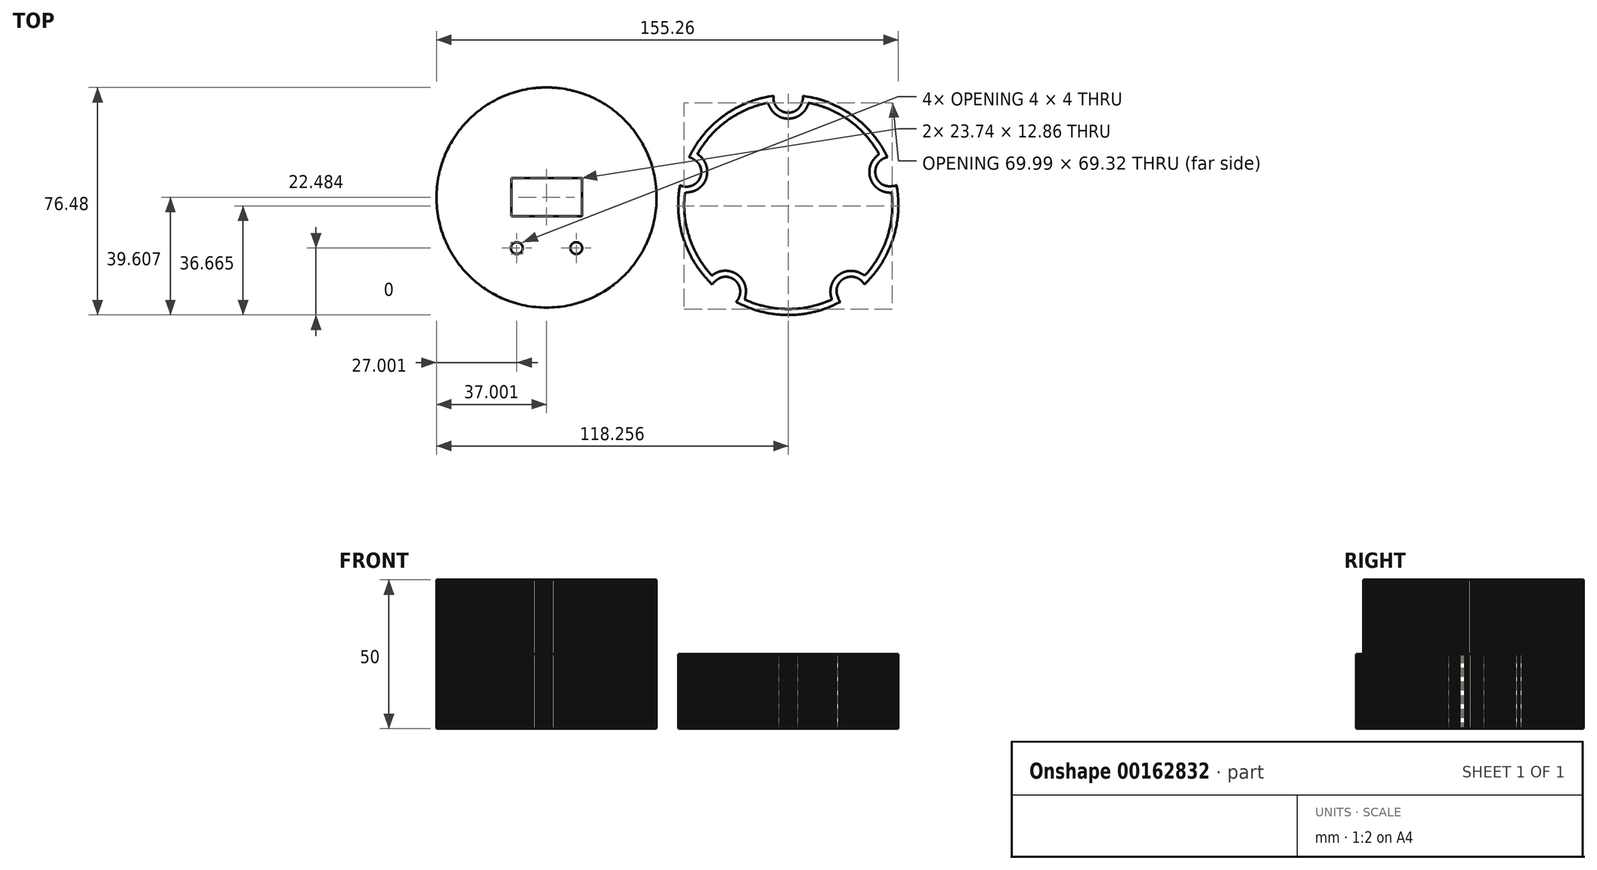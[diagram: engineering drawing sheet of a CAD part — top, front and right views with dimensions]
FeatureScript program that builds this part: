
annotation { "Feature Type Name" : "Feature", "Feature Type Description" : "" }
export const myFeature = defineFeature(function(context is Context, id is Id, definition is map)
    precondition{}
    {
        {
            var Q0;
            Q0=qCreatedBy(makeId("Top.planeOp"),FACE);
            var sketch = newSketch(context, id + "F0", { "sketchPlane" : qUnion([Q0])});
            skLineSegment(sketch, "E0", {"start": v(-51.65, -17.46) * mm, "end": v(-51.74, -17.42) * mm});
            skLineSegment(sketch, "E1", {"start": v(-51.74, -17.42) * mm, "end": v(-51.97, -17.23) * mm});
            skLineSegment(sketch, "E2", {"start": v(-51.97, -17.23) * mm, "end": v(-52.04, -17.17) * mm});
            skLineSegment(sketch, "E3", {"start": v(-52.04, -17.17) * mm, "end": v(-52.1, -17.1) * mm});
            skLineSegment(sketch, "E4", {"start": v(-52.1, -17.1) * mm, "end": v(-52.3, -16.87) * mm});
            skLineSegment(sketch, "E5", {"start": v(-52.3, -16.87) * mm, "end": v(-52.34, -16.78) * mm});
            skLineSegment(sketch, "E6", {"start": v(-52.34, -16.78) * mm, "end": v(-52.48, -16.52) * mm});
            skLineSegment(sketch, "E7", {"start": v(-52.48, -16.52) * mm, "end": v(-52.56, -16.24) * mm});
            skLineSegment(sketch, "E8", {"start": v(-52.56, -16.24) * mm, "end": v(-52.6, -16.15) * mm});
            skLineSegment(sketch, "E9", {"start": v(-52.6, -16.15) * mm, "end": v(-52.62, -15.85) * mm});
            skLineSegment(sketch, "E10", {"start": v(-52.62, -15.85) * mm, "end": v(-52.63, -15.76) * mm});
            skLineSegment(sketch, "E11", {"start": v(-52.63, -15.76) * mm, "end": v(-52.62, -15.66) * mm});
            skLineSegment(sketch, "E12", {"start": v(-52.62, -15.66) * mm, "end": v(-52.6, -15.37) * mm});
            skLineSegment(sketch, "E13", {"start": v(-52.6, -15.37) * mm, "end": v(-52.5, -15.08) * mm});
            skLineSegment(sketch, "E14", {"start": v(-52.5, -15.08) * mm, "end": v(-52.48, -15) * mm});
            skLineSegment(sketch, "E15", {"start": v(-52.48, -15) * mm, "end": v(-52.34, -14.73) * mm});
            skLineSegment(sketch, "E16", {"start": v(-52.34, -14.73) * mm, "end": v(-52.3, -14.64) * mm});
            skLineSegment(sketch, "E17", {"start": v(-52.3, -14.64) * mm, "end": v(-52.23, -14.57) * mm});
            skLineSegment(sketch, "E18", {"start": v(-52.23, -14.57) * mm, "end": v(-52.04, -14.34) * mm});
            skLineSegment(sketch, "E19", {"start": v(-52.04, -14.34) * mm, "end": v(-51.97, -14.28) * mm});
            skLineSegment(sketch, "E20", {"start": v(-51.97, -14.28) * mm, "end": v(-51.74, -14.1) * mm});
            skLineSegment(sketch, "E21", {"start": v(-51.74, -14.1) * mm, "end": v(-51.65, -14.05) * mm});
            skLineSegment(sketch, "E22", {"start": v(-51.65, -14.05) * mm, "end": v(-51.4, -13.9) * mm});
            skLineSegment(sketch, "E23", {"start": v(-51.4, -13.9) * mm, "end": v(-51.3, -13.88) * mm});
            skLineSegment(sketch, "E24", {"start": v(-51.3, -13.88) * mm, "end": v(-51.02, -13.8) * mm});
            skLineSegment(sketch, "E25", {"start": v(-51.02, -13.8) * mm, "end": v(-50.73, -13.77) * mm});
            skLineSegment(sketch, "E26", {"start": v(-50.73, -13.77) * mm, "end": v(-50.63, -13.76) * mm});
            skLineSegment(sketch, "E27", {"start": v(-50.63, -13.76) * mm, "end": v(-50.53, -13.77) * mm});
            skLineSegment(sketch, "E28", {"start": v(-50.53, -13.77) * mm, "end": v(-50.24, -13.8) * mm});
            skLineSegment(sketch, "E29", {"start": v(-50.24, -13.8) * mm, "end": v(-49.96, -13.88) * mm});
            skLineSegment(sketch, "E30", {"start": v(-49.96, -13.88) * mm, "end": v(-49.86, -13.9) * mm});
            skLineSegment(sketch, "E31", {"start": v(-49.86, -13.9) * mm, "end": v(-49.6, -14.05) * mm});
            skLineSegment(sketch, "E32", {"start": v(-49.6, -14.05) * mm, "end": v(-49.52, -14.1) * mm});
            skLineSegment(sketch, "E33", {"start": v(-49.52, -14.1) * mm, "end": v(-49.44, -14.15) * mm});
            skLineSegment(sketch, "E34", {"start": v(-49.44, -14.15) * mm, "end": v(-49.21, -14.34) * mm});
            skLineSegment(sketch, "E35", {"start": v(-49.21, -14.34) * mm, "end": v(-49.15, -14.42) * mm});
            skLineSegment(sketch, "E36", {"start": v(-49.15, -14.42) * mm, "end": v(-48.97, -14.64) * mm});
            skLineSegment(sketch, "E37", {"start": v(-48.97, -14.64) * mm, "end": v(-48.92, -14.73) * mm});
            skLineSegment(sketch, "E38", {"start": v(-48.92, -14.73) * mm, "end": v(-48.78, -15) * mm});
            skLineSegment(sketch, "E39", {"start": v(-48.78, -15) * mm, "end": v(-48.75, -15.08) * mm});
            skLineSegment(sketch, "E40", {"start": v(-48.75, -15.08) * mm, "end": v(-48.67, -15.37) * mm});
            skLineSegment(sketch, "E41", {"start": v(-48.67, -15.37) * mm, "end": v(-48.66, -15.46) * mm});
            skLineSegment(sketch, "E42", {"start": v(-48.66, -15.46) * mm, "end": v(-48.63, -15.76) * mm});
            skLineSegment(sketch, "E43", {"start": v(-48.63, -15.76) * mm, "end": v(-48.64, -15.85) * mm});
            skLineSegment(sketch, "E44", {"start": v(-48.64, -15.85) * mm, "end": v(-48.67, -16.15) * mm});
            skLineSegment(sketch, "E45", {"start": v(-48.67, -16.15) * mm, "end": v(-48.75, -16.43) * mm});
            skLineSegment(sketch, "E46", {"start": v(-48.75, -16.43) * mm, "end": v(-48.78, -16.52) * mm});
            skLineSegment(sketch, "E47", {"start": v(-48.78, -16.52) * mm, "end": v(-48.83, -16.6) * mm});
            skLineSegment(sketch, "E48", {"start": v(-48.83, -16.6) * mm, "end": v(-48.97, -16.87) * mm});
            skLineSegment(sketch, "E49", {"start": v(-48.97, -16.87) * mm, "end": v(-49.03, -16.95) * mm});
            skLineSegment(sketch, "E50", {"start": v(-49.03, -16.95) * mm, "end": v(-49.21, -17.17) * mm});
            skLineSegment(sketch, "E51", {"start": v(-49.21, -17.17) * mm, "end": v(-49.3, -17.23) * mm});
            skLineSegment(sketch, "E52", {"start": v(-49.3, -17.23) * mm, "end": v(-49.52, -17.42) * mm});
            skLineSegment(sketch, "E53", {"start": v(-49.52, -17.42) * mm, "end": v(-49.6, -17.47) * mm});
            skLineSegment(sketch, "E54", {"start": v(-49.6, -17.47) * mm, "end": v(-49.86, -17.6) * mm});
            skLineSegment(sketch, "E55", {"start": v(-49.86, -17.6) * mm, "end": v(-49.96, -17.63) * mm});
            skLineSegment(sketch, "E56", {"start": v(-49.96, -17.63) * mm, "end": v(-50.24, -17.72) * mm});
            skLineSegment(sketch, "E57", {"start": v(-50.24, -17.72) * mm, "end": v(-50.34, -17.73) * mm});
            skLineSegment(sketch, "E58", {"start": v(-50.34, -17.73) * mm, "end": v(-50.63, -17.76) * mm});
            skLineSegment(sketch, "E59", {"start": v(-50.63, -17.76) * mm, "end": v(-50.73, -17.75) * mm});
            skLineSegment(sketch, "E60", {"start": v(-50.73, -17.75) * mm, "end": v(-51.02, -17.72) * mm});
            skLineSegment(sketch, "E61", {"start": v(-51.02, -17.72) * mm, "end": v(-51.3, -17.63) * mm});
            skLineSegment(sketch, "E62", {"start": v(-51.3, -17.63) * mm, "end": v(-51.4, -17.6) * mm});
            skLineSegment(sketch, "E63", {"start": v(-51.4, -17.6) * mm, "end": v(-51.65, -17.46) * mm});
            skLineSegment(sketch, "E64", {"start": v(-31.65, -17.46) * mm, "end": v(-31.74, -17.42) * mm});
            skLineSegment(sketch, "E65", {"start": v(-31.74, -17.42) * mm, "end": v(-31.97, -17.23) * mm});
            skLineSegment(sketch, "E66", {"start": v(-31.97, -17.23) * mm, "end": v(-32.04, -17.17) * mm});
            skLineSegment(sketch, "E67", {"start": v(-32.04, -17.17) * mm, "end": v(-32.23, -16.95) * mm});
            skLineSegment(sketch, "E68", {"start": v(-32.23, -16.95) * mm, "end": v(-32.29, -16.87) * mm});
            skLineSegment(sketch, "E69", {"start": v(-32.29, -16.87) * mm, "end": v(-32.43, -16.6) * mm});
            skLineSegment(sketch, "E70", {"start": v(-32.43, -16.6) * mm, "end": v(-32.48, -16.52) * mm});
            skLineSegment(sketch, "E71", {"start": v(-32.48, -16.52) * mm, "end": v(-32.5, -16.43) * mm});
            skLineSegment(sketch, "E72", {"start": v(-32.5, -16.43) * mm, "end": v(-32.6, -16.15) * mm});
            skLineSegment(sketch, "E73", {"start": v(-32.6, -16.15) * mm, "end": v(-32.62, -15.85) * mm});
            skLineSegment(sketch, "E74", {"start": v(-32.62, -15.85) * mm, "end": v(-32.63, -15.76) * mm});
            skLineSegment(sketch, "E75", {"start": v(-32.63, -15.76) * mm, "end": v(-32.6, -15.46) * mm});
            skLineSegment(sketch, "E76", {"start": v(-32.6, -15.46) * mm, "end": v(-32.6, -15.37) * mm});
            skLineSegment(sketch, "E77", {"start": v(-32.6, -15.37) * mm, "end": v(-32.5, -15.08) * mm});
            skLineSegment(sketch, "E78", {"start": v(-32.5, -15.08) * mm, "end": v(-32.48, -15) * mm});
            skLineSegment(sketch, "E79", {"start": v(-32.48, -15) * mm, "end": v(-32.34, -14.73) * mm});
            skLineSegment(sketch, "E80", {"start": v(-32.34, -14.73) * mm, "end": v(-32.3, -14.64) * mm});
            skLineSegment(sketch, "E81", {"start": v(-32.3, -14.64) * mm, "end": v(-32.23, -14.57) * mm});
            skLineSegment(sketch, "E82", {"start": v(-32.23, -14.57) * mm, "end": v(-32.04, -14.34) * mm});
            skLineSegment(sketch, "E83", {"start": v(-32.04, -14.34) * mm, "end": v(-31.82, -14.15) * mm});
            skLineSegment(sketch, "E84", {"start": v(-31.82, -14.15) * mm, "end": v(-31.74, -14.1) * mm});
            skLineSegment(sketch, "E85", {"start": v(-31.74, -14.1) * mm, "end": v(-31.65, -14.05) * mm});
            skLineSegment(sketch, "E86", {"start": v(-31.65, -14.05) * mm, "end": v(-31.4, -13.9) * mm});
            skLineSegment(sketch, "E87", {"start": v(-31.4, -13.9) * mm, "end": v(-31.3, -13.88) * mm});
            skLineSegment(sketch, "E88", {"start": v(-31.3, -13.88) * mm, "end": v(-31.02, -13.8) * mm});
            skLineSegment(sketch, "E89", {"start": v(-31.02, -13.8) * mm, "end": v(-30.73, -13.77) * mm});
            skLineSegment(sketch, "E90", {"start": v(-30.73, -13.77) * mm, "end": v(-30.63, -13.76) * mm});
            skLineSegment(sketch, "E91", {"start": v(-30.63, -13.76) * mm, "end": v(-30.53, -13.77) * mm});
            skLineSegment(sketch, "E92", {"start": v(-30.53, -13.77) * mm, "end": v(-30.24, -13.8) * mm});
            skLineSegment(sketch, "E93", {"start": v(-30.24, -13.8) * mm, "end": v(-29.96, -13.88) * mm});
            skLineSegment(sketch, "E94", {"start": v(-29.96, -13.88) * mm, "end": v(-29.86, -13.9) * mm});
            skLineSegment(sketch, "E95", {"start": v(-29.86, -13.9) * mm, "end": v(-29.6, -14.05) * mm});
            skLineSegment(sketch, "E96", {"start": v(-29.6, -14.05) * mm, "end": v(-29.52, -14.1) * mm});
            skLineSegment(sketch, "E97", {"start": v(-29.52, -14.1) * mm, "end": v(-29.44, -14.15) * mm});
            skLineSegment(sketch, "E98", {"start": v(-29.44, -14.15) * mm, "end": v(-29.21, -14.34) * mm});
            skLineSegment(sketch, "E99", {"start": v(-29.21, -14.34) * mm, "end": v(-29.03, -14.57) * mm});
            skLineSegment(sketch, "E100", {"start": v(-29.03, -14.57) * mm, "end": v(-28.97, -14.64) * mm});
            skLineSegment(sketch, "E101", {"start": v(-28.97, -14.64) * mm, "end": v(-28.92, -14.73) * mm});
            skLineSegment(sketch, "E102", {"start": v(-28.92, -14.73) * mm, "end": v(-28.78, -15) * mm});
            skLineSegment(sketch, "E103", {"start": v(-28.78, -15) * mm, "end": v(-28.75, -15.08) * mm});
            skLineSegment(sketch, "E104", {"start": v(-28.75, -15.08) * mm, "end": v(-28.67, -15.37) * mm});
            skLineSegment(sketch, "E105", {"start": v(-28.67, -15.37) * mm, "end": v(-28.64, -15.66) * mm});
            skLineSegment(sketch, "E106", {"start": v(-28.64, -15.66) * mm, "end": v(-28.63, -15.76) * mm});
            skLineSegment(sketch, "E107", {"start": v(-28.63, -15.76) * mm, "end": v(-28.66, -16.05) * mm});
            skLineSegment(sketch, "E108", {"start": v(-28.66, -16.05) * mm, "end": v(-28.67, -16.15) * mm});
            skLineSegment(sketch, "E109", {"start": v(-28.67, -16.15) * mm, "end": v(-28.75, -16.43) * mm});
            skLineSegment(sketch, "E110", {"start": v(-28.75, -16.43) * mm, "end": v(-28.78, -16.52) * mm});
            skLineSegment(sketch, "E111", {"start": v(-28.78, -16.52) * mm, "end": v(-28.92, -16.78) * mm});
            skLineSegment(sketch, "E112", {"start": v(-28.92, -16.78) * mm, "end": v(-28.97, -16.87) * mm});
            skLineSegment(sketch, "E113", {"start": v(-28.97, -16.87) * mm, "end": v(-29.03, -16.94) * mm});
            skLineSegment(sketch, "E114", {"start": v(-29.03, -16.94) * mm, "end": v(-29.21, -17.17) * mm});
            skLineSegment(sketch, "E115", {"start": v(-29.21, -17.17) * mm, "end": v(-29.3, -17.23) * mm});
            skLineSegment(sketch, "E116", {"start": v(-29.3, -17.23) * mm, "end": v(-29.52, -17.42) * mm});
            skLineSegment(sketch, "E117", {"start": v(-29.52, -17.42) * mm, "end": v(-29.6, -17.46) * mm});
            skLineSegment(sketch, "E118", {"start": v(-29.6, -17.46) * mm, "end": v(-29.86, -17.6) * mm});
            skLineSegment(sketch, "E119", {"start": v(-29.86, -17.6) * mm, "end": v(-29.96, -17.63) * mm});
            skLineSegment(sketch, "E120", {"start": v(-29.96, -17.63) * mm, "end": v(-30.24, -17.72) * mm});
            skLineSegment(sketch, "E121", {"start": v(-30.24, -17.72) * mm, "end": v(-30.53, -17.75) * mm});
            skLineSegment(sketch, "E122", {"start": v(-30.53, -17.75) * mm, "end": v(-30.63, -17.76) * mm});
            skLineSegment(sketch, "E123", {"start": v(-30.63, -17.76) * mm, "end": v(-30.73, -17.75) * mm});
            skLineSegment(sketch, "E124", {"start": v(-30.73, -17.75) * mm, "end": v(-31.02, -17.72) * mm});
            skLineSegment(sketch, "E125", {"start": v(-31.02, -17.72) * mm, "end": v(-31.3, -17.63) * mm});
            skLineSegment(sketch, "E126", {"start": v(-31.3, -17.63) * mm, "end": v(-31.4, -17.6) * mm});
            skLineSegment(sketch, "E127", {"start": v(-31.4, -17.6) * mm, "end": v(-31.65, -17.46) * mm});
            skLineSegment(sketch, "E128", {"start": v(-28.76, 4.59) * mm, "end": v(-28.76, -5.07) * mm});
            skLineSegment(sketch, "E129", {"start": v(-28.76, -5.07) * mm, "end": v(-34.69, -5.07) * mm});
            skLineSegment(sketch, "E130", {"start": v(-34.69, -5.07) * mm, "end": v(-52.5, -5.07) * mm});
            skLineSegment(sketch, "E131", {"start": v(-52.5, -5.07) * mm, "end": v(-52.5, -1.85) * mm});
            skLineSegment(sketch, "E132", {"start": v(-52.5, -1.85) * mm, "end": v(-52.5, 7.8) * mm});
            skLineSegment(sketch, "E133", {"start": v(-52.5, 7.8) * mm, "end": v(-46.57, 7.8) * mm});
            skLineSegment(sketch, "E134", {"start": v(-46.57, 7.8) * mm, "end": v(-28.76, 7.8) * mm});
            skLineSegment(sketch, "E135", {"start": v(-28.76, 7.8) * mm, "end": v(-28.76, 4.59) * mm});
            skLineSegment(sketch, "E136", {"start": v(-68.54, -23.04) * mm, "end": v(-68, -23.65) * mm});
            skLineSegment(sketch, "E137", {"start": v(-68, -23.65) * mm, "end": v(-67.45, -24.25) * mm});
            skLineSegment(sketch, "E138", {"start": v(-67.45, -24.25) * mm, "end": v(-67.43, -24.27) * mm});
            skLineSegment(sketch, "E139", {"start": v(-67.43, -24.27) * mm, "end": v(-67.36, -24.34) * mm});
            skLineSegment(sketch, "E140", {"start": v(-67.36, -24.34) * mm, "end": v(-66.8, -24.92) * mm});
            skLineSegment(sketch, "E141", {"start": v(-66.8, -24.92) * mm, "end": v(-66.72, -25) * mm});
            skLineSegment(sketch, "E142", {"start": v(-66.72, -25) * mm, "end": v(-66.14, -25.55) * mm});
            skLineSegment(sketch, "E143", {"start": v(-66.14, -25.55) * mm, "end": v(-66.06, -25.63) * mm});
            skLineSegment(sketch, "E144", {"start": v(-66.06, -25.63) * mm, "end": v(-65.48, -26.17) * mm});
            skLineSegment(sketch, "E145", {"start": v(-65.48, -26.17) * mm, "end": v(-65.4, -26.24) * mm});
            skLineSegment(sketch, "E146", {"start": v(-65.4, -26.24) * mm, "end": v(-64.8, -26.77) * mm});
            skLineSegment(sketch, "E147", {"start": v(-64.8, -26.77) * mm, "end": v(-64.71, -26.84) * mm});
            skLineSegment(sketch, "E148", {"start": v(-64.71, -26.84) * mm, "end": v(-64.1, -27.36) * mm});
            skLineSegment(sketch, "E149", {"start": v(-64.1, -27.36) * mm, "end": v(-64.01, -27.43) * mm});
            skLineSegment(sketch, "E150", {"start": v(-64.01, -27.43) * mm, "end": v(-63.4, -27.92) * mm});
            skLineSegment(sketch, "E151", {"start": v(-63.4, -27.92) * mm, "end": v(-63.3, -28) * mm});
            skLineSegment(sketch, "E152", {"start": v(-63.3, -28) * mm, "end": v(-62.67, -28.47) * mm});
            skLineSegment(sketch, "E153", {"start": v(-62.67, -28.47) * mm, "end": v(-62.58, -28.54) * mm});
            skLineSegment(sketch, "E154", {"start": v(-62.58, -28.54) * mm, "end": v(-61.93, -29) * mm});
            skLineSegment(sketch, "E155", {"start": v(-61.93, -29) * mm, "end": v(-61.28, -29.46) * mm});
            skLineSegment(sketch, "E156", {"start": v(-61.28, -29.46) * mm, "end": v(-61.19, -29.52) * mm});
            skLineSegment(sketch, "E157", {"start": v(-61.19, -29.52) * mm, "end": v(-60.52, -29.95) * mm});
            skLineSegment(sketch, "E158", {"start": v(-60.52, -29.95) * mm, "end": v(-60.42, -30.02) * mm});
            skLineSegment(sketch, "E159", {"start": v(-60.42, -30.02) * mm, "end": v(-59.75, -30.43) * mm});
            skLineSegment(sketch, "E160", {"start": v(-59.75, -30.43) * mm, "end": v(-59.65, -30.5) * mm});
            skLineSegment(sketch, "E161", {"start": v(-59.65, -30.5) * mm, "end": v(-58.96, -30.9) * mm});
            skLineSegment(sketch, "E162", {"start": v(-58.96, -30.9) * mm, "end": v(-58.87, -30.95) * mm});
            skLineSegment(sketch, "E163", {"start": v(-58.87, -30.95) * mm, "end": v(-58.16, -31.34) * mm});
            skLineSegment(sketch, "E164", {"start": v(-58.16, -31.34) * mm, "end": v(-58.07, -31.39) * mm});
            skLineSegment(sketch, "E165", {"start": v(-58.07, -31.39) * mm, "end": v(-57.36, -31.76) * mm});
            skLineSegment(sketch, "E166", {"start": v(-57.36, -31.76) * mm, "end": v(-57.26, -31.8) * mm});
            skLineSegment(sketch, "E167", {"start": v(-57.26, -31.8) * mm, "end": v(-56.54, -32.16) * mm});
            skLineSegment(sketch, "E168", {"start": v(-56.54, -32.16) * mm, "end": v(-56.45, -32.2) * mm});
            skLineSegment(sketch, "E169", {"start": v(-56.45, -32.2) * mm, "end": v(-56.44, -32.2) * mm});
            skLineSegment(sketch, "E170", {"start": v(-56.44, -32.2) * mm, "end": v(-55.7, -32.55) * mm});
            skLineSegment(sketch, "E171", {"start": v(-55.7, -32.55) * mm, "end": v(-55.62, -32.58) * mm});
            skLineSegment(sketch, "E172", {"start": v(-55.62, -32.58) * mm, "end": v(-55.6, -32.59) * mm});
            skLineSegment(sketch, "E173", {"start": v(-55.6, -32.59) * mm, "end": v(-54.79, -32.94) * mm});
            skLineSegment(sketch, "E174", {"start": v(-54.79, -32.94) * mm, "end": v(-53.96, -33.27) * mm});
            skLineSegment(sketch, "E175", {"start": v(-53.96, -33.27) * mm, "end": v(-53.94, -33.28) * mm});
            skLineSegment(sketch, "E176", {"start": v(-53.94, -33.28) * mm, "end": v(-53.1, -33.59) * mm});
            skLineSegment(sketch, "E177", {"start": v(-53.1, -33.59) * mm, "end": v(-53.1, -33.6) * mm});
            skLineSegment(sketch, "E178", {"start": v(-53.1, -33.6) * mm, "end": v(-53.08, -33.6) * mm});
            skLineSegment(sketch, "E179", {"start": v(-53.08, -33.6) * mm, "end": v(-52.23, -33.89) * mm});
            skLineSegment(sketch, "E180", {"start": v(-52.23, -33.89) * mm, "end": v(-51.38, -34.16) * mm});
            skLineSegment(sketch, "E181", {"start": v(-51.38, -34.16) * mm, "end": v(-51.37, -34.16) * mm});
            skLineSegment(sketch, "E182", {"start": v(-51.37, -34.16) * mm, "end": v(-50.51, -34.41) * mm});
            skLineSegment(sketch, "E183", {"start": v(-50.51, -34.41) * mm, "end": v(-50.5, -34.42) * mm});
            skLineSegment(sketch, "E184", {"start": v(-50.5, -34.42) * mm, "end": v(-49.63, -34.64) * mm});
            skLineSegment(sketch, "E185", {"start": v(-49.63, -34.64) * mm, "end": v(-49.62, -34.65) * mm});
            skLineSegment(sketch, "E186", {"start": v(-49.62, -34.65) * mm, "end": v(-48.75, -34.85) * mm});
            skLineSegment(sketch, "E187", {"start": v(-48.75, -34.85) * mm, "end": v(-48.74, -34.86) * mm});
            skLineSegment(sketch, "E188", {"start": v(-48.74, -34.86) * mm, "end": v(-47.86, -35.04) * mm});
            skLineSegment(sketch, "E189", {"start": v(-47.86, -35.04) * mm, "end": v(-47.85, -35.04) * mm});
            skLineSegment(sketch, "E190", {"start": v(-47.85, -35.04) * mm, "end": v(-47.83, -35.05) * mm});
            skLineSegment(sketch, "E191", {"start": v(-47.83, -35.05) * mm, "end": v(-46.95, -35.21) * mm});
            skLineSegment(sketch, "E192", {"start": v(-46.95, -35.21) * mm, "end": v(-46.94, -35.21) * mm});
            skLineSegment(sketch, "E193", {"start": v(-46.94, -35.21) * mm, "end": v(-46.06, -35.36) * mm});
            skLineSegment(sketch, "E194", {"start": v(-46.06, -35.36) * mm, "end": v(-46.04, -35.36) * mm});
            skLineSegment(sketch, "E195", {"start": v(-46.04, -35.36) * mm, "end": v(-45.16, -35.48) * mm});
            skLineSegment(sketch, "E196", {"start": v(-45.16, -35.48) * mm, "end": v(-45.14, -35.48) * mm});
            skLineSegment(sketch, "E197", {"start": v(-45.14, -35.48) * mm, "end": v(-44.26, -35.58) * mm});
            skLineSegment(sketch, "E198", {"start": v(-44.26, -35.58) * mm, "end": v(-44.24, -35.58) * mm});
            skLineSegment(sketch, "E199", {"start": v(-44.24, -35.58) * mm, "end": v(-43.35, -35.66) * mm});
            skLineSegment(sketch, "E200", {"start": v(-43.35, -35.66) * mm, "end": v(-42.46, -35.71) * mm});
            skLineSegment(sketch, "E201", {"start": v(-42.46, -35.71) * mm, "end": v(-42.44, -35.71) * mm});
            skLineSegment(sketch, "E202", {"start": v(-42.44, -35.71) * mm, "end": v(-41.55, -35.74) * mm});
            skLineSegment(sketch, "E203", {"start": v(-41.55, -35.74) * mm, "end": v(-41.54, -35.74) * mm});
            skLineSegment(sketch, "E204", {"start": v(-41.54, -35.74) * mm, "end": v(-41.52, -35.74) * mm});
            skLineSegment(sketch, "E205", {"start": v(-41.52, -35.74) * mm, "end": v(-40.63, -35.76) * mm});
            skLineSegment(sketch, "E206", {"start": v(-40.63, -35.76) * mm, "end": v(-39.74, -35.74) * mm});
            skLineSegment(sketch, "E207", {"start": v(-39.74, -35.74) * mm, "end": v(-39.72, -35.74) * mm});
            skLineSegment(sketch, "E208", {"start": v(-39.72, -35.74) * mm, "end": v(-39.7, -35.74) * mm});
            skLineSegment(sketch, "E209", {"start": v(-39.7, -35.74) * mm, "end": v(-38.81, -35.71) * mm});
            skLineSegment(sketch, "E210", {"start": v(-38.81, -35.71) * mm, "end": v(-38.8, -35.71) * mm});
            skLineSegment(sketch, "E211", {"start": v(-38.8, -35.71) * mm, "end": v(-37.9, -35.66) * mm});
            skLineSegment(sketch, "E212", {"start": v(-37.9, -35.66) * mm, "end": v(-37.9, -35.65) * mm});
            skLineSegment(sketch, "E213", {"start": v(-37.9, -35.65) * mm, "end": v(-37, -35.58) * mm});
            skLineSegment(sketch, "E214", {"start": v(-37, -35.58) * mm, "end": v(-36.99, -35.58) * mm});
            skLineSegment(sketch, "E215", {"start": v(-36.99, -35.58) * mm, "end": v(-36.1, -35.48) * mm});
            skLineSegment(sketch, "E216", {"start": v(-36.1, -35.48) * mm, "end": v(-36.08, -35.48) * mm});
            skLineSegment(sketch, "E217", {"start": v(-36.08, -35.48) * mm, "end": v(-35.2, -35.36) * mm});
            skLineSegment(sketch, "E218", {"start": v(-35.2, -35.36) * mm, "end": v(-35.18, -35.35) * mm});
            skLineSegment(sketch, "E219", {"start": v(-35.18, -35.35) * mm, "end": v(-34.3, -35.21) * mm});
            skLineSegment(sketch, "E220", {"start": v(-34.3, -35.21) * mm, "end": v(-34.29, -35.2) * mm});
            skLineSegment(sketch, "E221", {"start": v(-34.29, -35.2) * mm, "end": v(-33.41, -35.04) * mm});
            skLineSegment(sketch, "E222", {"start": v(-33.41, -35.04) * mm, "end": v(-33.4, -35.04) * mm});
            skLineSegment(sketch, "E223", {"start": v(-33.4, -35.04) * mm, "end": v(-32.52, -34.86) * mm});
            skLineSegment(sketch, "E224", {"start": v(-32.52, -34.86) * mm, "end": v(-32.5, -34.85) * mm});
            skLineSegment(sketch, "E225", {"start": v(-32.5, -34.85) * mm, "end": v(-31.64, -34.65) * mm});
            skLineSegment(sketch, "E226", {"start": v(-31.64, -34.65) * mm, "end": v(-30.78, -34.42) * mm});
            skLineSegment(sketch, "E227", {"start": v(-30.78, -34.42) * mm, "end": v(-30.76, -34.42) * mm});
            skLineSegment(sketch, "E228", {"start": v(-30.76, -34.42) * mm, "end": v(-30.75, -34.41) * mm});
            skLineSegment(sketch, "E229", {"start": v(-30.75, -34.41) * mm, "end": v(-29.89, -34.16) * mm});
            skLineSegment(sketch, "E230", {"start": v(-29.89, -34.16) * mm, "end": v(-29.87, -34.16) * mm});
            skLineSegment(sketch, "E231", {"start": v(-29.87, -34.16) * mm, "end": v(-29.87, -34.16) * mm});
            skLineSegment(sketch, "E232", {"start": v(-29.87, -34.16) * mm, "end": v(-29.02, -33.89) * mm});
            skLineSegment(sketch, "E233", {"start": v(-29.02, -33.89) * mm, "end": v(-29.02, -33.89) * mm});
            skLineSegment(sketch, "E234", {"start": v(-29.02, -33.89) * mm, "end": v(-29, -33.88) * mm});
            skLineSegment(sketch, "E235", {"start": v(-29, -33.88) * mm, "end": v(-29, -33.88) * mm});
            skLineSegment(sketch, "E236", {"start": v(-29, -33.88) * mm, "end": v(-28.16, -33.6) * mm});
            skLineSegment(sketch, "E237", {"start": v(-28.16, -33.6) * mm, "end": v(-28.16, -33.6) * mm});
            skLineSegment(sketch, "E238", {"start": v(-28.16, -33.6) * mm, "end": v(-28.15, -33.59) * mm});
            skLineSegment(sketch, "E239", {"start": v(-28.15, -33.59) * mm, "end": v(-27.31, -33.28) * mm});
            skLineSegment(sketch, "E240", {"start": v(-27.31, -33.28) * mm, "end": v(-27.31, -33.28) * mm});
            skLineSegment(sketch, "E241", {"start": v(-27.31, -33.28) * mm, "end": v(-26.48, -32.95) * mm});
            skLineSegment(sketch, "E242", {"start": v(-26.48, -32.95) * mm, "end": v(-26.3, -32.87) * mm});
            skLineSegment(sketch, "E243", {"start": v(-26.3, -32.87) * mm, "end": v(-25.56, -32.55) * mm});
            skLineSegment(sketch, "E244", {"start": v(-25.56, -32.55) * mm, "end": v(-24.82, -32.2) * mm});
            skLineSegment(sketch, "E245", {"start": v(-24.82, -32.2) * mm, "end": v(-24.8, -32.2) * mm});
            skLineSegment(sketch, "E246", {"start": v(-24.8, -32.2) * mm, "end": v(-24.72, -32.16) * mm});
            skLineSegment(sketch, "E247", {"start": v(-24.72, -32.16) * mm, "end": v(-24, -31.8) * mm});
            skLineSegment(sketch, "E248", {"start": v(-24, -31.8) * mm, "end": v(-23.9, -31.76) * mm});
            skLineSegment(sketch, "E249", {"start": v(-23.9, -31.76) * mm, "end": v(-23.19, -31.39) * mm});
            skLineSegment(sketch, "E250", {"start": v(-23.19, -31.39) * mm, "end": v(-23.1, -31.34) * mm});
            skLineSegment(sketch, "E251", {"start": v(-23.1, -31.34) * mm, "end": v(-22.4, -30.95) * mm});
            skLineSegment(sketch, "E252", {"start": v(-22.4, -30.95) * mm, "end": v(-22.3, -30.9) * mm});
            skLineSegment(sketch, "E253", {"start": v(-22.3, -30.9) * mm, "end": v(-21.6, -30.5) * mm});
            skLineSegment(sketch, "E254", {"start": v(-21.6, -30.5) * mm, "end": v(-21.51, -30.43) * mm});
            skLineSegment(sketch, "E255", {"start": v(-21.51, -30.43) * mm, "end": v(-20.83, -30.02) * mm});
            skLineSegment(sketch, "E256", {"start": v(-20.83, -30.02) * mm, "end": v(-20.74, -29.95) * mm});
            skLineSegment(sketch, "E257", {"start": v(-20.74, -29.95) * mm, "end": v(-20.07, -29.52) * mm});
            skLineSegment(sketch, "E258", {"start": v(-20.07, -29.52) * mm, "end": v(-19.98, -29.46) * mm});
            skLineSegment(sketch, "E259", {"start": v(-19.98, -29.46) * mm, "end": v(-19.32, -29) * mm});
            skLineSegment(sketch, "E260", {"start": v(-19.32, -29) * mm, "end": v(-19.23, -28.94) * mm});
            skLineSegment(sketch, "E261", {"start": v(-19.23, -28.94) * mm, "end": v(-18.59, -28.47) * mm});
            skLineSegment(sketch, "E262", {"start": v(-18.59, -28.47) * mm, "end": v(-17.95, -28) * mm});
            skLineSegment(sketch, "E263", {"start": v(-17.95, -28) * mm, "end": v(-17.87, -27.92) * mm});
            skLineSegment(sketch, "E264", {"start": v(-17.87, -27.92) * mm, "end": v(-17.24, -27.43) * mm});
            skLineSegment(sketch, "E265", {"start": v(-17.24, -27.43) * mm, "end": v(-17.16, -27.36) * mm});
            skLineSegment(sketch, "E266", {"start": v(-17.16, -27.36) * mm, "end": v(-16.55, -26.84) * mm});
            skLineSegment(sketch, "E267", {"start": v(-16.55, -26.84) * mm, "end": v(-16.46, -26.77) * mm});
            skLineSegment(sketch, "E268", {"start": v(-16.46, -26.77) * mm, "end": v(-15.86, -26.24) * mm});
            skLineSegment(sketch, "E269", {"start": v(-15.86, -26.24) * mm, "end": v(-15.78, -26.17) * mm});
            skLineSegment(sketch, "E270", {"start": v(-15.78, -26.17) * mm, "end": v(-15.2, -25.63) * mm});
            skLineSegment(sketch, "E271", {"start": v(-15.2, -25.63) * mm, "end": v(-15.12, -25.55) * mm});
            skLineSegment(sketch, "E272", {"start": v(-15.12, -25.55) * mm, "end": v(-14.54, -25) * mm});
            skLineSegment(sketch, "E273", {"start": v(-14.54, -25) * mm, "end": v(-14.47, -24.92) * mm});
            skLineSegment(sketch, "E274", {"start": v(-14.47, -24.92) * mm, "end": v(-13.9, -24.34) * mm});
            skLineSegment(sketch, "E275", {"start": v(-13.9, -24.34) * mm, "end": v(-13.83, -24.27) * mm});
            skLineSegment(sketch, "E276", {"start": v(-13.83, -24.27) * mm, "end": v(-13.8, -24.24) * mm});
            skLineSegment(sketch, "E277", {"start": v(-13.8, -24.24) * mm, "end": v(-13.26, -23.65) * mm});
            skLineSegment(sketch, "E278", {"start": v(-13.26, -23.65) * mm, "end": v(-12.72, -23.04) * mm});
            skLineSegment(sketch, "E279", {"start": v(-12.72, -23.04) * mm, "end": v(-12.61, -22.92) * mm});
            skLineSegment(sketch, "E280", {"start": v(-12.61, -22.92) * mm, "end": v(-12.04, -22.24) * mm});
            skLineSegment(sketch, "E281", {"start": v(-12.04, -22.24) * mm, "end": v(-12.03, -22.23) * mm});
            skLineSegment(sketch, "E282", {"start": v(-12.03, -22.23) * mm, "end": v(-11.47, -21.53) * mm});
            skLineSegment(sketch, "E283", {"start": v(-11.47, -21.53) * mm, "end": v(-11.46, -21.52) * mm});
            skLineSegment(sketch, "E284", {"start": v(-11.46, -21.52) * mm, "end": v(-10.92, -20.8) * mm});
            skLineSegment(sketch, "E285", {"start": v(-10.92, -20.8) * mm, "end": v(-10.91, -20.8) * mm});
            skLineSegment(sketch, "E286", {"start": v(-10.91, -20.8) * mm, "end": v(-10.39, -20.07) * mm});
            skLineSegment(sketch, "E287", {"start": v(-10.39, -20.07) * mm, "end": v(-10.38, -20.06) * mm});
            skLineSegment(sketch, "E288", {"start": v(-10.38, -20.06) * mm, "end": v(-9.87, -19.32) * mm});
            skLineSegment(sketch, "E289", {"start": v(-9.87, -19.32) * mm, "end": v(-9.86, -19.31) * mm});
            skLineSegment(sketch, "E290", {"start": v(-9.86, -19.31) * mm, "end": v(-9.38, -18.56) * mm});
            skLineSegment(sketch, "E291", {"start": v(-9.38, -18.56) * mm, "end": v(-9.37, -18.55) * mm});
            skLineSegment(sketch, "E292", {"start": v(-9.37, -18.55) * mm, "end": v(-8.9, -17.8) * mm});
            skLineSegment(sketch, "E293", {"start": v(-8.9, -17.8) * mm, "end": v(-8.9, -17.78) * mm});
            skLineSegment(sketch, "E294", {"start": v(-8.9, -17.78) * mm, "end": v(-8.44, -17) * mm});
            skLineSegment(sketch, "E295", {"start": v(-8.44, -17) * mm, "end": v(-8.44, -17) * mm});
            skLineSegment(sketch, "E296", {"start": v(-8.44, -17) * mm, "end": v(-8, -16.21) * mm});
            skLineSegment(sketch, "E297", {"start": v(-8, -16.21) * mm, "end": v(-8, -16.2) * mm});
            skLineSegment(sketch, "E298", {"start": v(-8, -16.2) * mm, "end": v(-8, -16.18) * mm});
            skLineSegment(sketch, "E299", {"start": v(-8, -16.18) * mm, "end": v(-7.58, -15.4) * mm});
            skLineSegment(sketch, "E300", {"start": v(-7.58, -15.4) * mm, "end": v(-7.19, -14.59) * mm});
            skLineSegment(sketch, "E301", {"start": v(-7.19, -14.59) * mm, "end": v(-7.18, -14.58) * mm});
            skLineSegment(sketch, "E302", {"start": v(-7.18, -14.58) * mm, "end": v(-6.8, -13.76) * mm});
            skLineSegment(sketch, "E303", {"start": v(-6.8, -13.76) * mm, "end": v(-6.8, -13.75) * mm});
            skLineSegment(sketch, "E304", {"start": v(-6.8, -13.75) * mm, "end": v(-6.45, -12.93) * mm});
            skLineSegment(sketch, "E305", {"start": v(-6.45, -12.93) * mm, "end": v(-6.45, -12.92) * mm});
            skLineSegment(sketch, "E306", {"start": v(-6.45, -12.92) * mm, "end": v(-6.44, -12.9) * mm});
            skLineSegment(sketch, "E307", {"start": v(-6.44, -12.9) * mm, "end": v(-6.1, -12.07) * mm});
            skLineSegment(sketch, "E308", {"start": v(-6.1, -12.07) * mm, "end": v(-6.1, -12.06) * mm});
            skLineSegment(sketch, "E309", {"start": v(-6.1, -12.06) * mm, "end": v(-5.8, -11.22) * mm});
            skLineSegment(sketch, "E310", {"start": v(-5.8, -11.22) * mm, "end": v(-5.5, -10.38) * mm});
            skLineSegment(sketch, "E311", {"start": v(-5.5, -10.38) * mm, "end": v(-5.5, -10.36) * mm});
            skLineSegment(sketch, "E312", {"start": v(-5.5, -10.36) * mm, "end": v(-5.23, -9.51) * mm});
            skLineSegment(sketch, "E313", {"start": v(-5.23, -9.51) * mm, "end": v(-5.22, -9.5) * mm});
            skLineSegment(sketch, "E314", {"start": v(-5.22, -9.5) * mm, "end": v(-5.22, -9.48) * mm});
            skLineSegment(sketch, "E315", {"start": v(-5.22, -9.48) * mm, "end": v(-4.97, -8.62) * mm});
            skLineSegment(sketch, "E316", {"start": v(-4.97, -8.62) * mm, "end": v(-4.97, -8.6) * mm});
            skLineSegment(sketch, "E317", {"start": v(-4.97, -8.6) * mm, "end": v(-4.74, -7.75) * mm});
            skLineSegment(sketch, "E318", {"start": v(-4.74, -7.75) * mm, "end": v(-4.53, -6.88) * mm});
            skLineSegment(sketch, "E319", {"start": v(-4.53, -6.88) * mm, "end": v(-4.53, -6.86) * mm});
            skLineSegment(sketch, "E320", {"start": v(-4.53, -6.86) * mm, "end": v(-4.34, -5.99) * mm});
            skLineSegment(sketch, "E321", {"start": v(-4.34, -5.99) * mm, "end": v(-4.34, -5.97) * mm});
            skLineSegment(sketch, "E322", {"start": v(-4.34, -5.97) * mm, "end": v(-4.34, -5.96) * mm});
            skLineSegment(sketch, "E323", {"start": v(-4.34, -5.96) * mm, "end": v(-4.17, -5.08) * mm});
            skLineSegment(sketch, "E324", {"start": v(-4.17, -5.08) * mm, "end": v(-4.03, -4.2) * mm});
            skLineSegment(sketch, "E325", {"start": v(-4.03, -4.2) * mm, "end": v(-4.03, -4.18) * mm});
            skLineSegment(sketch, "E326", {"start": v(-4.03, -4.18) * mm, "end": v(-3.9, -3.3) * mm});
            skLineSegment(sketch, "E327", {"start": v(-3.9, -3.3) * mm, "end": v(-3.9, -3.28) * mm});
            skLineSegment(sketch, "E328", {"start": v(-3.9, -3.28) * mm, "end": v(-3.9, -3.27) * mm});
            skLineSegment(sketch, "E329", {"start": v(-3.9, -3.27) * mm, "end": v(-3.8, -2.38) * mm});
            skLineSegment(sketch, "E330", {"start": v(-3.8, -2.38) * mm, "end": v(-3.8, -2.37) * mm});
            skLineSegment(sketch, "E331", {"start": v(-3.8, -2.37) * mm, "end": v(-3.73, -1.48) * mm});
            skLineSegment(sketch, "E332", {"start": v(-3.73, -1.48) * mm, "end": v(-3.67, -0.59) * mm});
            skLineSegment(sketch, "E333", {"start": v(-3.67, -0.59) * mm, "end": v(-3.67, -0.54) * mm});
            skLineSegment(sketch, "E334", {"start": v(-3.67, -0.54) * mm, "end": v(-3.64, 0.35) * mm});
            skLineSegment(sketch, "E335", {"start": v(-3.64, 0.35) * mm, "end": v(-3.63, 1.24) * mm});
            skLineSegment(sketch, "E336", {"start": v(-3.63, 1.24) * mm, "end": v(-3.63, 1.25) * mm});
            skLineSegment(sketch, "E337", {"start": v(-3.63, 1.25) * mm, "end": v(-3.63, 1.25) * mm});
            skLineSegment(sketch, "E338", {"start": v(-3.63, 1.25) * mm, "end": v(-3.63, 1.26) * mm});
            skLineSegment(sketch, "E339", {"start": v(-3.63, 1.26) * mm, "end": v(-3.64, 2.15) * mm});
            skLineSegment(sketch, "E340", {"start": v(-3.64, 2.15) * mm, "end": v(-3.64, 2.15) * mm});
            skLineSegment(sketch, "E341", {"start": v(-3.64, 2.15) * mm, "end": v(-3.64, 2.16) * mm});
            skLineSegment(sketch, "E342", {"start": v(-3.64, 2.16) * mm, "end": v(-3.64, 2.17) * mm});
            skLineSegment(sketch, "E343", {"start": v(-3.64, 2.17) * mm, "end": v(-3.67, 3.06) * mm});
            skLineSegment(sketch, "E344", {"start": v(-3.67, 3.06) * mm, "end": v(-3.67, 3.06) * mm});
            skLineSegment(sketch, "E345", {"start": v(-3.67, 3.06) * mm, "end": v(-3.73, 3.95) * mm});
            skLineSegment(sketch, "E346", {"start": v(-3.73, 3.95) * mm, "end": v(-3.75, 4.16) * mm});
            skLineSegment(sketch, "E347", {"start": v(-3.75, 4.16) * mm, "end": v(-3.82, 4.97) * mm});
            skLineSegment(sketch, "E348", {"start": v(-3.82, 4.97) * mm, "end": v(-3.9, 5.78) * mm});
            skLineSegment(sketch, "E349", {"start": v(-3.9, 5.78) * mm, "end": v(-3.92, 5.87) * mm});
            skLineSegment(sketch, "E350", {"start": v(-3.92, 5.87) * mm, "end": v(-4.03, 6.67) * mm});
            skLineSegment(sketch, "E351", {"start": v(-4.03, 6.67) * mm, "end": v(-4.05, 6.77) * mm});
            skLineSegment(sketch, "E352", {"start": v(-4.05, 6.77) * mm, "end": v(-4.17, 7.57) * mm});
            skLineSegment(sketch, "E353", {"start": v(-4.17, 7.57) * mm, "end": v(-4.2, 7.67) * mm});
            skLineSegment(sketch, "E354", {"start": v(-4.2, 7.67) * mm, "end": v(-4.34, 8.46) * mm});
            skLineSegment(sketch, "E355", {"start": v(-4.34, 8.46) * mm, "end": v(-4.36, 8.57) * mm});
            skLineSegment(sketch, "E356", {"start": v(-4.36, 8.57) * mm, "end": v(-4.53, 9.35) * mm});
            skLineSegment(sketch, "E357", {"start": v(-4.53, 9.35) * mm, "end": v(-4.55, 9.46) * mm});
            skLineSegment(sketch, "E358", {"start": v(-4.55, 9.46) * mm, "end": v(-4.74, 10.23) * mm});
            skLineSegment(sketch, "E359", {"start": v(-4.74, 10.23) * mm, "end": v(-4.77, 10.34) * mm});
            skLineSegment(sketch, "E360", {"start": v(-4.77, 10.34) * mm, "end": v(-4.97, 11.11) * mm});
            skLineSegment(sketch, "E361", {"start": v(-4.97, 11.11) * mm, "end": v(-5, 11.22) * mm});
            skLineSegment(sketch, "E362", {"start": v(-5, 11.22) * mm, "end": v(-5.22, 11.99) * mm});
            skLineSegment(sketch, "E363", {"start": v(-5.22, 11.99) * mm, "end": v(-5.26, 12.1) * mm});
            skLineSegment(sketch, "E364", {"start": v(-5.26, 12.1) * mm, "end": v(-5.5, 12.85) * mm});
            skLineSegment(sketch, "E365", {"start": v(-5.5, 12.85) * mm, "end": v(-5.76, 13.6) * mm});
            skLineSegment(sketch, "E366", {"start": v(-5.76, 13.6) * mm, "end": v(-5.8, 13.7) * mm});
            skLineSegment(sketch, "E367", {"start": v(-5.8, 13.7) * mm, "end": v(-6.07, 14.46) * mm});
            skLineSegment(sketch, "E368", {"start": v(-6.07, 14.46) * mm, "end": v(-6.1, 14.56) * mm});
            skLineSegment(sketch, "E369", {"start": v(-6.1, 14.56) * mm, "end": v(-6.4, 15.3) * mm});
            skLineSegment(sketch, "E370", {"start": v(-6.4, 15.3) * mm, "end": v(-6.45, 15.4) * mm});
            skLineSegment(sketch, "E371", {"start": v(-6.45, 15.4) * mm, "end": v(-6.76, 16.14) * mm});
            skLineSegment(sketch, "E372", {"start": v(-6.76, 16.14) * mm, "end": v(-6.8, 16.24) * mm});
            skLineSegment(sketch, "E373", {"start": v(-6.8, 16.24) * mm, "end": v(-7.14, 16.97) * mm});
            skLineSegment(sketch, "E374", {"start": v(-7.14, 16.97) * mm, "end": v(-7.18, 17.06) * mm});
            skLineSegment(sketch, "E375", {"start": v(-7.18, 17.06) * mm, "end": v(-7.53, 17.79) * mm});
            skLineSegment(sketch, "E376", {"start": v(-7.53, 17.79) * mm, "end": v(-7.58, 17.88) * mm});
            skLineSegment(sketch, "E377", {"start": v(-7.58, 17.88) * mm, "end": v(-7.95, 18.6) * mm});
            skLineSegment(sketch, "E378", {"start": v(-7.95, 18.6) * mm, "end": v(-8, 18.69) * mm});
            skLineSegment(sketch, "E379", {"start": v(-8, 18.69) * mm, "end": v(-8.39, 19.4) * mm});
            skLineSegment(sketch, "E380", {"start": v(-8.39, 19.4) * mm, "end": v(-8.8, 20.1) * mm});
            skLineSegment(sketch, "E381", {"start": v(-8.8, 20.1) * mm, "end": v(-8.87, 20.23) * mm});
            skLineSegment(sketch, "E382", {"start": v(-8.87, 20.23) * mm, "end": v(-8.9, 20.27) * mm});
            skLineSegment(sketch, "E383", {"start": v(-8.9, 20.27) * mm, "end": v(-8.9, 20.28) * mm});
            skLineSegment(sketch, "E384", {"start": v(-8.9, 20.28) * mm, "end": v(-9.37, 21.04) * mm});
            skLineSegment(sketch, "E385", {"start": v(-9.37, 21.04) * mm, "end": v(-9.86, 21.79) * mm});
            skLineSegment(sketch, "E386", {"start": v(-9.86, 21.79) * mm, "end": v(-9.86, 21.8) * mm});
            skLineSegment(sketch, "E387", {"start": v(-9.86, 21.8) * mm, "end": v(-10.37, 22.54) * mm});
            skLineSegment(sketch, "E388", {"start": v(-10.37, 22.54) * mm, "end": v(-10.38, 22.55) * mm});
            skLineSegment(sketch, "E389", {"start": v(-10.38, 22.55) * mm, "end": v(-10.9, 23.27) * mm});
            skLineSegment(sketch, "E390", {"start": v(-10.9, 23.27) * mm, "end": v(-10.91, 23.29) * mm});
            skLineSegment(sketch, "E391", {"start": v(-10.91, 23.29) * mm, "end": v(-11.45, 24) * mm});
            skLineSegment(sketch, "E392", {"start": v(-11.45, 24) * mm, "end": v(-11.46, 24) * mm});
            skLineSegment(sketch, "E393", {"start": v(-11.46, 24) * mm, "end": v(-12.02, 24.7) * mm});
            skLineSegment(sketch, "E394", {"start": v(-12.02, 24.7) * mm, "end": v(-12.03, 24.72) * mm});
            skLineSegment(sketch, "E395", {"start": v(-12.03, 24.72) * mm, "end": v(-12.6, 25.4) * mm});
            skLineSegment(sketch, "E396", {"start": v(-12.6, 25.4) * mm, "end": v(-12.61, 25.41) * mm});
            skLineSegment(sketch, "E397", {"start": v(-12.61, 25.41) * mm, "end": v(-13.2, 26.08) * mm});
            skLineSegment(sketch, "E398", {"start": v(-13.2, 26.08) * mm, "end": v(-13.21, 26.1) * mm});
            skLineSegment(sketch, "E399", {"start": v(-13.21, 26.1) * mm, "end": v(-13.82, 26.75) * mm});
            skLineSegment(sketch, "E400", {"start": v(-13.82, 26.75) * mm, "end": v(-13.83, 26.76) * mm});
            skLineSegment(sketch, "E401", {"start": v(-13.83, 26.76) * mm, "end": v(-14.46, 27.4) * mm});
            skLineSegment(sketch, "E402", {"start": v(-14.46, 27.4) * mm, "end": v(-14.47, 27.4) * mm});
            skLineSegment(sketch, "E403", {"start": v(-14.47, 27.4) * mm, "end": v(-15.1, 28.03) * mm});
            skLineSegment(sketch, "E404", {"start": v(-15.1, 28.03) * mm, "end": v(-15.12, 28.04) * mm});
            skLineSegment(sketch, "E405", {"start": v(-15.12, 28.04) * mm, "end": v(-15.77, 28.65) * mm});
            skLineSegment(sketch, "E406", {"start": v(-15.77, 28.65) * mm, "end": v(-15.78, 28.66) * mm});
            skLineSegment(sketch, "E407", {"start": v(-15.78, 28.66) * mm, "end": v(-16.45, 29.25) * mm});
            skLineSegment(sketch, "E408", {"start": v(-16.45, 29.25) * mm, "end": v(-16.46, 29.26) * mm});
            skLineSegment(sketch, "E409", {"start": v(-16.46, 29.26) * mm, "end": v(-17.14, 29.84) * mm});
            skLineSegment(sketch, "E410", {"start": v(-17.14, 29.84) * mm, "end": v(-17.16, 29.85) * mm});
            skLineSegment(sketch, "E411", {"start": v(-17.16, 29.85) * mm, "end": v(-17.85, 30.4) * mm});
            skLineSegment(sketch, "E412", {"start": v(-17.85, 30.4) * mm, "end": v(-17.87, 30.41) * mm});
            skLineSegment(sketch, "E413", {"start": v(-17.87, 30.41) * mm, "end": v(-17.88, 30.42) * mm});
            skLineSegment(sketch, "E414", {"start": v(-17.88, 30.42) * mm, "end": v(-18.59, 30.96) * mm});
            skLineSegment(sketch, "E415", {"start": v(-18.59, 30.96) * mm, "end": v(-18.6, 30.97) * mm});
            skLineSegment(sketch, "E416", {"start": v(-18.6, 30.97) * mm, "end": v(-19.32, 31.5) * mm});
            skLineSegment(sketch, "E417", {"start": v(-19.32, 31.5) * mm, "end": v(-20.06, 32) * mm});
            skLineSegment(sketch, "E418", {"start": v(-20.06, 32) * mm, "end": v(-20.07, 32) * mm});
            skLineSegment(sketch, "E419", {"start": v(-20.07, 32) * mm, "end": v(-20.82, 32.5) * mm});
            skLineSegment(sketch, "E420", {"start": v(-20.82, 32.5) * mm, "end": v(-20.83, 32.5) * mm});
            skLineSegment(sketch, "E421", {"start": v(-20.83, 32.5) * mm, "end": v(-20.85, 32.51) * mm});
            skLineSegment(sketch, "E422", {"start": v(-20.85, 32.51) * mm, "end": v(-21.6, 32.98) * mm});
            skLineSegment(sketch, "E423", {"start": v(-21.6, 32.98) * mm, "end": v(-22.38, 33.43) * mm});
            skLineSegment(sketch, "E424", {"start": v(-22.38, 33.43) * mm, "end": v(-22.4, 33.44) * mm});
            skLineSegment(sketch, "E425", {"start": v(-22.4, 33.44) * mm, "end": v(-23.17, 33.87) * mm});
            skLineSegment(sketch, "E426", {"start": v(-23.17, 33.87) * mm, "end": v(-23.19, 33.88) * mm});
            skLineSegment(sketch, "E427", {"start": v(-23.19, 33.88) * mm, "end": v(-23.98, 34.29) * mm});
            skLineSegment(sketch, "E428", {"start": v(-23.98, 34.29) * mm, "end": v(-24, 34.3) * mm});
            skLineSegment(sketch, "E429", {"start": v(-24, 34.3) * mm, "end": v(-24.8, 34.69) * mm});
            skLineSegment(sketch, "E430", {"start": v(-24.8, 34.69) * mm, "end": v(-24.8, 34.7) * mm});
            skLineSegment(sketch, "E431", {"start": v(-24.8, 34.7) * mm, "end": v(-25.62, 35.06) * mm});
            skLineSegment(sketch, "E432", {"start": v(-25.62, 35.06) * mm, "end": v(-25.64, 35.07) * mm});
            skLineSegment(sketch, "E433", {"start": v(-25.64, 35.07) * mm, "end": v(-26.46, 35.42) * mm});
            skLineSegment(sketch, "E434", {"start": v(-26.46, 35.42) * mm, "end": v(-26.47, 35.43) * mm});
            skLineSegment(sketch, "E435", {"start": v(-26.47, 35.43) * mm, "end": v(-27.3, 35.76) * mm});
            skLineSegment(sketch, "E436", {"start": v(-27.3, 35.76) * mm, "end": v(-27.31, 35.77) * mm});
            skLineSegment(sketch, "E437", {"start": v(-27.31, 35.77) * mm, "end": v(-27.34, 35.78) * mm});
            skLineSegment(sketch, "E438", {"start": v(-27.34, 35.78) * mm, "end": v(-28.18, 36.09) * mm});
            skLineSegment(sketch, "E439", {"start": v(-28.18, 36.09) * mm, "end": v(-29.02, 36.38) * mm});
            skLineSegment(sketch, "E440", {"start": v(-29.02, 36.38) * mm, "end": v(-29.02, 36.38) * mm});
            skLineSegment(sketch, "E441", {"start": v(-29.02, 36.38) * mm, "end": v(-29.03, 36.38) * mm});
            skLineSegment(sketch, "E442", {"start": v(-29.03, 36.38) * mm, "end": v(-29.04, 36.38) * mm});
            skLineSegment(sketch, "E443", {"start": v(-29.04, 36.38) * mm, "end": v(-29.04, 36.38) * mm});
            skLineSegment(sketch, "E444", {"start": v(-29.04, 36.38) * mm, "end": v(-29.89, 36.65) * mm});
            skLineSegment(sketch, "E445", {"start": v(-29.89, 36.65) * mm, "end": v(-29.9, 36.65) * mm});
            skLineSegment(sketch, "E446", {"start": v(-29.9, 36.65) * mm, "end": v(-29.9, 36.66) * mm});
            skLineSegment(sketch, "E447", {"start": v(-29.9, 36.66) * mm, "end": v(-29.9, 36.66) * mm});
            skLineSegment(sketch, "E448", {"start": v(-29.9, 36.66) * mm, "end": v(-30.76, 36.9) * mm});
            skLineSegment(sketch, "E449", {"start": v(-30.76, 36.9) * mm, "end": v(-30.77, 36.9) * mm});
            skLineSegment(sketch, "E450", {"start": v(-30.77, 36.9) * mm, "end": v(-31.63, 37.13) * mm});
            skLineSegment(sketch, "E451", {"start": v(-31.63, 37.13) * mm, "end": v(-31.85, 37.18) * mm});
            skLineSegment(sketch, "E452", {"start": v(-31.85, 37.18) * mm, "end": v(-32.64, 37.37) * mm});
            skLineSegment(sketch, "E453", {"start": v(-32.64, 37.37) * mm, "end": v(-33.43, 37.54) * mm});
            skLineSegment(sketch, "E454", {"start": v(-33.43, 37.54) * mm, "end": v(-33.5, 37.55) * mm});
            skLineSegment(sketch, "E455", {"start": v(-33.5, 37.55) * mm, "end": v(-34.3, 37.7) * mm});
            skLineSegment(sketch, "E456", {"start": v(-34.3, 37.7) * mm, "end": v(-34.4, 37.72) * mm});
            skLineSegment(sketch, "E457", {"start": v(-34.4, 37.72) * mm, "end": v(-35.2, 37.84) * mm});
            skLineSegment(sketch, "E458", {"start": v(-35.2, 37.84) * mm, "end": v(-35.3, 37.86) * mm});
            skLineSegment(sketch, "E459", {"start": v(-35.3, 37.86) * mm, "end": v(-36.1, 37.97) * mm});
            skLineSegment(sketch, "E460", {"start": v(-36.1, 37.97) * mm, "end": v(-36.2, 37.98) * mm});
            skLineSegment(sketch, "E461", {"start": v(-36.2, 37.98) * mm, "end": v(-37, 38.07) * mm});
            skLineSegment(sketch, "E462", {"start": v(-37, 38.07) * mm, "end": v(-37.11, 38.08) * mm});
            skLineSegment(sketch, "E463", {"start": v(-37.11, 38.08) * mm, "end": v(-37.9, 38.14) * mm});
            skLineSegment(sketch, "E464", {"start": v(-37.9, 38.14) * mm, "end": v(-38.02, 38.15) * mm});
            skLineSegment(sketch, "E465", {"start": v(-38.02, 38.15) * mm, "end": v(-38.81, 38.2) * mm});
            skLineSegment(sketch, "E466", {"start": v(-38.81, 38.2) * mm, "end": v(-38.93, 38.2) * mm});
            skLineSegment(sketch, "E467", {"start": v(-38.93, 38.2) * mm, "end": v(-39.72, 38.23) * mm});
            skLineSegment(sketch, "E468", {"start": v(-39.72, 38.23) * mm, "end": v(-39.83, 38.23) * mm});
            skLineSegment(sketch, "E469", {"start": v(-39.83, 38.23) * mm, "end": v(-40.63, 38.24) * mm});
            skLineSegment(sketch, "E470", {"start": v(-40.63, 38.24) * mm, "end": v(-41.42, 38.23) * mm});
            skLineSegment(sketch, "E471", {"start": v(-41.42, 38.23) * mm, "end": v(-41.54, 38.23) * mm});
            skLineSegment(sketch, "E472", {"start": v(-41.54, 38.23) * mm, "end": v(-42.33, 38.2) * mm});
            skLineSegment(sketch, "E473", {"start": v(-42.33, 38.2) * mm, "end": v(-42.44, 38.2) * mm});
            skLineSegment(sketch, "E474", {"start": v(-42.44, 38.2) * mm, "end": v(-43.24, 38.15) * mm});
            skLineSegment(sketch, "E475", {"start": v(-43.24, 38.15) * mm, "end": v(-43.35, 38.14) * mm});
            skLineSegment(sketch, "E476", {"start": v(-43.35, 38.14) * mm, "end": v(-44.15, 38.08) * mm});
            skLineSegment(sketch, "E477", {"start": v(-44.15, 38.08) * mm, "end": v(-44.26, 38.07) * mm});
            skLineSegment(sketch, "E478", {"start": v(-44.26, 38.07) * mm, "end": v(-45.05, 37.98) * mm});
            skLineSegment(sketch, "E479", {"start": v(-45.05, 37.98) * mm, "end": v(-45.16, 37.97) * mm});
            skLineSegment(sketch, "E480", {"start": v(-45.16, 37.97) * mm, "end": v(-45.95, 37.86) * mm});
            skLineSegment(sketch, "E481", {"start": v(-45.95, 37.86) * mm, "end": v(-46.06, 37.84) * mm});
            skLineSegment(sketch, "E482", {"start": v(-46.06, 37.84) * mm, "end": v(-46.85, 37.72) * mm});
            skLineSegment(sketch, "E483", {"start": v(-46.85, 37.72) * mm, "end": v(-46.95, 37.7) * mm});
            skLineSegment(sketch, "E484", {"start": v(-46.95, 37.7) * mm, "end": v(-47.75, 37.55) * mm});
            skLineSegment(sketch, "E485", {"start": v(-47.75, 37.55) * mm, "end": v(-47.82, 37.54) * mm});
            skLineSegment(sketch, "E486", {"start": v(-47.82, 37.54) * mm, "end": v(-48.62, 37.37) * mm});
            skLineSegment(sketch, "E487", {"start": v(-48.62, 37.37) * mm, "end": v(-48.74, 37.35) * mm});
            skLineSegment(sketch, "E488", {"start": v(-48.74, 37.35) * mm, "end": v(-48.75, 37.34) * mm});
            skLineSegment(sketch, "E489", {"start": v(-48.75, 37.34) * mm, "end": v(-49.62, 37.14) * mm});
            skLineSegment(sketch, "E490", {"start": v(-49.62, 37.14) * mm, "end": v(-50.48, 36.9) * mm});
            skLineSegment(sketch, "E491", {"start": v(-50.48, 36.9) * mm, "end": v(-50.5, 36.9) * mm});
            skLineSegment(sketch, "E492", {"start": v(-50.5, 36.9) * mm, "end": v(-51.35, 36.66) * mm});
            skLineSegment(sketch, "E493", {"start": v(-51.35, 36.66) * mm, "end": v(-51.37, 36.65) * mm});
            skLineSegment(sketch, "E494", {"start": v(-51.37, 36.65) * mm, "end": v(-52.22, 36.38) * mm});
            skLineSegment(sketch, "E495", {"start": v(-52.22, 36.38) * mm, "end": v(-52.23, 36.38) * mm});
            skLineSegment(sketch, "E496", {"start": v(-52.23, 36.38) * mm, "end": v(-53.08, 36.09) * mm});
            skLineSegment(sketch, "E497", {"start": v(-53.08, 36.09) * mm, "end": v(-53.1, 36.08) * mm});
            skLineSegment(sketch, "E498", {"start": v(-53.1, 36.08) * mm, "end": v(-53.93, 35.77) * mm});
            skLineSegment(sketch, "E499", {"start": v(-53.93, 35.77) * mm, "end": v(-53.94, 35.76) * mm});
            skLineSegment(sketch, "E500", {"start": v(-53.94, 35.76) * mm, "end": v(-54.77, 35.43) * mm});
            skLineSegment(sketch, "E501", {"start": v(-54.77, 35.43) * mm, "end": v(-54.79, 35.43) * mm});
            skLineSegment(sketch, "E502", {"start": v(-54.79, 35.43) * mm, "end": v(-55.6, 35.08) * mm});
            skLineSegment(sketch, "E503", {"start": v(-55.6, 35.08) * mm, "end": v(-55.62, 35.07) * mm});
            skLineSegment(sketch, "E504", {"start": v(-55.62, 35.07) * mm, "end": v(-56.43, 34.7) * mm});
            skLineSegment(sketch, "E505", {"start": v(-56.43, 34.7) * mm, "end": v(-56.45, 34.7) * mm});
            skLineSegment(sketch, "E506", {"start": v(-56.45, 34.7) * mm, "end": v(-57.25, 34.3) * mm});
            skLineSegment(sketch, "E507", {"start": v(-57.25, 34.3) * mm, "end": v(-57.26, 34.3) * mm});
            skLineSegment(sketch, "E508", {"start": v(-57.26, 34.3) * mm, "end": v(-58.06, 33.88) * mm});
            skLineSegment(sketch, "E509", {"start": v(-58.06, 33.88) * mm, "end": v(-58.07, 33.88) * mm});
            skLineSegment(sketch, "E510", {"start": v(-58.07, 33.88) * mm, "end": v(-58.85, 33.44) * mm});
            skLineSegment(sketch, "E511", {"start": v(-58.85, 33.44) * mm, "end": v(-58.87, 33.44) * mm});
            skLineSegment(sketch, "E512", {"start": v(-58.87, 33.44) * mm, "end": v(-59.64, 32.99) * mm});
            skLineSegment(sketch, "E513", {"start": v(-59.64, 32.99) * mm, "end": v(-59.65, 32.98) * mm});
            skLineSegment(sketch, "E514", {"start": v(-59.65, 32.98) * mm, "end": v(-60.41, 32.51) * mm});
            skLineSegment(sketch, "E515", {"start": v(-60.41, 32.51) * mm, "end": v(-60.42, 32.5) * mm});
            skLineSegment(sketch, "E516", {"start": v(-60.42, 32.5) * mm, "end": v(-60.44, 32.5) * mm});
            skLineSegment(sketch, "E517", {"start": v(-60.44, 32.5) * mm, "end": v(-61.18, 32) * mm});
            skLineSegment(sketch, "E518", {"start": v(-61.18, 32) * mm, "end": v(-61.92, 31.5) * mm});
            skLineSegment(sketch, "E519", {"start": v(-61.92, 31.5) * mm, "end": v(-61.93, 31.5) * mm});
            skLineSegment(sketch, "E520", {"start": v(-61.93, 31.5) * mm, "end": v(-62.66, 30.97) * mm});
            skLineSegment(sketch, "E521", {"start": v(-62.66, 30.97) * mm, "end": v(-62.67, 30.96) * mm});
            skLineSegment(sketch, "E522", {"start": v(-62.67, 30.96) * mm, "end": v(-62.68, 30.95) * mm});
            skLineSegment(sketch, "E523", {"start": v(-62.68, 30.95) * mm, "end": v(-63.4, 30.41) * mm});
            skLineSegment(sketch, "E524", {"start": v(-63.4, 30.41) * mm, "end": v(-64.09, 29.86) * mm});
            skLineSegment(sketch, "E525", {"start": v(-64.09, 29.86) * mm, "end": v(-64.1, 29.85) * mm});
            skLineSegment(sketch, "E526", {"start": v(-64.1, 29.85) * mm, "end": v(-64.78, 29.27) * mm});
            skLineSegment(sketch, "E527", {"start": v(-64.78, 29.27) * mm, "end": v(-64.8, 29.26) * mm});
            skLineSegment(sketch, "E528", {"start": v(-64.8, 29.26) * mm, "end": v(-65.47, 28.67) * mm});
            skLineSegment(sketch, "E529", {"start": v(-65.47, 28.67) * mm, "end": v(-65.48, 28.66) * mm});
            skLineSegment(sketch, "E530", {"start": v(-65.48, 28.66) * mm, "end": v(-66.13, 28.05) * mm});
            skLineSegment(sketch, "E531", {"start": v(-66.13, 28.05) * mm, "end": v(-66.14, 28.04) * mm});
            skLineSegment(sketch, "E532", {"start": v(-66.14, 28.04) * mm, "end": v(-66.78, 27.42) * mm});
            skLineSegment(sketch, "E533", {"start": v(-66.78, 27.42) * mm, "end": v(-66.8, 27.4) * mm});
            skLineSegment(sketch, "E534", {"start": v(-66.8, 27.4) * mm, "end": v(-67.42, 26.77) * mm});
            skLineSegment(sketch, "E535", {"start": v(-67.42, 26.77) * mm, "end": v(-67.43, 26.76) * mm});
            skLineSegment(sketch, "E536", {"start": v(-67.43, 26.76) * mm, "end": v(-68.03, 26.1) * mm});
            skLineSegment(sketch, "E537", {"start": v(-68.03, 26.1) * mm, "end": v(-68.04, 26.1) * mm});
            skLineSegment(sketch, "E538", {"start": v(-68.04, 26.1) * mm, "end": v(-68.64, 25.42) * mm});
            skLineSegment(sketch, "E539", {"start": v(-68.64, 25.42) * mm, "end": v(-68.65, 25.41) * mm});
            skLineSegment(sketch, "E540", {"start": v(-68.65, 25.41) * mm, "end": v(-69.22, 24.73) * mm});
            skLineSegment(sketch, "E541", {"start": v(-69.22, 24.73) * mm, "end": v(-69.23, 24.72) * mm});
            skLineSegment(sketch, "E542", {"start": v(-69.23, 24.72) * mm, "end": v(-69.24, 24.7) * mm});
            skLineSegment(sketch, "E543", {"start": v(-69.24, 24.7) * mm, "end": v(-69.8, 24) * mm});
            skLineSegment(sketch, "E544", {"start": v(-69.8, 24) * mm, "end": v(-69.8, 24) * mm});
            skLineSegment(sketch, "E545", {"start": v(-69.8, 24) * mm, "end": v(-70.35, 23.29) * mm});
            skLineSegment(sketch, "E546", {"start": v(-70.35, 23.29) * mm, "end": v(-70.35, 23.28) * mm});
            skLineSegment(sketch, "E547", {"start": v(-70.35, 23.28) * mm, "end": v(-70.35, 23.28) * mm});
            skLineSegment(sketch, "E548", {"start": v(-70.35, 23.28) * mm, "end": v(-70.36, 23.27) * mm});
            skLineSegment(sketch, "E549", {"start": v(-70.36, 23.27) * mm, "end": v(-70.88, 22.55) * mm});
            skLineSegment(sketch, "E550", {"start": v(-70.88, 22.55) * mm, "end": v(-70.88, 22.55) * mm});
            skLineSegment(sketch, "E551", {"start": v(-70.88, 22.55) * mm, "end": v(-70.88, 22.54) * mm});
            skLineSegment(sketch, "E552", {"start": v(-70.88, 22.54) * mm, "end": v(-70.89, 22.54) * mm});
            skLineSegment(sketch, "E553", {"start": v(-70.89, 22.54) * mm, "end": v(-71.4, 21.8) * mm});
            skLineSegment(sketch, "E554", {"start": v(-71.4, 21.8) * mm, "end": v(-71.4, 21.8) * mm});
            skLineSegment(sketch, "E555", {"start": v(-71.4, 21.8) * mm, "end": v(-71.88, 21.04) * mm});
            skLineSegment(sketch, "E556", {"start": v(-71.88, 21.04) * mm, "end": v(-72, 20.84) * mm});
            skLineSegment(sketch, "E557", {"start": v(-72, 20.84) * mm, "end": v(-72.43, 20.15) * mm});
            skLineSegment(sketch, "E558", {"start": v(-72.43, 20.15) * mm, "end": v(-72.84, 19.44) * mm});
            skLineSegment(sketch, "E559", {"start": v(-72.84, 19.44) * mm, "end": v(-73.24, 18.73) * mm});
            skLineSegment(sketch, "E560", {"start": v(-73.24, 18.73) * mm, "end": v(-73.26, 18.69) * mm});
            skLineSegment(sketch, "E561", {"start": v(-73.26, 18.69) * mm, "end": v(-73.3, 18.6) * mm});
            skLineSegment(sketch, "E562", {"start": v(-73.3, 18.6) * mm, "end": v(-73.68, 17.88) * mm});
            skLineSegment(sketch, "E563", {"start": v(-73.68, 17.88) * mm, "end": v(-73.72, 17.79) * mm});
            skLineSegment(sketch, "E564", {"start": v(-73.72, 17.79) * mm, "end": v(-74.08, 17.06) * mm});
            skLineSegment(sketch, "E565", {"start": v(-74.08, 17.06) * mm, "end": v(-74.12, 16.97) * mm});
            skLineSegment(sketch, "E566", {"start": v(-74.12, 16.97) * mm, "end": v(-74.46, 16.24) * mm});
            skLineSegment(sketch, "E567", {"start": v(-74.46, 16.24) * mm, "end": v(-74.5, 16.14) * mm});
            skLineSegment(sketch, "E568", {"start": v(-74.5, 16.14) * mm, "end": v(-74.81, 15.4) * mm});
            skLineSegment(sketch, "E569", {"start": v(-74.81, 15.4) * mm, "end": v(-74.85, 15.3) * mm});
            skLineSegment(sketch, "E570", {"start": v(-74.85, 15.3) * mm, "end": v(-75.15, 14.56) * mm});
            skLineSegment(sketch, "E571", {"start": v(-75.15, 14.56) * mm, "end": v(-75.19, 14.45) * mm});
            skLineSegment(sketch, "E572", {"start": v(-75.19, 14.45) * mm, "end": v(-75.47, 13.7) * mm});
            skLineSegment(sketch, "E573", {"start": v(-75.47, 13.7) * mm, "end": v(-75.5, 13.6) * mm});
            skLineSegment(sketch, "E574", {"start": v(-75.5, 13.6) * mm, "end": v(-75.76, 12.85) * mm});
            skLineSegment(sketch, "E575", {"start": v(-75.76, 12.85) * mm, "end": v(-76, 12.1) * mm});
            skLineSegment(sketch, "E576", {"start": v(-76, 12.1) * mm, "end": v(-76.04, 11.98) * mm});
            skLineSegment(sketch, "E577", {"start": v(-76.04, 11.98) * mm, "end": v(-76.26, 11.22) * mm});
            skLineSegment(sketch, "E578", {"start": v(-76.26, 11.22) * mm, "end": v(-76.29, 11.11) * mm});
            skLineSegment(sketch, "E579", {"start": v(-76.29, 11.11) * mm, "end": v(-76.5, 10.34) * mm});
            skLineSegment(sketch, "E580", {"start": v(-76.5, 10.34) * mm, "end": v(-76.52, 10.23) * mm});
            skLineSegment(sketch, "E581", {"start": v(-76.52, 10.23) * mm, "end": v(-76.7, 9.46) * mm});
            skLineSegment(sketch, "E582", {"start": v(-76.7, 9.46) * mm, "end": v(-76.73, 9.35) * mm});
            skLineSegment(sketch, "E583", {"start": v(-76.73, 9.35) * mm, "end": v(-76.9, 8.57) * mm});
            skLineSegment(sketch, "E584", {"start": v(-76.9, 8.57) * mm, "end": v(-76.92, 8.46) * mm});
            skLineSegment(sketch, "E585", {"start": v(-76.92, 8.46) * mm, "end": v(-77.07, 7.67) * mm});
            skLineSegment(sketch, "E586", {"start": v(-77.07, 7.67) * mm, "end": v(-77.09, 7.57) * mm});
            skLineSegment(sketch, "E587", {"start": v(-77.09, 7.57) * mm, "end": v(-77.21, 6.77) * mm});
            skLineSegment(sketch, "E588", {"start": v(-77.21, 6.77) * mm, "end": v(-77.23, 6.67) * mm});
            skLineSegment(sketch, "E589", {"start": v(-77.23, 6.67) * mm, "end": v(-77.34, 5.87) * mm});
            skLineSegment(sketch, "E590", {"start": v(-77.34, 5.87) * mm, "end": v(-77.35, 5.78) * mm});
            skLineSegment(sketch, "E591", {"start": v(-77.35, 5.78) * mm, "end": v(-77.35, 5.77) * mm});
            skLineSegment(sketch, "E592", {"start": v(-77.35, 5.77) * mm, "end": v(-77.35, 5.76) * mm});
            skLineSegment(sketch, "E593", {"start": v(-77.35, 5.76) * mm, "end": v(-77.45, 4.87) * mm});
            skLineSegment(sketch, "E594", {"start": v(-77.45, 4.87) * mm, "end": v(-77.45, 4.86) * mm});
            skLineSegment(sketch, "E595", {"start": v(-77.45, 4.86) * mm, "end": v(-77.53, 3.97) * mm});
            skLineSegment(sketch, "E596", {"start": v(-77.53, 3.97) * mm, "end": v(-77.58, 3.07) * mm});
            skLineSegment(sketch, "E597", {"start": v(-77.58, 3.07) * mm, "end": v(-77.58, 3.06) * mm});
            skLineSegment(sketch, "E598", {"start": v(-77.58, 3.06) * mm, "end": v(-77.62, 2.17) * mm});
            skLineSegment(sketch, "E599", {"start": v(-77.62, 2.17) * mm, "end": v(-77.62, 2.15) * mm});
            skLineSegment(sketch, "E600", {"start": v(-77.62, 2.15) * mm, "end": v(-77.62, 2.14) * mm});
            skLineSegment(sketch, "E601", {"start": v(-77.62, 2.14) * mm, "end": v(-77.63, 1.24) * mm});
            skLineSegment(sketch, "E602", {"start": v(-77.63, 1.24) * mm, "end": v(-77.63, 1.23) * mm});
            skLineSegment(sketch, "E603", {"start": v(-77.63, 1.23) * mm, "end": v(-77.62, 0.34) * mm});
            skLineSegment(sketch, "E604", {"start": v(-77.62, 0.34) * mm, "end": v(-77.62, 0.32) * mm});
            skLineSegment(sketch, "E605", {"start": v(-77.62, 0.32) * mm, "end": v(-77.58, -0.57) * mm});
            skLineSegment(sketch, "E606", {"start": v(-77.58, -0.57) * mm, "end": v(-77.58, -0.59) * mm});
            skLineSegment(sketch, "E607", {"start": v(-77.58, -0.59) * mm, "end": v(-77.53, -1.48) * mm});
            skLineSegment(sketch, "E608", {"start": v(-77.53, -1.48) * mm, "end": v(-77.53, -1.5) * mm});
            skLineSegment(sketch, "E609", {"start": v(-77.53, -1.5) * mm, "end": v(-77.45, -2.38) * mm});
            skLineSegment(sketch, "E610", {"start": v(-77.45, -2.38) * mm, "end": v(-77.35, -3.27) * mm});
            skLineSegment(sketch, "E611", {"start": v(-77.35, -3.27) * mm, "end": v(-77.35, -3.28) * mm});
            skLineSegment(sketch, "E612", {"start": v(-77.35, -3.28) * mm, "end": v(-77.23, -4.17) * mm});
            skLineSegment(sketch, "E613", {"start": v(-77.23, -4.17) * mm, "end": v(-77.23, -4.18) * mm});
            skLineSegment(sketch, "E614", {"start": v(-77.23, -4.18) * mm, "end": v(-77.09, -5.07) * mm});
            skLineSegment(sketch, "E615", {"start": v(-77.09, -5.07) * mm, "end": v(-77.08, -5.08) * mm});
            skLineSegment(sketch, "E616", {"start": v(-77.08, -5.08) * mm, "end": v(-76.92, -5.96) * mm});
            skLineSegment(sketch, "E617", {"start": v(-76.92, -5.96) * mm, "end": v(-76.92, -5.97) * mm});
            skLineSegment(sketch, "E618", {"start": v(-76.92, -5.97) * mm, "end": v(-76.73, -6.85) * mm});
            skLineSegment(sketch, "E619", {"start": v(-76.73, -6.85) * mm, "end": v(-76.73, -6.86) * mm});
            skLineSegment(sketch, "E620", {"start": v(-76.73, -6.86) * mm, "end": v(-76.52, -7.73) * mm});
            skLineSegment(sketch, "E621", {"start": v(-76.52, -7.73) * mm, "end": v(-76.52, -7.75) * mm});
            skLineSegment(sketch, "E622", {"start": v(-76.52, -7.75) * mm, "end": v(-76.52, -7.76) * mm});
            skLineSegment(sketch, "E623", {"start": v(-76.52, -7.76) * mm, "end": v(-76.29, -8.62) * mm});
            skLineSegment(sketch, "E624", {"start": v(-76.29, -8.62) * mm, "end": v(-76.28, -8.64) * mm});
            skLineSegment(sketch, "E625", {"start": v(-76.28, -8.64) * mm, "end": v(-76.04, -9.5) * mm});
            skLineSegment(sketch, "E626", {"start": v(-76.04, -9.5) * mm, "end": v(-75.77, -10.35) * mm});
            skLineSegment(sketch, "E627", {"start": v(-75.77, -10.35) * mm, "end": v(-75.76, -10.36) * mm});
            skLineSegment(sketch, "E628", {"start": v(-75.76, -10.36) * mm, "end": v(-75.76, -10.38) * mm});
            skLineSegment(sketch, "E629", {"start": v(-75.76, -10.38) * mm, "end": v(-75.47, -11.22) * mm});
            skLineSegment(sketch, "E630", {"start": v(-75.47, -11.22) * mm, "end": v(-75.46, -11.23) * mm});
            skLineSegment(sketch, "E631", {"start": v(-75.46, -11.23) * mm, "end": v(-75.15, -12.07) * mm});
            skLineSegment(sketch, "E632", {"start": v(-75.15, -12.07) * mm, "end": v(-75.14, -12.09) * mm});
            skLineSegment(sketch, "E633", {"start": v(-75.14, -12.09) * mm, "end": v(-74.81, -12.91) * mm});
            skLineSegment(sketch, "E634", {"start": v(-74.81, -12.91) * mm, "end": v(-74.46, -13.74) * mm});
            skLineSegment(sketch, "E635", {"start": v(-74.46, -13.74) * mm, "end": v(-74.45, -13.75) * mm});
            skLineSegment(sketch, "E636", {"start": v(-74.45, -13.75) * mm, "end": v(-74.08, -14.56) * mm});
            skLineSegment(sketch, "E637", {"start": v(-74.08, -14.56) * mm, "end": v(-74.08, -14.58) * mm});
            skLineSegment(sketch, "E638", {"start": v(-74.08, -14.58) * mm, "end": v(-74.07, -14.59) * mm});
            skLineSegment(sketch, "E639", {"start": v(-74.07, -14.59) * mm, "end": v(-73.68, -15.4) * mm});
            skLineSegment(sketch, "E640", {"start": v(-73.68, -15.4) * mm, "end": v(-73.67, -15.4) * mm});
            skLineSegment(sketch, "E641", {"start": v(-73.67, -15.4) * mm, "end": v(-73.26, -16.2) * mm});
            skLineSegment(sketch, "E642", {"start": v(-73.26, -16.2) * mm, "end": v(-72.83, -16.98) * mm});
            skLineSegment(sketch, "E643", {"start": v(-72.83, -16.98) * mm, "end": v(-72.82, -17) * mm});
            skLineSegment(sketch, "E644", {"start": v(-72.82, -17) * mm, "end": v(-72.81, -17) * mm});
            skLineSegment(sketch, "E645", {"start": v(-72.81, -17) * mm, "end": v(-72.36, -17.78) * mm});
            skLineSegment(sketch, "E646", {"start": v(-72.36, -17.78) * mm, "end": v(-71.9, -18.54) * mm});
            skLineSegment(sketch, "E647", {"start": v(-71.9, -18.54) * mm, "end": v(-71.89, -18.55) * mm});
            skLineSegment(sketch, "E648", {"start": v(-71.89, -18.55) * mm, "end": v(-71.4, -19.3) * mm});
            skLineSegment(sketch, "E649", {"start": v(-71.4, -19.3) * mm, "end": v(-71.4, -19.31) * mm});
            skLineSegment(sketch, "E650", {"start": v(-71.4, -19.31) * mm, "end": v(-71.38, -19.32) * mm});
            skLineSegment(sketch, "E651", {"start": v(-71.38, -19.32) * mm, "end": v(-70.88, -20.06) * mm});
            skLineSegment(sketch, "E652", {"start": v(-70.88, -20.06) * mm, "end": v(-70.88, -20.07) * mm});
            skLineSegment(sketch, "E653", {"start": v(-70.88, -20.07) * mm, "end": v(-70.87, -20.07) * mm});
            skLineSegment(sketch, "E654", {"start": v(-70.87, -20.07) * mm, "end": v(-70.87, -20.07) * mm});
            skLineSegment(sketch, "E655", {"start": v(-70.87, -20.07) * mm, "end": v(-70.35, -20.8) * mm});
            skLineSegment(sketch, "E656", {"start": v(-70.35, -20.8) * mm, "end": v(-70.35, -20.8) * mm});
            skLineSegment(sketch, "E657", {"start": v(-70.35, -20.8) * mm, "end": v(-70.34, -20.8) * mm});
            skLineSegment(sketch, "E658", {"start": v(-70.34, -20.8) * mm, "end": v(-70.34, -20.8) * mm});
            skLineSegment(sketch, "E659", {"start": v(-70.34, -20.8) * mm, "end": v(-69.8, -21.52) * mm});
            skLineSegment(sketch, "E660", {"start": v(-69.8, -21.52) * mm, "end": v(-69.8, -21.52) * mm});
            skLineSegment(sketch, "E661", {"start": v(-69.8, -21.52) * mm, "end": v(-69.79, -21.53) * mm});
            skLineSegment(sketch, "E662", {"start": v(-69.79, -21.53) * mm, "end": v(-69.23, -22.23) * mm});
            skLineSegment(sketch, "E663", {"start": v(-69.23, -22.23) * mm, "end": v(-68.66, -22.9) * mm});
            skLineSegment(sketch, "E664", {"start": v(-68.66, -22.9) * mm, "end": v(-68.54, -23.04) * mm});
            skLineSegment(sketch, "E665", {"start": v(14.6, -24.63) * mm, "end": v(14.47, -24.49) * mm});
            skLineSegment(sketch, "E666", {"start": v(14.47, -24.49) * mm, "end": v(14.35, -24.36) * mm});
            skLineSegment(sketch, "E667", {"start": v(14.35, -24.36) * mm, "end": v(14.13, -24.1) * mm});
            skLineSegment(sketch, "E668", {"start": v(14.13, -24.1) * mm, "end": v(14.08, -24.05) * mm});
            skLineSegment(sketch, "E669", {"start": v(14.08, -24.05) * mm, "end": v(13.9, -23.84) * mm});
            skLineSegment(sketch, "E670", {"start": v(13.9, -23.84) * mm, "end": v(13.78, -23.7) * mm});
            skLineSegment(sketch, "E671", {"start": v(13.78, -23.7) * mm, "end": v(13.57, -23.45) * mm});
            skLineSegment(sketch, "E672", {"start": v(13.57, -23.45) * mm, "end": v(13.5, -23.36) * mm});
            skLineSegment(sketch, "E673", {"start": v(13.5, -23.36) * mm, "end": v(13.3, -23.1) * mm});
            skLineSegment(sketch, "E674", {"start": v(13.3, -23.1) * mm, "end": v(13.1, -22.86) * mm});
            skLineSegment(sketch, "E675", {"start": v(13.1, -22.86) * mm, "end": v(12.9, -22.6) * mm});
            skLineSegment(sketch, "E676", {"start": v(12.9, -22.6) * mm, "end": v(12.84, -22.52) * mm});
            skLineSegment(sketch, "E677", {"start": v(12.84, -22.52) * mm, "end": v(12.71, -22.35) * mm});
            skLineSegment(sketch, "E678", {"start": v(12.71, -22.35) * mm, "end": v(12.53, -22.1) * mm});
            skLineSegment(sketch, "E679", {"start": v(12.53, -22.1) * mm, "end": v(12.34, -21.83) * mm});
            skLineSegment(sketch, "E680", {"start": v(12.34, -21.83) * mm, "end": v(12.15, -21.57) * mm});
            skLineSegment(sketch, "E681", {"start": v(12.15, -21.57) * mm, "end": v(11.97, -21.3) * mm});
            skLineSegment(sketch, "E682", {"start": v(11.97, -21.3) * mm, "end": v(11.96, -21.28) * mm});
            skLineSegment(sketch, "E683", {"start": v(11.96, -21.28) * mm, "end": v(11.8, -21.05) * mm});
            skLineSegment(sketch, "E684", {"start": v(11.8, -21.05) * mm, "end": v(11.63, -20.83) * mm});
            skLineSegment(sketch, "E685", {"start": v(11.63, -20.83) * mm, "end": v(11.32, -20.38) * mm});
            skLineSegment(sketch, "E686", {"start": v(11.32, -20.38) * mm, "end": v(11.06, -19.97) * mm});
            skLineSegment(sketch, "E687", {"start": v(11.06, -19.97) * mm, "end": v(10.86, -19.65) * mm});
            skLineSegment(sketch, "E688", {"start": v(10.86, -19.65) * mm, "end": v(10.6, -19.24) * mm});
            skLineSegment(sketch, "E689", {"start": v(10.6, -19.24) * mm, "end": v(10.37, -18.82) * mm});
            skLineSegment(sketch, "E690", {"start": v(10.37, -18.82) * mm, "end": v(10.18, -18.5) * mm});
            skLineSegment(sketch, "E691", {"start": v(10.18, -18.5) * mm, "end": v(9.94, -18.08) * mm});
            skLineSegment(sketch, "E692", {"start": v(9.94, -18.08) * mm, "end": v(9.76, -17.74) * mm});
            skLineSegment(sketch, "E693", {"start": v(9.76, -17.74) * mm, "end": v(9.59, -17.4) * mm});
            skLineSegment(sketch, "E694", {"start": v(9.59, -17.4) * mm, "end": v(9.37, -16.98) * mm});
            skLineSegment(sketch, "E695", {"start": v(9.37, -16.98) * mm, "end": v(9.2, -16.64) * mm});
            skLineSegment(sketch, "E696", {"start": v(9.2, -16.64) * mm, "end": v(8.99, -16.2) * mm});
            skLineSegment(sketch, "E697", {"start": v(8.99, -16.2) * mm, "end": v(8.79, -15.77) * mm});
            skLineSegment(sketch, "E698", {"start": v(8.79, -15.77) * mm, "end": v(8.63, -15.43) * mm});
            skLineSegment(sketch, "E699", {"start": v(8.63, -15.43) * mm, "end": v(8.44, -14.99) * mm});
            skLineSegment(sketch, "E700", {"start": v(8.44, -14.99) * mm, "end": v(8.3, -14.64) * mm});
            skLineSegment(sketch, "E701", {"start": v(8.3, -14.64) * mm, "end": v(8.12, -14.2) * mm});
            skLineSegment(sketch, "E702", {"start": v(8.12, -14.2) * mm, "end": v(7.97, -13.84) * mm});
            skLineSegment(sketch, "E703", {"start": v(7.97, -13.84) * mm, "end": v(7.77, -13.3) * mm});
            skLineSegment(sketch, "E704", {"start": v(7.77, -13.3) * mm, "end": v(7.67, -13.02) * mm});
            skLineSegment(sketch, "E705", {"start": v(7.67, -13.02) * mm, "end": v(7.57, -12.74) * mm});
            skLineSegment(sketch, "E706", {"start": v(7.57, -12.74) * mm, "end": v(7.4, -12.22) * mm});
            skLineSegment(sketch, "E707", {"start": v(7.4, -12.22) * mm, "end": v(7.3, -11.94) * mm});
            skLineSegment(sketch, "E708", {"start": v(7.3, -11.94) * mm, "end": v(7.08, -11.2) * mm});
            skLineSegment(sketch, "E709", {"start": v(7.08, -11.2) * mm, "end": v(7, -10.92) * mm});
            skLineSegment(sketch, "E710", {"start": v(7, -10.92) * mm, "end": v(6.92, -10.64) * mm});
            skLineSegment(sketch, "E711", {"start": v(6.92, -10.64) * mm, "end": v(6.8, -10.21) * mm});
            skLineSegment(sketch, "E712", {"start": v(6.8, -10.21) * mm, "end": v(6.68, -9.75) * mm});
            skLineSegment(sketch, "E713", {"start": v(6.68, -9.75) * mm, "end": v(6.57, -9.28) * mm});
            skLineSegment(sketch, "E714", {"start": v(6.57, -9.28) * mm, "end": v(6.48, -8.91) * mm});
            skLineSegment(sketch, "E715", {"start": v(6.48, -8.91) * mm, "end": v(6.4, -8.54) * mm});
            skLineSegment(sketch, "E716", {"start": v(6.4, -8.54) * mm, "end": v(6.3, -8.07) * mm});
            skLineSegment(sketch, "E717", {"start": v(6.3, -8.07) * mm, "end": v(6.23, -7.7) * mm});
            skLineSegment(sketch, "E718", {"start": v(6.23, -7.7) * mm, "end": v(6.14, -7.23) * mm});
            skLineSegment(sketch, "E719", {"start": v(6.14, -7.23) * mm, "end": v(6.07, -6.75) * mm});
            skLineSegment(sketch, "E720", {"start": v(6.07, -6.75) * mm, "end": v(6, -6.38) * mm});
            skLineSegment(sketch, "E721", {"start": v(6, -6.38) * mm, "end": v(5.96, -6) * mm});
            skLineSegment(sketch, "E722", {"start": v(5.96, -6) * mm, "end": v(5.9, -5.53) * mm});
            skLineSegment(sketch, "E723", {"start": v(5.9, -5.53) * mm, "end": v(5.85, -5.15) * mm});
            skLineSegment(sketch, "E724", {"start": v(5.85, -5.15) * mm, "end": v(5.8, -4.67) * mm});
            skLineSegment(sketch, "E725", {"start": v(5.8, -4.67) * mm, "end": v(5.76, -4.3) * mm});
            skLineSegment(sketch, "E726", {"start": v(5.76, -4.3) * mm, "end": v(5.72, -3.82) * mm});
            skLineSegment(sketch, "E727", {"start": v(5.72, -3.82) * mm, "end": v(5.7, -3.44) * mm});
            skLineSegment(sketch, "E728", {"start": v(5.7, -3.44) * mm, "end": v(5.67, -2.96) * mm});
            skLineSegment(sketch, "E729", {"start": v(5.67, -2.96) * mm, "end": v(5.66, -2.58) * mm});
            skLineSegment(sketch, "E730", {"start": v(5.66, -2.58) * mm, "end": v(5.64, -2.1) * mm});
            skLineSegment(sketch, "E731", {"start": v(5.64, -2.1) * mm, "end": v(5.63, -1.72) * mm});
            skLineSegment(sketch, "E732", {"start": v(5.63, -1.72) * mm, "end": v(5.63, -1.24) * mm});
            skLineSegment(sketch, "E733", {"start": v(5.63, -1.24) * mm, "end": v(5.63, -0.86) * mm});
            skLineSegment(sketch, "E734", {"start": v(5.63, -0.86) * mm, "end": v(5.64, -0.38) * mm});
            skLineSegment(sketch, "E735", {"start": v(5.64, -0.38) * mm, "end": v(5.65, 0) * mm});
            skLineSegment(sketch, "E736", {"start": v(5.65, 0) * mm, "end": v(5.67, 0.47) * mm});
            skLineSegment(sketch, "E737", {"start": v(5.67, 0.47) * mm, "end": v(5.7, 0.85) * mm});
            skLineSegment(sketch, "E738", {"start": v(5.7, 0.85) * mm, "end": v(5.77, 1.7) * mm});
            skLineSegment(sketch, "E739", {"start": v(5.77, 1.7) * mm, "end": v(5.8, 2.12) * mm});
            skLineSegment(sketch, "E740", {"start": v(5.8, 2.12) * mm, "end": v(5.81, 2.13) * mm});
            skLineSegment(sketch, "E741", {"start": v(5.81, 2.13) * mm, "end": v(5.85, 2.55) * mm});
            skLineSegment(sketch, "E742", {"start": v(5.85, 2.55) * mm, "end": v(5.94, 2.55) * mm});
            skLineSegment(sketch, "E743", {"start": v(5.94, 2.55) * mm, "end": v(5.98, 2.9) * mm});
            skLineSegment(sketch, "E744", {"start": v(5.98, 2.9) * mm, "end": v(6.07, 2.9) * mm});
            skLineSegment(sketch, "E745", {"start": v(6.07, 2.9) * mm, "end": v(6.16, 2.89) * mm});
            skLineSegment(sketch, "E746", {"start": v(6.16, 2.89) * mm, "end": v(6.25, 2.9) * mm});
            skLineSegment(sketch, "E747", {"start": v(6.25, 2.9) * mm, "end": v(6.35, 2.9) * mm});
            skLineSegment(sketch, "E748", {"start": v(6.35, 2.9) * mm, "end": v(6.44, 2.9) * mm});
            skLineSegment(sketch, "E749", {"start": v(6.44, 2.9) * mm, "end": v(6.54, 2.9) * mm});
            skLineSegment(sketch, "E750", {"start": v(6.54, 2.9) * mm, "end": v(6.63, 2.92) * mm});
            skLineSegment(sketch, "E751", {"start": v(6.63, 2.92) * mm, "end": v(6.73, 2.93) * mm});
            skLineSegment(sketch, "E752", {"start": v(6.73, 2.93) * mm, "end": v(6.83, 2.95) * mm});
            skLineSegment(sketch, "E753", {"start": v(6.83, 2.95) * mm, "end": v(6.93, 2.97) * mm});
            skLineSegment(sketch, "E754", {"start": v(6.93, 2.97) * mm, "end": v(7.04, 2.99) * mm});
            skLineSegment(sketch, "E755", {"start": v(7.04, 2.99) * mm, "end": v(7.14, 3.01) * mm});
            skLineSegment(sketch, "E756", {"start": v(7.14, 3.01) * mm, "end": v(7.24, 3.04) * mm});
            skLineSegment(sketch, "E757", {"start": v(7.24, 3.04) * mm, "end": v(7.33, 3.03) * mm});
            skLineSegment(sketch, "E758", {"start": v(7.33, 3.03) * mm, "end": v(7.44, 3.06) * mm});
            skLineSegment(sketch, "E759", {"start": v(7.44, 3.06) * mm, "end": v(7.5, 3.06) * mm});
            skLineSegment(sketch, "E760", {"start": v(7.5, 3.06) * mm, "end": v(7.61, 3.1) * mm});
            skLineSegment(sketch, "E761", {"start": v(7.61, 3.1) * mm, "end": v(7.69, 3.09) * mm});
            skLineSegment(sketch, "E762", {"start": v(7.69, 3.09) * mm, "end": v(7.8, 3.12) * mm});
            skLineSegment(sketch, "E763", {"start": v(7.8, 3.12) * mm, "end": v(7.86, 3.13) * mm});
            skLineSegment(sketch, "E764", {"start": v(7.86, 3.13) * mm, "end": v(7.94, 3.13) * mm});
            skLineSegment(sketch, "E765", {"start": v(7.94, 3.13) * mm, "end": v(8.04, 3.17) * mm});
            skLineSegment(sketch, "E766", {"start": v(8.04, 3.17) * mm, "end": v(8.1, 3.17) * mm});
            skLineSegment(sketch, "E767", {"start": v(8.1, 3.17) * mm, "end": v(8.21, 3.21) * mm});
            skLineSegment(sketch, "E768", {"start": v(8.21, 3.21) * mm, "end": v(8.28, 3.22) * mm});
            skLineSegment(sketch, "E769", {"start": v(8.28, 3.22) * mm, "end": v(8.39, 3.26) * mm});
            skLineSegment(sketch, "E770", {"start": v(8.39, 3.26) * mm, "end": v(8.45, 3.27) * mm});
            skLineSegment(sketch, "E771", {"start": v(8.45, 3.27) * mm, "end": v(8.52, 3.28) * mm});
            skLineSegment(sketch, "E772", {"start": v(8.52, 3.28) * mm, "end": v(8.63, 3.32) * mm});
            skLineSegment(sketch, "E773", {"start": v(8.63, 3.32) * mm, "end": v(8.7, 3.33) * mm});
            skLineSegment(sketch, "E774", {"start": v(8.7, 3.33) * mm, "end": v(8.8, 3.38) * mm});
            skLineSegment(sketch, "E775", {"start": v(8.8, 3.38) * mm, "end": v(8.86, 3.4) * mm});
            skLineSegment(sketch, "E776", {"start": v(8.86, 3.4) * mm, "end": v(8.96, 3.45) * mm});
            skLineSegment(sketch, "E777", {"start": v(8.96, 3.45) * mm, "end": v(9.03, 3.46) * mm});
            skLineSegment(sketch, "E778", {"start": v(9.03, 3.46) * mm, "end": v(9.1, 3.48) * mm});
            skLineSegment(sketch, "E779", {"start": v(9.1, 3.48) * mm, "end": v(9.2, 3.53) * mm});
            skLineSegment(sketch, "E780", {"start": v(9.2, 3.53) * mm, "end": v(9.26, 3.55) * mm});
            skLineSegment(sketch, "E781", {"start": v(9.26, 3.55) * mm, "end": v(9.35, 3.6) * mm});
            skLineSegment(sketch, "E782", {"start": v(9.35, 3.6) * mm, "end": v(9.42, 3.62) * mm});
            skLineSegment(sketch, "E783", {"start": v(9.42, 3.62) * mm, "end": v(9.48, 3.64) * mm});
            skLineSegment(sketch, "E784", {"start": v(9.48, 3.64) * mm, "end": v(9.58, 3.7) * mm});
            skLineSegment(sketch, "E785", {"start": v(9.58, 3.7) * mm, "end": v(9.64, 3.72) * mm});
            skLineSegment(sketch, "E786", {"start": v(9.64, 3.72) * mm, "end": v(9.73, 3.79) * mm});
            skLineSegment(sketch, "E787", {"start": v(9.73, 3.79) * mm, "end": v(9.8, 3.8) * mm});
            skLineSegment(sketch, "E788", {"start": v(9.8, 3.8) * mm, "end": v(9.89, 3.87) * mm});
            skLineSegment(sketch, "E789", {"start": v(9.89, 3.87) * mm, "end": v(9.95, 3.9) * mm});
            skLineSegment(sketch, "E790", {"start": v(9.95, 3.9) * mm, "end": v(10, 3.92) * mm});
            skLineSegment(sketch, "E791", {"start": v(10, 3.92) * mm, "end": v(10.1, 4) * mm});
            skLineSegment(sketch, "E792", {"start": v(10.1, 4) * mm, "end": v(10.16, 4.02) * mm});
            skLineSegment(sketch, "E793", {"start": v(10.16, 4.02) * mm, "end": v(10.25, 4.09) * mm});
            skLineSegment(sketch, "E794", {"start": v(10.25, 4.09) * mm, "end": v(10.3, 4.11) * mm});
            skLineSegment(sketch, "E795", {"start": v(10.3, 4.11) * mm, "end": v(10.4, 4.19) * mm});
            skLineSegment(sketch, "E796", {"start": v(10.4, 4.19) * mm, "end": v(10.45, 4.21) * mm});
            skLineSegment(sketch, "E797", {"start": v(10.45, 4.21) * mm, "end": v(10.5, 4.24) * mm});
            skLineSegment(sketch, "E798", {"start": v(10.5, 4.24) * mm, "end": v(10.6, 4.32) * mm});
            skLineSegment(sketch, "E799", {"start": v(10.6, 4.32) * mm, "end": v(10.64, 4.35) * mm});
            skLineSegment(sketch, "E800", {"start": v(10.64, 4.35) * mm, "end": v(10.73, 4.43) * mm});
            skLineSegment(sketch, "E801", {"start": v(10.73, 4.43) * mm, "end": v(10.78, 4.46) * mm});
            skLineSegment(sketch, "E802", {"start": v(10.78, 4.46) * mm, "end": v(10.87, 4.54) * mm});
            skLineSegment(sketch, "E803", {"start": v(10.87, 4.54) * mm, "end": v(10.92, 4.57) * mm});
            skLineSegment(sketch, "E804", {"start": v(10.92, 4.57) * mm, "end": v(10.97, 4.6) * mm});
            skLineSegment(sketch, "E805", {"start": v(10.97, 4.6) * mm, "end": v(11.05, 4.69) * mm});
            skLineSegment(sketch, "E806", {"start": v(11.05, 4.69) * mm, "end": v(11.1, 4.72) * mm});
            skLineSegment(sketch, "E807", {"start": v(11.1, 4.72) * mm, "end": v(11.18, 4.8) * mm});
            skLineSegment(sketch, "E808", {"start": v(11.18, 4.8) * mm, "end": v(11.22, 4.84) * mm});
            skLineSegment(sketch, "E809", {"start": v(11.22, 4.84) * mm, "end": v(11.3, 4.93) * mm});
            skLineSegment(sketch, "E810", {"start": v(11.3, 4.93) * mm, "end": v(11.35, 4.96) * mm});
            skLineSegment(sketch, "E811", {"start": v(11.35, 4.96) * mm, "end": v(11.4, 5) * mm});
            skLineSegment(sketch, "E812", {"start": v(11.4, 5) * mm, "end": v(11.47, 5.09) * mm});
            skLineSegment(sketch, "E813", {"start": v(11.47, 5.09) * mm, "end": v(11.51, 5.13) * mm});
            skLineSegment(sketch, "E814", {"start": v(11.51, 5.13) * mm, "end": v(11.59, 5.22) * mm});
            skLineSegment(sketch, "E815", {"start": v(11.59, 5.22) * mm, "end": v(11.63, 5.26) * mm});
            skLineSegment(sketch, "E816", {"start": v(11.63, 5.26) * mm, "end": v(11.7, 5.35) * mm});
            skLineSegment(sketch, "E817", {"start": v(11.7, 5.35) * mm, "end": v(11.74, 5.39) * mm});
            skLineSegment(sketch, "E818", {"start": v(11.74, 5.39) * mm, "end": v(11.78, 5.43) * mm});
            skLineSegment(sketch, "E819", {"start": v(11.78, 5.43) * mm, "end": v(11.85, 5.52) * mm});
            skLineSegment(sketch, "E820", {"start": v(11.85, 5.52) * mm, "end": v(11.9, 5.56) * mm});
            skLineSegment(sketch, "E821", {"start": v(11.9, 5.56) * mm, "end": v(11.96, 5.66) * mm});
            skLineSegment(sketch, "E822", {"start": v(11.96, 5.66) * mm, "end": v(12, 5.7) * mm});
            skLineSegment(sketch, "E823", {"start": v(12, 5.7) * mm, "end": v(12.28, 6.11) * mm});
            skLineSegment(sketch, "E824", {"start": v(12.28, 6.11) * mm, "end": v(12.33, 6.18) * mm});
            skLineSegment(sketch, "E825", {"start": v(12.33, 6.18) * mm, "end": v(12.38, 6.25) * mm});
            skLineSegment(sketch, "E826", {"start": v(12.38, 6.25) * mm, "end": v(12.42, 6.33) * mm});
            skLineSegment(sketch, "E827", {"start": v(12.42, 6.33) * mm, "end": v(12.46, 6.4) * mm});
            skLineSegment(sketch, "E828", {"start": v(12.46, 6.4) * mm, "end": v(12.5, 6.48) * mm});
            skLineSegment(sketch, "E829", {"start": v(12.5, 6.48) * mm, "end": v(12.54, 6.54) * mm});
            skLineSegment(sketch, "E830", {"start": v(12.54, 6.54) * mm, "end": v(12.58, 6.61) * mm});
            skLineSegment(sketch, "E831", {"start": v(12.58, 6.61) * mm, "end": v(12.62, 6.69) * mm});
            skLineSegment(sketch, "E832", {"start": v(12.62, 6.69) * mm, "end": v(12.66, 6.77) * mm});
            skLineSegment(sketch, "E833", {"start": v(12.66, 6.77) * mm, "end": v(12.7, 6.84) * mm});
            skLineSegment(sketch, "E834", {"start": v(12.7, 6.84) * mm, "end": v(12.73, 6.92) * mm});
            skLineSegment(sketch, "E835", {"start": v(12.73, 6.92) * mm, "end": v(12.77, 7) * mm});
            skLineSegment(sketch, "E836", {"start": v(12.77, 7) * mm, "end": v(12.8, 7.08) * mm});
            skLineSegment(sketch, "E837", {"start": v(12.8, 7.08) * mm, "end": v(12.84, 7.16) * mm});
            skLineSegment(sketch, "E838", {"start": v(12.84, 7.16) * mm, "end": v(12.87, 7.23) * mm});
            skLineSegment(sketch, "E839", {"start": v(12.87, 7.23) * mm, "end": v(12.9, 7.32) * mm});
            skLineSegment(sketch, "E840", {"start": v(12.9, 7.32) * mm, "end": v(12.93, 7.4) * mm});
            skLineSegment(sketch, "E841", {"start": v(12.93, 7.4) * mm, "end": v(12.96, 7.48) * mm});
            skLineSegment(sketch, "E842", {"start": v(12.96, 7.48) * mm, "end": v(13, 7.56) * mm});
            skLineSegment(sketch, "E843", {"start": v(13, 7.56) * mm, "end": v(13.02, 7.64) * mm});
            skLineSegment(sketch, "E844", {"start": v(13.02, 7.64) * mm, "end": v(13.05, 7.72) * mm});
            skLineSegment(sketch, "E845", {"start": v(13.05, 7.72) * mm, "end": v(13.07, 7.8) * mm});
            skLineSegment(sketch, "E846", {"start": v(13.07, 7.8) * mm, "end": v(13.1, 7.88) * mm});
            skLineSegment(sketch, "E847", {"start": v(13.1, 7.88) * mm, "end": v(13.12, 7.96) * mm});
            skLineSegment(sketch, "E848", {"start": v(13.12, 7.96) * mm, "end": v(13.15, 8.05) * mm});
            skLineSegment(sketch, "E849", {"start": v(13.15, 8.05) * mm, "end": v(13.17, 8.13) * mm});
            skLineSegment(sketch, "E850", {"start": v(13.17, 8.13) * mm, "end": v(13.19, 8.21) * mm});
            skLineSegment(sketch, "E851", {"start": v(13.19, 8.21) * mm, "end": v(13.2, 8.3) * mm});
            skLineSegment(sketch, "E852", {"start": v(13.2, 8.3) * mm, "end": v(13.23, 8.38) * mm});
            skLineSegment(sketch, "E853", {"start": v(13.23, 8.38) * mm, "end": v(13.25, 8.46) * mm});
            skLineSegment(sketch, "E854", {"start": v(13.25, 8.46) * mm, "end": v(13.26, 8.55) * mm});
            skLineSegment(sketch, "E855", {"start": v(13.26, 8.55) * mm, "end": v(13.28, 8.63) * mm});
            skLineSegment(sketch, "E856", {"start": v(13.28, 8.63) * mm, "end": v(13.3, 8.72) * mm});
            skLineSegment(sketch, "E857", {"start": v(13.3, 8.72) * mm, "end": v(13.3, 8.8) * mm});
            skLineSegment(sketch, "E858", {"start": v(13.3, 8.8) * mm, "end": v(13.32, 8.89) * mm});
            skLineSegment(sketch, "E859", {"start": v(13.32, 8.89) * mm, "end": v(13.33, 8.97) * mm});
            skLineSegment(sketch, "E860", {"start": v(13.33, 8.97) * mm, "end": v(13.34, 9.04) * mm});
            skLineSegment(sketch, "E861", {"start": v(13.34, 9.04) * mm, "end": v(13.35, 9.13) * mm});
            skLineSegment(sketch, "E862", {"start": v(13.35, 9.13) * mm, "end": v(13.36, 9.21) * mm});
            skLineSegment(sketch, "E863", {"start": v(13.36, 9.21) * mm, "end": v(13.37, 9.3) * mm});
            skLineSegment(sketch, "E864", {"start": v(13.37, 9.3) * mm, "end": v(13.37, 9.4) * mm});
            skLineSegment(sketch, "E865", {"start": v(13.37, 9.4) * mm, "end": v(13.38, 9.46) * mm});
            skLineSegment(sketch, "E866", {"start": v(13.38, 9.46) * mm, "end": v(13.38, 9.57) * mm});
            skLineSegment(sketch, "E867", {"start": v(13.38, 9.57) * mm, "end": v(13.39, 9.63) * mm});
            skLineSegment(sketch, "E868", {"start": v(13.39, 9.63) * mm, "end": v(13.39, 9.74) * mm});
            skLineSegment(sketch, "E869", {"start": v(13.39, 9.74) * mm, "end": v(13.39, 9.8) * mm});
            skLineSegment(sketch, "E870", {"start": v(13.39, 9.8) * mm, "end": v(13.4, 9.92) * mm});
            skLineSegment(sketch, "E871", {"start": v(13.4, 9.92) * mm, "end": v(13.39, 9.97) * mm});
            skLineSegment(sketch, "E872", {"start": v(13.39, 9.97) * mm, "end": v(13.39, 10.09) * mm});
            skLineSegment(sketch, "E873", {"start": v(13.39, 10.09) * mm, "end": v(13.39, 10.14) * mm});
            skLineSegment(sketch, "E874", {"start": v(13.39, 10.14) * mm, "end": v(13.38, 10.26) * mm});
            skLineSegment(sketch, "E875", {"start": v(13.38, 10.26) * mm, "end": v(13.38, 10.32) * mm});
            skLineSegment(sketch, "E876", {"start": v(13.38, 10.32) * mm, "end": v(13.37, 10.43) * mm});
            skLineSegment(sketch, "E877", {"start": v(13.37, 10.43) * mm, "end": v(13.36, 10.49) * mm});
            skLineSegment(sketch, "E878", {"start": v(13.36, 10.49) * mm, "end": v(13.35, 10.6) * mm});
            skLineSegment(sketch, "E879", {"start": v(13.35, 10.6) * mm, "end": v(13.35, 10.66) * mm});
            skLineSegment(sketch, "E880", {"start": v(13.35, 10.66) * mm, "end": v(13.33, 10.77) * mm});
            skLineSegment(sketch, "E881", {"start": v(13.33, 10.77) * mm, "end": v(13.33, 10.83) * mm});
            skLineSegment(sketch, "E882", {"start": v(13.33, 10.83) * mm, "end": v(13.3, 10.94) * mm});
            skLineSegment(sketch, "E883", {"start": v(13.3, 10.94) * mm, "end": v(13.3, 11) * mm});
            skLineSegment(sketch, "E884", {"start": v(13.3, 11) * mm, "end": v(13.28, 11.11) * mm});
            skLineSegment(sketch, "E885", {"start": v(13.28, 11.11) * mm, "end": v(13.27, 11.17) * mm});
            skLineSegment(sketch, "E886", {"start": v(13.27, 11.17) * mm, "end": v(13.25, 11.28) * mm});
            skLineSegment(sketch, "E887", {"start": v(13.25, 11.28) * mm, "end": v(13.24, 11.34) * mm});
            skLineSegment(sketch, "E888", {"start": v(13.24, 11.34) * mm, "end": v(13.21, 11.45) * mm});
            skLineSegment(sketch, "E889", {"start": v(13.21, 11.45) * mm, "end": v(13.2, 11.5) * mm});
            skLineSegment(sketch, "E890", {"start": v(13.2, 11.5) * mm, "end": v(13.17, 11.62) * mm});
            skLineSegment(sketch, "E891", {"start": v(13.17, 11.62) * mm, "end": v(13.16, 11.68) * mm});
            skLineSegment(sketch, "E892", {"start": v(13.16, 11.68) * mm, "end": v(13.13, 11.78) * mm});
            skLineSegment(sketch, "E893", {"start": v(13.13, 11.78) * mm, "end": v(13.11, 11.84) * mm});
            skLineSegment(sketch, "E894", {"start": v(13.11, 11.84) * mm, "end": v(13.08, 11.95) * mm});
            skLineSegment(sketch, "E895", {"start": v(13.08, 11.95) * mm, "end": v(13.06, 12) * mm});
            skLineSegment(sketch, "E896", {"start": v(13.06, 12) * mm, "end": v(13.03, 12.1) * mm});
            skLineSegment(sketch, "E897", {"start": v(13.03, 12.1) * mm, "end": v(13, 12.17) * mm});
            skLineSegment(sketch, "E898", {"start": v(13, 12.17) * mm, "end": v(12.97, 12.27) * mm});
            skLineSegment(sketch, "E899", {"start": v(12.97, 12.27) * mm, "end": v(12.95, 12.33) * mm});
            skLineSegment(sketch, "E900", {"start": v(12.95, 12.33) * mm, "end": v(12.9, 12.43) * mm});
            skLineSegment(sketch, "E901", {"start": v(12.9, 12.43) * mm, "end": v(12.88, 12.5) * mm});
            skLineSegment(sketch, "E902", {"start": v(12.88, 12.5) * mm, "end": v(12.84, 12.6) * mm});
            skLineSegment(sketch, "E903", {"start": v(12.84, 12.6) * mm, "end": v(12.82, 12.65) * mm});
            skLineSegment(sketch, "E904", {"start": v(12.82, 12.65) * mm, "end": v(12.78, 12.75) * mm});
            skLineSegment(sketch, "E905", {"start": v(12.78, 12.75) * mm, "end": v(12.75, 12.8) * mm});
            skLineSegment(sketch, "E906", {"start": v(12.75, 12.8) * mm, "end": v(12.7, 12.9) * mm});
            skLineSegment(sketch, "E907", {"start": v(12.7, 12.9) * mm, "end": v(12.67, 12.97) * mm});
            skLineSegment(sketch, "E908", {"start": v(12.67, 12.97) * mm, "end": v(12.63, 13.06) * mm});
            skLineSegment(sketch, "E909", {"start": v(12.63, 13.06) * mm, "end": v(12.6, 13.12) * mm});
            skLineSegment(sketch, "E910", {"start": v(12.6, 13.12) * mm, "end": v(12.55, 13.21) * mm});
            skLineSegment(sketch, "E911", {"start": v(12.55, 13.21) * mm, "end": v(12.51, 13.27) * mm});
            skLineSegment(sketch, "E912", {"start": v(12.51, 13.27) * mm, "end": v(12.46, 13.36) * mm});
            skLineSegment(sketch, "E913", {"start": v(12.46, 13.36) * mm, "end": v(12.43, 13.42) * mm});
            skLineSegment(sketch, "E914", {"start": v(12.43, 13.42) * mm, "end": v(12.38, 13.5) * mm});
            skLineSegment(sketch, "E915", {"start": v(12.38, 13.5) * mm, "end": v(12.34, 13.57) * mm});
            skLineSegment(sketch, "E916", {"start": v(12.34, 13.57) * mm, "end": v(12.29, 13.65) * mm});
            skLineSegment(sketch, "E917", {"start": v(12.29, 13.65) * mm, "end": v(12.25, 13.71) * mm});
            skLineSegment(sketch, "E918", {"start": v(12.25, 13.71) * mm, "end": v(12.2, 13.8) * mm});
            skLineSegment(sketch, "E919", {"start": v(12.2, 13.8) * mm, "end": v(12.15, 13.86) * mm});
            skLineSegment(sketch, "E920", {"start": v(12.15, 13.86) * mm, "end": v(12.1, 13.94) * mm});
            skLineSegment(sketch, "E921", {"start": v(12.1, 13.94) * mm, "end": v(12.05, 14) * mm});
            skLineSegment(sketch, "E922", {"start": v(12.05, 14) * mm, "end": v(12, 14.08) * mm});
            skLineSegment(sketch, "E923", {"start": v(12, 14.08) * mm, "end": v(11.95, 14.14) * mm});
            skLineSegment(sketch, "E924", {"start": v(11.95, 14.14) * mm, "end": v(11.89, 14.21) * mm});
            skLineSegment(sketch, "E925", {"start": v(11.89, 14.21) * mm, "end": v(11.84, 14.27) * mm});
            skLineSegment(sketch, "E926", {"start": v(11.84, 14.27) * mm, "end": v(11.78, 14.35) * mm});
            skLineSegment(sketch, "E927", {"start": v(11.78, 14.35) * mm, "end": v(11.73, 14.4) * mm});
            skLineSegment(sketch, "E928", {"start": v(11.73, 14.4) * mm, "end": v(11.67, 14.48) * mm});
            skLineSegment(sketch, "E929", {"start": v(11.67, 14.48) * mm, "end": v(11.62, 14.54) * mm});
            skLineSegment(sketch, "E930", {"start": v(11.62, 14.54) * mm, "end": v(11.55, 14.6) * mm});
            skLineSegment(sketch, "E931", {"start": v(11.55, 14.6) * mm, "end": v(11.5, 14.66) * mm});
            skLineSegment(sketch, "E932", {"start": v(11.5, 14.66) * mm, "end": v(11.44, 14.73) * mm});
            skLineSegment(sketch, "E933", {"start": v(11.44, 14.73) * mm, "end": v(11.38, 14.79) * mm});
            skLineSegment(sketch, "E934", {"start": v(11.38, 14.79) * mm, "end": v(11.32, 14.85) * mm});
            skLineSegment(sketch, "E935", {"start": v(11.32, 14.85) * mm, "end": v(11.26, 14.9) * mm});
            skLineSegment(sketch, "E936", {"start": v(11.26, 14.9) * mm, "end": v(11.2, 14.97) * mm});
            skLineSegment(sketch, "E937", {"start": v(11.2, 14.97) * mm, "end": v(11.13, 15.03) * mm});
            skLineSegment(sketch, "E938", {"start": v(11.13, 15.03) * mm, "end": v(11.07, 15.1) * mm});
            skLineSegment(sketch, "E939", {"start": v(11.07, 15.1) * mm, "end": v(11, 15.14) * mm});
            skLineSegment(sketch, "E940", {"start": v(11, 15.14) * mm, "end": v(10.94, 15.2) * mm});
            skLineSegment(sketch, "E941", {"start": v(10.94, 15.2) * mm, "end": v(10.87, 15.26) * mm});
            skLineSegment(sketch, "E942", {"start": v(10.87, 15.26) * mm, "end": v(10.8, 15.31) * mm});
            skLineSegment(sketch, "E943", {"start": v(10.8, 15.31) * mm, "end": v(10.74, 15.36) * mm});
            skLineSegment(sketch, "E944", {"start": v(10.74, 15.36) * mm, "end": v(10.67, 15.42) * mm});
            skLineSegment(sketch, "E945", {"start": v(10.67, 15.42) * mm, "end": v(10.6, 15.47) * mm});
            skLineSegment(sketch, "E946", {"start": v(10.6, 15.47) * mm, "end": v(10.53, 15.52) * mm});
            skLineSegment(sketch, "E947", {"start": v(10.53, 15.52) * mm, "end": v(10.46, 15.57) * mm});
            skLineSegment(sketch, "E948", {"start": v(10.46, 15.57) * mm, "end": v(10.4, 15.62) * mm});
            skLineSegment(sketch, "E949", {"start": v(10.4, 15.62) * mm, "end": v(10.32, 15.67) * mm});
            skLineSegment(sketch, "E950", {"start": v(10.32, 15.67) * mm, "end": v(10.25, 15.72) * mm});
            skLineSegment(sketch, "E951", {"start": v(10.25, 15.72) * mm, "end": v(10.18, 15.77) * mm});
            skLineSegment(sketch, "E952", {"start": v(10.18, 15.77) * mm, "end": v(10.1, 15.81) * mm});
            skLineSegment(sketch, "E953", {"start": v(10.1, 15.81) * mm, "end": v(10.1, 15.82) * mm});
            skLineSegment(sketch, "E954", {"start": v(10.1, 15.82) * mm, "end": v(10.08, 15.83) * mm});
            skLineSegment(sketch, "E955", {"start": v(10.08, 15.83) * mm, "end": v(10.33, 16.27) * mm});
            skLineSegment(sketch, "E956", {"start": v(10.33, 16.27) * mm, "end": v(10.36, 16.33) * mm});
            skLineSegment(sketch, "E957", {"start": v(10.36, 16.33) * mm, "end": v(10.6, 16.75) * mm});
            skLineSegment(sketch, "E958", {"start": v(10.6, 16.75) * mm, "end": v(10.7, 16.9) * mm});
            skLineSegment(sketch, "E959", {"start": v(10.7, 16.9) * mm, "end": v(10.85, 17.14) * mm});
            skLineSegment(sketch, "E960", {"start": v(10.85, 17.14) * mm, "end": v(10.89, 17.2) * mm});
            skLineSegment(sketch, "E961", {"start": v(10.89, 17.2) * mm, "end": v(11.06, 17.48) * mm});
            skLineSegment(sketch, "E962", {"start": v(11.06, 17.48) * mm, "end": v(11.18, 17.67) * mm});
            skLineSegment(sketch, "E963", {"start": v(11.18, 17.67) * mm, "end": v(11.35, 17.93) * mm});
            skLineSegment(sketch, "E964", {"start": v(11.35, 17.93) * mm, "end": v(11.53, 18.2) * mm});
            skLineSegment(sketch, "E965", {"start": v(11.53, 18.2) * mm, "end": v(11.7, 18.46) * mm});
            skLineSegment(sketch, "E966", {"start": v(11.7, 18.46) * mm, "end": v(11.9, 18.73) * mm});
            skLineSegment(sketch, "E967", {"start": v(11.9, 18.73) * mm, "end": v(12.08, 18.99) * mm});
            skLineSegment(sketch, "E968", {"start": v(12.08, 18.99) * mm, "end": v(12.27, 19.24) * mm});
            skLineSegment(sketch, "E969", {"start": v(12.27, 19.24) * mm, "end": v(12.4, 19.43) * mm});
            skLineSegment(sketch, "E970", {"start": v(12.4, 19.43) * mm, "end": v(12.46, 19.5) * mm});
            skLineSegment(sketch, "E971", {"start": v(12.46, 19.5) * mm, "end": v(12.63, 19.75) * mm});
            skLineSegment(sketch, "E972", {"start": v(12.63, 19.75) * mm, "end": v(12.73, 19.88) * mm});
            skLineSegment(sketch, "E973", {"start": v(12.73, 19.88) * mm, "end": v(12.78, 19.95) * mm});
            skLineSegment(sketch, "E974", {"start": v(12.78, 19.95) * mm, "end": v(12.9, 20.11) * mm});
            skLineSegment(sketch, "E975", {"start": v(12.9, 20.11) * mm, "end": v(13.04, 20.29) * mm});
            skLineSegment(sketch, "E976", {"start": v(13.04, 20.29) * mm, "end": v(13.34, 20.66) * mm});
            skLineSegment(sketch, "E977", {"start": v(13.34, 20.66) * mm, "end": v(13.57, 20.96) * mm});
            skLineSegment(sketch, "E978", {"start": v(13.57, 20.96) * mm, "end": v(13.88, 21.33) * mm});
            skLineSegment(sketch, "E979", {"start": v(13.88, 21.33) * mm, "end": v(14.13, 21.62) * mm});
            skLineSegment(sketch, "E980", {"start": v(14.13, 21.62) * mm, "end": v(14.44, 21.98) * mm});
            skLineSegment(sketch, "E981", {"start": v(14.44, 21.98) * mm, "end": v(14.7, 22.26) * mm});
            skLineSegment(sketch, "E982", {"start": v(14.7, 22.26) * mm, "end": v(15.02, 22.61) * mm});
            skLineSegment(sketch, "E983", {"start": v(15.02, 22.61) * mm, "end": v(15.28, 22.89) * mm});
            skLineSegment(sketch, "E984", {"start": v(15.28, 22.89) * mm, "end": v(15.62, 23.23) * mm});
            skLineSegment(sketch, "E985", {"start": v(15.62, 23.23) * mm, "end": v(15.88, 23.5) * mm});
            skLineSegment(sketch, "E986", {"start": v(15.88, 23.5) * mm, "end": v(16.15, 23.77) * mm});
            skLineSegment(sketch, "E987", {"start": v(16.15, 23.77) * mm, "end": v(16.5, 24.1) * mm});
            skLineSegment(sketch, "E988", {"start": v(16.5, 24.1) * mm, "end": v(16.77, 24.36) * mm});
            skLineSegment(sketch, "E989", {"start": v(16.77, 24.36) * mm, "end": v(17.12, 24.69) * mm});
            skLineSegment(sketch, "E990", {"start": v(17.12, 24.69) * mm, "end": v(17.4, 24.94) * mm});
            skLineSegment(sketch, "E991", {"start": v(17.4, 24.94) * mm, "end": v(17.77, 25.26) * mm});
            skLineSegment(sketch, "E992", {"start": v(17.77, 25.26) * mm, "end": v(18.74, 26.05) * mm});
            skLineSegment(sketch, "E993", {"start": v(18.74, 26.05) * mm, "end": v(18.97, 26.24) * mm});
            skLineSegment(sketch, "E994", {"start": v(18.97, 26.24) * mm, "end": v(19.2, 26.42) * mm});
            skLineSegment(sketch, "E995", {"start": v(19.2, 26.42) * mm, "end": v(19.43, 26.6) * mm});
            skLineSegment(sketch, "E996", {"start": v(19.43, 26.6) * mm, "end": v(19.78, 26.87) * mm});
            skLineSegment(sketch, "E997", {"start": v(19.78, 26.87) * mm, "end": v(20.02, 27.04) * mm});
            skLineSegment(sketch, "E998", {"start": v(20.02, 27.04) * mm, "end": v(20.75, 27.56) * mm});
            skLineSegment(sketch, "E999", {"start": v(20.75, 27.56) * mm, "end": v(20.99, 27.72) * mm});
            skLineSegment(sketch, "E1000", {"start": v(20.99, 27.72) * mm, "end": v(21.23, 27.88) * mm});
            skLineSegment(sketch, "E1001", {"start": v(21.23, 27.88) * mm, "end": v(21.5, 28.06) * mm});
            skLineSegment(sketch, "E1002", {"start": v(21.5, 28.06) * mm, "end": v(21.9, 28.33) * mm});
            skLineSegment(sketch, "E1003", {"start": v(21.9, 28.33) * mm, "end": v(22.31, 28.58) * mm});
            skLineSegment(sketch, "E1004", {"start": v(22.31, 28.58) * mm, "end": v(22.64, 28.78) * mm});
            skLineSegment(sketch, "E1005", {"start": v(22.64, 28.78) * mm, "end": v(23.05, 29.02) * mm});
            skLineSegment(sketch, "E1006", {"start": v(23.05, 29.02) * mm, "end": v(23.38, 29.2) * mm});
            skLineSegment(sketch, "E1007", {"start": v(23.38, 29.2) * mm, "end": v(23.71, 29.4) * mm});
            skLineSegment(sketch, "E1008", {"start": v(23.71, 29.4) * mm, "end": v(24.13, 29.62) * mm});
            skLineSegment(sketch, "E1009", {"start": v(24.13, 29.62) * mm, "end": v(24.47, 29.8) * mm});
            skLineSegment(sketch, "E1010", {"start": v(24.47, 29.8) * mm, "end": v(24.9, 30.02) * mm});
            skLineSegment(sketch, "E1011", {"start": v(24.9, 30.02) * mm, "end": v(25.23, 30.19) * mm});
            skLineSegment(sketch, "E1012", {"start": v(25.23, 30.19) * mm, "end": v(25.66, 30.4) * mm});
            skLineSegment(sketch, "E1013", {"start": v(25.66, 30.4) * mm, "end": v(26.01, 30.55) * mm});
            skLineSegment(sketch, "E1014", {"start": v(26.01, 30.55) * mm, "end": v(26.45, 30.75) * mm});
            skLineSegment(sketch, "E1015", {"start": v(26.45, 30.75) * mm, "end": v(26.8, 30.9) * mm});
            skLineSegment(sketch, "E1016", {"start": v(26.8, 30.9) * mm, "end": v(27.24, 31.1) * mm});
            skLineSegment(sketch, "E1017", {"start": v(27.24, 31.1) * mm, "end": v(27.59, 31.23) * mm});
            skLineSegment(sketch, "E1018", {"start": v(27.59, 31.23) * mm, "end": v(28.03, 31.41) * mm});
            skLineSegment(sketch, "E1019", {"start": v(28.03, 31.41) * mm, "end": v(28.39, 31.54) * mm});
            skLineSegment(sketch, "E1020", {"start": v(28.39, 31.54) * mm, "end": v(28.84, 31.7) * mm});
            skLineSegment(sketch, "E1021", {"start": v(28.84, 31.7) * mm, "end": v(29.3, 31.87) * mm});
            skLineSegment(sketch, "E1022", {"start": v(29.3, 31.87) * mm, "end": v(29.65, 31.99) * mm});
            skLineSegment(sketch, "E1023", {"start": v(29.65, 31.99) * mm, "end": v(30.01, 32.1) * mm});
            skLineSegment(sketch, "E1024", {"start": v(30.01, 32.1) * mm, "end": v(30.47, 32.25) * mm});
            skLineSegment(sketch, "E1025", {"start": v(30.47, 32.25) * mm, "end": v(30.83, 32.35) * mm});
            skLineSegment(sketch, "E1026", {"start": v(30.83, 32.35) * mm, "end": v(31.3, 32.49) * mm});
            skLineSegment(sketch, "E1027", {"start": v(31.3, 32.49) * mm, "end": v(31.66, 32.58) * mm});
            skLineSegment(sketch, "E1028", {"start": v(31.66, 32.58) * mm, "end": v(32.57, 32.79) * mm});
            skLineSegment(sketch, "E1029", {"start": v(32.57, 32.79) * mm, "end": v(32.98, 32.9) * mm});
            skLineSegment(sketch, "E1030", {"start": v(32.98, 32.9) * mm, "end": v(33.4, 33) * mm});
            skLineSegment(sketch, "E1031", {"start": v(33.4, 33) * mm, "end": v(33.4, 32.99) * mm});
            skLineSegment(sketch, "E1032", {"start": v(33.4, 32.99) * mm, "end": v(33.82, 33.07) * mm});
            skLineSegment(sketch, "E1033", {"start": v(33.82, 33.07) * mm, "end": v(33.84, 32.98) * mm});
            skLineSegment(sketch, "E1034", {"start": v(33.84, 32.98) * mm, "end": v(33.87, 32.9) * mm});
            skLineSegment(sketch, "E1035", {"start": v(33.87, 32.9) * mm, "end": v(33.9, 32.81) * mm});
            skLineSegment(sketch, "E1036", {"start": v(33.9, 32.81) * mm, "end": v(33.92, 32.73) * mm});
            skLineSegment(sketch, "E1037", {"start": v(33.92, 32.73) * mm, "end": v(33.96, 32.64) * mm});
            skLineSegment(sketch, "E1038", {"start": v(33.96, 32.64) * mm, "end": v(34, 32.55) * mm});
            skLineSegment(sketch, "E1039", {"start": v(34, 32.55) * mm, "end": v(34.03, 32.46) * mm});
            skLineSegment(sketch, "E1040", {"start": v(34.03, 32.46) * mm, "end": v(34.07, 32.37) * mm});
            skLineSegment(sketch, "E1041", {"start": v(34.07, 32.37) * mm, "end": v(34.11, 32.28) * mm});
            skLineSegment(sketch, "E1042", {"start": v(34.11, 32.28) * mm, "end": v(34.16, 32.2) * mm});
            skLineSegment(sketch, "E1043", {"start": v(34.16, 32.2) * mm, "end": v(34.2, 32.1) * mm});
            skLineSegment(sketch, "E1044", {"start": v(34.2, 32.1) * mm, "end": v(34.26, 32.01) * mm});
            skLineSegment(sketch, "E1045", {"start": v(34.26, 32.01) * mm, "end": v(34.31, 31.92) * mm});
            skLineSegment(sketch, "E1046", {"start": v(34.31, 31.92) * mm, "end": v(34.37, 31.83) * mm});
            skLineSegment(sketch, "E1047", {"start": v(34.37, 31.83) * mm, "end": v(34.38, 31.83) * mm});
            skLineSegment(sketch, "E1048", {"start": v(34.38, 31.83) * mm, "end": v(34.4, 31.74) * mm});
            skLineSegment(sketch, "E1049", {"start": v(34.4, 31.74) * mm, "end": v(34.47, 31.65) * mm});
            skLineSegment(sketch, "E1050", {"start": v(34.47, 31.65) * mm, "end": v(34.49, 31.58) * mm});
            skLineSegment(sketch, "E1051", {"start": v(34.49, 31.58) * mm, "end": v(34.55, 31.5) * mm});
            skLineSegment(sketch, "E1052", {"start": v(34.55, 31.5) * mm, "end": v(34.57, 31.42) * mm});
            skLineSegment(sketch, "E1053", {"start": v(34.57, 31.42) * mm, "end": v(34.64, 31.34) * mm});
            skLineSegment(sketch, "E1054", {"start": v(34.64, 31.34) * mm, "end": v(34.66, 31.27) * mm});
            skLineSegment(sketch, "E1055", {"start": v(34.66, 31.27) * mm, "end": v(34.68, 31.2) * mm});
            skLineSegment(sketch, "E1056", {"start": v(34.68, 31.2) * mm, "end": v(34.75, 31.11) * mm});
            skLineSegment(sketch, "E1057", {"start": v(34.75, 31.11) * mm, "end": v(34.78, 31.05) * mm});
            skLineSegment(sketch, "E1058", {"start": v(34.78, 31.05) * mm, "end": v(34.85, 30.96) * mm});
            skLineSegment(sketch, "E1059", {"start": v(34.85, 30.96) * mm, "end": v(34.88, 30.9) * mm});
            skLineSegment(sketch, "E1060", {"start": v(34.88, 30.9) * mm, "end": v(34.95, 30.81) * mm});
            skLineSegment(sketch, "E1061", {"start": v(34.95, 30.81) * mm, "end": v(34.98, 30.75) * mm});
            skLineSegment(sketch, "E1062", {"start": v(34.98, 30.75) * mm, "end": v(35, 30.69) * mm});
            skLineSegment(sketch, "E1063", {"start": v(35, 30.69) * mm, "end": v(35.08, 30.6) * mm});
            skLineSegment(sketch, "E1064", {"start": v(35.08, 30.6) * mm, "end": v(35.12, 30.54) * mm});
            skLineSegment(sketch, "E1065", {"start": v(35.12, 30.54) * mm, "end": v(35.2, 30.46) * mm});
            skLineSegment(sketch, "E1066", {"start": v(35.2, 30.46) * mm, "end": v(35.23, 30.4) * mm});
            skLineSegment(sketch, "E1067", {"start": v(35.23, 30.4) * mm, "end": v(35.3, 30.32) * mm});
            skLineSegment(sketch, "E1068", {"start": v(35.3, 30.32) * mm, "end": v(35.34, 30.26) * mm});
            skLineSegment(sketch, "E1069", {"start": v(35.34, 30.26) * mm, "end": v(35.37, 30.2) * mm});
            skLineSegment(sketch, "E1070", {"start": v(35.37, 30.2) * mm, "end": v(35.46, 30.13) * mm});
            skLineSegment(sketch, "E1071", {"start": v(35.46, 30.13) * mm, "end": v(35.5, 30.07) * mm});
            skLineSegment(sketch, "E1072", {"start": v(35.5, 30.07) * mm, "end": v(35.58, 30) * mm});
            skLineSegment(sketch, "E1073", {"start": v(35.58, 30) * mm, "end": v(35.61, 29.94) * mm});
            skLineSegment(sketch, "E1074", {"start": v(35.61, 29.94) * mm, "end": v(35.65, 29.9) * mm});
            skLineSegment(sketch, "E1075", {"start": v(35.65, 29.9) * mm, "end": v(35.74, 29.82) * mm});
            skLineSegment(sketch, "E1076", {"start": v(35.74, 29.82) * mm, "end": v(35.78, 29.76) * mm});
            skLineSegment(sketch, "E1077", {"start": v(35.78, 29.76) * mm, "end": v(35.87, 29.7) * mm});
            skLineSegment(sketch, "E1078", {"start": v(35.87, 29.7) * mm, "end": v(35.9, 29.64) * mm});
            skLineSegment(sketch, "E1079", {"start": v(35.9, 29.64) * mm, "end": v(36, 29.57) * mm});
            skLineSegment(sketch, "E1080", {"start": v(36, 29.57) * mm, "end": v(36.04, 29.52) * mm});
            skLineSegment(sketch, "E1081", {"start": v(36.04, 29.52) * mm, "end": v(36.08, 29.48) * mm});
            skLineSegment(sketch, "E1082", {"start": v(36.08, 29.48) * mm, "end": v(36.17, 29.4) * mm});
            skLineSegment(sketch, "E1083", {"start": v(36.17, 29.4) * mm, "end": v(36.22, 29.36) * mm});
            skLineSegment(sketch, "E1084", {"start": v(36.22, 29.36) * mm, "end": v(36.3, 29.3) * mm});
            skLineSegment(sketch, "E1085", {"start": v(36.3, 29.3) * mm, "end": v(36.35, 29.25) * mm});
            skLineSegment(sketch, "E1086", {"start": v(36.35, 29.25) * mm, "end": v(36.45, 29.19) * mm});
            skLineSegment(sketch, "E1087", {"start": v(36.45, 29.19) * mm, "end": v(36.5, 29.15) * mm});
            skLineSegment(sketch, "E1088", {"start": v(36.5, 29.15) * mm, "end": v(36.54, 29.1) * mm});
            skLineSegment(sketch, "E1089", {"start": v(36.54, 29.1) * mm, "end": v(36.64, 29.04) * mm});
            skLineSegment(sketch, "E1090", {"start": v(36.64, 29.04) * mm, "end": v(36.68, 29) * mm});
            skLineSegment(sketch, "E1091", {"start": v(36.68, 29) * mm, "end": v(36.78, 28.94) * mm});
            skLineSegment(sketch, "E1092", {"start": v(36.78, 28.94) * mm, "end": v(36.83, 28.9) * mm});
            skLineSegment(sketch, "E1093", {"start": v(36.83, 28.9) * mm, "end": v(36.93, 28.85) * mm});
            skLineSegment(sketch, "E1094", {"start": v(36.93, 28.85) * mm, "end": v(36.98, 28.81) * mm});
            skLineSegment(sketch, "E1095", {"start": v(36.98, 28.81) * mm, "end": v(37.03, 28.77) * mm});
            skLineSegment(sketch, "E1096", {"start": v(37.03, 28.77) * mm, "end": v(37.13, 28.72) * mm});
            skLineSegment(sketch, "E1097", {"start": v(37.13, 28.72) * mm, "end": v(37.18, 28.69) * mm});
            skLineSegment(sketch, "E1098", {"start": v(37.18, 28.69) * mm, "end": v(37.28, 28.64) * mm});
            skLineSegment(sketch, "E1099", {"start": v(37.28, 28.64) * mm, "end": v(37.33, 28.6) * mm});
            skLineSegment(sketch, "E1100", {"start": v(37.33, 28.6) * mm, "end": v(37.43, 28.55) * mm});
            skLineSegment(sketch, "E1101", {"start": v(37.43, 28.55) * mm, "end": v(37.48, 28.52) * mm});
            skLineSegment(sketch, "E1102", {"start": v(37.48, 28.52) * mm, "end": v(37.53, 28.5) * mm});
            skLineSegment(sketch, "E1103", {"start": v(37.53, 28.5) * mm, "end": v(37.64, 28.44) * mm});
            skLineSegment(sketch, "E1104", {"start": v(37.64, 28.44) * mm, "end": v(37.7, 28.42) * mm});
            skLineSegment(sketch, "E1105", {"start": v(37.7, 28.42) * mm, "end": v(37.8, 28.37) * mm});
            skLineSegment(sketch, "E1106", {"start": v(37.8, 28.37) * mm, "end": v(37.85, 28.34) * mm});
            skLineSegment(sketch, "E1107", {"start": v(37.85, 28.34) * mm, "end": v(37.96, 28.3) * mm});
            skLineSegment(sketch, "E1108", {"start": v(37.96, 28.3) * mm, "end": v(38, 28.28) * mm});
            skLineSegment(sketch, "E1109", {"start": v(38, 28.28) * mm, "end": v(38.06, 28.25) * mm});
            skLineSegment(sketch, "E1110", {"start": v(38.06, 28.25) * mm, "end": v(38.17, 28.21) * mm});
            skLineSegment(sketch, "E1111", {"start": v(38.17, 28.21) * mm, "end": v(38.22, 28.2) * mm});
            skLineSegment(sketch, "E1112", {"start": v(38.22, 28.2) * mm, "end": v(38.33, 28.15) * mm});
            skLineSegment(sketch, "E1113", {"start": v(38.33, 28.15) * mm, "end": v(38.39, 28.13) * mm});
            skLineSegment(sketch, "E1114", {"start": v(38.39, 28.13) * mm, "end": v(38.87, 27.99) * mm});
            skLineSegment(sketch, "E1115", {"start": v(38.87, 27.99) * mm, "end": v(38.95, 27.96) * mm});
            skLineSegment(sketch, "E1116", {"start": v(38.95, 27.96) * mm, "end": v(39.03, 27.94) * mm});
            skLineSegment(sketch, "E1117", {"start": v(39.03, 27.94) * mm, "end": v(39.11, 27.92) * mm});
            skLineSegment(sketch, "E1118", {"start": v(39.11, 27.92) * mm, "end": v(39.2, 27.9) * mm});
            skLineSegment(sketch, "E1119", {"start": v(39.2, 27.9) * mm, "end": v(39.28, 27.89) * mm});
            skLineSegment(sketch, "E1120", {"start": v(39.28, 27.89) * mm, "end": v(39.35, 27.87) * mm});
            skLineSegment(sketch, "E1121", {"start": v(39.35, 27.87) * mm, "end": v(39.44, 27.86) * mm});
            skLineSegment(sketch, "E1122", {"start": v(39.44, 27.86) * mm, "end": v(39.52, 27.84) * mm});
            skLineSegment(sketch, "E1123", {"start": v(39.52, 27.84) * mm, "end": v(39.6, 27.83) * mm});
            skLineSegment(sketch, "E1124", {"start": v(39.6, 27.83) * mm, "end": v(39.69, 27.82) * mm});
            skLineSegment(sketch, "E1125", {"start": v(39.69, 27.82) * mm, "end": v(39.77, 27.8) * mm});
            skLineSegment(sketch, "E1126", {"start": v(39.77, 27.8) * mm, "end": v(39.86, 27.8) * mm});
            skLineSegment(sketch, "E1127", {"start": v(39.86, 27.8) * mm, "end": v(39.94, 27.79) * mm});
            skLineSegment(sketch, "E1128", {"start": v(39.94, 27.79) * mm, "end": v(40.03, 27.78) * mm});
            skLineSegment(sketch, "E1129", {"start": v(40.03, 27.78) * mm, "end": v(40.11, 27.77) * mm});
            skLineSegment(sketch, "E1130", {"start": v(40.11, 27.77) * mm, "end": v(40.2, 27.77) * mm});
            skLineSegment(sketch, "E1131", {"start": v(40.2, 27.77) * mm, "end": v(40.29, 27.76) * mm});
            skLineSegment(sketch, "E1132", {"start": v(40.29, 27.76) * mm, "end": v(40.37, 27.76) * mm});
            skLineSegment(sketch, "E1133", {"start": v(40.37, 27.76) * mm, "end": v(40.46, 27.76) * mm});
            skLineSegment(sketch, "E1134", {"start": v(40.46, 27.76) * mm, "end": v(40.55, 27.76) * mm});
            skLineSegment(sketch, "E1135", {"start": v(40.55, 27.76) * mm, "end": v(40.63, 27.76) * mm});
            skLineSegment(sketch, "E1136", {"start": v(40.63, 27.76) * mm, "end": v(40.71, 27.76) * mm});
            skLineSegment(sketch, "E1137", {"start": v(40.71, 27.76) * mm, "end": v(40.8, 27.76) * mm});
            skLineSegment(sketch, "E1138", {"start": v(40.8, 27.76) * mm, "end": v(40.89, 27.76) * mm});
            skLineSegment(sketch, "E1139", {"start": v(40.89, 27.76) * mm, "end": v(40.97, 27.76) * mm});
            skLineSegment(sketch, "E1140", {"start": v(40.97, 27.76) * mm, "end": v(41.06, 27.77) * mm});
            skLineSegment(sketch, "E1141", {"start": v(41.06, 27.77) * mm, "end": v(41.14, 27.77) * mm});
            skLineSegment(sketch, "E1142", {"start": v(41.14, 27.77) * mm, "end": v(41.23, 27.78) * mm});
            skLineSegment(sketch, "E1143", {"start": v(41.23, 27.78) * mm, "end": v(41.32, 27.79) * mm});
            skLineSegment(sketch, "E1144", {"start": v(41.32, 27.79) * mm, "end": v(41.4, 27.8) * mm});
            skLineSegment(sketch, "E1145", {"start": v(41.4, 27.8) * mm, "end": v(41.49, 27.8) * mm});
            skLineSegment(sketch, "E1146", {"start": v(41.49, 27.8) * mm, "end": v(41.57, 27.82) * mm});
            skLineSegment(sketch, "E1147", {"start": v(41.57, 27.82) * mm, "end": v(41.66, 27.83) * mm});
            skLineSegment(sketch, "E1148", {"start": v(41.66, 27.83) * mm, "end": v(41.74, 27.85) * mm});
            skLineSegment(sketch, "E1149", {"start": v(41.74, 27.85) * mm, "end": v(41.83, 27.86) * mm});
            skLineSegment(sketch, "E1150", {"start": v(41.83, 27.86) * mm, "end": v(41.9, 27.87) * mm});
            skLineSegment(sketch, "E1151", {"start": v(41.9, 27.87) * mm, "end": v(41.98, 27.89) * mm});
            skLineSegment(sketch, "E1152", {"start": v(41.98, 27.89) * mm, "end": v(42.06, 27.9) * mm});
            skLineSegment(sketch, "E1153", {"start": v(42.06, 27.9) * mm, "end": v(42.15, 27.92) * mm});
            skLineSegment(sketch, "E1154", {"start": v(42.15, 27.92) * mm, "end": v(42.23, 27.94) * mm});
            skLineSegment(sketch, "E1155", {"start": v(42.23, 27.94) * mm, "end": v(42.31, 27.96) * mm});
            skLineSegment(sketch, "E1156", {"start": v(42.31, 27.96) * mm, "end": v(42.5, 28) * mm});
            skLineSegment(sketch, "E1157", {"start": v(42.5, 28) * mm, "end": v(42.55, 28.03) * mm});
            skLineSegment(sketch, "E1158", {"start": v(42.55, 28.03) * mm, "end": v(42.66, 28.06) * mm});
            skLineSegment(sketch, "E1159", {"start": v(42.66, 28.06) * mm, "end": v(42.71, 28.07) * mm});
            skLineSegment(sketch, "E1160", {"start": v(42.71, 28.07) * mm, "end": v(42.83, 28.1) * mm});
            skLineSegment(sketch, "E1161", {"start": v(42.83, 28.1) * mm, "end": v(42.88, 28.13) * mm});
            skLineSegment(sketch, "E1162", {"start": v(42.88, 28.13) * mm, "end": v(42.99, 28.17) * mm});
            skLineSegment(sketch, "E1163", {"start": v(42.99, 28.17) * mm, "end": v(43.04, 28.19) * mm});
            skLineSegment(sketch, "E1164", {"start": v(43.04, 28.19) * mm, "end": v(43.15, 28.23) * mm});
            skLineSegment(sketch, "E1165", {"start": v(43.15, 28.23) * mm, "end": v(43.2, 28.25) * mm});
            skLineSegment(sketch, "E1166", {"start": v(43.2, 28.25) * mm, "end": v(43.3, 28.29) * mm});
            skLineSegment(sketch, "E1167", {"start": v(43.3, 28.29) * mm, "end": v(43.36, 28.31) * mm});
            skLineSegment(sketch, "E1168", {"start": v(43.36, 28.31) * mm, "end": v(43.47, 28.36) * mm});
            skLineSegment(sketch, "E1169", {"start": v(43.47, 28.36) * mm, "end": v(43.52, 28.38) * mm});
            skLineSegment(sketch, "E1170", {"start": v(43.52, 28.38) * mm, "end": v(43.62, 28.43) * mm});
            skLineSegment(sketch, "E1171", {"start": v(43.62, 28.43) * mm, "end": v(43.68, 28.45) * mm});
            skLineSegment(sketch, "E1172", {"start": v(43.68, 28.45) * mm, "end": v(43.78, 28.5) * mm});
            skLineSegment(sketch, "E1173", {"start": v(43.78, 28.5) * mm, "end": v(43.83, 28.53) * mm});
            skLineSegment(sketch, "E1174", {"start": v(43.83, 28.53) * mm, "end": v(43.93, 28.58) * mm});
            skLineSegment(sketch, "E1175", {"start": v(43.93, 28.58) * mm, "end": v(43.98, 28.61) * mm});
            skLineSegment(sketch, "E1176", {"start": v(43.98, 28.61) * mm, "end": v(44.08, 28.67) * mm});
            skLineSegment(sketch, "E1177", {"start": v(44.08, 28.67) * mm, "end": v(44.13, 28.7) * mm});
            skLineSegment(sketch, "E1178", {"start": v(44.13, 28.7) * mm, "end": v(44.23, 28.75) * mm});
            skLineSegment(sketch, "E1179", {"start": v(44.23, 28.75) * mm, "end": v(44.28, 28.78) * mm});
            skLineSegment(sketch, "E1180", {"start": v(44.28, 28.78) * mm, "end": v(44.37, 28.84) * mm});
            skLineSegment(sketch, "E1181", {"start": v(44.37, 28.84) * mm, "end": v(44.43, 28.88) * mm});
            skLineSegment(sketch, "E1182", {"start": v(44.43, 28.88) * mm, "end": v(44.52, 28.94) * mm});
            skLineSegment(sketch, "E1183", {"start": v(44.52, 28.94) * mm, "end": v(44.57, 28.97) * mm});
            skLineSegment(sketch, "E1184", {"start": v(44.57, 28.97) * mm, "end": v(44.66, 29.03) * mm});
            skLineSegment(sketch, "E1185", {"start": v(44.66, 29.03) * mm, "end": v(44.71, 29.07) * mm});
            skLineSegment(sketch, "E1186", {"start": v(44.71, 29.07) * mm, "end": v(44.8, 29.13) * mm});
            skLineSegment(sketch, "E1187", {"start": v(44.8, 29.13) * mm, "end": v(44.85, 29.17) * mm});
            skLineSegment(sketch, "E1188", {"start": v(44.85, 29.17) * mm, "end": v(44.94, 29.24) * mm});
            skLineSegment(sketch, "E1189", {"start": v(44.94, 29.24) * mm, "end": v(44.99, 29.28) * mm});
            skLineSegment(sketch, "E1190", {"start": v(44.99, 29.28) * mm, "end": v(45.07, 29.35) * mm});
            skLineSegment(sketch, "E1191", {"start": v(45.07, 29.35) * mm, "end": v(45.12, 29.39) * mm});
            skLineSegment(sketch, "E1192", {"start": v(45.12, 29.39) * mm, "end": v(45.2, 29.46) * mm});
            skLineSegment(sketch, "E1193", {"start": v(45.2, 29.46) * mm, "end": v(45.25, 29.5) * mm});
            skLineSegment(sketch, "E1194", {"start": v(45.25, 29.5) * mm, "end": v(45.33, 29.57) * mm});
            skLineSegment(sketch, "E1195", {"start": v(45.33, 29.57) * mm, "end": v(45.38, 29.62) * mm});
            skLineSegment(sketch, "E1196", {"start": v(45.38, 29.62) * mm, "end": v(45.46, 29.69) * mm});
            skLineSegment(sketch, "E1197", {"start": v(45.46, 29.69) * mm, "end": v(45.5, 29.73) * mm});
            skLineSegment(sketch, "E1198", {"start": v(45.5, 29.73) * mm, "end": v(45.58, 29.8) * mm});
            skLineSegment(sketch, "E1199", {"start": v(45.58, 29.8) * mm, "end": v(45.63, 29.86) * mm});
            skLineSegment(sketch, "E1200", {"start": v(45.63, 29.86) * mm, "end": v(45.7, 29.93) * mm});
            skLineSegment(sketch, "E1201", {"start": v(45.7, 29.93) * mm, "end": v(45.75, 29.98) * mm});
            skLineSegment(sketch, "E1202", {"start": v(45.75, 29.98) * mm, "end": v(45.82, 30.06) * mm});
            skLineSegment(sketch, "E1203", {"start": v(45.82, 30.06) * mm, "end": v(45.86, 30.1) * mm});
            skLineSegment(sketch, "E1204", {"start": v(45.86, 30.1) * mm, "end": v(45.93, 30.18) * mm});
            skLineSegment(sketch, "E1205", {"start": v(45.93, 30.18) * mm, "end": v(45.98, 30.24) * mm});
            skLineSegment(sketch, "E1206", {"start": v(45.98, 30.24) * mm, "end": v(46.04, 30.32) * mm});
            skLineSegment(sketch, "E1207", {"start": v(46.04, 30.32) * mm, "end": v(46.09, 30.37) * mm});
            skLineSegment(sketch, "E1208", {"start": v(46.09, 30.37) * mm, "end": v(46.15, 30.45) * mm});
            skLineSegment(sketch, "E1209", {"start": v(46.15, 30.45) * mm, "end": v(46.2, 30.5) * mm});
            skLineSegment(sketch, "E1210", {"start": v(46.2, 30.5) * mm, "end": v(46.25, 30.59) * mm});
            skLineSegment(sketch, "E1211", {"start": v(46.25, 30.59) * mm, "end": v(46.3, 30.65) * mm});
            skLineSegment(sketch, "E1212", {"start": v(46.3, 30.65) * mm, "end": v(46.35, 30.73) * mm});
            skLineSegment(sketch, "E1213", {"start": v(46.35, 30.73) * mm, "end": v(46.4, 30.79) * mm});
            skLineSegment(sketch, "E1214", {"start": v(46.4, 30.79) * mm, "end": v(46.45, 30.87) * mm});
            skLineSegment(sketch, "E1215", {"start": v(46.45, 30.87) * mm, "end": v(46.5, 30.93) * mm});
            skLineSegment(sketch, "E1216", {"start": v(46.5, 30.93) * mm, "end": v(46.54, 31.01) * mm});
            skLineSegment(sketch, "E1217", {"start": v(46.54, 31.01) * mm, "end": v(46.58, 31.08) * mm});
            skLineSegment(sketch, "E1218", {"start": v(46.58, 31.08) * mm, "end": v(46.63, 31.16) * mm});
            skLineSegment(sketch, "E1219", {"start": v(46.63, 31.16) * mm, "end": v(46.67, 31.22) * mm});
            skLineSegment(sketch, "E1220", {"start": v(46.67, 31.22) * mm, "end": v(46.72, 31.3) * mm});
            skLineSegment(sketch, "E1221", {"start": v(46.72, 31.3) * mm, "end": v(46.76, 31.37) * mm});
            skLineSegment(sketch, "E1222", {"start": v(46.76, 31.37) * mm, "end": v(46.8, 31.46) * mm});
            skLineSegment(sketch, "E1223", {"start": v(46.8, 31.46) * mm, "end": v(46.84, 31.53) * mm});
            skLineSegment(sketch, "E1224", {"start": v(46.84, 31.53) * mm, "end": v(46.88, 31.6) * mm});
            skLineSegment(sketch, "E1225", {"start": v(46.88, 31.6) * mm, "end": v(46.92, 31.68) * mm});
            skLineSegment(sketch, "E1226", {"start": v(46.92, 31.68) * mm, "end": v(46.96, 31.76) * mm});
            skLineSegment(sketch, "E1227", {"start": v(46.96, 31.76) * mm, "end": v(47, 31.84) * mm});
            skLineSegment(sketch, "E1228", {"start": v(47, 31.84) * mm, "end": v(47.03, 31.92) * mm});
            skLineSegment(sketch, "E1229", {"start": v(47.03, 31.92) * mm, "end": v(47.06, 32) * mm});
            skLineSegment(sketch, "E1230", {"start": v(47.06, 32) * mm, "end": v(47.1, 32.08) * mm});
            skLineSegment(sketch, "E1231", {"start": v(47.1, 32.08) * mm, "end": v(47.13, 32.15) * mm});
            skLineSegment(sketch, "E1232", {"start": v(47.13, 32.15) * mm, "end": v(47.16, 32.24) * mm});
            skLineSegment(sketch, "E1233", {"start": v(47.16, 32.24) * mm, "end": v(47.19, 32.31) * mm});
            skLineSegment(sketch, "E1234", {"start": v(47.19, 32.31) * mm, "end": v(47.22, 32.4) * mm});
            skLineSegment(sketch, "E1235", {"start": v(47.22, 32.4) * mm, "end": v(47.25, 32.48) * mm});
            skLineSegment(sketch, "E1236", {"start": v(47.25, 32.48) * mm, "end": v(47.28, 32.56) * mm});
            skLineSegment(sketch, "E1237", {"start": v(47.28, 32.56) * mm, "end": v(47.3, 32.64) * mm});
            skLineSegment(sketch, "E1238", {"start": v(47.3, 32.64) * mm, "end": v(47.33, 32.72) * mm});
            skLineSegment(sketch, "E1239", {"start": v(47.33, 32.72) * mm, "end": v(47.35, 32.8) * mm});
            skLineSegment(sketch, "E1240", {"start": v(47.35, 32.8) * mm, "end": v(47.38, 32.89) * mm});
            skLineSegment(sketch, "E1241", {"start": v(47.38, 32.89) * mm, "end": v(47.4, 32.97) * mm});
            skLineSegment(sketch, "E1242", {"start": v(47.4, 32.97) * mm, "end": v(47.42, 33.06) * mm});
            skLineSegment(sketch, "E1243", {"start": v(47.42, 33.06) * mm, "end": v(47.42, 33.07) * mm});
            skLineSegment(sketch, "E1244", {"start": v(47.42, 33.07) * mm, "end": v(47.43, 33.09) * mm});
            skLineSegment(sketch, "E1245", {"start": v(47.43, 33.09) * mm, "end": v(47.89, 33) * mm});
            skLineSegment(sketch, "E1246", {"start": v(47.89, 33) * mm, "end": v(48.3, 32.9) * mm});
            skLineSegment(sketch, "E1247", {"start": v(48.3, 32.9) * mm, "end": v(48.34, 32.9) * mm});
            skLineSegment(sketch, "E1248", {"start": v(48.34, 32.9) * mm, "end": v(48.57, 32.84) * mm});
            skLineSegment(sketch, "E1249", {"start": v(48.57, 32.84) * mm, "end": v(48.81, 32.78) * mm});
            skLineSegment(sketch, "E1250", {"start": v(48.81, 32.78) * mm, "end": v(49.13, 32.7) * mm});
            skLineSegment(sketch, "E1251", {"start": v(49.13, 32.7) * mm, "end": v(49.16, 32.7) * mm});
            skLineSegment(sketch, "E1252", {"start": v(49.16, 32.7) * mm, "end": v(49.46, 32.62) * mm});
            skLineSegment(sketch, "E1253", {"start": v(49.46, 32.62) * mm, "end": v(49.66, 32.57) * mm});
            skLineSegment(sketch, "E1254", {"start": v(49.66, 32.57) * mm, "end": v(49.96, 32.49) * mm});
            skLineSegment(sketch, "E1255", {"start": v(49.96, 32.49) * mm, "end": v(50.07, 32.46) * mm});
            skLineSegment(sketch, "E1256", {"start": v(50.07, 32.46) * mm, "end": v(50.38, 32.37) * mm});
            skLineSegment(sketch, "E1257", {"start": v(50.38, 32.37) * mm, "end": v(50.68, 32.28) * mm});
            skLineSegment(sketch, "E1258", {"start": v(50.68, 32.28) * mm, "end": v(50.99, 32.18) * mm});
            skLineSegment(sketch, "E1259", {"start": v(50.99, 32.18) * mm, "end": v(51.3, 32.08) * mm});
            skLineSegment(sketch, "E1260", {"start": v(51.3, 32.08) * mm, "end": v(51.4, 32.05) * mm});
            skLineSegment(sketch, "E1261", {"start": v(51.4, 32.05) * mm, "end": v(51.6, 31.98) * mm});
            skLineSegment(sketch, "E1262", {"start": v(51.6, 31.98) * mm, "end": v(51.9, 31.87) * mm});
            skLineSegment(sketch, "E1263", {"start": v(51.9, 31.87) * mm, "end": v(52.19, 31.78) * mm});
            skLineSegment(sketch, "E1264", {"start": v(52.19, 31.78) * mm, "end": v(52.25, 31.76) * mm});
            skLineSegment(sketch, "E1265", {"start": v(52.25, 31.76) * mm, "end": v(52.44, 31.7) * mm});
            skLineSegment(sketch, "E1266", {"start": v(52.44, 31.7) * mm, "end": v(52.64, 31.62) * mm});
            skLineSegment(sketch, "E1267", {"start": v(52.64, 31.62) * mm, "end": v(53.23, 31.41) * mm});
            skLineSegment(sketch, "E1268", {"start": v(53.23, 31.41) * mm, "end": v(53.67, 31.23) * mm});
            skLineSegment(sketch, "E1269", {"start": v(53.67, 31.23) * mm, "end": v(54.02, 31.1) * mm});
            skLineSegment(sketch, "E1270", {"start": v(54.02, 31.1) * mm, "end": v(54.46, 30.9) * mm});
            skLineSegment(sketch, "E1271", {"start": v(54.46, 30.9) * mm, "end": v(54.81, 30.75) * mm});
            skLineSegment(sketch, "E1272", {"start": v(54.81, 30.75) * mm, "end": v(55.25, 30.55) * mm});
            skLineSegment(sketch, "E1273", {"start": v(55.25, 30.55) * mm, "end": v(55.6, 30.4) * mm});
            skLineSegment(sketch, "E1274", {"start": v(55.6, 30.4) * mm, "end": v(56.02, 30.19) * mm});
            skLineSegment(sketch, "E1275", {"start": v(56.02, 30.19) * mm, "end": v(56.37, 30.02) * mm});
            skLineSegment(sketch, "E1276", {"start": v(56.37, 30.02) * mm, "end": v(56.8, 29.8) * mm});
            skLineSegment(sketch, "E1277", {"start": v(56.8, 29.8) * mm, "end": v(57.13, 29.62) * mm});
            skLineSegment(sketch, "E1278", {"start": v(57.13, 29.62) * mm, "end": v(57.55, 29.4) * mm});
            skLineSegment(sketch, "E1279", {"start": v(57.55, 29.4) * mm, "end": v(57.88, 29.2) * mm});
            skLineSegment(sketch, "E1280", {"start": v(57.88, 29.2) * mm, "end": v(58.3, 28.97) * mm});
            skLineSegment(sketch, "E1281", {"start": v(58.3, 28.97) * mm, "end": v(58.62, 28.78) * mm});
            skLineSegment(sketch, "E1282", {"start": v(58.62, 28.78) * mm, "end": v(59.03, 28.52) * mm});
            skLineSegment(sketch, "E1283", {"start": v(59.03, 28.52) * mm, "end": v(59.35, 28.33) * mm});
            skLineSegment(sketch, "E1284", {"start": v(59.35, 28.33) * mm, "end": v(59.76, 28.06) * mm});
            skLineSegment(sketch, "E1285", {"start": v(59.76, 28.06) * mm, "end": v(60.07, 27.86) * mm});
            skLineSegment(sketch, "E1286", {"start": v(60.07, 27.86) * mm, "end": v(60.27, 27.72) * mm});
            skLineSegment(sketch, "E1287", {"start": v(60.27, 27.72) * mm, "end": v(60.51, 27.56) * mm});
            skLineSegment(sketch, "E1288", {"start": v(60.51, 27.56) * mm, "end": v(60.78, 27.37) * mm});
            skLineSegment(sketch, "E1289", {"start": v(60.78, 27.37) * mm, "end": v(61.02, 27.2) * mm});
            skLineSegment(sketch, "E1290", {"start": v(61.02, 27.2) * mm, "end": v(61.83, 26.6) * mm});
            skLineSegment(sketch, "E1291", {"start": v(61.83, 26.6) * mm, "end": v(62.06, 26.42) * mm});
            skLineSegment(sketch, "E1292", {"start": v(62.06, 26.42) * mm, "end": v(62.29, 26.24) * mm});
            skLineSegment(sketch, "E1293", {"start": v(62.29, 26.24) * mm, "end": v(62.83, 25.81) * mm});
            skLineSegment(sketch, "E1294", {"start": v(62.83, 25.81) * mm, "end": v(63.2, 25.5) * mm});
            skLineSegment(sketch, "E1295", {"start": v(63.2, 25.5) * mm, "end": v(63.5, 25.26) * mm});
            skLineSegment(sketch, "E1296", {"start": v(63.5, 25.26) * mm, "end": v(63.85, 24.94) * mm});
            skLineSegment(sketch, "E1297", {"start": v(63.85, 24.94) * mm, "end": v(64.13, 24.69) * mm});
            skLineSegment(sketch, "E1298", {"start": v(64.13, 24.69) * mm, "end": v(64.48, 24.36) * mm});
            skLineSegment(sketch, "E1299", {"start": v(64.48, 24.36) * mm, "end": v(64.76, 24.1) * mm});
            skLineSegment(sketch, "E1300", {"start": v(64.76, 24.1) * mm, "end": v(65.1, 23.77) * mm});
            skLineSegment(sketch, "E1301", {"start": v(65.1, 23.77) * mm, "end": v(65.38, 23.5) * mm});
            skLineSegment(sketch, "E1302", {"start": v(65.38, 23.5) * mm, "end": v(65.71, 23.16) * mm});
            skLineSegment(sketch, "E1303", {"start": v(65.71, 23.16) * mm, "end": v(65.98, 22.89) * mm});
            skLineSegment(sketch, "E1304", {"start": v(65.98, 22.89) * mm, "end": v(66.3, 22.54) * mm});
            skLineSegment(sketch, "E1305", {"start": v(66.3, 22.54) * mm, "end": v(66.56, 22.26) * mm});
            skLineSegment(sketch, "E1306", {"start": v(66.56, 22.26) * mm, "end": v(66.88, 21.9) * mm});
            skLineSegment(sketch, "E1307", {"start": v(66.88, 21.9) * mm, "end": v(67.13, 21.62) * mm});
            skLineSegment(sketch, "E1308", {"start": v(67.13, 21.62) * mm, "end": v(67.44, 21.25) * mm});
            skLineSegment(sketch, "E1309", {"start": v(67.44, 21.25) * mm, "end": v(67.68, 20.96) * mm});
            skLineSegment(sketch, "E1310", {"start": v(67.68, 20.96) * mm, "end": v(67.98, 20.59) * mm});
            skLineSegment(sketch, "E1311", {"start": v(67.98, 20.59) * mm, "end": v(68.22, 20.29) * mm});
            skLineSegment(sketch, "E1312", {"start": v(68.22, 20.29) * mm, "end": v(68.51, 19.9) * mm});
            skLineSegment(sketch, "E1313", {"start": v(68.51, 19.9) * mm, "end": v(68.74, 19.6) * mm});
            skLineSegment(sketch, "E1314", {"start": v(68.74, 19.6) * mm, "end": v(69.02, 19.22) * mm});
            skLineSegment(sketch, "E1315", {"start": v(69.02, 19.22) * mm, "end": v(69.24, 18.9) * mm});
            skLineSegment(sketch, "E1316", {"start": v(69.24, 18.9) * mm, "end": v(69.52, 18.51) * mm});
            skLineSegment(sketch, "E1317", {"start": v(69.52, 18.51) * mm, "end": v(69.73, 18.2) * mm});
            skLineSegment(sketch, "E1318", {"start": v(69.73, 18.2) * mm, "end": v(70, 17.8) * mm});
            skLineSegment(sketch, "E1319", {"start": v(70, 17.8) * mm, "end": v(70.2, 17.48) * mm});
            skLineSegment(sketch, "E1320", {"start": v(70.2, 17.48) * mm, "end": v(70.7, 16.65) * mm});
            skLineSegment(sketch, "E1321", {"start": v(70.7, 16.65) * mm, "end": v(70.92, 16.29) * mm});
            skLineSegment(sketch, "E1322", {"start": v(70.92, 16.29) * mm, "end": v(70.9, 16.27) * mm});
            skLineSegment(sketch, "E1323", {"start": v(70.9, 16.27) * mm, "end": v(71.12, 15.9) * mm});
            skLineSegment(sketch, "E1324", {"start": v(71.12, 15.9) * mm, "end": v(71.04, 15.86) * mm});
            skLineSegment(sketch, "E1325", {"start": v(71.04, 15.86) * mm, "end": v(71.1, 15.77) * mm});
            skLineSegment(sketch, "E1326", {"start": v(71.1, 15.77) * mm, "end": v(71.02, 15.72) * mm});
            skLineSegment(sketch, "E1327", {"start": v(71.02, 15.72) * mm, "end": v(70.94, 15.67) * mm});
            skLineSegment(sketch, "E1328", {"start": v(70.94, 15.67) * mm, "end": v(70.87, 15.62) * mm});
            skLineSegment(sketch, "E1329", {"start": v(70.87, 15.62) * mm, "end": v(70.8, 15.56) * mm});
            skLineSegment(sketch, "E1330", {"start": v(70.8, 15.56) * mm, "end": v(70.72, 15.5) * mm});
            skLineSegment(sketch, "E1331", {"start": v(70.72, 15.5) * mm, "end": v(70.65, 15.43) * mm});
            skLineSegment(sketch, "E1332", {"start": v(70.65, 15.43) * mm, "end": v(70.58, 15.37) * mm});
            skLineSegment(sketch, "E1333", {"start": v(70.58, 15.37) * mm, "end": v(70.5, 15.3) * mm});
            skLineSegment(sketch, "E1334", {"start": v(70.5, 15.3) * mm, "end": v(70.44, 15.23) * mm});
            skLineSegment(sketch, "E1335", {"start": v(70.44, 15.23) * mm, "end": v(70.36, 15.15) * mm});
            skLineSegment(sketch, "E1336", {"start": v(70.36, 15.15) * mm, "end": v(70.3, 15.08) * mm});
            skLineSegment(sketch, "E1337", {"start": v(70.3, 15.08) * mm, "end": v(70.22, 15) * mm});
            skLineSegment(sketch, "E1338", {"start": v(70.22, 15) * mm, "end": v(70.16, 14.92) * mm});
            skLineSegment(sketch, "E1339", {"start": v(70.16, 14.92) * mm, "end": v(70.08, 14.87) * mm});
            skLineSegment(sketch, "E1340", {"start": v(70.08, 14.87) * mm, "end": v(70.01, 14.78) * mm});
            skLineSegment(sketch, "E1341", {"start": v(70.01, 14.78) * mm, "end": v(69.95, 14.74) * mm});
            skLineSegment(sketch, "E1342", {"start": v(69.95, 14.74) * mm, "end": v(69.89, 14.65) * mm});
            skLineSegment(sketch, "E1343", {"start": v(69.89, 14.65) * mm, "end": v(69.83, 14.61) * mm});
            skLineSegment(sketch, "E1344", {"start": v(69.83, 14.61) * mm, "end": v(69.76, 14.52) * mm});
            skLineSegment(sketch, "E1345", {"start": v(69.76, 14.52) * mm, "end": v(69.7, 14.48) * mm});
            skLineSegment(sketch, "E1346", {"start": v(69.7, 14.48) * mm, "end": v(69.65, 14.43) * mm});
            skLineSegment(sketch, "E1347", {"start": v(69.65, 14.43) * mm, "end": v(69.59, 14.34) * mm});
            skLineSegment(sketch, "E1348", {"start": v(69.59, 14.34) * mm, "end": v(69.53, 14.3) * mm});
            skLineSegment(sketch, "E1349", {"start": v(69.53, 14.3) * mm, "end": v(69.47, 14.2) * mm});
            skLineSegment(sketch, "E1350", {"start": v(69.47, 14.2) * mm, "end": v(69.42, 14.16) * mm});
            skLineSegment(sketch, "E1351", {"start": v(69.42, 14.16) * mm, "end": v(69.36, 14.06) * mm});
            skLineSegment(sketch, "E1352", {"start": v(69.36, 14.06) * mm, "end": v(69.31, 14.02) * mm});
            skLineSegment(sketch, "E1353", {"start": v(69.31, 14.02) * mm, "end": v(69.26, 13.97) * mm});
            skLineSegment(sketch, "E1354", {"start": v(69.26, 13.97) * mm, "end": v(69.2, 13.87) * mm});
            skLineSegment(sketch, "E1355", {"start": v(69.2, 13.87) * mm, "end": v(69.16, 13.82) * mm});
            skLineSegment(sketch, "E1356", {"start": v(69.16, 13.82) * mm, "end": v(69.1, 13.72) * mm});
            skLineSegment(sketch, "E1357", {"start": v(69.1, 13.72) * mm, "end": v(69.06, 13.67) * mm});
            skLineSegment(sketch, "E1358", {"start": v(69.06, 13.67) * mm, "end": v(69, 13.57) * mm});
            skLineSegment(sketch, "E1359", {"start": v(69, 13.57) * mm, "end": v(68.96, 13.52) * mm});
            skLineSegment(sketch, "E1360", {"start": v(68.96, 13.52) * mm, "end": v(68.92, 13.47) * mm});
            skLineSegment(sketch, "E1361", {"start": v(68.92, 13.47) * mm, "end": v(68.87, 13.37) * mm});
            skLineSegment(sketch, "E1362", {"start": v(68.87, 13.37) * mm, "end": v(68.83, 13.32) * mm});
            skLineSegment(sketch, "E1363", {"start": v(68.83, 13.32) * mm, "end": v(68.78, 13.22) * mm});
            skLineSegment(sketch, "E1364", {"start": v(68.78, 13.22) * mm, "end": v(68.74, 13.16) * mm});
            skLineSegment(sketch, "E1365", {"start": v(68.74, 13.16) * mm, "end": v(68.7, 13.1) * mm});
            skLineSegment(sketch, "E1366", {"start": v(68.7, 13.1) * mm, "end": v(68.66, 13) * mm});
            skLineSegment(sketch, "E1367", {"start": v(68.66, 13) * mm, "end": v(68.62, 12.95) * mm});
            skLineSegment(sketch, "E1368", {"start": v(68.62, 12.95) * mm, "end": v(68.58, 12.85) * mm});
            skLineSegment(sketch, "E1369", {"start": v(68.58, 12.85) * mm, "end": v(68.55, 12.8) * mm});
            skLineSegment(sketch, "E1370", {"start": v(68.55, 12.8) * mm, "end": v(68.5, 12.68) * mm});
            skLineSegment(sketch, "E1371", {"start": v(68.5, 12.68) * mm, "end": v(68.47, 12.63) * mm});
            skLineSegment(sketch, "E1372", {"start": v(68.47, 12.63) * mm, "end": v(68.44, 12.57) * mm});
            skLineSegment(sketch, "E1373", {"start": v(68.44, 12.57) * mm, "end": v(68.4, 12.47) * mm});
            skLineSegment(sketch, "E1374", {"start": v(68.4, 12.47) * mm, "end": v(68.37, 12.41) * mm});
            skLineSegment(sketch, "E1375", {"start": v(68.37, 12.41) * mm, "end": v(68.34, 12.3) * mm});
            skLineSegment(sketch, "E1376", {"start": v(68.34, 12.3) * mm, "end": v(68.31, 12.25) * mm});
            skLineSegment(sketch, "E1377", {"start": v(68.31, 12.25) * mm, "end": v(68.28, 12.13) * mm});
            skLineSegment(sketch, "E1378", {"start": v(68.28, 12.13) * mm, "end": v(68.25, 12.08) * mm});
            skLineSegment(sketch, "E1379", {"start": v(68.25, 12.08) * mm, "end": v(68.23, 12.02) * mm});
            skLineSegment(sketch, "E1380", {"start": v(68.23, 12.02) * mm, "end": v(68.2, 11.91) * mm});
            skLineSegment(sketch, "E1381", {"start": v(68.2, 11.91) * mm, "end": v(68.18, 11.86) * mm});
            skLineSegment(sketch, "E1382", {"start": v(68.18, 11.86) * mm, "end": v(68.15, 11.74) * mm});
            skLineSegment(sketch, "E1383", {"start": v(68.15, 11.74) * mm, "end": v(68.13, 11.69) * mm});
            skLineSegment(sketch, "E1384", {"start": v(68.13, 11.69) * mm, "end": v(68.1, 11.57) * mm});
            skLineSegment(sketch, "E1385", {"start": v(68.1, 11.57) * mm, "end": v(68.08, 11.52) * mm});
            skLineSegment(sketch, "E1386", {"start": v(68.08, 11.52) * mm, "end": v(68.07, 11.46) * mm});
            skLineSegment(sketch, "E1387", {"start": v(68.07, 11.46) * mm, "end": v(68.05, 11.35) * mm});
            skLineSegment(sketch, "E1388", {"start": v(68.05, 11.35) * mm, "end": v(68.03, 11.29) * mm});
            skLineSegment(sketch, "E1389", {"start": v(68.03, 11.29) * mm, "end": v(68.01, 11.17) * mm});
            skLineSegment(sketch, "E1390", {"start": v(68.01, 11.17) * mm, "end": v(68, 11.12) * mm});
            skLineSegment(sketch, "E1391", {"start": v(68, 11.12) * mm, "end": v(67.98, 11) * mm});
            skLineSegment(sketch, "E1392", {"start": v(67.98, 11) * mm, "end": v(67.97, 10.95) * mm});
            skLineSegment(sketch, "E1393", {"start": v(67.97, 10.95) * mm, "end": v(67.95, 10.89) * mm});
            skLineSegment(sketch, "E1394", {"start": v(67.95, 10.89) * mm, "end": v(67.94, 10.77) * mm});
            skLineSegment(sketch, "E1395", {"start": v(67.94, 10.77) * mm, "end": v(67.93, 10.72) * mm});
            skLineSegment(sketch, "E1396", {"start": v(67.93, 10.72) * mm, "end": v(67.92, 10.6) * mm});
            skLineSegment(sketch, "E1397", {"start": v(67.92, 10.6) * mm, "end": v(67.91, 10.54) * mm});
            skLineSegment(sketch, "E1398", {"start": v(67.91, 10.54) * mm, "end": v(67.9, 10.43) * mm});
            skLineSegment(sketch, "E1399", {"start": v(67.9, 10.43) * mm, "end": v(67.9, 10.37) * mm});
            skLineSegment(sketch, "E1400", {"start": v(67.9, 10.37) * mm, "end": v(67.89, 10.31) * mm});
            skLineSegment(sketch, "E1401", {"start": v(67.89, 10.31) * mm, "end": v(67.89, 10.2) * mm});
            skLineSegment(sketch, "E1402", {"start": v(67.89, 10.2) * mm, "end": v(67.88, 10.14) * mm});
            skLineSegment(sketch, "E1403", {"start": v(67.88, 10.14) * mm, "end": v(67.88, 10.02) * mm});
            skLineSegment(sketch, "E1404", {"start": v(67.88, 10.02) * mm, "end": v(67.87, 9.97) * mm});
            skLineSegment(sketch, "E1405", {"start": v(67.87, 9.97) * mm, "end": v(67.89, 9.47) * mm});
            skLineSegment(sketch, "E1406", {"start": v(67.89, 9.47) * mm, "end": v(67.89, 9.38) * mm});
            skLineSegment(sketch, "E1407", {"start": v(67.89, 9.38) * mm, "end": v(67.9, 9.3) * mm});
            skLineSegment(sketch, "E1408", {"start": v(67.9, 9.3) * mm, "end": v(67.9, 9.21) * mm});
            skLineSegment(sketch, "E1409", {"start": v(67.9, 9.21) * mm, "end": v(67.9, 9.13) * mm});
            skLineSegment(sketch, "E1410", {"start": v(67.9, 9.13) * mm, "end": v(67.92, 9.04) * mm});
            skLineSegment(sketch, "E1411", {"start": v(67.92, 9.04) * mm, "end": v(67.93, 8.97) * mm});
            skLineSegment(sketch, "E1412", {"start": v(67.93, 8.97) * mm, "end": v(67.94, 8.88) * mm});
            skLineSegment(sketch, "E1413", {"start": v(67.94, 8.88) * mm, "end": v(67.95, 8.8) * mm});
            skLineSegment(sketch, "E1414", {"start": v(67.95, 8.8) * mm, "end": v(67.97, 8.71) * mm});
            skLineSegment(sketch, "E1415", {"start": v(67.97, 8.71) * mm, "end": v(67.98, 8.63) * mm});
            skLineSegment(sketch, "E1416", {"start": v(67.98, 8.63) * mm, "end": v(68, 8.55) * mm});
            skLineSegment(sketch, "E1417", {"start": v(68, 8.55) * mm, "end": v(68.01, 8.46) * mm});
            skLineSegment(sketch, "E1418", {"start": v(68.01, 8.46) * mm, "end": v(68.03, 8.38) * mm});
            skLineSegment(sketch, "E1419", {"start": v(68.03, 8.38) * mm, "end": v(68.05, 8.3) * mm});
            skLineSegment(sketch, "E1420", {"start": v(68.05, 8.3) * mm, "end": v(68.07, 8.21) * mm});
            skLineSegment(sketch, "E1421", {"start": v(68.07, 8.21) * mm, "end": v(68.1, 8.13) * mm});
            skLineSegment(sketch, "E1422", {"start": v(68.1, 8.13) * mm, "end": v(68.11, 8.05) * mm});
            skLineSegment(sketch, "E1423", {"start": v(68.11, 8.05) * mm, "end": v(68.14, 7.96) * mm});
            skLineSegment(sketch, "E1424", {"start": v(68.14, 7.96) * mm, "end": v(68.16, 7.88) * mm});
            skLineSegment(sketch, "E1425", {"start": v(68.16, 7.88) * mm, "end": v(68.18, 7.8) * mm});
            skLineSegment(sketch, "E1426", {"start": v(68.18, 7.8) * mm, "end": v(68.2, 7.72) * mm});
            skLineSegment(sketch, "E1427", {"start": v(68.2, 7.72) * mm, "end": v(68.24, 7.64) * mm});
            skLineSegment(sketch, "E1428", {"start": v(68.24, 7.64) * mm, "end": v(68.26, 7.55) * mm});
            skLineSegment(sketch, "E1429", {"start": v(68.26, 7.55) * mm, "end": v(68.3, 7.48) * mm});
            skLineSegment(sketch, "E1430", {"start": v(68.3, 7.48) * mm, "end": v(68.32, 7.4) * mm});
            skLineSegment(sketch, "E1431", {"start": v(68.32, 7.4) * mm, "end": v(68.35, 7.31) * mm});
            skLineSegment(sketch, "E1432", {"start": v(68.35, 7.31) * mm, "end": v(68.39, 7.23) * mm});
            skLineSegment(sketch, "E1433", {"start": v(68.39, 7.23) * mm, "end": v(68.42, 7.16) * mm});
            skLineSegment(sketch, "E1434", {"start": v(68.42, 7.16) * mm, "end": v(68.45, 7.07) * mm});
            skLineSegment(sketch, "E1435", {"start": v(68.45, 7.07) * mm, "end": v(68.49, 7) * mm});
            skLineSegment(sketch, "E1436", {"start": v(68.49, 7) * mm, "end": v(68.52, 6.92) * mm});
            skLineSegment(sketch, "E1437", {"start": v(68.52, 6.92) * mm, "end": v(68.56, 6.84) * mm});
            skLineSegment(sketch, "E1438", {"start": v(68.56, 6.84) * mm, "end": v(68.6, 6.76) * mm});
            skLineSegment(sketch, "E1439", {"start": v(68.6, 6.76) * mm, "end": v(68.64, 6.69) * mm});
            skLineSegment(sketch, "E1440", {"start": v(68.64, 6.69) * mm, "end": v(68.68, 6.61) * mm});
            skLineSegment(sketch, "E1441", {"start": v(68.68, 6.61) * mm, "end": v(68.72, 6.54) * mm});
            skLineSegment(sketch, "E1442", {"start": v(68.72, 6.54) * mm, "end": v(68.75, 6.48) * mm});
            skLineSegment(sketch, "E1443", {"start": v(68.75, 6.48) * mm, "end": v(68.8, 6.4) * mm});
            skLineSegment(sketch, "E1444", {"start": v(68.8, 6.4) * mm, "end": v(68.84, 6.33) * mm});
            skLineSegment(sketch, "E1445", {"start": v(68.84, 6.33) * mm, "end": v(68.88, 6.25) * mm});
            skLineSegment(sketch, "E1446", {"start": v(68.88, 6.25) * mm, "end": v(68.93, 6.16) * mm});
            skLineSegment(sketch, "E1447", {"start": v(68.93, 6.16) * mm, "end": v(68.96, 6.12) * mm});
            skLineSegment(sketch, "E1448", {"start": v(68.96, 6.12) * mm, "end": v(69.03, 6.02) * mm});
            skLineSegment(sketch, "E1449", {"start": v(69.03, 6.02) * mm, "end": v(69.06, 5.97) * mm});
            skLineSegment(sketch, "E1450", {"start": v(69.06, 5.97) * mm, "end": v(69.12, 5.88) * mm});
            skLineSegment(sketch, "E1451", {"start": v(69.12, 5.88) * mm, "end": v(69.16, 5.83) * mm});
            skLineSegment(sketch, "E1452", {"start": v(69.16, 5.83) * mm, "end": v(69.22, 5.74) * mm});
            skLineSegment(sketch, "E1453", {"start": v(69.22, 5.74) * mm, "end": v(69.26, 5.7) * mm});
            skLineSegment(sketch, "E1454", {"start": v(69.26, 5.7) * mm, "end": v(69.33, 5.6) * mm});
            skLineSegment(sketch, "E1455", {"start": v(69.33, 5.6) * mm, "end": v(69.36, 5.56) * mm});
            skLineSegment(sketch, "E1456", {"start": v(69.36, 5.56) * mm, "end": v(69.43, 5.47) * mm});
            skLineSegment(sketch, "E1457", {"start": v(69.43, 5.47) * mm, "end": v(69.47, 5.42) * mm});
            skLineSegment(sketch, "E1458", {"start": v(69.47, 5.42) * mm, "end": v(69.54, 5.33) * mm});
            skLineSegment(sketch, "E1459", {"start": v(69.54, 5.33) * mm, "end": v(69.58, 5.3) * mm});
            skLineSegment(sketch, "E1460", {"start": v(69.58, 5.3) * mm, "end": v(69.66, 5.2) * mm});
            skLineSegment(sketch, "E1461", {"start": v(69.66, 5.2) * mm, "end": v(69.7, 5.16) * mm});
            skLineSegment(sketch, "E1462", {"start": v(69.7, 5.16) * mm, "end": v(69.77, 5.08) * mm});
            skLineSegment(sketch, "E1463", {"start": v(69.77, 5.08) * mm, "end": v(69.81, 5.04) * mm});
            skLineSegment(sketch, "E1464", {"start": v(69.81, 5.04) * mm, "end": v(69.9, 4.95) * mm});
            skLineSegment(sketch, "E1465", {"start": v(69.9, 4.95) * mm, "end": v(69.94, 4.91) * mm});
            skLineSegment(sketch, "E1466", {"start": v(69.94, 4.91) * mm, "end": v(70.02, 4.83) * mm});
            skLineSegment(sketch, "E1467", {"start": v(70.02, 4.83) * mm, "end": v(70.06, 4.8) * mm});
            skLineSegment(sketch, "E1468", {"start": v(70.06, 4.8) * mm, "end": v(70.14, 4.72) * mm});
            skLineSegment(sketch, "E1469", {"start": v(70.14, 4.72) * mm, "end": v(70.19, 4.68) * mm});
            skLineSegment(sketch, "E1470", {"start": v(70.19, 4.68) * mm, "end": v(70.27, 4.6) * mm});
            skLineSegment(sketch, "E1471", {"start": v(70.27, 4.6) * mm, "end": v(70.32, 4.56) * mm});
            skLineSegment(sketch, "E1472", {"start": v(70.32, 4.56) * mm, "end": v(70.4, 4.5) * mm});
            skLineSegment(sketch, "E1473", {"start": v(70.4, 4.5) * mm, "end": v(70.45, 4.45) * mm});
            skLineSegment(sketch, "E1474", {"start": v(70.45, 4.45) * mm, "end": v(70.53, 4.38) * mm});
            skLineSegment(sketch, "E1475", {"start": v(70.53, 4.38) * mm, "end": v(70.58, 4.34) * mm});
            skLineSegment(sketch, "E1476", {"start": v(70.58, 4.34) * mm, "end": v(70.67, 4.28) * mm});
            skLineSegment(sketch, "E1477", {"start": v(70.67, 4.28) * mm, "end": v(70.72, 4.24) * mm});
            skLineSegment(sketch, "E1478", {"start": v(70.72, 4.24) * mm, "end": v(70.8, 4.18) * mm});
            skLineSegment(sketch, "E1479", {"start": v(70.8, 4.18) * mm, "end": v(70.86, 4.14) * mm});
            skLineSegment(sketch, "E1480", {"start": v(70.86, 4.14) * mm, "end": v(70.95, 4.08) * mm});
            skLineSegment(sketch, "E1481", {"start": v(70.95, 4.08) * mm, "end": v(71, 4.04) * mm});
            skLineSegment(sketch, "E1482", {"start": v(71, 4.04) * mm, "end": v(71.1, 3.98) * mm});
            skLineSegment(sketch, "E1483", {"start": v(71.1, 3.98) * mm, "end": v(71.15, 3.95) * mm});
            skLineSegment(sketch, "E1484", {"start": v(71.15, 3.95) * mm, "end": v(71.24, 3.9) * mm});
            skLineSegment(sketch, "E1485", {"start": v(71.24, 3.9) * mm, "end": v(71.3, 3.86) * mm});
            skLineSegment(sketch, "E1486", {"start": v(71.3, 3.86) * mm, "end": v(71.39, 3.8) * mm});
            skLineSegment(sketch, "E1487", {"start": v(71.39, 3.8) * mm, "end": v(71.45, 3.77) * mm});
            skLineSegment(sketch, "E1488", {"start": v(71.45, 3.77) * mm, "end": v(71.54, 3.72) * mm});
            skLineSegment(sketch, "E1489", {"start": v(71.54, 3.72) * mm, "end": v(71.6, 3.7) * mm});
            skLineSegment(sketch, "E1490", {"start": v(71.6, 3.7) * mm, "end": v(71.69, 3.64) * mm});
            skLineSegment(sketch, "E1491", {"start": v(71.69, 3.64) * mm, "end": v(71.75, 3.61) * mm});
            skLineSegment(sketch, "E1492", {"start": v(71.75, 3.61) * mm, "end": v(71.84, 3.57) * mm});
            skLineSegment(sketch, "E1493", {"start": v(71.84, 3.57) * mm, "end": v(71.9, 3.54) * mm});
            skLineSegment(sketch, "E1494", {"start": v(71.9, 3.54) * mm, "end": v(72, 3.5) * mm});
            skLineSegment(sketch, "E1495", {"start": v(72, 3.5) * mm, "end": v(72.06, 3.47) * mm});
            skLineSegment(sketch, "E1496", {"start": v(72.06, 3.47) * mm, "end": v(72.16, 3.43) * mm});
            skLineSegment(sketch, "E1497", {"start": v(72.16, 3.43) * mm, "end": v(72.22, 3.4) * mm});
            skLineSegment(sketch, "E1498", {"start": v(72.22, 3.4) * mm, "end": v(72.32, 3.36) * mm});
            skLineSegment(sketch, "E1499", {"start": v(72.32, 3.36) * mm, "end": v(72.38, 3.34) * mm});
            skLineSegment(sketch, "E1500", {"start": v(72.38, 3.34) * mm, "end": v(72.48, 3.3) * mm});
            skLineSegment(sketch, "E1501", {"start": v(72.48, 3.3) * mm, "end": v(72.55, 3.28) * mm});
            skLineSegment(sketch, "E1502", {"start": v(72.55, 3.28) * mm, "end": v(72.64, 3.24) * mm});
            skLineSegment(sketch, "E1503", {"start": v(72.64, 3.24) * mm, "end": v(72.7, 3.22) * mm});
            skLineSegment(sketch, "E1504", {"start": v(72.7, 3.22) * mm, "end": v(72.8, 3.2) * mm});
            skLineSegment(sketch, "E1505", {"start": v(72.8, 3.2) * mm, "end": v(72.87, 3.17) * mm});
            skLineSegment(sketch, "E1506", {"start": v(72.87, 3.17) * mm, "end": v(72.97, 3.14) * mm});
            skLineSegment(sketch, "E1507", {"start": v(72.97, 3.14) * mm, "end": v(73.04, 3.12) * mm});
            skLineSegment(sketch, "E1508", {"start": v(73.04, 3.12) * mm, "end": v(73.13, 3.1) * mm});
            skLineSegment(sketch, "E1509", {"start": v(73.13, 3.1) * mm, "end": v(73.2, 3.08) * mm});
            skLineSegment(sketch, "E1510", {"start": v(73.2, 3.08) * mm, "end": v(73.3, 3.06) * mm});
            skLineSegment(sketch, "E1511", {"start": v(73.3, 3.06) * mm, "end": v(73.37, 3.04) * mm});
            skLineSegment(sketch, "E1512", {"start": v(73.37, 3.04) * mm, "end": v(73.47, 3.02) * mm});
            skLineSegment(sketch, "E1513", {"start": v(73.47, 3.02) * mm, "end": v(73.54, 3) * mm});
            skLineSegment(sketch, "E1514", {"start": v(73.54, 3) * mm, "end": v(73.64, 2.99) * mm});
            skLineSegment(sketch, "E1515", {"start": v(73.64, 2.99) * mm, "end": v(73.71, 2.98) * mm});
            skLineSegment(sketch, "E1516", {"start": v(73.71, 2.98) * mm, "end": v(73.8, 2.96) * mm});
            skLineSegment(sketch, "E1517", {"start": v(73.8, 2.96) * mm, "end": v(73.88, 2.95) * mm});
            skLineSegment(sketch, "E1518", {"start": v(73.88, 2.95) * mm, "end": v(73.98, 2.94) * mm});
            skLineSegment(sketch, "E1519", {"start": v(73.98, 2.94) * mm, "end": v(74.06, 2.93) * mm});
            skLineSegment(sketch, "E1520", {"start": v(74.06, 2.93) * mm, "end": v(74.15, 2.92) * mm});
            skLineSegment(sketch, "E1521", {"start": v(74.15, 2.92) * mm, "end": v(74.23, 2.91) * mm});
            skLineSegment(sketch, "E1522", {"start": v(74.23, 2.91) * mm, "end": v(74.32, 2.9) * mm});
            skLineSegment(sketch, "E1523", {"start": v(74.32, 2.9) * mm, "end": v(74.4, 2.9) * mm});
            skLineSegment(sketch, "E1524", {"start": v(74.4, 2.9) * mm, "end": v(74.49, 2.9) * mm});
            skLineSegment(sketch, "E1525", {"start": v(74.49, 2.9) * mm, "end": v(74.57, 2.89) * mm});
            skLineSegment(sketch, "E1526", {"start": v(74.57, 2.89) * mm, "end": v(74.66, 2.88) * mm});
            skLineSegment(sketch, "E1527", {"start": v(74.66, 2.88) * mm, "end": v(74.74, 2.88) * mm});
            skLineSegment(sketch, "E1528", {"start": v(74.74, 2.88) * mm, "end": v(74.83, 2.88) * mm});
            skLineSegment(sketch, "E1529", {"start": v(74.83, 2.88) * mm, "end": v(74.92, 2.88) * mm});
            skLineSegment(sketch, "E1530", {"start": v(74.92, 2.88) * mm, "end": v(75, 2.88) * mm});
            skLineSegment(sketch, "E1531", {"start": v(75, 2.88) * mm, "end": v(75.09, 2.88) * mm});
            skLineSegment(sketch, "E1532", {"start": v(75.09, 2.88) * mm, "end": v(75.18, 2.89) * mm});
            skLineSegment(sketch, "E1533", {"start": v(75.18, 2.89) * mm, "end": v(75.26, 2.9) * mm});
            skLineSegment(sketch, "E1534", {"start": v(75.26, 2.9) * mm, "end": v(75.35, 2.9) * mm});
            skLineSegment(sketch, "E1535", {"start": v(75.35, 2.9) * mm, "end": v(75.36, 2.9) * mm});
            skLineSegment(sketch, "E1536", {"start": v(75.36, 2.9) * mm, "end": v(75.38, 2.9) * mm});
            skLineSegment(sketch, "E1537", {"start": v(75.38, 2.9) * mm, "end": v(75.42, 2.53) * mm});
            skLineSegment(sketch, "E1538", {"start": v(75.42, 2.53) * mm, "end": v(75.46, 2.19) * mm});
            skLineSegment(sketch, "E1539", {"start": v(75.46, 2.19) * mm, "end": v(75.47, 2.04) * mm});
            skLineSegment(sketch, "E1540", {"start": v(75.47, 2.04) * mm, "end": v(75.5, 1.8) * mm});
            skLineSegment(sketch, "E1541", {"start": v(75.5, 1.8) * mm, "end": v(75.5, 1.66) * mm});
            skLineSegment(sketch, "E1542", {"start": v(75.5, 1.66) * mm, "end": v(75.53, 1.33) * mm});
            skLineSegment(sketch, "E1543", {"start": v(75.53, 1.33) * mm, "end": v(75.54, 1.2) * mm});
            skLineSegment(sketch, "E1544", {"start": v(75.54, 1.2) * mm, "end": v(75.56, 0.9) * mm});
            skLineSegment(sketch, "E1545", {"start": v(75.56, 0.9) * mm, "end": v(75.57, 0.8) * mm});
            skLineSegment(sketch, "E1546", {"start": v(75.57, 0.8) * mm, "end": v(75.59, 0.47) * mm});
            skLineSegment(sketch, "E1547", {"start": v(75.59, 0.47) * mm, "end": v(75.6, 0.25) * mm});
            skLineSegment(sketch, "E1548", {"start": v(75.6, 0.25) * mm, "end": v(75.6, -0.06) * mm});
            skLineSegment(sketch, "E1549", {"start": v(75.6, -0.06) * mm, "end": v(75.62, -0.39) * mm});
            skLineSegment(sketch, "E1550", {"start": v(75.62, -0.39) * mm, "end": v(75.62, -0.7) * mm});
            skLineSegment(sketch, "E1551", {"start": v(75.62, -0.7) * mm, "end": v(75.62, -1.02) * mm});
            skLineSegment(sketch, "E1552", {"start": v(75.62, -1.02) * mm, "end": v(75.62, -1.34) * mm});
            skLineSegment(sketch, "E1553", {"start": v(75.62, -1.34) * mm, "end": v(75.61, -1.67) * mm});
            skLineSegment(sketch, "E1554", {"start": v(75.61, -1.67) * mm, "end": v(75.61, -1.91) * mm});
            skLineSegment(sketch, "E1555", {"start": v(75.61, -1.91) * mm, "end": v(75.61, -1.97) * mm});
            skLineSegment(sketch, "E1556", {"start": v(75.61, -1.97) * mm, "end": v(75.6, -2.23) * mm});
            skLineSegment(sketch, "E1557", {"start": v(75.6, -2.23) * mm, "end": v(75.6, -2.44) * mm});
            skLineSegment(sketch, "E1558", {"start": v(75.6, -2.44) * mm, "end": v(75.6, -2.47) * mm});
            skLineSegment(sketch, "E1559", {"start": v(75.6, -2.47) * mm, "end": v(75.59, -2.96) * mm});
            skLineSegment(sketch, "E1560", {"start": v(75.59, -2.96) * mm, "end": v(75.56, -3.44) * mm});
            skLineSegment(sketch, "E1561", {"start": v(75.56, -3.44) * mm, "end": v(75.53, -3.82) * mm});
            skLineSegment(sketch, "E1562", {"start": v(75.53, -3.82) * mm, "end": v(75.5, -4.2) * mm});
            skLineSegment(sketch, "E1563", {"start": v(75.5, -4.2) * mm, "end": v(75.46, -4.67) * mm});
            skLineSegment(sketch, "E1564", {"start": v(75.46, -4.67) * mm, "end": v(75.42, -5.05) * mm});
            skLineSegment(sketch, "E1565", {"start": v(75.42, -5.05) * mm, "end": v(75.37, -5.53) * mm});
            skLineSegment(sketch, "E1566", {"start": v(75.37, -5.53) * mm, "end": v(75.31, -5.9) * mm});
            skLineSegment(sketch, "E1567", {"start": v(75.31, -5.9) * mm, "end": v(75.25, -6.38) * mm});
            skLineSegment(sketch, "E1568", {"start": v(75.25, -6.38) * mm, "end": v(75.19, -6.76) * mm});
            skLineSegment(sketch, "E1569", {"start": v(75.19, -6.76) * mm, "end": v(75.11, -7.23) * mm});
            skLineSegment(sketch, "E1570", {"start": v(75.11, -7.23) * mm, "end": v(75.04, -7.6) * mm});
            skLineSegment(sketch, "E1571", {"start": v(75.04, -7.6) * mm, "end": v(74.96, -8.07) * mm});
            skLineSegment(sketch, "E1572", {"start": v(74.96, -8.07) * mm, "end": v(74.88, -8.44) * mm});
            skLineSegment(sketch, "E1573", {"start": v(74.88, -8.44) * mm, "end": v(74.78, -8.91) * mm});
            skLineSegment(sketch, "E1574", {"start": v(74.78, -8.91) * mm, "end": v(74.7, -9.28) * mm});
            skLineSegment(sketch, "E1575", {"start": v(74.7, -9.28) * mm, "end": v(74.58, -9.75) * mm});
            skLineSegment(sketch, "E1576", {"start": v(74.58, -9.75) * mm, "end": v(74.46, -10.21) * mm});
            skLineSegment(sketch, "E1577", {"start": v(74.46, -10.21) * mm, "end": v(74.36, -10.58) * mm});
            skLineSegment(sketch, "E1578", {"start": v(74.36, -10.58) * mm, "end": v(74.26, -10.92) * mm});
            skLineSegment(sketch, "E1579", {"start": v(74.26, -10.92) * mm, "end": v(74.17, -11.2) * mm});
            skLineSegment(sketch, "E1580", {"start": v(74.17, -11.2) * mm, "end": v(74.12, -11.4) * mm});
            skLineSegment(sketch, "E1581", {"start": v(74.12, -11.4) * mm, "end": v(74.03, -11.68) * mm});
            skLineSegment(sketch, "E1582", {"start": v(74.03, -11.68) * mm, "end": v(73.86, -12.22) * mm});
            skLineSegment(sketch, "E1583", {"start": v(73.86, -12.22) * mm, "end": v(73.68, -12.75) * mm});
            skLineSegment(sketch, "E1584", {"start": v(73.68, -12.75) * mm, "end": v(73.59, -13.02) * mm});
            skLineSegment(sketch, "E1585", {"start": v(73.59, -13.02) * mm, "end": v(73.49, -13.3) * mm});
            skLineSegment(sketch, "E1586", {"start": v(73.49, -13.3) * mm, "end": v(73.28, -13.84) * mm});
            skLineSegment(sketch, "E1587", {"start": v(73.28, -13.84) * mm, "end": v(73.1, -14.29) * mm});
            skLineSegment(sketch, "E1588", {"start": v(73.1, -14.29) * mm, "end": v(72.96, -14.64) * mm});
            skLineSegment(sketch, "E1589", {"start": v(72.96, -14.64) * mm, "end": v(72.78, -15.08) * mm});
            skLineSegment(sketch, "E1590", {"start": v(72.78, -15.08) * mm, "end": v(72.63, -15.43) * mm});
            skLineSegment(sketch, "E1591", {"start": v(72.63, -15.43) * mm, "end": v(72.43, -15.86) * mm});
            skLineSegment(sketch, "E1592", {"start": v(72.43, -15.86) * mm, "end": v(72.27, -16.2) * mm});
            skLineSegment(sketch, "E1593", {"start": v(72.27, -16.2) * mm, "end": v(72.06, -16.64) * mm});
            skLineSegment(sketch, "E1594", {"start": v(72.06, -16.64) * mm, "end": v(71.9, -16.98) * mm});
            skLineSegment(sketch, "E1595", {"start": v(71.9, -16.98) * mm, "end": v(71.67, -17.4) * mm});
            skLineSegment(sketch, "E1596", {"start": v(71.67, -17.4) * mm, "end": v(71.5, -17.74) * mm});
            skLineSegment(sketch, "E1597", {"start": v(71.5, -17.74) * mm, "end": v(71.27, -18.16) * mm});
            skLineSegment(sketch, "E1598", {"start": v(71.27, -18.16) * mm, "end": v(71.08, -18.5) * mm});
            skLineSegment(sketch, "E1599", {"start": v(71.08, -18.5) * mm, "end": v(70.84, -18.9) * mm});
            skLineSegment(sketch, "E1600", {"start": v(70.84, -18.9) * mm, "end": v(70.65, -19.24) * mm});
            skLineSegment(sketch, "E1601", {"start": v(70.65, -19.24) * mm, "end": v(70.4, -19.65) * mm});
            skLineSegment(sketch, "E1602", {"start": v(70.4, -19.65) * mm, "end": v(70.2, -19.97) * mm});
            skLineSegment(sketch, "E1603", {"start": v(70.2, -19.97) * mm, "end": v(69.94, -20.37) * mm});
            skLineSegment(sketch, "E1604", {"start": v(69.94, -20.37) * mm, "end": v(69.73, -20.69) * mm});
            skLineSegment(sketch, "E1605", {"start": v(69.73, -20.69) * mm, "end": v(69.46, -21.08) * mm});
            skLineSegment(sketch, "E1606", {"start": v(69.46, -21.08) * mm, "end": v(69.24, -21.4) * mm});
            skLineSegment(sketch, "E1607", {"start": v(69.24, -21.4) * mm, "end": v(68.96, -21.79) * mm});
            skLineSegment(sketch, "E1608", {"start": v(68.96, -21.79) * mm, "end": v(68.74, -22.1) * mm});
            skLineSegment(sketch, "E1609", {"start": v(68.74, -22.1) * mm, "end": v(68.51, -22.4) * mm});
            skLineSegment(sketch, "E1610", {"start": v(68.51, -22.4) * mm, "end": v(68.22, -22.78) * mm});
            skLineSegment(sketch, "E1611", {"start": v(68.22, -22.78) * mm, "end": v(67.92, -23.15) * mm});
            skLineSegment(sketch, "E1612", {"start": v(67.92, -23.15) * mm, "end": v(67.68, -23.45) * mm});
            skLineSegment(sketch, "E1613", {"start": v(67.68, -23.45) * mm, "end": v(67.38, -23.81) * mm});
            skLineSegment(sketch, "E1614", {"start": v(67.38, -23.81) * mm, "end": v(67.13, -24.1) * mm});
            skLineSegment(sketch, "E1615", {"start": v(67.13, -24.1) * mm, "end": v(66.72, -24.57) * mm});
            skLineSegment(sketch, "E1616", {"start": v(66.72, -24.57) * mm, "end": v(66.43, -24.89) * mm});
            skLineSegment(sketch, "E1617", {"start": v(66.43, -24.89) * mm, "end": v(66.3, -25.02) * mm});
            skLineSegment(sketch, "E1618", {"start": v(66.3, -25.02) * mm, "end": v(66.3, -25.01) * mm});
            skLineSegment(sketch, "E1619", {"start": v(66.3, -25.01) * mm, "end": v(66.23, -24.96) * mm});
            skLineSegment(sketch, "E1620", {"start": v(66.23, -24.96) * mm, "end": v(66.16, -24.9) * mm});
            skLineSegment(sketch, "E1621", {"start": v(66.16, -24.9) * mm, "end": v(66.08, -24.85) * mm});
            skLineSegment(sketch, "E1622", {"start": v(66.08, -24.85) * mm, "end": v(66, -24.8) * mm});
            skLineSegment(sketch, "E1623", {"start": v(66, -24.8) * mm, "end": v(65.93, -24.74) * mm});
            skLineSegment(sketch, "E1624", {"start": v(65.93, -24.74) * mm, "end": v(65.85, -24.7) * mm});
            skLineSegment(sketch, "E1625", {"start": v(65.85, -24.7) * mm, "end": v(65.77, -24.64) * mm});
            skLineSegment(sketch, "E1626", {"start": v(65.77, -24.64) * mm, "end": v(65.68, -24.6) * mm});
            skLineSegment(sketch, "E1627", {"start": v(65.68, -24.6) * mm, "end": v(65.6, -24.55) * mm});
            skLineSegment(sketch, "E1628", {"start": v(65.6, -24.55) * mm, "end": v(65.5, -24.5) * mm});
            skLineSegment(sketch, "E1629", {"start": v(65.5, -24.5) * mm, "end": v(65.41, -24.46) * mm});
            skLineSegment(sketch, "E1630", {"start": v(65.41, -24.46) * mm, "end": v(65.32, -24.41) * mm});
            skLineSegment(sketch, "E1631", {"start": v(65.32, -24.41) * mm, "end": v(65.22, -24.37) * mm});
            skLineSegment(sketch, "E1632", {"start": v(65.22, -24.37) * mm, "end": v(65.12, -24.33) * mm});
            skLineSegment(sketch, "E1633", {"start": v(65.12, -24.33) * mm, "end": v(65.05, -24.28) * mm});
            skLineSegment(sketch, "E1634", {"start": v(65.05, -24.28) * mm, "end": v(64.95, -24.24) * mm});
            skLineSegment(sketch, "E1635", {"start": v(64.95, -24.24) * mm, "end": v(64.9, -24.2) * mm});
            skLineSegment(sketch, "E1636", {"start": v(64.9, -24.2) * mm, "end": v(64.8, -24.16) * mm});
            skLineSegment(sketch, "E1637", {"start": v(64.8, -24.16) * mm, "end": v(64.73, -24.11) * mm});
            skLineSegment(sketch, "E1638", {"start": v(64.73, -24.11) * mm, "end": v(64.63, -24.08) * mm});
            skLineSegment(sketch, "E1639", {"start": v(64.63, -24.08) * mm, "end": v(64.57, -24.04) * mm});
            skLineSegment(sketch, "E1640", {"start": v(64.57, -24.04) * mm, "end": v(64.5, -24) * mm});
            skLineSegment(sketch, "E1641", {"start": v(64.5, -24) * mm, "end": v(64.4, -23.97) * mm});
            skLineSegment(sketch, "E1642", {"start": v(64.4, -23.97) * mm, "end": v(64.34, -23.93) * mm});
            skLineSegment(sketch, "E1643", {"start": v(64.34, -23.93) * mm, "end": v(64.24, -23.9) * mm});
            skLineSegment(sketch, "E1644", {"start": v(64.24, -23.9) * mm, "end": v(64.17, -23.87) * mm});
            skLineSegment(sketch, "E1645", {"start": v(64.17, -23.87) * mm, "end": v(64.07, -23.84) * mm});
            skLineSegment(sketch, "E1646", {"start": v(64.07, -23.84) * mm, "end": v(64, -23.8) * mm});
            skLineSegment(sketch, "E1647", {"start": v(64, -23.8) * mm, "end": v(63.94, -23.77) * mm});
            skLineSegment(sketch, "E1648", {"start": v(63.94, -23.77) * mm, "end": v(63.84, -23.75) * mm});
            skLineSegment(sketch, "E1649", {"start": v(63.84, -23.75) * mm, "end": v(63.77, -23.72) * mm});
            skLineSegment(sketch, "E1650", {"start": v(63.77, -23.72) * mm, "end": v(63.66, -23.7) * mm});
            skLineSegment(sketch, "E1651", {"start": v(63.66, -23.7) * mm, "end": v(63.6, -23.67) * mm});
            skLineSegment(sketch, "E1652", {"start": v(63.6, -23.67) * mm, "end": v(63.5, -23.65) * mm});
            skLineSegment(sketch, "E1653", {"start": v(63.5, -23.65) * mm, "end": v(63.43, -23.63) * mm});
            skLineSegment(sketch, "E1654", {"start": v(63.43, -23.63) * mm, "end": v(63.37, -23.6) * mm});
            skLineSegment(sketch, "E1655", {"start": v(63.37, -23.6) * mm, "end": v(63.26, -23.59) * mm});
            skLineSegment(sketch, "E1656", {"start": v(63.26, -23.59) * mm, "end": v(63.2, -23.56) * mm});
            skLineSegment(sketch, "E1657", {"start": v(63.2, -23.56) * mm, "end": v(63.08, -23.55) * mm});
            skLineSegment(sketch, "E1658", {"start": v(63.08, -23.55) * mm, "end": v(63.02, -23.53) * mm});
            skLineSegment(sketch, "E1659", {"start": v(63.02, -23.53) * mm, "end": v(62.96, -23.5) * mm});
            skLineSegment(sketch, "E1660", {"start": v(62.96, -23.5) * mm, "end": v(62.84, -23.5) * mm});
            skLineSegment(sketch, "E1661", {"start": v(62.84, -23.5) * mm, "end": v(62.78, -23.48) * mm});
            skLineSegment(sketch, "E1662", {"start": v(62.78, -23.48) * mm, "end": v(62.67, -23.47) * mm});
            skLineSegment(sketch, "E1663", {"start": v(62.67, -23.47) * mm, "end": v(62.6, -23.46) * mm});
            skLineSegment(sketch, "E1664", {"start": v(62.6, -23.46) * mm, "end": v(62.5, -23.45) * mm});
            skLineSegment(sketch, "E1665", {"start": v(62.5, -23.45) * mm, "end": v(62.43, -23.44) * mm});
            skLineSegment(sketch, "E1666", {"start": v(62.43, -23.44) * mm, "end": v(62.37, -23.42) * mm});
            skLineSegment(sketch, "E1667", {"start": v(62.37, -23.42) * mm, "end": v(62.25, -23.42) * mm});
            skLineSegment(sketch, "E1668", {"start": v(62.25, -23.42) * mm, "end": v(62.19, -23.41) * mm});
            skLineSegment(sketch, "E1669", {"start": v(62.19, -23.41) * mm, "end": v(62.08, -23.41) * mm});
            skLineSegment(sketch, "E1670", {"start": v(62.08, -23.41) * mm, "end": v(62.01, -23.4) * mm});
            skLineSegment(sketch, "E1671", {"start": v(62.01, -23.4) * mm, "end": v(61.9, -23.4) * mm});
            skLineSegment(sketch, "E1672", {"start": v(61.9, -23.4) * mm, "end": v(61.84, -23.4) * mm});
            skLineSegment(sketch, "E1673", {"start": v(61.84, -23.4) * mm, "end": v(61.78, -23.4) * mm});
            skLineSegment(sketch, "E1674", {"start": v(61.78, -23.4) * mm, "end": v(61.66, -23.4) * mm});
            skLineSegment(sketch, "E1675", {"start": v(61.66, -23.4) * mm, "end": v(61.6, -23.4) * mm});
            skLineSegment(sketch, "E1676", {"start": v(61.6, -23.4) * mm, "end": v(61.48, -23.4) * mm});
            skLineSegment(sketch, "E1677", {"start": v(61.48, -23.4) * mm, "end": v(61.42, -23.4) * mm});
            skLineSegment(sketch, "E1678", {"start": v(61.42, -23.4) * mm, "end": v(61.3, -23.42) * mm});
            skLineSegment(sketch, "E1679", {"start": v(61.3, -23.42) * mm, "end": v(61.25, -23.41) * mm});
            skLineSegment(sketch, "E1680", {"start": v(61.25, -23.41) * mm, "end": v(61.19, -23.41) * mm});
            skLineSegment(sketch, "E1681", {"start": v(61.19, -23.41) * mm, "end": v(61.07, -23.43) * mm});
            skLineSegment(sketch, "E1682", {"start": v(61.07, -23.43) * mm, "end": v(61.02, -23.43) * mm});
            skLineSegment(sketch, "E1683", {"start": v(61.02, -23.43) * mm, "end": v(60.9, -23.45) * mm});
            skLineSegment(sketch, "E1684", {"start": v(60.9, -23.45) * mm, "end": v(60.84, -23.45) * mm});
            skLineSegment(sketch, "E1685", {"start": v(60.84, -23.45) * mm, "end": v(60.73, -23.47) * mm});
            skLineSegment(sketch, "E1686", {"start": v(60.73, -23.47) * mm, "end": v(60.67, -23.48) * mm});
            skLineSegment(sketch, "E1687", {"start": v(60.67, -23.48) * mm, "end": v(60.61, -23.48) * mm});
            skLineSegment(sketch, "E1688", {"start": v(60.61, -23.48) * mm, "end": v(60.5, -23.5) * mm});
            skLineSegment(sketch, "E1689", {"start": v(60.5, -23.5) * mm, "end": v(60.44, -23.51) * mm});
            skLineSegment(sketch, "E1690", {"start": v(60.44, -23.51) * mm, "end": v(60.33, -23.54) * mm});
            skLineSegment(sketch, "E1691", {"start": v(60.33, -23.54) * mm, "end": v(60.27, -23.55) * mm});
            skLineSegment(sketch, "E1692", {"start": v(60.27, -23.55) * mm, "end": v(60.16, -23.58) * mm});
            skLineSegment(sketch, "E1693", {"start": v(60.16, -23.58) * mm, "end": v(60.1, -23.59) * mm});
            skLineSegment(sketch, "E1694", {"start": v(60.1, -23.59) * mm, "end": v(60.04, -23.6) * mm});
            skLineSegment(sketch, "E1695", {"start": v(60.04, -23.6) * mm, "end": v(59.93, -23.63) * mm});
            skLineSegment(sketch, "E1696", {"start": v(59.93, -23.63) * mm, "end": v(59.88, -23.64) * mm});
            skLineSegment(sketch, "E1697", {"start": v(59.88, -23.64) * mm, "end": v(59.77, -23.68) * mm});
            skLineSegment(sketch, "E1698", {"start": v(59.77, -23.68) * mm, "end": v(59.71, -23.7) * mm});
            skLineSegment(sketch, "E1699", {"start": v(59.71, -23.7) * mm, "end": v(59.24, -23.86) * mm});
            skLineSegment(sketch, "E1700", {"start": v(59.24, -23.86) * mm, "end": v(59.16, -23.89) * mm});
            skLineSegment(sketch, "E1701", {"start": v(59.16, -23.89) * mm, "end": v(59.08, -23.92) * mm});
            skLineSegment(sketch, "E1702", {"start": v(59.08, -23.92) * mm, "end": v(59, -23.95) * mm});
            skLineSegment(sketch, "E1703", {"start": v(59, -23.95) * mm, "end": v(58.92, -23.98) * mm});
            skLineSegment(sketch, "E1704", {"start": v(58.92, -23.98) * mm, "end": v(58.84, -24.02) * mm});
            skLineSegment(sketch, "E1705", {"start": v(58.84, -24.02) * mm, "end": v(58.78, -24.05) * mm});
            skLineSegment(sketch, "E1706", {"start": v(58.78, -24.05) * mm, "end": v(58.7, -24.09) * mm});
            skLineSegment(sketch, "E1707", {"start": v(58.7, -24.09) * mm, "end": v(58.63, -24.13) * mm});
            skLineSegment(sketch, "E1708", {"start": v(58.63, -24.13) * mm, "end": v(58.55, -24.17) * mm});
            skLineSegment(sketch, "E1709", {"start": v(58.55, -24.17) * mm, "end": v(58.47, -24.2) * mm});
            skLineSegment(sketch, "E1710", {"start": v(58.47, -24.2) * mm, "end": v(58.4, -24.24) * mm});
            skLineSegment(sketch, "E1711", {"start": v(58.4, -24.24) * mm, "end": v(58.32, -24.29) * mm});
            skLineSegment(sketch, "E1712", {"start": v(58.32, -24.29) * mm, "end": v(58.25, -24.33) * mm});
            skLineSegment(sketch, "E1713", {"start": v(58.25, -24.33) * mm, "end": v(58.17, -24.38) * mm});
            skLineSegment(sketch, "E1714", {"start": v(58.17, -24.38) * mm, "end": v(58.1, -24.42) * mm});
            skLineSegment(sketch, "E1715", {"start": v(58.1, -24.42) * mm, "end": v(58.03, -24.47) * mm});
            skLineSegment(sketch, "E1716", {"start": v(58.03, -24.47) * mm, "end": v(57.96, -24.51) * mm});
            skLineSegment(sketch, "E1717", {"start": v(57.96, -24.51) * mm, "end": v(57.88, -24.56) * mm});
            skLineSegment(sketch, "E1718", {"start": v(57.88, -24.56) * mm, "end": v(57.81, -24.6) * mm});
            skLineSegment(sketch, "E1719", {"start": v(57.81, -24.6) * mm, "end": v(57.74, -24.66) * mm});
            skLineSegment(sketch, "E1720", {"start": v(57.74, -24.66) * mm, "end": v(57.67, -24.7) * mm});
            skLineSegment(sketch, "E1721", {"start": v(57.67, -24.7) * mm, "end": v(57.6, -24.76) * mm});
            skLineSegment(sketch, "E1722", {"start": v(57.6, -24.76) * mm, "end": v(57.54, -24.8) * mm});
            skLineSegment(sketch, "E1723", {"start": v(57.54, -24.8) * mm, "end": v(57.47, -24.86) * mm});
            skLineSegment(sketch, "E1724", {"start": v(57.47, -24.86) * mm, "end": v(57.4, -24.91) * mm});
            skLineSegment(sketch, "E1725", {"start": v(57.4, -24.91) * mm, "end": v(57.34, -24.97) * mm});
            skLineSegment(sketch, "E1726", {"start": v(57.34, -24.97) * mm, "end": v(57.27, -25.02) * mm});
            skLineSegment(sketch, "E1727", {"start": v(57.27, -25.02) * mm, "end": v(57.2, -25.08) * mm});
            skLineSegment(sketch, "E1728", {"start": v(57.2, -25.08) * mm, "end": v(57.14, -25.14) * mm});
            skLineSegment(sketch, "E1729", {"start": v(57.14, -25.14) * mm, "end": v(57.08, -25.2) * mm});
            skLineSegment(sketch, "E1730", {"start": v(57.08, -25.2) * mm, "end": v(57.01, -25.25) * mm});
            skLineSegment(sketch, "E1731", {"start": v(57.01, -25.25) * mm, "end": v(56.95, -25.31) * mm});
            skLineSegment(sketch, "E1732", {"start": v(56.95, -25.31) * mm, "end": v(56.89, -25.37) * mm});
            skLineSegment(sketch, "E1733", {"start": v(56.89, -25.37) * mm, "end": v(56.83, -25.43) * mm});
            skLineSegment(sketch, "E1734", {"start": v(56.83, -25.43) * mm, "end": v(56.77, -25.5) * mm});
            skLineSegment(sketch, "E1735", {"start": v(56.77, -25.5) * mm, "end": v(56.7, -25.55) * mm});
            skLineSegment(sketch, "E1736", {"start": v(56.7, -25.55) * mm, "end": v(56.66, -25.6) * mm});
            skLineSegment(sketch, "E1737", {"start": v(56.66, -25.6) * mm, "end": v(56.6, -25.67) * mm});
            skLineSegment(sketch, "E1738", {"start": v(56.6, -25.67) * mm, "end": v(56.55, -25.73) * mm});
            skLineSegment(sketch, "E1739", {"start": v(56.55, -25.73) * mm, "end": v(56.53, -25.74) * mm});
            skLineSegment(sketch, "E1740", {"start": v(56.53, -25.74) * mm, "end": v(56.5, -25.79) * mm});
            skLineSegment(sketch, "E1741", {"start": v(56.5, -25.79) * mm, "end": v(56.42, -25.88) * mm});
            skLineSegment(sketch, "E1742", {"start": v(56.42, -25.88) * mm, "end": v(56.39, -25.92) * mm});
            skLineSegment(sketch, "E1743", {"start": v(56.39, -25.92) * mm, "end": v(56.31, -26) * mm});
            skLineSegment(sketch, "E1744", {"start": v(56.31, -26) * mm, "end": v(56.28, -26.05) * mm});
            skLineSegment(sketch, "E1745", {"start": v(56.28, -26.05) * mm, "end": v(56.2, -26.14) * mm});
            skLineSegment(sketch, "E1746", {"start": v(56.2, -26.14) * mm, "end": v(56.17, -26.19) * mm});
            skLineSegment(sketch, "E1747", {"start": v(56.17, -26.19) * mm, "end": v(56.1, -26.28) * mm});
            skLineSegment(sketch, "E1748", {"start": v(56.1, -26.28) * mm, "end": v(56.07, -26.33) * mm});
            skLineSegment(sketch, "E1749", {"start": v(56.07, -26.33) * mm, "end": v(56, -26.42) * mm});
            skLineSegment(sketch, "E1750", {"start": v(56, -26.42) * mm, "end": v(55.98, -26.47) * mm});
            skLineSegment(sketch, "E1751", {"start": v(55.98, -26.47) * mm, "end": v(55.91, -26.57) * mm});
            skLineSegment(sketch, "E1752", {"start": v(55.91, -26.57) * mm, "end": v(55.88, -26.62) * mm});
            skLineSegment(sketch, "E1753", {"start": v(55.88, -26.62) * mm, "end": v(55.82, -26.71) * mm});
            skLineSegment(sketch, "E1754", {"start": v(55.82, -26.71) * mm, "end": v(55.8, -26.76) * mm});
            skLineSegment(sketch, "E1755", {"start": v(55.8, -26.76) * mm, "end": v(55.73, -26.86) * mm});
            skLineSegment(sketch, "E1756", {"start": v(55.73, -26.86) * mm, "end": v(55.7, -26.91) * mm});
            skLineSegment(sketch, "E1757", {"start": v(55.7, -26.91) * mm, "end": v(55.65, -27) * mm});
            skLineSegment(sketch, "E1758", {"start": v(55.65, -27) * mm, "end": v(55.62, -27.06) * mm});
            skLineSegment(sketch, "E1759", {"start": v(55.62, -27.06) * mm, "end": v(55.57, -27.16) * mm});
            skLineSegment(sketch, "E1760", {"start": v(55.57, -27.16) * mm, "end": v(55.54, -27.21) * mm});
            skLineSegment(sketch, "E1761", {"start": v(55.54, -27.21) * mm, "end": v(55.5, -27.31) * mm});
            skLineSegment(sketch, "E1762", {"start": v(55.5, -27.31) * mm, "end": v(55.46, -27.37) * mm});
            skLineSegment(sketch, "E1763", {"start": v(55.46, -27.37) * mm, "end": v(55.42, -27.47) * mm});
            skLineSegment(sketch, "E1764", {"start": v(55.42, -27.47) * mm, "end": v(55.4, -27.53) * mm});
            skLineSegment(sketch, "E1765", {"start": v(55.4, -27.53) * mm, "end": v(55.35, -27.63) * mm});
            skLineSegment(sketch, "E1766", {"start": v(55.35, -27.63) * mm, "end": v(55.32, -27.68) * mm});
            skLineSegment(sketch, "E1767", {"start": v(55.32, -27.68) * mm, "end": v(55.28, -27.79) * mm});
            skLineSegment(sketch, "E1768", {"start": v(55.28, -27.79) * mm, "end": v(55.26, -27.84) * mm});
            skLineSegment(sketch, "E1769", {"start": v(55.26, -27.84) * mm, "end": v(55.22, -27.95) * mm});
            skLineSegment(sketch, "E1770", {"start": v(55.22, -27.95) * mm, "end": v(55.2, -28) * mm});
            skLineSegment(sketch, "E1771", {"start": v(55.2, -28) * mm, "end": v(55.16, -28.1) * mm});
            skLineSegment(sketch, "E1772", {"start": v(55.16, -28.1) * mm, "end": v(55.14, -28.17) * mm});
            skLineSegment(sketch, "E1773", {"start": v(55.14, -28.17) * mm, "end": v(55.11, -28.27) * mm});
            skLineSegment(sketch, "E1774", {"start": v(55.11, -28.27) * mm, "end": v(55.1, -28.33) * mm});
            skLineSegment(sketch, "E1775", {"start": v(55.1, -28.33) * mm, "end": v(55.06, -28.44) * mm});
            skLineSegment(sketch, "E1776", {"start": v(55.06, -28.44) * mm, "end": v(55.04, -28.5) * mm});
            skLineSegment(sketch, "E1777", {"start": v(55.04, -28.5) * mm, "end": v(55.02, -28.6) * mm});
            skLineSegment(sketch, "E1778", {"start": v(55.02, -28.6) * mm, "end": v(55, -28.67) * mm});
            skLineSegment(sketch, "E1779", {"start": v(55, -28.67) * mm, "end": v(54.97, -28.77) * mm});
            skLineSegment(sketch, "E1780", {"start": v(54.97, -28.77) * mm, "end": v(54.96, -28.83) * mm});
            skLineSegment(sketch, "E1781", {"start": v(54.96, -28.83) * mm, "end": v(54.94, -28.94) * mm});
            skLineSegment(sketch, "E1782", {"start": v(54.94, -28.94) * mm, "end": v(54.92, -29) * mm});
            skLineSegment(sketch, "E1783", {"start": v(54.92, -29) * mm, "end": v(54.9, -29.1) * mm});
            skLineSegment(sketch, "E1784", {"start": v(54.9, -29.1) * mm, "end": v(54.9, -29.17) * mm});
            skLineSegment(sketch, "E1785", {"start": v(54.9, -29.17) * mm, "end": v(54.88, -29.27) * mm});
            skLineSegment(sketch, "E1786", {"start": v(54.88, -29.27) * mm, "end": v(54.87, -29.34) * mm});
            skLineSegment(sketch, "E1787", {"start": v(54.87, -29.34) * mm, "end": v(54.85, -29.44) * mm});
            skLineSegment(sketch, "E1788", {"start": v(54.85, -29.44) * mm, "end": v(54.84, -29.51) * mm});
            skLineSegment(sketch, "E1789", {"start": v(54.84, -29.51) * mm, "end": v(54.83, -29.62) * mm});
            skLineSegment(sketch, "E1790", {"start": v(54.83, -29.62) * mm, "end": v(54.82, -29.68) * mm});
            skLineSegment(sketch, "E1791", {"start": v(54.82, -29.68) * mm, "end": v(54.81, -29.79) * mm});
            skLineSegment(sketch, "E1792", {"start": v(54.81, -29.79) * mm, "end": v(54.8, -29.86) * mm});
            skLineSegment(sketch, "E1793", {"start": v(54.8, -29.86) * mm, "end": v(54.8, -29.96) * mm});
            skLineSegment(sketch, "E1794", {"start": v(54.8, -29.96) * mm, "end": v(54.8, -30.03) * mm});
            skLineSegment(sketch, "E1795", {"start": v(54.8, -30.03) * mm, "end": v(54.8, -30.13) * mm});
            skLineSegment(sketch, "E1796", {"start": v(54.8, -30.13) * mm, "end": v(54.8, -30.2) * mm});
            skLineSegment(sketch, "E1797", {"start": v(54.8, -30.2) * mm, "end": v(54.79, -30.3) * mm});
            skLineSegment(sketch, "E1798", {"start": v(54.79, -30.3) * mm, "end": v(54.79, -30.37) * mm});
            skLineSegment(sketch, "E1799", {"start": v(54.79, -30.37) * mm, "end": v(54.79, -30.47) * mm});
            skLineSegment(sketch, "E1800", {"start": v(54.79, -30.47) * mm, "end": v(54.8, -30.55) * mm});
            skLineSegment(sketch, "E1801", {"start": v(54.8, -30.55) * mm, "end": v(54.8, -30.64) * mm});
            skLineSegment(sketch, "E1802", {"start": v(54.8, -30.64) * mm, "end": v(54.8, -30.72) * mm});
            skLineSegment(sketch, "E1803", {"start": v(54.8, -30.72) * mm, "end": v(54.8, -30.82) * mm});
            skLineSegment(sketch, "E1804", {"start": v(54.8, -30.82) * mm, "end": v(54.8, -30.9) * mm});
            skLineSegment(sketch, "E1805", {"start": v(54.8, -30.9) * mm, "end": v(54.82, -30.99) * mm});
            skLineSegment(sketch, "E1806", {"start": v(54.82, -30.99) * mm, "end": v(54.82, -31.06) * mm});
            skLineSegment(sketch, "E1807", {"start": v(54.82, -31.06) * mm, "end": v(54.83, -31.16) * mm});
            skLineSegment(sketch, "E1808", {"start": v(54.83, -31.16) * mm, "end": v(54.84, -31.23) * mm});
            skLineSegment(sketch, "E1809", {"start": v(54.84, -31.23) * mm, "end": v(54.86, -31.33) * mm});
            skLineSegment(sketch, "E1810", {"start": v(54.86, -31.33) * mm, "end": v(54.87, -31.4) * mm});
            skLineSegment(sketch, "E1811", {"start": v(54.87, -31.4) * mm, "end": v(54.88, -31.5) * mm});
            skLineSegment(sketch, "E1812", {"start": v(54.88, -31.5) * mm, "end": v(54.9, -31.58) * mm});
            skLineSegment(sketch, "E1813", {"start": v(54.9, -31.58) * mm, "end": v(54.91, -31.67) * mm});
            skLineSegment(sketch, "E1814", {"start": v(54.91, -31.67) * mm, "end": v(54.93, -31.75) * mm});
            skLineSegment(sketch, "E1815", {"start": v(54.93, -31.75) * mm, "end": v(54.94, -31.84) * mm});
            skLineSegment(sketch, "E1816", {"start": v(54.94, -31.84) * mm, "end": v(54.96, -31.91) * mm});
            skLineSegment(sketch, "E1817", {"start": v(54.96, -31.91) * mm, "end": v(54.98, -32) * mm});
            skLineSegment(sketch, "E1818", {"start": v(54.98, -32) * mm, "end": v(55, -32.08) * mm});
            skLineSegment(sketch, "E1819", {"start": v(55, -32.08) * mm, "end": v(55.02, -32.17) * mm});
            skLineSegment(sketch, "E1820", {"start": v(55.02, -32.17) * mm, "end": v(55.05, -32.25) * mm});
            skLineSegment(sketch, "E1821", {"start": v(55.05, -32.25) * mm, "end": v(55.07, -32.34) * mm});
            skLineSegment(sketch, "E1822", {"start": v(55.07, -32.34) * mm, "end": v(55.1, -32.41) * mm});
            skLineSegment(sketch, "E1823", {"start": v(55.1, -32.41) * mm, "end": v(55.12, -32.5) * mm});
            skLineSegment(sketch, "E1824", {"start": v(55.12, -32.5) * mm, "end": v(55.15, -32.58) * mm});
            skLineSegment(sketch, "E1825", {"start": v(55.15, -32.58) * mm, "end": v(55.18, -32.66) * mm});
            skLineSegment(sketch, "E1826", {"start": v(55.18, -32.66) * mm, "end": v(55.2, -32.74) * mm});
            skLineSegment(sketch, "E1827", {"start": v(55.2, -32.74) * mm, "end": v(55.23, -32.82) * mm});
            skLineSegment(sketch, "E1828", {"start": v(55.23, -32.82) * mm, "end": v(55.26, -32.9) * mm});
            skLineSegment(sketch, "E1829", {"start": v(55.26, -32.9) * mm, "end": v(55.3, -32.98) * mm});
            skLineSegment(sketch, "E1830", {"start": v(55.3, -32.98) * mm, "end": v(55.3, -33) * mm});
            skLineSegment(sketch, "E1831", {"start": v(55.3, -33) * mm, "end": v(55.3, -33.01) * mm});
            skLineSegment(sketch, "E1832", {"start": v(55.3, -33.01) * mm, "end": v(55.06, -33.13) * mm});
            skLineSegment(sketch, "E1833", {"start": v(55.06, -33.13) * mm, "end": v(54.81, -33.24) * mm});
            skLineSegment(sketch, "E1834", {"start": v(54.81, -33.24) * mm, "end": v(54.76, -33.26) * mm});
            skLineSegment(sketch, "E1835", {"start": v(54.76, -33.26) * mm, "end": v(54.59, -33.34) * mm});
            skLineSegment(sketch, "E1836", {"start": v(54.59, -33.34) * mm, "end": v(54.36, -33.43) * mm});
            skLineSegment(sketch, "E1837", {"start": v(54.36, -33.43) * mm, "end": v(54.33, -33.45) * mm});
            skLineSegment(sketch, "E1838", {"start": v(54.33, -33.45) * mm, "end": v(54.02, -33.58) * mm});
            skLineSegment(sketch, "E1839", {"start": v(54.02, -33.58) * mm, "end": v(53.8, -33.67) * mm});
            skLineSegment(sketch, "E1840", {"start": v(53.8, -33.67) * mm, "end": v(53.53, -33.78) * mm});
            skLineSegment(sketch, "E1841", {"start": v(53.53, -33.78) * mm, "end": v(53.23, -33.9) * mm});
            skLineSegment(sketch, "E1842", {"start": v(53.23, -33.9) * mm, "end": v(53.22, -33.9) * mm});
            skLineSegment(sketch, "E1843", {"start": v(53.22, -33.9) * mm, "end": v(52.92, -34.01) * mm});
            skLineSegment(sketch, "E1844", {"start": v(52.92, -34.01) * mm, "end": v(52.62, -34.12) * mm});
            skLineSegment(sketch, "E1845", {"start": v(52.62, -34.12) * mm, "end": v(52.42, -34.2) * mm});
            skLineSegment(sketch, "E1846", {"start": v(52.42, -34.2) * mm, "end": v(52.12, -34.3) * mm});
            skLineSegment(sketch, "E1847", {"start": v(52.12, -34.3) * mm, "end": v(52.02, -34.34) * mm});
            skLineSegment(sketch, "E1848", {"start": v(52.02, -34.34) * mm, "end": v(51.71, -34.43) * mm});
            skLineSegment(sketch, "E1849", {"start": v(51.71, -34.43) * mm, "end": v(51.41, -34.54) * mm});
            skLineSegment(sketch, "E1850", {"start": v(51.41, -34.54) * mm, "end": v(51.1, -34.63) * mm});
            skLineSegment(sketch, "E1851", {"start": v(51.1, -34.63) * mm, "end": v(50.78, -34.71) * mm});
            skLineSegment(sketch, "E1852", {"start": v(50.78, -34.71) * mm, "end": v(50.65, -34.75) * mm});
            skLineSegment(sketch, "E1853", {"start": v(50.65, -34.75) * mm, "end": v(50.49, -34.8) * mm});
            skLineSegment(sketch, "E1854", {"start": v(50.49, -34.8) * mm, "end": v(50.23, -34.89) * mm});
            skLineSegment(sketch, "E1855", {"start": v(50.23, -34.89) * mm, "end": v(49.6, -35.07) * mm});
            skLineSegment(sketch, "E1856", {"start": v(49.6, -35.07) * mm, "end": v(49.13, -35.2) * mm});
            skLineSegment(sketch, "E1857", {"start": v(49.13, -35.2) * mm, "end": v(48.76, -35.28) * mm});
            skLineSegment(sketch, "E1858", {"start": v(48.76, -35.28) * mm, "end": v(48.3, -35.4) * mm});
            skLineSegment(sketch, "E1859", {"start": v(48.3, -35.4) * mm, "end": v(47.93, -35.47) * mm});
            skLineSegment(sketch, "E1860", {"start": v(47.93, -35.47) * mm, "end": v(47.46, -35.57) * mm});
            skLineSegment(sketch, "E1861", {"start": v(47.46, -35.57) * mm, "end": v(47.08, -35.64) * mm});
            skLineSegment(sketch, "E1862", {"start": v(47.08, -35.64) * mm, "end": v(46.61, -35.73) * mm});
            skLineSegment(sketch, "E1863", {"start": v(46.61, -35.73) * mm, "end": v(46.14, -35.8) * mm});
            skLineSegment(sketch, "E1864", {"start": v(46.14, -35.8) * mm, "end": v(45.76, -35.87) * mm});
            skLineSegment(sketch, "E1865", {"start": v(45.76, -35.87) * mm, "end": v(45.39, -35.92) * mm});
            skLineSegment(sketch, "E1866", {"start": v(45.39, -35.92) * mm, "end": v(44.91, -35.98) * mm});
            skLineSegment(sketch, "E1867", {"start": v(44.91, -35.98) * mm, "end": v(44.54, -36.02) * mm});
            skLineSegment(sketch, "E1868", {"start": v(44.54, -36.02) * mm, "end": v(44.06, -36.08) * mm});
            skLineSegment(sketch, "E1869", {"start": v(44.06, -36.08) * mm, "end": v(43.68, -36.1) * mm});
            skLineSegment(sketch, "E1870", {"start": v(43.68, -36.1) * mm, "end": v(43.2, -36.15) * mm});
            skLineSegment(sketch, "E1871", {"start": v(43.2, -36.15) * mm, "end": v(42.73, -36.18) * mm});
            skLineSegment(sketch, "E1872", {"start": v(42.73, -36.18) * mm, "end": v(42.35, -36.2) * mm});
            skLineSegment(sketch, "E1873", {"start": v(42.35, -36.2) * mm, "end": v(41.88, -36.22) * mm});
            skLineSegment(sketch, "E1874", {"start": v(41.88, -36.22) * mm, "end": v(41.59, -36.23) * mm});
            skLineSegment(sketch, "E1875", {"start": v(41.59, -36.23) * mm, "end": v(41.49, -36.23) * mm});
            skLineSegment(sketch, "E1876", {"start": v(41.49, -36.23) * mm, "end": v(41.2, -36.23) * mm});
            skLineSegment(sketch, "E1877", {"start": v(41.2, -36.23) * mm, "end": v(40.9, -36.23) * mm});
            skLineSegment(sketch, "E1878", {"start": v(40.9, -36.23) * mm, "end": v(39.77, -36.24) * mm});
            skLineSegment(sketch, "E1879", {"start": v(39.77, -36.24) * mm, "end": v(39.67, -36.23) * mm});
            skLineSegment(sketch, "E1880", {"start": v(39.67, -36.23) * mm, "end": v(39.38, -36.22) * mm});
            skLineSegment(sketch, "E1881", {"start": v(39.38, -36.22) * mm, "end": v(39.09, -36.2) * mm});
            skLineSegment(sketch, "E1882", {"start": v(39.09, -36.2) * mm, "end": v(38.05, -36.15) * mm});
            skLineSegment(sketch, "E1883", {"start": v(38.05, -36.15) * mm, "end": v(37.58, -36.1) * mm});
            skLineSegment(sketch, "E1884", {"start": v(37.58, -36.1) * mm, "end": v(37.2, -36.08) * mm});
            skLineSegment(sketch, "E1885", {"start": v(37.2, -36.08) * mm, "end": v(36.72, -36.02) * mm});
            skLineSegment(sketch, "E1886", {"start": v(36.72, -36.02) * mm, "end": v(36.34, -35.98) * mm});
            skLineSegment(sketch, "E1887", {"start": v(36.34, -35.98) * mm, "end": v(35.87, -35.92) * mm});
            skLineSegment(sketch, "E1888", {"start": v(35.87, -35.92) * mm, "end": v(35.5, -35.87) * mm});
            skLineSegment(sketch, "E1889", {"start": v(35.5, -35.87) * mm, "end": v(35.02, -35.79) * mm});
            skLineSegment(sketch, "E1890", {"start": v(35.02, -35.79) * mm, "end": v(34.64, -35.73) * mm});
            skLineSegment(sketch, "E1891", {"start": v(34.64, -35.73) * mm, "end": v(34.27, -35.66) * mm});
            skLineSegment(sketch, "E1892", {"start": v(34.27, -35.66) * mm, "end": v(33.8, -35.57) * mm});
            skLineSegment(sketch, "E1893", {"start": v(33.8, -35.57) * mm, "end": v(33.33, -35.47) * mm});
            skLineSegment(sketch, "E1894", {"start": v(33.33, -35.47) * mm, "end": v(32.96, -35.4) * mm});
            skLineSegment(sketch, "E1895", {"start": v(32.96, -35.4) * mm, "end": v(32.6, -35.3) * mm});
            skLineSegment(sketch, "E1896", {"start": v(32.6, -35.3) * mm, "end": v(32.12, -35.2) * mm});
            skLineSegment(sketch, "E1897", {"start": v(32.12, -35.2) * mm, "end": v(31.66, -35.07) * mm});
            skLineSegment(sketch, "E1898", {"start": v(31.66, -35.07) * mm, "end": v(31.3, -34.98) * mm});
            skLineSegment(sketch, "E1899", {"start": v(31.3, -34.98) * mm, "end": v(30.93, -34.87) * mm});
            skLineSegment(sketch, "E1900", {"start": v(30.93, -34.87) * mm, "end": v(30.47, -34.74) * mm});
            skLineSegment(sketch, "E1901", {"start": v(30.47, -34.74) * mm, "end": v(30.01, -34.6) * mm});
            skLineSegment(sketch, "E1902", {"start": v(30.01, -34.6) * mm, "end": v(29.65, -34.48) * mm});
            skLineSegment(sketch, "E1903", {"start": v(29.65, -34.48) * mm, "end": v(29.2, -34.32) * mm});
            skLineSegment(sketch, "E1904", {"start": v(29.2, -34.32) * mm, "end": v(28.84, -34.2) * mm});
            skLineSegment(sketch, "E1905", {"start": v(28.84, -34.2) * mm, "end": v(28.48, -34.07) * mm});
            skLineSegment(sketch, "E1906", {"start": v(28.48, -34.07) * mm, "end": v(28.03, -33.9) * mm});
            skLineSegment(sketch, "E1907", {"start": v(28.03, -33.9) * mm, "end": v(27.68, -33.76) * mm});
            skLineSegment(sketch, "E1908", {"start": v(27.68, -33.76) * mm, "end": v(26.99, -33.45) * mm});
            skLineSegment(sketch, "E1909", {"start": v(26.99, -33.45) * mm, "end": v(26.59, -33.3) * mm});
            skLineSegment(sketch, "E1910", {"start": v(26.59, -33.3) * mm, "end": v(26.2, -33.13) * mm});
            skLineSegment(sketch, "E1911", {"start": v(26.2, -33.13) * mm, "end": v(25.95, -33.01) * mm});
            skLineSegment(sketch, "E1912", {"start": v(25.95, -33.01) * mm, "end": v(25.96, -33) * mm});
            skLineSegment(sketch, "E1913", {"start": v(25.96, -33) * mm, "end": v(25.99, -32.92) * mm});
            skLineSegment(sketch, "E1914", {"start": v(25.99, -32.92) * mm, "end": v(26.02, -32.83) * mm});
            skLineSegment(sketch, "E1915", {"start": v(26.02, -32.83) * mm, "end": v(26.05, -32.75) * mm});
            skLineSegment(sketch, "E1916", {"start": v(26.05, -32.75) * mm, "end": v(26.07, -32.66) * mm});
            skLineSegment(sketch, "E1917", {"start": v(26.07, -32.66) * mm, "end": v(26.1, -32.57) * mm});
            skLineSegment(sketch, "E1918", {"start": v(26.1, -32.57) * mm, "end": v(26.12, -32.48) * mm});
            skLineSegment(sketch, "E1919", {"start": v(26.12, -32.48) * mm, "end": v(26.14, -32.38) * mm});
            skLineSegment(sketch, "E1920", {"start": v(26.14, -32.38) * mm, "end": v(26.16, -32.29) * mm});
            skLineSegment(sketch, "E1921", {"start": v(26.16, -32.29) * mm, "end": v(26.18, -32.2) * mm});
            skLineSegment(sketch, "E1922", {"start": v(26.18, -32.2) * mm, "end": v(26.2, -32.1) * mm});
            skLineSegment(sketch, "E1923", {"start": v(26.2, -32.1) * mm, "end": v(26.21, -31.99) * mm});
            skLineSegment(sketch, "E1924", {"start": v(26.21, -31.99) * mm, "end": v(26.22, -31.89) * mm});
            skLineSegment(sketch, "E1925", {"start": v(26.22, -31.89) * mm, "end": v(26.23, -31.78) * mm});
            skLineSegment(sketch, "E1926", {"start": v(26.23, -31.78) * mm, "end": v(26.24, -31.67) * mm});
            skLineSegment(sketch, "E1927", {"start": v(26.24, -31.67) * mm, "end": v(26.27, -31.6) * mm});
            skLineSegment(sketch, "E1928", {"start": v(26.27, -31.6) * mm, "end": v(26.28, -31.48) * mm});
            skLineSegment(sketch, "E1929", {"start": v(26.28, -31.48) * mm, "end": v(26.3, -31.41) * mm});
            skLineSegment(sketch, "E1930", {"start": v(26.3, -31.41) * mm, "end": v(26.3, -31.3) * mm});
            skLineSegment(sketch, "E1931", {"start": v(26.3, -31.3) * mm, "end": v(26.33, -31.24) * mm});
            skLineSegment(sketch, "E1932", {"start": v(26.33, -31.24) * mm, "end": v(26.33, -31.13) * mm});
            skLineSegment(sketch, "E1933", {"start": v(26.33, -31.13) * mm, "end": v(26.35, -31.06) * mm});
            skLineSegment(sketch, "E1934", {"start": v(26.35, -31.06) * mm, "end": v(26.37, -30.99) * mm});
            skLineSegment(sketch, "E1935", {"start": v(26.37, -30.99) * mm, "end": v(26.36, -30.88) * mm});
            skLineSegment(sketch, "E1936", {"start": v(26.36, -30.88) * mm, "end": v(26.38, -30.8) * mm});
            skLineSegment(sketch, "E1937", {"start": v(26.38, -30.8) * mm, "end": v(26.37, -30.7) * mm});
            skLineSegment(sketch, "E1938", {"start": v(26.37, -30.7) * mm, "end": v(26.4, -30.63) * mm});
            skLineSegment(sketch, "E1939", {"start": v(26.4, -30.63) * mm, "end": v(26.38, -30.52) * mm});
            skLineSegment(sketch, "E1940", {"start": v(26.38, -30.52) * mm, "end": v(26.4, -30.45) * mm});
            skLineSegment(sketch, "E1941", {"start": v(26.4, -30.45) * mm, "end": v(26.4, -30.38) * mm});
            skLineSegment(sketch, "E1942", {"start": v(26.4, -30.38) * mm, "end": v(26.4, -30.27) * mm});
            skLineSegment(sketch, "E1943", {"start": v(26.4, -30.27) * mm, "end": v(26.4, -30.2) * mm});
            skLineSegment(sketch, "E1944", {"start": v(26.4, -30.2) * mm, "end": v(26.4, -30.1) * mm});
            skLineSegment(sketch, "E1945", {"start": v(26.4, -30.1) * mm, "end": v(26.4, -30.02) * mm});
            skLineSegment(sketch, "E1946", {"start": v(26.4, -30.02) * mm, "end": v(26.38, -29.91) * mm});
            skLineSegment(sketch, "E1947", {"start": v(26.38, -29.91) * mm, "end": v(26.39, -29.85) * mm});
            skLineSegment(sketch, "E1948", {"start": v(26.39, -29.85) * mm, "end": v(26.4, -29.78) * mm});
            skLineSegment(sketch, "E1949", {"start": v(26.4, -29.78) * mm, "end": v(26.37, -29.67) * mm});
            skLineSegment(sketch, "E1950", {"start": v(26.37, -29.67) * mm, "end": v(26.38, -29.6) * mm});
            skLineSegment(sketch, "E1951", {"start": v(26.38, -29.6) * mm, "end": v(26.35, -29.5) * mm});
            skLineSegment(sketch, "E1952", {"start": v(26.35, -29.5) * mm, "end": v(26.35, -29.42) * mm});
            skLineSegment(sketch, "E1953", {"start": v(26.35, -29.42) * mm, "end": v(26.35, -29.36) * mm});
            skLineSegment(sketch, "E1954", {"start": v(26.35, -29.36) * mm, "end": v(26.33, -29.25) * mm});
            skLineSegment(sketch, "E1955", {"start": v(26.33, -29.25) * mm, "end": v(26.33, -29.18) * mm});
            skLineSegment(sketch, "E1956", {"start": v(26.33, -29.18) * mm, "end": v(26.3, -29.07) * mm});
            skLineSegment(sketch, "E1957", {"start": v(26.3, -29.07) * mm, "end": v(26.3, -29) * mm});
            skLineSegment(sketch, "E1958", {"start": v(26.3, -29) * mm, "end": v(26.26, -28.9) * mm});
            skLineSegment(sketch, "E1959", {"start": v(26.26, -28.9) * mm, "end": v(26.26, -28.84) * mm});
            skLineSegment(sketch, "E1960", {"start": v(26.26, -28.84) * mm, "end": v(26.25, -28.77) * mm});
            skLineSegment(sketch, "E1961", {"start": v(26.25, -28.77) * mm, "end": v(26.22, -28.66) * mm});
            skLineSegment(sketch, "E1962", {"start": v(26.22, -28.66) * mm, "end": v(26.2, -28.6) * mm});
            skLineSegment(sketch, "E1963", {"start": v(26.2, -28.6) * mm, "end": v(26.17, -28.5) * mm});
            skLineSegment(sketch, "E1964", {"start": v(26.17, -28.5) * mm, "end": v(26.16, -28.43) * mm});
            skLineSegment(sketch, "E1965", {"start": v(26.16, -28.43) * mm, "end": v(26.12, -28.32) * mm});
            skLineSegment(sketch, "E1966", {"start": v(26.12, -28.32) * mm, "end": v(26.11, -28.26) * mm});
            skLineSegment(sketch, "E1967", {"start": v(26.11, -28.26) * mm, "end": v(26.1, -28.2) * mm});
            skLineSegment(sketch, "E1968", {"start": v(26.1, -28.2) * mm, "end": v(26.06, -28.1) * mm});
            skLineSegment(sketch, "E1969", {"start": v(26.06, -28.1) * mm, "end": v(26.04, -28.03) * mm});
            skLineSegment(sketch, "E1970", {"start": v(26.04, -28.03) * mm, "end": v(26, -27.93) * mm});
            skLineSegment(sketch, "E1971", {"start": v(26, -27.93) * mm, "end": v(25.98, -27.87) * mm});
            skLineSegment(sketch, "E1972", {"start": v(25.98, -27.87) * mm, "end": v(25.93, -27.76) * mm});
            skLineSegment(sketch, "E1973", {"start": v(25.93, -27.76) * mm, "end": v(25.92, -27.7) * mm});
            skLineSegment(sketch, "E1974", {"start": v(25.92, -27.7) * mm, "end": v(25.9, -27.65) * mm});
            skLineSegment(sketch, "E1975", {"start": v(25.9, -27.65) * mm, "end": v(25.85, -27.54) * mm});
            skLineSegment(sketch, "E1976", {"start": v(25.85, -27.54) * mm, "end": v(25.83, -27.49) * mm});
            skLineSegment(sketch, "E1977", {"start": v(25.83, -27.49) * mm, "end": v(25.78, -27.39) * mm});
            skLineSegment(sketch, "E1978", {"start": v(25.78, -27.39) * mm, "end": v(25.76, -27.33) * mm});
            skLineSegment(sketch, "E1979", {"start": v(25.76, -27.33) * mm, "end": v(25.7, -27.23) * mm});
            skLineSegment(sketch, "E1980", {"start": v(25.7, -27.23) * mm, "end": v(25.68, -27.17) * mm});
            skLineSegment(sketch, "E1981", {"start": v(25.68, -27.17) * mm, "end": v(25.66, -27.12) * mm});
            skLineSegment(sketch, "E1982", {"start": v(25.66, -27.12) * mm, "end": v(25.6, -27.02) * mm});
            skLineSegment(sketch, "E1983", {"start": v(25.6, -27.02) * mm, "end": v(25.57, -26.97) * mm});
            skLineSegment(sketch, "E1984", {"start": v(25.57, -26.97) * mm, "end": v(25.51, -26.87) * mm});
            skLineSegment(sketch, "E1985", {"start": v(25.51, -26.87) * mm, "end": v(25.49, -26.82) * mm});
            skLineSegment(sketch, "E1986", {"start": v(25.49, -26.82) * mm, "end": v(25.42, -26.72) * mm});
            skLineSegment(sketch, "E1987", {"start": v(25.42, -26.72) * mm, "end": v(25.4, -26.67) * mm});
            skLineSegment(sketch, "E1988", {"start": v(25.4, -26.67) * mm, "end": v(25.37, -26.62) * mm});
            skLineSegment(sketch, "E1989", {"start": v(25.37, -26.62) * mm, "end": v(25.3, -26.52) * mm});
            skLineSegment(sketch, "E1990", {"start": v(25.3, -26.52) * mm, "end": v(25.27, -26.47) * mm});
            skLineSegment(sketch, "E1991", {"start": v(25.27, -26.47) * mm, "end": v(25.2, -26.38) * mm});
            skLineSegment(sketch, "E1992", {"start": v(25.2, -26.38) * mm, "end": v(25.18, -26.33) * mm});
            skLineSegment(sketch, "E1993", {"start": v(25.18, -26.33) * mm, "end": v(24.87, -25.93) * mm});
            skLineSegment(sketch, "E1994", {"start": v(24.87, -25.93) * mm, "end": v(24.82, -25.86) * mm});
            skLineSegment(sketch, "E1995", {"start": v(24.82, -25.86) * mm, "end": v(24.77, -25.8) * mm});
            skLineSegment(sketch, "E1996", {"start": v(24.77, -25.8) * mm, "end": v(24.71, -25.73) * mm});
            skLineSegment(sketch, "E1997", {"start": v(24.71, -25.73) * mm, "end": v(24.65, -25.67) * mm});
            skLineSegment(sketch, "E1998", {"start": v(24.65, -25.67) * mm, "end": v(24.6, -25.6) * mm});
            skLineSegment(sketch, "E1999", {"start": v(24.6, -25.6) * mm, "end": v(24.55, -25.55) * mm});
            skLineSegment(sketch, "E2000", {"start": v(24.55, -25.55) * mm, "end": v(24.49, -25.5) * mm});
            skLineSegment(sketch, "E2001", {"start": v(24.49, -25.5) * mm, "end": v(24.43, -25.43) * mm});
            skLineSegment(sketch, "E2002", {"start": v(24.43, -25.43) * mm, "end": v(24.37, -25.37) * mm});
            skLineSegment(sketch, "E2003", {"start": v(24.37, -25.37) * mm, "end": v(24.3, -25.31) * mm});
            skLineSegment(sketch, "E2004", {"start": v(24.3, -25.31) * mm, "end": v(24.25, -25.25) * mm});
            skLineSegment(sketch, "E2005", {"start": v(24.25, -25.25) * mm, "end": v(24.18, -25.2) * mm});
            skLineSegment(sketch, "E2006", {"start": v(24.18, -25.2) * mm, "end": v(24.12, -25.14) * mm});
            skLineSegment(sketch, "E2007", {"start": v(24.12, -25.14) * mm, "end": v(24.05, -25.08) * mm});
            skLineSegment(sketch, "E2008", {"start": v(24.05, -25.08) * mm, "end": v(23.99, -25.02) * mm});
            skLineSegment(sketch, "E2009", {"start": v(23.99, -25.02) * mm, "end": v(23.92, -24.97) * mm});
            skLineSegment(sketch, "E2010", {"start": v(23.92, -24.97) * mm, "end": v(23.86, -24.91) * mm});
            skLineSegment(sketch, "E2011", {"start": v(23.86, -24.91) * mm, "end": v(23.79, -24.86) * mm});
            skLineSegment(sketch, "E2012", {"start": v(23.79, -24.86) * mm, "end": v(23.72, -24.8) * mm});
            skLineSegment(sketch, "E2013", {"start": v(23.72, -24.8) * mm, "end": v(23.65, -24.76) * mm});
            skLineSegment(sketch, "E2014", {"start": v(23.65, -24.76) * mm, "end": v(23.58, -24.7) * mm});
            skLineSegment(sketch, "E2015", {"start": v(23.58, -24.7) * mm, "end": v(23.51, -24.66) * mm});
            skLineSegment(sketch, "E2016", {"start": v(23.51, -24.66) * mm, "end": v(23.44, -24.6) * mm});
            skLineSegment(sketch, "E2017", {"start": v(23.44, -24.6) * mm, "end": v(23.37, -24.56) * mm});
            skLineSegment(sketch, "E2018", {"start": v(23.37, -24.56) * mm, "end": v(23.3, -24.51) * mm});
            skLineSegment(sketch, "E2019", {"start": v(23.3, -24.51) * mm, "end": v(23.23, -24.47) * mm});
            skLineSegment(sketch, "E2020", {"start": v(23.23, -24.47) * mm, "end": v(23.16, -24.42) * mm});
            skLineSegment(sketch, "E2021", {"start": v(23.16, -24.42) * mm, "end": v(23.08, -24.37) * mm});
            skLineSegment(sketch, "E2022", {"start": v(23.08, -24.37) * mm, "end": v(23, -24.33) * mm});
            skLineSegment(sketch, "E2023", {"start": v(23, -24.33) * mm, "end": v(22.94, -24.29) * mm});
            skLineSegment(sketch, "E2024", {"start": v(22.94, -24.29) * mm, "end": v(22.86, -24.24) * mm});
            skLineSegment(sketch, "E2025", {"start": v(22.86, -24.24) * mm, "end": v(22.78, -24.2) * mm});
            skLineSegment(sketch, "E2026", {"start": v(22.78, -24.2) * mm, "end": v(22.7, -24.16) * mm});
            skLineSegment(sketch, "E2027", {"start": v(22.7, -24.16) * mm, "end": v(22.63, -24.13) * mm});
            skLineSegment(sketch, "E2028", {"start": v(22.63, -24.13) * mm, "end": v(22.55, -24.09) * mm});
            skLineSegment(sketch, "E2029", {"start": v(22.55, -24.09) * mm, "end": v(22.48, -24.05) * mm});
            skLineSegment(sketch, "E2030", {"start": v(22.48, -24.05) * mm, "end": v(22.42, -24.02) * mm});
            skLineSegment(sketch, "E2031", {"start": v(22.42, -24.02) * mm, "end": v(22.34, -23.98) * mm});
            skLineSegment(sketch, "E2032", {"start": v(22.34, -23.98) * mm, "end": v(22.26, -23.95) * mm});
            skLineSegment(sketch, "E2033", {"start": v(22.26, -23.95) * mm, "end": v(22.18, -23.92) * mm});
            skLineSegment(sketch, "E2034", {"start": v(22.18, -23.92) * mm, "end": v(22.08, -23.88) * mm});
            skLineSegment(sketch, "E2035", {"start": v(22.08, -23.88) * mm, "end": v(22.03, -23.86) * mm});
            skLineSegment(sketch, "E2036", {"start": v(22.03, -23.86) * mm, "end": v(21.92, -23.81) * mm});
            skLineSegment(sketch, "E2037", {"start": v(21.92, -23.81) * mm, "end": v(21.87, -23.8) * mm});
            skLineSegment(sketch, "E2038", {"start": v(21.87, -23.8) * mm, "end": v(21.76, -23.75) * mm});
            skLineSegment(sketch, "E2039", {"start": v(21.76, -23.75) * mm, "end": v(21.7, -23.74) * mm});
            skLineSegment(sketch, "E2040", {"start": v(21.7, -23.74) * mm, "end": v(21.6, -23.7) * mm});
            skLineSegment(sketch, "E2041", {"start": v(21.6, -23.7) * mm, "end": v(21.54, -23.68) * mm});
            skLineSegment(sketch, "E2042", {"start": v(21.54, -23.68) * mm, "end": v(21.43, -23.65) * mm});
            skLineSegment(sketch, "E2043", {"start": v(21.43, -23.65) * mm, "end": v(21.38, -23.64) * mm});
            skLineSegment(sketch, "E2044", {"start": v(21.38, -23.64) * mm, "end": v(21.27, -23.6) * mm});
            skLineSegment(sketch, "E2045", {"start": v(21.27, -23.6) * mm, "end": v(21.21, -23.6) * mm});
            skLineSegment(sketch, "E2046", {"start": v(21.21, -23.6) * mm, "end": v(21.1, -23.56) * mm});
            skLineSegment(sketch, "E2047", {"start": v(21.1, -23.56) * mm, "end": v(21.05, -23.55) * mm});
            skLineSegment(sketch, "E2048", {"start": v(21.05, -23.55) * mm, "end": v(20.93, -23.52) * mm});
            skLineSegment(sketch, "E2049", {"start": v(20.93, -23.52) * mm, "end": v(20.88, -23.51) * mm});
            skLineSegment(sketch, "E2050", {"start": v(20.88, -23.51) * mm, "end": v(20.77, -23.5) * mm});
            skLineSegment(sketch, "E2051", {"start": v(20.77, -23.5) * mm, "end": v(20.7, -23.48) * mm});
            skLineSegment(sketch, "E2052", {"start": v(20.7, -23.48) * mm, "end": v(20.6, -23.46) * mm});
            skLineSegment(sketch, "E2053", {"start": v(20.6, -23.46) * mm, "end": v(20.54, -23.45) * mm});
            skLineSegment(sketch, "E2054", {"start": v(20.54, -23.45) * mm, "end": v(20.43, -23.43) * mm});
            skLineSegment(sketch, "E2055", {"start": v(20.43, -23.43) * mm, "end": v(20.37, -23.43) * mm});
            skLineSegment(sketch, "E2056", {"start": v(20.37, -23.43) * mm, "end": v(20.26, -23.41) * mm});
            skLineSegment(sketch, "E2057", {"start": v(20.26, -23.41) * mm, "end": v(20.2, -23.4) * mm});
            skLineSegment(sketch, "E2058", {"start": v(20.2, -23.4) * mm, "end": v(20.09, -23.4) * mm});
            skLineSegment(sketch, "E2059", {"start": v(20.09, -23.4) * mm, "end": v(20.02, -23.4) * mm});
            skLineSegment(sketch, "E2060", {"start": v(20.02, -23.4) * mm, "end": v(19.91, -23.38) * mm});
            skLineSegment(sketch, "E2061", {"start": v(19.91, -23.38) * mm, "end": v(19.85, -23.38) * mm});
            skLineSegment(sketch, "E2062", {"start": v(19.85, -23.38) * mm, "end": v(19.74, -23.37) * mm});
            skLineSegment(sketch, "E2063", {"start": v(19.74, -23.37) * mm, "end": v(19.68, -23.37) * mm});
            skLineSegment(sketch, "E2064", {"start": v(19.68, -23.37) * mm, "end": v(19.57, -23.37) * mm});
            skLineSegment(sketch, "E2065", {"start": v(19.57, -23.37) * mm, "end": v(19.5, -23.37) * mm});
            skLineSegment(sketch, "E2066", {"start": v(19.5, -23.37) * mm, "end": v(19.4, -23.37) * mm});
            skLineSegment(sketch, "E2067", {"start": v(19.4, -23.37) * mm, "end": v(19.34, -23.37) * mm});
            skLineSegment(sketch, "E2068", {"start": v(19.34, -23.37) * mm, "end": v(19.23, -23.37) * mm});
            skLineSegment(sketch, "E2069", {"start": v(19.23, -23.37) * mm, "end": v(19.16, -23.38) * mm});
            skLineSegment(sketch, "E2070", {"start": v(19.16, -23.38) * mm, "end": v(19.06, -23.38) * mm});
            skLineSegment(sketch, "E2071", {"start": v(19.06, -23.38) * mm, "end": v(19, -23.39) * mm});
            skLineSegment(sketch, "E2072", {"start": v(19, -23.39) * mm, "end": v(18.88, -23.4) * mm});
            skLineSegment(sketch, "E2073", {"start": v(18.88, -23.4) * mm, "end": v(18.82, -23.4) * mm});
            skLineSegment(sketch, "E2074", {"start": v(18.82, -23.4) * mm, "end": v(18.71, -23.4) * mm});
            skLineSegment(sketch, "E2075", {"start": v(18.71, -23.4) * mm, "end": v(18.65, -23.42) * mm});
            skLineSegment(sketch, "E2076", {"start": v(18.65, -23.42) * mm, "end": v(18.54, -23.43) * mm});
            skLineSegment(sketch, "E2077", {"start": v(18.54, -23.43) * mm, "end": v(18.48, -23.44) * mm});
            skLineSegment(sketch, "E2078", {"start": v(18.48, -23.44) * mm, "end": v(18.37, -23.45) * mm});
            skLineSegment(sketch, "E2079", {"start": v(18.37, -23.45) * mm, "end": v(18.3, -23.47) * mm});
            skLineSegment(sketch, "E2080", {"start": v(18.3, -23.47) * mm, "end": v(18.2, -23.48) * mm});
            skLineSegment(sketch, "E2081", {"start": v(18.2, -23.48) * mm, "end": v(18.14, -23.5) * mm});
            skLineSegment(sketch, "E2082", {"start": v(18.14, -23.5) * mm, "end": v(18.04, -23.52) * mm});
            skLineSegment(sketch, "E2083", {"start": v(18.04, -23.52) * mm, "end": v(17.97, -23.53) * mm});
            skLineSegment(sketch, "E2084", {"start": v(17.97, -23.53) * mm, "end": v(17.87, -23.55) * mm});
            skLineSegment(sketch, "E2085", {"start": v(17.87, -23.55) * mm, "end": v(17.8, -23.57) * mm});
            skLineSegment(sketch, "E2086", {"start": v(17.8, -23.57) * mm, "end": v(17.7, -23.6) * mm});
            skLineSegment(sketch, "E2087", {"start": v(17.7, -23.6) * mm, "end": v(17.63, -23.61) * mm});
            skLineSegment(sketch, "E2088", {"start": v(17.63, -23.61) * mm, "end": v(17.54, -23.64) * mm});
            skLineSegment(sketch, "E2089", {"start": v(17.54, -23.64) * mm, "end": v(17.47, -23.66) * mm});
            skLineSegment(sketch, "E2090", {"start": v(17.47, -23.66) * mm, "end": v(17.37, -23.7) * mm});
            skLineSegment(sketch, "E2091", {"start": v(17.37, -23.7) * mm, "end": v(17.3, -23.71) * mm});
            skLineSegment(sketch, "E2092", {"start": v(17.3, -23.71) * mm, "end": v(17.2, -23.74) * mm});
            skLineSegment(sketch, "E2093", {"start": v(17.2, -23.74) * mm, "end": v(17.14, -23.77) * mm});
            skLineSegment(sketch, "E2094", {"start": v(17.14, -23.77) * mm, "end": v(17.05, -23.8) * mm});
            skLineSegment(sketch, "E2095", {"start": v(17.05, -23.8) * mm, "end": v(16.98, -23.83) * mm});
            skLineSegment(sketch, "E2096", {"start": v(16.98, -23.83) * mm, "end": v(16.89, -23.86) * mm});
            skLineSegment(sketch, "E2097", {"start": v(16.89, -23.86) * mm, "end": v(16.82, -23.9) * mm});
            skLineSegment(sketch, "E2098", {"start": v(16.82, -23.9) * mm, "end": v(16.73, -23.93) * mm});
            skLineSegment(sketch, "E2099", {"start": v(16.73, -23.93) * mm, "end": v(16.66, -23.96) * mm});
            skLineSegment(sketch, "E2100", {"start": v(16.66, -23.96) * mm, "end": v(16.57, -24) * mm});
            skLineSegment(sketch, "E2101", {"start": v(16.57, -24) * mm, "end": v(16.5, -24.03) * mm});
            skLineSegment(sketch, "E2102", {"start": v(16.5, -24.03) * mm, "end": v(16.41, -24.07) * mm});
            skLineSegment(sketch, "E2103", {"start": v(16.41, -24.07) * mm, "end": v(16.34, -24.1) * mm});
            skLineSegment(sketch, "E2104", {"start": v(16.34, -24.1) * mm, "end": v(16.26, -24.15) * mm});
            skLineSegment(sketch, "E2105", {"start": v(16.26, -24.15) * mm, "end": v(16.2, -24.18) * mm});
            skLineSegment(sketch, "E2106", {"start": v(16.2, -24.18) * mm, "end": v(16.1, -24.23) * mm});
            skLineSegment(sketch, "E2107", {"start": v(16.1, -24.23) * mm, "end": v(16.04, -24.27) * mm});
            skLineSegment(sketch, "E2108", {"start": v(16.04, -24.27) * mm, "end": v(15.96, -24.31) * mm});
            skLineSegment(sketch, "E2109", {"start": v(15.96, -24.31) * mm, "end": v(15.89, -24.35) * mm});
            skLineSegment(sketch, "E2110", {"start": v(15.89, -24.35) * mm, "end": v(15.81, -24.4) * mm});
            skLineSegment(sketch, "E2111", {"start": v(15.81, -24.4) * mm, "end": v(15.74, -24.44) * mm});
            skLineSegment(sketch, "E2112", {"start": v(15.74, -24.44) * mm, "end": v(15.67, -24.5) * mm});
            skLineSegment(sketch, "E2113", {"start": v(15.67, -24.5) * mm, "end": v(15.6, -24.54) * mm});
            skLineSegment(sketch, "E2114", {"start": v(15.6, -24.54) * mm, "end": v(15.52, -24.59) * mm});
            skLineSegment(sketch, "E2115", {"start": v(15.52, -24.59) * mm, "end": v(15.46, -24.63) * mm});
            skLineSegment(sketch, "E2116", {"start": v(15.46, -24.63) * mm, "end": v(15.38, -24.69) * mm});
            skLineSegment(sketch, "E2117", {"start": v(15.38, -24.69) * mm, "end": v(15.31, -24.73) * mm});
            skLineSegment(sketch, "E2118", {"start": v(15.31, -24.73) * mm, "end": v(15.24, -24.79) * mm});
            skLineSegment(sketch, "E2119", {"start": v(15.24, -24.79) * mm, "end": v(15.18, -24.84) * mm});
            skLineSegment(sketch, "E2120", {"start": v(15.18, -24.84) * mm, "end": v(15.1, -24.9) * mm});
            skLineSegment(sketch, "E2121", {"start": v(15.1, -24.9) * mm, "end": v(15.04, -24.95) * mm});
            skLineSegment(sketch, "E2122", {"start": v(15.04, -24.95) * mm, "end": v(14.98, -25) * mm});
            skLineSegment(sketch, "E2123", {"start": v(14.98, -25) * mm, "end": v(14.96, -25.01) * mm});
            skLineSegment(sketch, "E2124", {"start": v(14.96, -25.01) * mm, "end": v(14.95, -25.02) * mm});
            skLineSegment(sketch, "E2125", {"start": v(14.95, -25.02) * mm, "end": v(14.82, -24.89) * mm});
            skLineSegment(sketch, "E2126", {"start": v(14.82, -24.89) * mm, "end": v(14.7, -24.75) * mm});
            skLineSegment(sketch, "E2127", {"start": v(14.7, -24.75) * mm, "end": v(14.6, -24.63) * mm});
            skLineSegment(sketch, "E2128", {"start": v(13.77, -26.63) * mm, "end": v(13.91, -26.8) * mm});
            skLineSegment(sketch, "E2129", {"start": v(13.91, -26.8) * mm, "end": v(14.08, -26.98) * mm});
            skLineSegment(sketch, "E2130", {"start": v(14.08, -26.98) * mm, "end": v(14.15, -27.06) * mm});
            skLineSegment(sketch, "E2131", {"start": v(14.15, -27.06) * mm, "end": v(14.22, -27.13) * mm});
            skLineSegment(sketch, "E2132", {"start": v(14.22, -27.13) * mm, "end": v(14.78, -27.72) * mm});
            skLineSegment(sketch, "E2133", {"start": v(14.78, -27.72) * mm, "end": v(15.07, -28) * mm});
            skLineSegment(sketch, "E2134", {"start": v(15.07, -28) * mm, "end": v(15.11, -27.91) * mm});
            skLineSegment(sketch, "E2135", {"start": v(15.11, -27.91) * mm, "end": v(15.15, -27.86) * mm});
            skLineSegment(sketch, "E2136", {"start": v(15.15, -27.86) * mm, "end": v(15.19, -27.8) * mm});
            skLineSegment(sketch, "E2137", {"start": v(15.19, -27.8) * mm, "end": v(15.22, -27.74) * mm});
            skLineSegment(sketch, "E2138", {"start": v(15.22, -27.74) * mm, "end": v(15.26, -27.68) * mm});
            skLineSegment(sketch, "E2139", {"start": v(15.26, -27.68) * mm, "end": v(15.3, -27.63) * mm});
            skLineSegment(sketch, "E2140", {"start": v(15.3, -27.63) * mm, "end": v(15.35, -27.57) * mm});
            skLineSegment(sketch, "E2141", {"start": v(15.35, -27.57) * mm, "end": v(15.4, -27.51) * mm});
            skLineSegment(sketch, "E2142", {"start": v(15.4, -27.51) * mm, "end": v(15.44, -27.46) * mm});
            skLineSegment(sketch, "E2143", {"start": v(15.44, -27.46) * mm, "end": v(15.5, -27.4) * mm});
            skLineSegment(sketch, "E2144", {"start": v(15.5, -27.4) * mm, "end": v(15.55, -27.35) * mm});
            skLineSegment(sketch, "E2145", {"start": v(15.55, -27.35) * mm, "end": v(15.6, -27.3) * mm});
            skLineSegment(sketch, "E2146", {"start": v(15.6, -27.3) * mm, "end": v(15.66, -27.24) * mm});
            skLineSegment(sketch, "E2147", {"start": v(15.66, -27.24) * mm, "end": v(15.71, -27.18) * mm});
            skLineSegment(sketch, "E2148", {"start": v(15.71, -27.18) * mm, "end": v(15.77, -27.13) * mm});
            skLineSegment(sketch, "E2149", {"start": v(15.77, -27.13) * mm, "end": v(15.84, -27.08) * mm});
            skLineSegment(sketch, "E2150", {"start": v(15.84, -27.08) * mm, "end": v(15.9, -27.03) * mm});
            skLineSegment(sketch, "E2151", {"start": v(15.9, -27.03) * mm, "end": v(15.96, -26.98) * mm});
            skLineSegment(sketch, "E2152", {"start": v(15.96, -26.98) * mm, "end": v(16.03, -26.93) * mm});
            skLineSegment(sketch, "E2153", {"start": v(16.03, -26.93) * mm, "end": v(16.1, -26.88) * mm});
            skLineSegment(sketch, "E2154", {"start": v(16.1, -26.88) * mm, "end": v(16.17, -26.83) * mm});
            skLineSegment(sketch, "E2155", {"start": v(16.17, -26.83) * mm, "end": v(16.2, -26.77) * mm});
            skLineSegment(sketch, "E2156", {"start": v(16.2, -26.77) * mm, "end": v(16.28, -26.72) * mm});
            skLineSegment(sketch, "E2157", {"start": v(16.28, -26.72) * mm, "end": v(16.3, -26.68) * mm});
            skLineSegment(sketch, "E2158", {"start": v(16.3, -26.68) * mm, "end": v(16.38, -26.64) * mm});
            skLineSegment(sketch, "E2159", {"start": v(16.38, -26.64) * mm, "end": v(16.4, -26.6) * mm});
            skLineSegment(sketch, "E2160", {"start": v(16.4, -26.6) * mm, "end": v(16.48, -26.55) * mm});
            skLineSegment(sketch, "E2161", {"start": v(16.48, -26.55) * mm, "end": v(16.5, -26.51) * mm});
            skLineSegment(sketch, "E2162", {"start": v(16.5, -26.51) * mm, "end": v(16.58, -26.47) * mm});
            skLineSegment(sketch, "E2163", {"start": v(16.58, -26.47) * mm, "end": v(16.6, -26.44) * mm});
            skLineSegment(sketch, "E2164", {"start": v(16.6, -26.44) * mm, "end": v(16.63, -26.4) * mm});
            skLineSegment(sketch, "E2165", {"start": v(16.63, -26.4) * mm, "end": v(16.71, -26.36) * mm});
            skLineSegment(sketch, "E2166", {"start": v(16.71, -26.36) * mm, "end": v(16.74, -26.33) * mm});
            skLineSegment(sketch, "E2167", {"start": v(16.74, -26.33) * mm, "end": v(16.82, -26.29) * mm});
            skLineSegment(sketch, "E2168", {"start": v(16.82, -26.29) * mm, "end": v(16.85, -26.26) * mm});
            skLineSegment(sketch, "E2169", {"start": v(16.85, -26.26) * mm, "end": v(16.88, -26.22) * mm});
            skLineSegment(sketch, "E2170", {"start": v(16.88, -26.22) * mm, "end": v(16.96, -26.19) * mm});
            skLineSegment(sketch, "E2171", {"start": v(16.96, -26.19) * mm, "end": v(16.99, -26.16) * mm});
            skLineSegment(sketch, "E2172", {"start": v(16.99, -26.16) * mm, "end": v(17.02, -26.12) * mm});
            skLineSegment(sketch, "E2173", {"start": v(17.02, -26.12) * mm, "end": v(17.1, -26.1) * mm});
            skLineSegment(sketch, "E2174", {"start": v(17.1, -26.1) * mm, "end": v(17.13, -26.06) * mm});
            skLineSegment(sketch, "E2175", {"start": v(17.13, -26.06) * mm, "end": v(17.21, -26.03) * mm});
            skLineSegment(sketch, "E2176", {"start": v(17.21, -26.03) * mm, "end": v(17.25, -26) * mm});
            skLineSegment(sketch, "E2177", {"start": v(17.25, -26) * mm, "end": v(17.33, -25.97) * mm});
            skLineSegment(sketch, "E2178", {"start": v(17.33, -25.97) * mm, "end": v(17.36, -25.94) * mm});
            skLineSegment(sketch, "E2179", {"start": v(17.36, -25.94) * mm, "end": v(17.4, -25.91) * mm});
            skLineSegment(sketch, "E2180", {"start": v(17.4, -25.91) * mm, "end": v(17.48, -25.89) * mm});
            skLineSegment(sketch, "E2181", {"start": v(17.48, -25.89) * mm, "end": v(17.5, -25.86) * mm});
            skLineSegment(sketch, "E2182", {"start": v(17.5, -25.86) * mm, "end": v(17.6, -25.84) * mm});
            skLineSegment(sketch, "E2183", {"start": v(17.6, -25.84) * mm, "end": v(17.63, -25.81) * mm});
            skLineSegment(sketch, "E2184", {"start": v(17.63, -25.81) * mm, "end": v(17.66, -25.79) * mm});
            skLineSegment(sketch, "E2185", {"start": v(17.66, -25.79) * mm, "end": v(17.75, -25.76) * mm});
            skLineSegment(sketch, "E2186", {"start": v(17.75, -25.76) * mm, "end": v(17.78, -25.74) * mm});
            skLineSegment(sketch, "E2187", {"start": v(17.78, -25.74) * mm, "end": v(17.87, -25.72) * mm});
            skLineSegment(sketch, "E2188", {"start": v(17.87, -25.72) * mm, "end": v(17.9, -25.7) * mm});
            skLineSegment(sketch, "E2189", {"start": v(17.9, -25.7) * mm, "end": v(17.94, -25.68) * mm});
            skLineSegment(sketch, "E2190", {"start": v(17.94, -25.68) * mm, "end": v(18.02, -25.66) * mm});
            skLineSegment(sketch, "E2191", {"start": v(18.02, -25.66) * mm, "end": v(18.06, -25.64) * mm});
            skLineSegment(sketch, "E2192", {"start": v(18.06, -25.64) * mm, "end": v(18.15, -25.62) * mm});
            skLineSegment(sketch, "E2193", {"start": v(18.15, -25.62) * mm, "end": v(18.18, -25.6) * mm});
            skLineSegment(sketch, "E2194", {"start": v(18.18, -25.6) * mm, "end": v(18.22, -25.58) * mm});
            skLineSegment(sketch, "E2195", {"start": v(18.22, -25.58) * mm, "end": v(18.3, -25.57) * mm});
            skLineSegment(sketch, "E2196", {"start": v(18.3, -25.57) * mm, "end": v(18.34, -25.55) * mm});
            skLineSegment(sketch, "E2197", {"start": v(18.34, -25.55) * mm, "end": v(18.43, -25.54) * mm});
            skLineSegment(sketch, "E2198", {"start": v(18.43, -25.54) * mm, "end": v(18.46, -25.53) * mm});
            skLineSegment(sketch, "E2199", {"start": v(18.46, -25.53) * mm, "end": v(18.5, -25.51) * mm});
            skLineSegment(sketch, "E2200", {"start": v(18.5, -25.51) * mm, "end": v(18.59, -25.5) * mm});
            skLineSegment(sketch, "E2201", {"start": v(18.59, -25.5) * mm, "end": v(18.62, -25.49) * mm});
            skLineSegment(sketch, "E2202", {"start": v(18.62, -25.49) * mm, "end": v(18.72, -25.48) * mm});
            skLineSegment(sketch, "E2203", {"start": v(18.72, -25.48) * mm, "end": v(18.75, -25.47) * mm});
            skLineSegment(sketch, "E2204", {"start": v(18.75, -25.47) * mm, "end": v(18.84, -25.46) * mm});
            skLineSegment(sketch, "E2205", {"start": v(18.84, -25.46) * mm, "end": v(18.88, -25.45) * mm});
            skLineSegment(sketch, "E2206", {"start": v(18.88, -25.45) * mm, "end": v(18.9, -25.44) * mm});
            skLineSegment(sketch, "E2207", {"start": v(18.9, -25.44) * mm, "end": v(18.94, -25.43) * mm});
            skLineSegment(sketch, "E2208", {"start": v(18.94, -25.43) * mm, "end": v(18.98, -25.42) * mm});
            skLineSegment(sketch, "E2209", {"start": v(18.98, -25.42) * mm, "end": v(19.01, -25.4) * mm});
            skLineSegment(sketch, "E2210", {"start": v(19.01, -25.4) * mm, "end": v(19.05, -25.4) * mm});
            skLineSegment(sketch, "E2211", {"start": v(19.05, -25.4) * mm, "end": v(19.35, -25.37) * mm});
            skLineSegment(sketch, "E2212", {"start": v(19.35, -25.37) * mm, "end": v(19.42, -25.37) * mm});
            skLineSegment(sketch, "E2213", {"start": v(19.42, -25.37) * mm, "end": v(19.49, -25.37) * mm});
            skLineSegment(sketch, "E2214", {"start": v(19.49, -25.37) * mm, "end": v(19.55, -25.37) * mm});
            skLineSegment(sketch, "E2215", {"start": v(19.55, -25.37) * mm, "end": v(19.62, -25.37) * mm});
            skLineSegment(sketch, "E2216", {"start": v(19.62, -25.37) * mm, "end": v(19.7, -25.38) * mm});
            skLineSegment(sketch, "E2217", {"start": v(19.7, -25.38) * mm, "end": v(19.76, -25.39) * mm});
            skLineSegment(sketch, "E2218", {"start": v(19.76, -25.39) * mm, "end": v(19.83, -25.4) * mm});
            skLineSegment(sketch, "E2219", {"start": v(19.83, -25.4) * mm, "end": v(19.9, -25.4) * mm});
            skLineSegment(sketch, "E2220", {"start": v(19.9, -25.4) * mm, "end": v(19.96, -25.4) * mm});
            skLineSegment(sketch, "E2221", {"start": v(19.96, -25.4) * mm, "end": v(20.01, -25.4) * mm});
            skLineSegment(sketch, "E2222", {"start": v(20.01, -25.4) * mm, "end": v(20.07, -25.41) * mm});
            skLineSegment(sketch, "E2223", {"start": v(20.07, -25.41) * mm, "end": v(20.14, -25.42) * mm});
            skLineSegment(sketch, "E2224", {"start": v(20.14, -25.42) * mm, "end": v(20.19, -25.43) * mm});
            skLineSegment(sketch, "E2225", {"start": v(20.19, -25.43) * mm, "end": v(20.26, -25.44) * mm});
            skLineSegment(sketch, "E2226", {"start": v(20.26, -25.44) * mm, "end": v(20.31, -25.45) * mm});
            skLineSegment(sketch, "E2227", {"start": v(20.31, -25.45) * mm, "end": v(20.38, -25.46) * mm});
            skLineSegment(sketch, "E2228", {"start": v(20.38, -25.46) * mm, "end": v(20.43, -25.47) * mm});
            skLineSegment(sketch, "E2229", {"start": v(20.43, -25.47) * mm, "end": v(20.5, -25.49) * mm});
            skLineSegment(sketch, "E2230", {"start": v(20.5, -25.49) * mm, "end": v(20.56, -25.5) * mm});
            skLineSegment(sketch, "E2231", {"start": v(20.56, -25.5) * mm, "end": v(20.6, -25.5) * mm});
            skLineSegment(sketch, "E2232", {"start": v(20.6, -25.5) * mm, "end": v(20.68, -25.52) * mm});
            skLineSegment(sketch, "E2233", {"start": v(20.68, -25.52) * mm, "end": v(20.73, -25.53) * mm});
            skLineSegment(sketch, "E2234", {"start": v(20.73, -25.53) * mm, "end": v(20.8, -25.55) * mm});
            skLineSegment(sketch, "E2235", {"start": v(20.8, -25.55) * mm, "end": v(20.85, -25.57) * mm});
            skLineSegment(sketch, "E2236", {"start": v(20.85, -25.57) * mm, "end": v(20.92, -25.59) * mm});
            skLineSegment(sketch, "E2237", {"start": v(20.92, -25.59) * mm, "end": v(20.96, -25.6) * mm});
            skLineSegment(sketch, "E2238", {"start": v(20.96, -25.6) * mm, "end": v(21.03, -25.63) * mm});
            skLineSegment(sketch, "E2239", {"start": v(21.03, -25.63) * mm, "end": v(21.08, -25.64) * mm});
            skLineSegment(sketch, "E2240", {"start": v(21.08, -25.64) * mm, "end": v(21.13, -25.65) * mm});
            skLineSegment(sketch, "E2241", {"start": v(21.13, -25.65) * mm, "end": v(21.2, -25.68) * mm});
            skLineSegment(sketch, "E2242", {"start": v(21.2, -25.68) * mm, "end": v(21.25, -25.7) * mm});
            skLineSegment(sketch, "E2243", {"start": v(21.25, -25.7) * mm, "end": v(21.31, -25.72) * mm});
            skLineSegment(sketch, "E2244", {"start": v(21.31, -25.72) * mm, "end": v(21.36, -25.74) * mm});
            skLineSegment(sketch, "E2245", {"start": v(21.36, -25.74) * mm, "end": v(21.43, -25.77) * mm});
            skLineSegment(sketch, "E2246", {"start": v(21.43, -25.77) * mm, "end": v(21.47, -25.79) * mm});
            skLineSegment(sketch, "E2247", {"start": v(21.47, -25.79) * mm, "end": v(21.52, -25.8) * mm});
            skLineSegment(sketch, "E2248", {"start": v(21.52, -25.8) * mm, "end": v(21.59, -25.84) * mm});
            skLineSegment(sketch, "E2249", {"start": v(21.59, -25.84) * mm, "end": v(21.63, -25.86) * mm});
            skLineSegment(sketch, "E2250", {"start": v(21.63, -25.86) * mm, "end": v(21.7, -25.9) * mm});
            skLineSegment(sketch, "E2251", {"start": v(21.7, -25.9) * mm, "end": v(21.74, -25.91) * mm});
            skLineSegment(sketch, "E2252", {"start": v(21.74, -25.91) * mm, "end": v(21.8, -25.95) * mm});
            skLineSegment(sketch, "E2253", {"start": v(21.8, -25.95) * mm, "end": v(21.85, -25.97) * mm});
            skLineSegment(sketch, "E2254", {"start": v(21.85, -25.97) * mm, "end": v(21.91, -26) * mm});
            skLineSegment(sketch, "E2255", {"start": v(21.91, -26) * mm, "end": v(21.96, -26.03) * mm});
            skLineSegment(sketch, "E2256", {"start": v(21.96, -26.03) * mm, "end": v(22.02, -26.07) * mm});
            skLineSegment(sketch, "E2257", {"start": v(22.02, -26.07) * mm, "end": v(22.06, -26.1) * mm});
            skLineSegment(sketch, "E2258", {"start": v(22.06, -26.1) * mm, "end": v(22.1, -26.12) * mm});
            skLineSegment(sketch, "E2259", {"start": v(22.1, -26.12) * mm, "end": v(22.17, -26.16) * mm});
            skLineSegment(sketch, "E2260", {"start": v(22.17, -26.16) * mm, "end": v(22.2, -26.18) * mm});
            skLineSegment(sketch, "E2261", {"start": v(22.2, -26.18) * mm, "end": v(22.27, -26.22) * mm});
            skLineSegment(sketch, "E2262", {"start": v(22.27, -26.22) * mm, "end": v(22.3, -26.25) * mm});
            skLineSegment(sketch, "E2263", {"start": v(22.3, -26.25) * mm, "end": v(22.37, -26.3) * mm});
            skLineSegment(sketch, "E2264", {"start": v(22.37, -26.3) * mm, "end": v(22.4, -26.32) * mm});
            skLineSegment(sketch, "E2265", {"start": v(22.4, -26.32) * mm, "end": v(22.45, -26.35) * mm});
            skLineSegment(sketch, "E2266", {"start": v(22.45, -26.35) * mm, "end": v(22.5, -26.4) * mm});
            skLineSegment(sketch, "E2267", {"start": v(22.5, -26.4) * mm, "end": v(22.54, -26.43) * mm});
            skLineSegment(sketch, "E2268", {"start": v(22.54, -26.43) * mm, "end": v(22.6, -26.47) * mm});
            skLineSegment(sketch, "E2269", {"start": v(22.6, -26.47) * mm, "end": v(22.64, -26.5) * mm});
            skLineSegment(sketch, "E2270", {"start": v(22.64, -26.5) * mm, "end": v(22.7, -26.55) * mm});
            skLineSegment(sketch, "E2271", {"start": v(22.7, -26.55) * mm, "end": v(22.73, -26.58) * mm});
            skLineSegment(sketch, "E2272", {"start": v(22.73, -26.58) * mm, "end": v(22.8, -26.63) * mm});
            skLineSegment(sketch, "E2273", {"start": v(22.8, -26.63) * mm, "end": v(22.83, -26.66) * mm});
            skLineSegment(sketch, "E2274", {"start": v(22.83, -26.66) * mm, "end": v(22.88, -26.71) * mm});
            skLineSegment(sketch, "E2275", {"start": v(22.88, -26.71) * mm, "end": v(22.92, -26.75) * mm});
            skLineSegment(sketch, "E2276", {"start": v(22.92, -26.75) * mm, "end": v(22.97, -26.8) * mm});
            skLineSegment(sketch, "E2277", {"start": v(22.97, -26.8) * mm, "end": v(23, -26.83) * mm});
            skLineSegment(sketch, "E2278", {"start": v(23, -26.83) * mm, "end": v(23.06, -26.89) * mm});
            skLineSegment(sketch, "E2279", {"start": v(23.06, -26.89) * mm, "end": v(23.09, -26.92) * mm});
            skLineSegment(sketch, "E2280", {"start": v(23.09, -26.92) * mm, "end": v(23.14, -26.98) * mm});
            skLineSegment(sketch, "E2281", {"start": v(23.14, -26.98) * mm, "end": v(23.17, -27.01) * mm});
            skLineSegment(sketch, "E2282", {"start": v(23.17, -27.01) * mm, "end": v(23.22, -27.07) * mm});
            skLineSegment(sketch, "E2283", {"start": v(23.22, -27.07) * mm, "end": v(23.25, -27.1) * mm});
            skLineSegment(sketch, "E2284", {"start": v(23.25, -27.1) * mm, "end": v(23.3, -27.16) * mm});
            skLineSegment(sketch, "E2285", {"start": v(23.3, -27.16) * mm, "end": v(23.33, -27.2) * mm});
            skLineSegment(sketch, "E2286", {"start": v(23.33, -27.2) * mm, "end": v(23.38, -27.25) * mm});
            skLineSegment(sketch, "E2287", {"start": v(23.38, -27.25) * mm, "end": v(23.41, -27.3) * mm});
            skLineSegment(sketch, "E2288", {"start": v(23.41, -27.3) * mm, "end": v(23.46, -27.35) * mm});
            skLineSegment(sketch, "E2289", {"start": v(23.46, -27.35) * mm, "end": v(23.49, -27.4) * mm});
            skLineSegment(sketch, "E2290", {"start": v(23.49, -27.4) * mm, "end": v(23.53, -27.45) * mm});
            skLineSegment(sketch, "E2291", {"start": v(23.53, -27.45) * mm, "end": v(23.56, -27.5) * mm});
            skLineSegment(sketch, "E2292", {"start": v(23.56, -27.5) * mm, "end": v(23.6, -27.55) * mm});
            skLineSegment(sketch, "E2293", {"start": v(23.6, -27.55) * mm, "end": v(23.63, -27.6) * mm});
            skLineSegment(sketch, "E2294", {"start": v(23.63, -27.6) * mm, "end": v(23.67, -27.65) * mm});
            skLineSegment(sketch, "E2295", {"start": v(23.67, -27.65) * mm, "end": v(23.7, -27.7) * mm});
            skLineSegment(sketch, "E2296", {"start": v(23.7, -27.7) * mm, "end": v(23.73, -27.76) * mm});
            skLineSegment(sketch, "E2297", {"start": v(23.73, -27.76) * mm, "end": v(23.76, -27.8) * mm});
            skLineSegment(sketch, "E2298", {"start": v(23.76, -27.8) * mm, "end": v(23.8, -27.86) * mm});
            skLineSegment(sketch, "E2299", {"start": v(23.8, -27.86) * mm, "end": v(23.82, -27.9) * mm});
            skLineSegment(sketch, "E2300", {"start": v(23.82, -27.9) * mm, "end": v(23.86, -27.97) * mm});
            skLineSegment(sketch, "E2301", {"start": v(23.86, -27.97) * mm, "end": v(23.88, -28.02) * mm});
            skLineSegment(sketch, "E2302", {"start": v(23.88, -28.02) * mm, "end": v(23.91, -28.08) * mm});
            skLineSegment(sketch, "E2303", {"start": v(23.91, -28.08) * mm, "end": v(23.94, -28.12) * mm});
            skLineSegment(sketch, "E2304", {"start": v(23.94, -28.12) * mm, "end": v(23.97, -28.19) * mm});
            skLineSegment(sketch, "E2305", {"start": v(23.97, -28.19) * mm, "end": v(24, -28.24) * mm});
            skLineSegment(sketch, "E2306", {"start": v(24, -28.24) * mm, "end": v(24.02, -28.3) * mm});
            skLineSegment(sketch, "E2307", {"start": v(24.02, -28.3) * mm, "end": v(24.04, -28.35) * mm});
            skLineSegment(sketch, "E2308", {"start": v(24.04, -28.35) * mm, "end": v(24.07, -28.41) * mm});
            skLineSegment(sketch, "E2309", {"start": v(24.07, -28.41) * mm, "end": v(24.1, -28.46) * mm});
            skLineSegment(sketch, "E2310", {"start": v(24.1, -28.46) * mm, "end": v(24.12, -28.52) * mm});
            skLineSegment(sketch, "E2311", {"start": v(24.12, -28.52) * mm, "end": v(24.14, -28.58) * mm});
            skLineSegment(sketch, "E2312", {"start": v(24.14, -28.58) * mm, "end": v(24.16, -28.64) * mm});
            skLineSegment(sketch, "E2313", {"start": v(24.16, -28.64) * mm, "end": v(24.18, -28.7) * mm});
            skLineSegment(sketch, "E2314", {"start": v(24.18, -28.7) * mm, "end": v(24.2, -28.75) * mm});
            skLineSegment(sketch, "E2315", {"start": v(24.2, -28.75) * mm, "end": v(24.22, -28.8) * mm});
            skLineSegment(sketch, "E2316", {"start": v(24.22, -28.8) * mm, "end": v(24.24, -28.87) * mm});
            skLineSegment(sketch, "E2317", {"start": v(24.24, -28.87) * mm, "end": v(24.26, -28.94) * mm});
            skLineSegment(sketch, "E2318", {"start": v(24.26, -28.94) * mm, "end": v(24.28, -29) * mm});
            skLineSegment(sketch, "E2319", {"start": v(24.28, -29) * mm, "end": v(24.3, -29.1) * mm});
            skLineSegment(sketch, "E2320", {"start": v(24.3, -29.1) * mm, "end": v(24.32, -29.14) * mm});
            skLineSegment(sketch, "E2321", {"start": v(24.32, -29.14) * mm, "end": v(24.34, -29.23) * mm});
            skLineSegment(sketch, "E2322", {"start": v(24.34, -29.23) * mm, "end": v(24.34, -29.26) * mm});
            skLineSegment(sketch, "E2323", {"start": v(24.34, -29.26) * mm, "end": v(24.36, -29.35) * mm});
            skLineSegment(sketch, "E2324", {"start": v(24.36, -29.35) * mm, "end": v(24.37, -29.38) * mm});
            skLineSegment(sketch, "E2325", {"start": v(24.37, -29.38) * mm, "end": v(24.39, -29.47) * mm});
            skLineSegment(sketch, "E2326", {"start": v(24.39, -29.47) * mm, "end": v(24.4, -29.5) * mm});
            skLineSegment(sketch, "E2327", {"start": v(24.4, -29.5) * mm, "end": v(24.4, -29.59) * mm});
            skLineSegment(sketch, "E2328", {"start": v(24.4, -29.59) * mm, "end": v(24.41, -29.63) * mm});
            skLineSegment(sketch, "E2329", {"start": v(24.41, -29.63) * mm, "end": v(24.42, -29.7) * mm});
            skLineSegment(sketch, "E2330", {"start": v(24.42, -29.7) * mm, "end": v(24.43, -29.75) * mm});
            skLineSegment(sketch, "E2331", {"start": v(24.43, -29.75) * mm, "end": v(24.44, -29.83) * mm});
            skLineSegment(sketch, "E2332", {"start": v(24.44, -29.83) * mm, "end": v(24.44, -29.87) * mm});
            skLineSegment(sketch, "E2333", {"start": v(24.44, -29.87) * mm, "end": v(24.45, -29.95) * mm});
            skLineSegment(sketch, "E2334", {"start": v(24.45, -29.95) * mm, "end": v(24.45, -30) * mm});
            skLineSegment(sketch, "E2335", {"start": v(24.45, -30) * mm, "end": v(24.46, -30.08) * mm});
            skLineSegment(sketch, "E2336", {"start": v(24.46, -30.08) * mm, "end": v(24.46, -30.12) * mm});
            skLineSegment(sketch, "E2337", {"start": v(24.46, -30.12) * mm, "end": v(24.47, -30.2) * mm});
            skLineSegment(sketch, "E2338", {"start": v(24.47, -30.2) * mm, "end": v(24.47, -30.24) * mm});
            skLineSegment(sketch, "E2339", {"start": v(24.47, -30.24) * mm, "end": v(24.47, -30.32) * mm});
            skLineSegment(sketch, "E2340", {"start": v(24.47, -30.32) * mm, "end": v(24.47, -30.36) * mm});
            skLineSegment(sketch, "E2341", {"start": v(24.47, -30.36) * mm, "end": v(24.47, -30.44) * mm});
            skLineSegment(sketch, "E2342", {"start": v(24.47, -30.44) * mm, "end": v(24.47, -30.49) * mm});
            skLineSegment(sketch, "E2343", {"start": v(24.47, -30.49) * mm, "end": v(24.46, -30.57) * mm});
            skLineSegment(sketch, "E2344", {"start": v(24.46, -30.57) * mm, "end": v(24.46, -30.6) * mm});
            skLineSegment(sketch, "E2345", {"start": v(24.46, -30.6) * mm, "end": v(24.46, -30.69) * mm});
            skLineSegment(sketch, "E2346", {"start": v(24.46, -30.69) * mm, "end": v(24.46, -30.73) * mm});
            skLineSegment(sketch, "E2347", {"start": v(24.46, -30.73) * mm, "end": v(24.45, -30.81) * mm});
            skLineSegment(sketch, "E2348", {"start": v(24.45, -30.81) * mm, "end": v(24.44, -30.85) * mm});
            skLineSegment(sketch, "E2349", {"start": v(24.44, -30.85) * mm, "end": v(24.44, -30.93) * mm});
            skLineSegment(sketch, "E2350", {"start": v(24.44, -30.93) * mm, "end": v(24.43, -30.98) * mm});
            skLineSegment(sketch, "E2351", {"start": v(24.43, -30.98) * mm, "end": v(24.42, -31.05) * mm});
            skLineSegment(sketch, "E2352", {"start": v(24.42, -31.05) * mm, "end": v(24.41, -31.1) * mm});
            skLineSegment(sketch, "E2353", {"start": v(24.41, -31.1) * mm, "end": v(24.4, -31.18) * mm});
            skLineSegment(sketch, "E2354", {"start": v(24.4, -31.18) * mm, "end": v(24.4, -31.22) * mm});
            skLineSegment(sketch, "E2355", {"start": v(24.4, -31.22) * mm, "end": v(24.38, -31.3) * mm});
            skLineSegment(sketch, "E2356", {"start": v(24.38, -31.3) * mm, "end": v(24.37, -31.34) * mm});
            skLineSegment(sketch, "E2357", {"start": v(24.37, -31.34) * mm, "end": v(24.36, -31.42) * mm});
            skLineSegment(sketch, "E2358", {"start": v(24.36, -31.42) * mm, "end": v(24.35, -31.46) * mm});
            skLineSegment(sketch, "E2359", {"start": v(24.35, -31.46) * mm, "end": v(24.33, -31.54) * mm});
            skLineSegment(sketch, "E2360", {"start": v(24.33, -31.54) * mm, "end": v(24.32, -31.58) * mm});
            skLineSegment(sketch, "E2361", {"start": v(24.32, -31.58) * mm, "end": v(24.3, -31.66) * mm});
            skLineSegment(sketch, "E2362", {"start": v(24.3, -31.66) * mm, "end": v(24.29, -31.7) * mm});
            skLineSegment(sketch, "E2363", {"start": v(24.29, -31.7) * mm, "end": v(24.27, -31.77) * mm});
            skLineSegment(sketch, "E2364", {"start": v(24.27, -31.77) * mm, "end": v(24.25, -31.82) * mm});
            skLineSegment(sketch, "E2365", {"start": v(24.25, -31.82) * mm, "end": v(24.23, -31.9) * mm});
            skLineSegment(sketch, "E2366", {"start": v(24.23, -31.9) * mm, "end": v(24.22, -31.94) * mm});
            skLineSegment(sketch, "E2367", {"start": v(24.22, -31.94) * mm, "end": v(24.2, -32) * mm});
            skLineSegment(sketch, "E2368", {"start": v(24.2, -32) * mm, "end": v(24.18, -32.05) * mm});
            skLineSegment(sketch, "E2369", {"start": v(24.18, -32.05) * mm, "end": v(24.15, -32.12) * mm});
            skLineSegment(sketch, "E2370", {"start": v(24.15, -32.12) * mm, "end": v(24.13, -32.17) * mm});
            skLineSegment(sketch, "E2371", {"start": v(24.13, -32.17) * mm, "end": v(24.1, -32.24) * mm});
            skLineSegment(sketch, "E2372", {"start": v(24.1, -32.24) * mm, "end": v(24.09, -32.28) * mm});
            skLineSegment(sketch, "E2373", {"start": v(24.09, -32.28) * mm, "end": v(24.06, -32.35) * mm});
            skLineSegment(sketch, "E2374", {"start": v(24.06, -32.35) * mm, "end": v(24.04, -32.4) * mm});
            skLineSegment(sketch, "E2375", {"start": v(24.04, -32.4) * mm, "end": v(24, -32.46) * mm});
            skLineSegment(sketch, "E2376", {"start": v(24, -32.46) * mm, "end": v(23.99, -32.5) * mm});
            skLineSegment(sketch, "E2377", {"start": v(23.99, -32.5) * mm, "end": v(23.96, -32.57) * mm});
            skLineSegment(sketch, "E2378", {"start": v(23.96, -32.57) * mm, "end": v(23.93, -32.62) * mm});
            skLineSegment(sketch, "E2379", {"start": v(23.93, -32.62) * mm, "end": v(23.9, -32.68) * mm});
            skLineSegment(sketch, "E2380", {"start": v(23.9, -32.68) * mm, "end": v(23.88, -32.73) * mm});
            skLineSegment(sketch, "E2381", {"start": v(23.88, -32.73) * mm, "end": v(23.84, -32.8) * mm});
            skLineSegment(sketch, "E2382", {"start": v(23.84, -32.8) * mm, "end": v(23.82, -32.84) * mm});
            skLineSegment(sketch, "E2383", {"start": v(23.82, -32.84) * mm, "end": v(23.78, -32.9) * mm});
            skLineSegment(sketch, "E2384", {"start": v(23.78, -32.9) * mm, "end": v(23.75, -32.94) * mm});
            skLineSegment(sketch, "E2385", {"start": v(23.75, -32.94) * mm, "end": v(23.72, -33) * mm});
            skLineSegment(sketch, "E2386", {"start": v(23.72, -33) * mm, "end": v(23.69, -33.05) * mm});
            skLineSegment(sketch, "E2387", {"start": v(23.69, -33.05) * mm, "end": v(23.65, -33.1) * mm});
            skLineSegment(sketch, "E2388", {"start": v(23.65, -33.1) * mm, "end": v(23.62, -33.15) * mm});
            skLineSegment(sketch, "E2389", {"start": v(23.62, -33.15) * mm, "end": v(23.58, -33.2) * mm});
            skLineSegment(sketch, "E2390", {"start": v(23.58, -33.2) * mm, "end": v(23.55, -33.25) * mm});
            skLineSegment(sketch, "E2391", {"start": v(23.55, -33.25) * mm, "end": v(23.51, -33.3) * mm});
            skLineSegment(sketch, "E2392", {"start": v(23.51, -33.3) * mm, "end": v(23.48, -33.35) * mm});
            skLineSegment(sketch, "E2393", {"start": v(23.48, -33.35) * mm, "end": v(23.44, -33.4) * mm});
            skLineSegment(sketch, "E2394", {"start": v(23.44, -33.4) * mm, "end": v(23.4, -33.45) * mm});
            skLineSegment(sketch, "E2395", {"start": v(23.4, -33.45) * mm, "end": v(23.36, -33.5) * mm});
            skLineSegment(sketch, "E2396", {"start": v(23.36, -33.5) * mm, "end": v(23.33, -33.55) * mm});
            skLineSegment(sketch, "E2397", {"start": v(23.33, -33.55) * mm, "end": v(23.29, -33.6) * mm});
            skLineSegment(sketch, "E2398", {"start": v(23.29, -33.6) * mm, "end": v(23.25, -33.64) * mm});
            skLineSegment(sketch, "E2399", {"start": v(23.25, -33.64) * mm, "end": v(23.2, -33.7) * mm});
            skLineSegment(sketch, "E2400", {"start": v(23.2, -33.7) * mm, "end": v(23.17, -33.73) * mm});
            skLineSegment(sketch, "E2401", {"start": v(23.17, -33.73) * mm, "end": v(23.12, -33.78) * mm});
            skLineSegment(sketch, "E2402", {"start": v(23.12, -33.78) * mm, "end": v(23.1, -33.8) * mm});
            skLineSegment(sketch, "E2403", {"start": v(23.1, -33.8) * mm, "end": v(23.09, -33.82) * mm});
            skLineSegment(sketch, "E2404", {"start": v(23.09, -33.82) * mm, "end": v(23.13, -33.85) * mm});
            skLineSegment(sketch, "E2405", {"start": v(23.13, -33.85) * mm, "end": v(23.18, -33.88) * mm});
            skLineSegment(sketch, "E2406", {"start": v(23.18, -33.88) * mm, "end": v(23.55, -34.06) * mm});
            skLineSegment(sketch, "E2407", {"start": v(23.55, -34.06) * mm, "end": v(23.99, -34.3) * mm});
            skLineSegment(sketch, "E2408", {"start": v(23.99, -34.3) * mm, "end": v(24.36, -34.48) * mm});
            skLineSegment(sketch, "E2409", {"start": v(24.36, -34.48) * mm, "end": v(24.42, -34.5) * mm});
            skLineSegment(sketch, "E2410", {"start": v(24.42, -34.5) * mm, "end": v(24.86, -34.72) * mm});
            skLineSegment(sketch, "E2411", {"start": v(24.86, -34.72) * mm, "end": v(24.93, -34.75) * mm});
            skLineSegment(sketch, "E2412", {"start": v(24.93, -34.75) * mm, "end": v(25.31, -34.92) * mm});
            skLineSegment(sketch, "E2413", {"start": v(25.31, -34.92) * mm, "end": v(25.64, -35.07) * mm});
            skLineSegment(sketch, "E2414", {"start": v(25.64, -35.07) * mm, "end": v(26.15, -35.3) * mm});
            skLineSegment(sketch, "E2415", {"start": v(26.15, -35.3) * mm, "end": v(26.47, -35.43) * mm});
            skLineSegment(sketch, "E2416", {"start": v(26.47, -35.43) * mm, "end": v(26.8, -35.56) * mm});
            skLineSegment(sketch, "E2417", {"start": v(26.8, -35.56) * mm, "end": v(27.31, -35.77) * mm});
            skLineSegment(sketch, "E2418", {"start": v(27.31, -35.77) * mm, "end": v(27.64, -35.89) * mm});
            skLineSegment(sketch, "E2419", {"start": v(27.64, -35.89) * mm, "end": v(28.16, -36.08) * mm});
            skLineSegment(sketch, "E2420", {"start": v(28.16, -36.08) * mm, "end": v(28.7, -36.26) * mm});
            skLineSegment(sketch, "E2421", {"start": v(28.7, -36.26) * mm, "end": v(29.02, -36.38) * mm});
            skLineSegment(sketch, "E2422", {"start": v(29.02, -36.38) * mm, "end": v(29.35, -36.48) * mm});
            skLineSegment(sketch, "E2423", {"start": v(29.35, -36.48) * mm, "end": v(29.89, -36.65) * mm});
            skLineSegment(sketch, "E2424", {"start": v(29.89, -36.65) * mm, "end": v(30.22, -36.75) * mm});
            skLineSegment(sketch, "E2425", {"start": v(30.22, -36.75) * mm, "end": v(30.76, -36.9) * mm});
            skLineSegment(sketch, "E2426", {"start": v(30.76, -36.9) * mm, "end": v(31.1, -37) * mm});
            skLineSegment(sketch, "E2427", {"start": v(31.1, -37) * mm, "end": v(31.64, -37.14) * mm});
            skLineSegment(sketch, "E2428", {"start": v(31.64, -37.14) * mm, "end": v(31.98, -37.22) * mm});
            skLineSegment(sketch, "E2429", {"start": v(31.98, -37.22) * mm, "end": v(32.52, -37.35) * mm});
            skLineSegment(sketch, "E2430", {"start": v(32.52, -37.35) * mm, "end": v(32.86, -37.42) * mm});
            skLineSegment(sketch, "E2431", {"start": v(32.86, -37.42) * mm, "end": v(33.41, -37.53) * mm});
            skLineSegment(sketch, "E2432", {"start": v(33.41, -37.53) * mm, "end": v(33.96, -37.64) * mm});
            skLineSegment(sketch, "E2433", {"start": v(33.96, -37.64) * mm, "end": v(34.3, -37.7) * mm});
            skLineSegment(sketch, "E2434", {"start": v(34.3, -37.7) * mm, "end": v(34.86, -37.79) * mm});
            skLineSegment(sketch, "E2435", {"start": v(34.86, -37.79) * mm, "end": v(35.2, -37.84) * mm});
            skLineSegment(sketch, "E2436", {"start": v(35.2, -37.84) * mm, "end": v(35.75, -37.92) * mm});
            skLineSegment(sketch, "E2437", {"start": v(35.75, -37.92) * mm, "end": v(36.1, -37.97) * mm});
            skLineSegment(sketch, "E2438", {"start": v(36.1, -37.97) * mm, "end": v(36.66, -38.03) * mm});
            skLineSegment(sketch, "E2439", {"start": v(36.66, -38.03) * mm, "end": v(37, -38.07) * mm});
            skLineSegment(sketch, "E2440", {"start": v(37, -38.07) * mm, "end": v(37.56, -38.11) * mm});
            skLineSegment(sketch, "E2441", {"start": v(37.56, -38.11) * mm, "end": v(37.9, -38.14) * mm});
            skLineSegment(sketch, "E2442", {"start": v(37.9, -38.14) * mm, "end": v(38.25, -38.17) * mm});
            skLineSegment(sketch, "E2443", {"start": v(38.25, -38.17) * mm, "end": v(38.81, -38.2) * mm});
            skLineSegment(sketch, "E2444", {"start": v(38.81, -38.2) * mm, "end": v(39.16, -38.21) * mm});
            skLineSegment(sketch, "E2445", {"start": v(39.16, -38.21) * mm, "end": v(39.72, -38.23) * mm});
            skLineSegment(sketch, "E2446", {"start": v(39.72, -38.23) * mm, "end": v(40.28, -38.24) * mm});
            skLineSegment(sketch, "E2447", {"start": v(40.28, -38.24) * mm, "end": v(40.63, -38.24) * mm});
            skLineSegment(sketch, "E2448", {"start": v(40.63, -38.24) * mm, "end": v(40.98, -38.24) * mm});
            skLineSegment(sketch, "E2449", {"start": v(40.98, -38.24) * mm, "end": v(41.54, -38.23) * mm});
            skLineSegment(sketch, "E2450", {"start": v(41.54, -38.23) * mm, "end": v(42.1, -38.21) * mm});
            skLineSegment(sketch, "E2451", {"start": v(42.1, -38.21) * mm, "end": v(42.44, -38.2) * mm});
            skLineSegment(sketch, "E2452", {"start": v(42.44, -38.2) * mm, "end": v(43, -38.17) * mm});
            skLineSegment(sketch, "E2453", {"start": v(43, -38.17) * mm, "end": v(43.35, -38.14) * mm});
            skLineSegment(sketch, "E2454", {"start": v(43.35, -38.14) * mm, "end": v(43.9, -38.1) * mm});
            skLineSegment(sketch, "E2455", {"start": v(43.9, -38.1) * mm, "end": v(44.26, -38.07) * mm});
            skLineSegment(sketch, "E2456", {"start": v(44.26, -38.07) * mm, "end": v(44.81, -38) * mm});
            skLineSegment(sketch, "E2457", {"start": v(44.81, -38) * mm, "end": v(45.16, -37.97) * mm});
            skLineSegment(sketch, "E2458", {"start": v(45.16, -37.97) * mm, "end": v(45.71, -37.9) * mm});
            skLineSegment(sketch, "E2459", {"start": v(45.71, -37.9) * mm, "end": v(46.06, -37.84) * mm});
            skLineSegment(sketch, "E2460", {"start": v(46.06, -37.84) * mm, "end": v(46.61, -37.75) * mm});
            skLineSegment(sketch, "E2461", {"start": v(46.61, -37.75) * mm, "end": v(46.95, -37.7) * mm});
            skLineSegment(sketch, "E2462", {"start": v(46.95, -37.7) * mm, "end": v(47.5, -37.6) * mm});
            skLineSegment(sketch, "E2463", {"start": v(47.5, -37.6) * mm, "end": v(47.85, -37.53) * mm});
            skLineSegment(sketch, "E2464", {"start": v(47.85, -37.53) * mm, "end": v(48.4, -37.42) * mm});
            skLineSegment(sketch, "E2465", {"start": v(48.4, -37.42) * mm, "end": v(48.74, -37.35) * mm});
            skLineSegment(sketch, "E2466", {"start": v(48.74, -37.35) * mm, "end": v(49.28, -37.22) * mm});
            skLineSegment(sketch, "E2467", {"start": v(49.28, -37.22) * mm, "end": v(49.62, -37.14) * mm});
            skLineSegment(sketch, "E2468", {"start": v(49.62, -37.14) * mm, "end": v(49.96, -37.05) * mm});
            skLineSegment(sketch, "E2469", {"start": v(49.96, -37.05) * mm, "end": v(50.5, -36.9) * mm});
            skLineSegment(sketch, "E2470", {"start": v(50.5, -36.9) * mm, "end": v(51.04, -36.75) * mm});
            skLineSegment(sketch, "E2471", {"start": v(51.04, -36.75) * mm, "end": v(51.37, -36.65) * mm});
            skLineSegment(sketch, "E2472", {"start": v(51.37, -36.65) * mm, "end": v(51.92, -36.48) * mm});
            skLineSegment(sketch, "E2473", {"start": v(51.92, -36.48) * mm, "end": v(51.93, -36.47) * mm});
            skLineSegment(sketch, "E2474", {"start": v(51.93, -36.47) * mm, "end": v(52.24, -36.38) * mm});
            skLineSegment(sketch, "E2475", {"start": v(52.24, -36.38) * mm, "end": v(52.48, -36.3) * mm});
            skLineSegment(sketch, "E2476", {"start": v(52.48, -36.3) * mm, "end": v(52.77, -36.2) * mm});
            skLineSegment(sketch, "E2477", {"start": v(52.77, -36.2) * mm, "end": v(52.82, -36.18) * mm});
            skLineSegment(sketch, "E2478", {"start": v(52.82, -36.18) * mm, "end": v(53.1, -36.08) * mm});
            skLineSegment(sketch, "E2479", {"start": v(53.1, -36.08) * mm, "end": v(53.36, -35.98) * mm});
            skLineSegment(sketch, "E2480", {"start": v(53.36, -35.98) * mm, "end": v(53.68, -35.86) * mm});
            skLineSegment(sketch, "E2481", {"start": v(53.68, -35.86) * mm, "end": v(53.94, -35.76) * mm});
            skLineSegment(sketch, "E2482", {"start": v(53.94, -35.76) * mm, "end": v(53.96, -35.76) * mm});
            skLineSegment(sketch, "E2483", {"start": v(53.96, -35.76) * mm, "end": v(54.22, -35.65) * mm});
            skLineSegment(sketch, "E2484", {"start": v(54.22, -35.65) * mm, "end": v(54.87, -35.37) * mm});
            skLineSegment(sketch, "E2485", {"start": v(54.87, -35.37) * mm, "end": v(55.16, -35.25) * mm});
            skLineSegment(sketch, "E2486", {"start": v(55.16, -35.25) * mm, "end": v(55.4, -35.16) * mm});
            skLineSegment(sketch, "E2487", {"start": v(55.4, -35.16) * mm, "end": v(55.44, -35.14) * mm});
            skLineSegment(sketch, "E2488", {"start": v(55.44, -35.14) * mm, "end": v(55.5, -35.12) * mm});
            skLineSegment(sketch, "E2489", {"start": v(55.5, -35.12) * mm, "end": v(56.42, -34.66) * mm});
            skLineSegment(sketch, "E2490", {"start": v(56.42, -34.66) * mm, "end": v(56.67, -34.55) * mm});
            skLineSegment(sketch, "E2491", {"start": v(56.67, -34.55) * mm, "end": v(57.75, -34.04) * mm});
            skLineSegment(sketch, "E2492", {"start": v(57.75, -34.04) * mm, "end": v(58.12, -33.85) * mm});
            skLineSegment(sketch, "E2493", {"start": v(58.12, -33.85) * mm, "end": v(58.06, -33.78) * mm});
            skLineSegment(sketch, "E2494", {"start": v(58.06, -33.78) * mm, "end": v(58.01, -33.73) * mm});
            skLineSegment(sketch, "E2495", {"start": v(58.01, -33.73) * mm, "end": v(57.97, -33.68) * mm});
            skLineSegment(sketch, "E2496", {"start": v(57.97, -33.68) * mm, "end": v(57.93, -33.62) * mm});
            skLineSegment(sketch, "E2497", {"start": v(57.93, -33.62) * mm, "end": v(57.89, -33.57) * mm});
            skLineSegment(sketch, "E2498", {"start": v(57.89, -33.57) * mm, "end": v(57.85, -33.5) * mm});
            skLineSegment(sketch, "E2499", {"start": v(57.85, -33.5) * mm, "end": v(57.8, -33.45) * mm});
            skLineSegment(sketch, "E2500", {"start": v(57.8, -33.45) * mm, "end": v(57.77, -33.39) * mm});
            skLineSegment(sketch, "E2501", {"start": v(57.77, -33.39) * mm, "end": v(57.73, -33.32) * mm});
            skLineSegment(sketch, "E2502", {"start": v(57.73, -33.32) * mm, "end": v(57.7, -33.26) * mm});
            skLineSegment(sketch, "E2503", {"start": v(57.7, -33.26) * mm, "end": v(57.66, -33.2) * mm});
            skLineSegment(sketch, "E2504", {"start": v(57.66, -33.2) * mm, "end": v(57.62, -33.12) * mm});
            skLineSegment(sketch, "E2505", {"start": v(57.62, -33.12) * mm, "end": v(57.59, -33.05) * mm});
            skLineSegment(sketch, "E2506", {"start": v(57.59, -33.05) * mm, "end": v(57.56, -32.98) * mm});
            skLineSegment(sketch, "E2507", {"start": v(57.56, -32.98) * mm, "end": v(57.52, -32.9) * mm});
            skLineSegment(sketch, "E2508", {"start": v(57.52, -32.9) * mm, "end": v(57.5, -32.83) * mm});
            skLineSegment(sketch, "E2509", {"start": v(57.5, -32.83) * mm, "end": v(57.46, -32.76) * mm});
            skLineSegment(sketch, "E2510", {"start": v(57.46, -32.76) * mm, "end": v(57.44, -32.68) * mm});
            skLineSegment(sketch, "E2511", {"start": v(57.44, -32.68) * mm, "end": v(57.41, -32.6) * mm});
            skLineSegment(sketch, "E2512", {"start": v(57.41, -32.6) * mm, "end": v(57.45, -32.57) * mm});
            skLineSegment(sketch, "E2513", {"start": v(57.45, -32.57) * mm, "end": v(57.4, -32.52) * mm});
            skLineSegment(sketch, "E2514", {"start": v(57.4, -32.52) * mm, "end": v(57.38, -32.44) * mm});
            skLineSegment(sketch, "E2515", {"start": v(57.38, -32.44) * mm, "end": v(57.36, -32.36) * mm});
            skLineSegment(sketch, "E2516", {"start": v(57.36, -32.36) * mm, "end": v(57.33, -32.27) * mm});
            skLineSegment(sketch, "E2517", {"start": v(57.33, -32.27) * mm, "end": v(57.3, -32.24) * mm});
            skLineSegment(sketch, "E2518", {"start": v(57.3, -32.24) * mm, "end": v(57.28, -32.15) * mm});
            skLineSegment(sketch, "E2519", {"start": v(57.28, -32.15) * mm, "end": v(57.26, -32.12) * mm});
            skLineSegment(sketch, "E2520", {"start": v(57.26, -32.12) * mm, "end": v(57.24, -32.03) * mm});
            skLineSegment(sketch, "E2521", {"start": v(57.24, -32.03) * mm, "end": v(57.2, -32) * mm});
            skLineSegment(sketch, "E2522", {"start": v(57.2, -32) * mm, "end": v(57.2, -31.91) * mm});
            skLineSegment(sketch, "E2523", {"start": v(57.2, -31.91) * mm, "end": v(57.17, -31.88) * mm});
            skLineSegment(sketch, "E2524", {"start": v(57.17, -31.88) * mm, "end": v(57.14, -31.84) * mm});
            skLineSegment(sketch, "E2525", {"start": v(57.14, -31.84) * mm, "end": v(57.13, -31.75) * mm});
            skLineSegment(sketch, "E2526", {"start": v(57.13, -31.75) * mm, "end": v(57.1, -31.71) * mm});
            skLineSegment(sketch, "E2527", {"start": v(57.1, -31.71) * mm, "end": v(57.1, -31.63) * mm});
            skLineSegment(sketch, "E2528", {"start": v(57.1, -31.63) * mm, "end": v(57.07, -31.59) * mm});
            skLineSegment(sketch, "E2529", {"start": v(57.07, -31.59) * mm, "end": v(57.05, -31.55) * mm});
            skLineSegment(sketch, "E2530", {"start": v(57.05, -31.55) * mm, "end": v(57.04, -31.46) * mm});
            skLineSegment(sketch, "E2531", {"start": v(57.04, -31.46) * mm, "end": v(57.02, -31.43) * mm});
            skLineSegment(sketch, "E2532", {"start": v(57.02, -31.43) * mm, "end": v(57, -31.39) * mm});
            skLineSegment(sketch, "E2533", {"start": v(57, -31.39) * mm, "end": v(56.99, -31.3) * mm});
            skLineSegment(sketch, "E2534", {"start": v(56.99, -31.3) * mm, "end": v(56.97, -31.26) * mm});
            skLineSegment(sketch, "E2535", {"start": v(56.97, -31.26) * mm, "end": v(56.96, -31.17) * mm});
            skLineSegment(sketch, "E2536", {"start": v(56.96, -31.17) * mm, "end": v(56.95, -31.13) * mm});
            skLineSegment(sketch, "E2537", {"start": v(56.95, -31.13) * mm, "end": v(56.94, -31.04) * mm});
            skLineSegment(sketch, "E2538", {"start": v(56.94, -31.04) * mm, "end": v(56.93, -31) * mm});
            skLineSegment(sketch, "E2539", {"start": v(56.93, -31) * mm, "end": v(56.91, -30.97) * mm});
            skLineSegment(sketch, "E2540", {"start": v(56.91, -30.97) * mm, "end": v(56.91, -30.88) * mm});
            skLineSegment(sketch, "E2541", {"start": v(56.91, -30.88) * mm, "end": v(56.9, -30.84) * mm});
            skLineSegment(sketch, "E2542", {"start": v(56.9, -30.84) * mm, "end": v(56.9, -30.75) * mm});
            skLineSegment(sketch, "E2543", {"start": v(56.9, -30.75) * mm, "end": v(56.89, -30.71) * mm});
            skLineSegment(sketch, "E2544", {"start": v(56.89, -30.71) * mm, "end": v(56.87, -30.67) * mm});
            skLineSegment(sketch, "E2545", {"start": v(56.87, -30.67) * mm, "end": v(56.88, -30.58) * mm});
            skLineSegment(sketch, "E2546", {"start": v(56.88, -30.58) * mm, "end": v(56.87, -30.54) * mm});
            skLineSegment(sketch, "E2547", {"start": v(56.87, -30.54) * mm, "end": v(56.87, -30.45) * mm});
            skLineSegment(sketch, "E2548", {"start": v(56.87, -30.45) * mm, "end": v(56.86, -30.42) * mm});
            skLineSegment(sketch, "E2549", {"start": v(56.86, -30.42) * mm, "end": v(56.85, -30.38) * mm});
            skLineSegment(sketch, "E2550", {"start": v(56.85, -30.38) * mm, "end": v(56.86, -30.29) * mm});
            skLineSegment(sketch, "E2551", {"start": v(56.86, -30.29) * mm, "end": v(56.85, -30.25) * mm});
            skLineSegment(sketch, "E2552", {"start": v(56.85, -30.25) * mm, "end": v(56.87, -30.16) * mm});
            skLineSegment(sketch, "E2553", {"start": v(56.87, -30.16) * mm, "end": v(56.86, -30.12) * mm});
            skLineSegment(sketch, "E2554", {"start": v(56.86, -30.12) * mm, "end": v(56.85, -30.08) * mm});
            skLineSegment(sketch, "E2555", {"start": v(56.85, -30.08) * mm, "end": v(56.87, -30) * mm});
            skLineSegment(sketch, "E2556", {"start": v(56.87, -30) * mm, "end": v(56.86, -29.96) * mm});
            skLineSegment(sketch, "E2557", {"start": v(56.86, -29.96) * mm, "end": v(56.88, -29.87) * mm});
            skLineSegment(sketch, "E2558", {"start": v(56.88, -29.87) * mm, "end": v(56.87, -29.83) * mm});
            skLineSegment(sketch, "E2559", {"start": v(56.87, -29.83) * mm, "end": v(56.87, -29.8) * mm});
            skLineSegment(sketch, "E2560", {"start": v(56.87, -29.8) * mm, "end": v(56.89, -29.7) * mm});
            skLineSegment(sketch, "E2561", {"start": v(56.89, -29.7) * mm, "end": v(56.89, -29.66) * mm});
            skLineSegment(sketch, "E2562", {"start": v(56.89, -29.66) * mm, "end": v(56.88, -29.63) * mm});
            skLineSegment(sketch, "E2563", {"start": v(56.88, -29.63) * mm, "end": v(56.88, -29.6) * mm});
            skLineSegment(sketch, "E2564", {"start": v(56.88, -29.6) * mm, "end": v(56.88, -29.55) * mm});
            skLineSegment(sketch, "E2565", {"start": v(56.88, -29.55) * mm, "end": v(56.88, -29.52) * mm});
            skLineSegment(sketch, "E2566", {"start": v(56.88, -29.52) * mm, "end": v(56.88, -29.48) * mm});
            skLineSegment(sketch, "E2567", {"start": v(56.88, -29.48) * mm, "end": v(56.89, -29.44) * mm});
            skLineSegment(sketch, "E2568", {"start": v(56.89, -29.44) * mm, "end": v(56.9, -29.4) * mm});
            skLineSegment(sketch, "E2569", {"start": v(56.9, -29.4) * mm, "end": v(56.9, -29.37) * mm});
            skLineSegment(sketch, "E2570", {"start": v(56.9, -29.37) * mm, "end": v(56.9, -29.33) * mm});
            skLineSegment(sketch, "E2571", {"start": v(56.9, -29.33) * mm, "end": v(56.97, -29.06) * mm});
            skLineSegment(sketch, "E2572", {"start": v(56.97, -29.06) * mm, "end": v(56.98, -29) * mm});
            skLineSegment(sketch, "E2573", {"start": v(56.98, -29) * mm, "end": v(57, -28.93) * mm});
            skLineSegment(sketch, "E2574", {"start": v(57, -28.93) * mm, "end": v(57.02, -28.87) * mm});
            skLineSegment(sketch, "E2575", {"start": v(57.02, -28.87) * mm, "end": v(57.04, -28.8) * mm});
            skLineSegment(sketch, "E2576", {"start": v(57.04, -28.8) * mm, "end": v(57.06, -28.74) * mm});
            skLineSegment(sketch, "E2577", {"start": v(57.06, -28.74) * mm, "end": v(57.09, -28.68) * mm});
            skLineSegment(sketch, "E2578", {"start": v(57.09, -28.68) * mm, "end": v(57.11, -28.62) * mm});
            skLineSegment(sketch, "E2579", {"start": v(57.11, -28.62) * mm, "end": v(57.14, -28.55) * mm});
            skLineSegment(sketch, "E2580", {"start": v(57.14, -28.55) * mm, "end": v(57.17, -28.49) * mm});
            skLineSegment(sketch, "E2581", {"start": v(57.17, -28.49) * mm, "end": v(57.2, -28.42) * mm});
            skLineSegment(sketch, "E2582", {"start": v(57.2, -28.42) * mm, "end": v(57.22, -28.37) * mm});
            skLineSegment(sketch, "E2583", {"start": v(57.22, -28.37) * mm, "end": v(57.24, -28.32) * mm});
            skLineSegment(sketch, "E2584", {"start": v(57.24, -28.32) * mm, "end": v(57.26, -28.27) * mm});
            skLineSegment(sketch, "E2585", {"start": v(57.26, -28.27) * mm, "end": v(57.3, -28.2) * mm});
            skLineSegment(sketch, "E2586", {"start": v(57.3, -28.2) * mm, "end": v(57.31, -28.16) * mm});
            skLineSegment(sketch, "E2587", {"start": v(57.31, -28.16) * mm, "end": v(57.35, -28.1) * mm});
            skLineSegment(sketch, "E2588", {"start": v(57.35, -28.1) * mm, "end": v(57.37, -28.05) * mm});
            skLineSegment(sketch, "E2589", {"start": v(57.37, -28.05) * mm, "end": v(57.4, -27.98) * mm});
            skLineSegment(sketch, "E2590", {"start": v(57.4, -27.98) * mm, "end": v(57.43, -27.94) * mm});
            skLineSegment(sketch, "E2591", {"start": v(57.43, -27.94) * mm, "end": v(57.47, -27.87) * mm});
            skLineSegment(sketch, "E2592", {"start": v(57.47, -27.87) * mm, "end": v(57.49, -27.83) * mm});
            skLineSegment(sketch, "E2593", {"start": v(57.49, -27.83) * mm, "end": v(57.51, -27.78) * mm});
            skLineSegment(sketch, "E2594", {"start": v(57.51, -27.78) * mm, "end": v(57.55, -27.72) * mm});
            skLineSegment(sketch, "E2595", {"start": v(57.55, -27.72) * mm, "end": v(57.58, -27.68) * mm});
            skLineSegment(sketch, "E2596", {"start": v(57.58, -27.68) * mm, "end": v(57.62, -27.62) * mm});
            skLineSegment(sketch, "E2597", {"start": v(57.62, -27.62) * mm, "end": v(57.65, -27.57) * mm});
            skLineSegment(sketch, "E2598", {"start": v(57.65, -27.57) * mm, "end": v(57.7, -27.52) * mm});
            skLineSegment(sketch, "E2599", {"start": v(57.7, -27.52) * mm, "end": v(57.72, -27.47) * mm});
            skLineSegment(sketch, "E2600", {"start": v(57.72, -27.47) * mm, "end": v(57.76, -27.41) * mm});
            skLineSegment(sketch, "E2601", {"start": v(57.76, -27.41) * mm, "end": v(57.79, -27.37) * mm});
            skLineSegment(sketch, "E2602", {"start": v(57.79, -27.37) * mm, "end": v(57.82, -27.33) * mm});
            skLineSegment(sketch, "E2603", {"start": v(57.82, -27.33) * mm, "end": v(57.86, -27.27) * mm});
            skLineSegment(sketch, "E2604", {"start": v(57.86, -27.27) * mm, "end": v(57.9, -27.23) * mm});
            skLineSegment(sketch, "E2605", {"start": v(57.9, -27.23) * mm, "end": v(57.94, -27.18) * mm});
            skLineSegment(sketch, "E2606", {"start": v(57.94, -27.18) * mm, "end": v(57.97, -27.14) * mm});
            skLineSegment(sketch, "E2607", {"start": v(57.97, -27.14) * mm, "end": v(58.02, -27.08) * mm});
            skLineSegment(sketch, "E2608", {"start": v(58.02, -27.08) * mm, "end": v(58.05, -27.05) * mm});
            skLineSegment(sketch, "E2609", {"start": v(58.05, -27.05) * mm, "end": v(58.08, -27) * mm});
            skLineSegment(sketch, "E2610", {"start": v(58.08, -27) * mm, "end": v(58.14, -26.96) * mm});
            skLineSegment(sketch, "E2611", {"start": v(58.14, -26.96) * mm, "end": v(58.17, -26.92) * mm});
            skLineSegment(sketch, "E2612", {"start": v(58.17, -26.92) * mm, "end": v(58.22, -26.87) * mm});
            skLineSegment(sketch, "E2613", {"start": v(58.22, -26.87) * mm, "end": v(58.25, -26.83) * mm});
            skLineSegment(sketch, "E2614", {"start": v(58.25, -26.83) * mm, "end": v(58.3, -26.78) * mm});
            skLineSegment(sketch, "E2615", {"start": v(58.3, -26.78) * mm, "end": v(58.34, -26.75) * mm});
            skLineSegment(sketch, "E2616", {"start": v(58.34, -26.75) * mm, "end": v(58.4, -26.7) * mm});
            skLineSegment(sketch, "E2617", {"start": v(58.4, -26.7) * mm, "end": v(58.43, -26.66) * mm});
            skLineSegment(sketch, "E2618", {"start": v(58.43, -26.66) * mm, "end": v(58.47, -26.63) * mm});
            skLineSegment(sketch, "E2619", {"start": v(58.47, -26.63) * mm, "end": v(58.52, -26.58) * mm});
            skLineSegment(sketch, "E2620", {"start": v(58.52, -26.58) * mm, "end": v(58.56, -26.55) * mm});
            skLineSegment(sketch, "E2621", {"start": v(58.56, -26.55) * mm, "end": v(58.62, -26.5) * mm});
            skLineSegment(sketch, "E2622", {"start": v(58.62, -26.5) * mm, "end": v(58.66, -26.47) * mm});
            skLineSegment(sketch, "E2623", {"start": v(58.66, -26.47) * mm, "end": v(58.71, -26.43) * mm});
            skLineSegment(sketch, "E2624", {"start": v(58.71, -26.43) * mm, "end": v(58.75, -26.4) * mm});
            skLineSegment(sketch, "E2625", {"start": v(58.75, -26.4) * mm, "end": v(58.81, -26.35) * mm});
            skLineSegment(sketch, "E2626", {"start": v(58.81, -26.35) * mm, "end": v(58.85, -26.32) * mm});
            skLineSegment(sketch, "E2627", {"start": v(58.85, -26.32) * mm, "end": v(58.89, -26.3) * mm});
            skLineSegment(sketch, "E2628", {"start": v(58.89, -26.3) * mm, "end": v(58.95, -26.25) * mm});
            skLineSegment(sketch, "E2629", {"start": v(58.95, -26.25) * mm, "end": v(59, -26.23) * mm});
            skLineSegment(sketch, "E2630", {"start": v(59, -26.23) * mm, "end": v(59.05, -26.18) * mm});
            skLineSegment(sketch, "E2631", {"start": v(59.05, -26.18) * mm, "end": v(59.1, -26.16) * mm});
            skLineSegment(sketch, "E2632", {"start": v(59.1, -26.16) * mm, "end": v(59.16, -26.12) * mm});
            skLineSegment(sketch, "E2633", {"start": v(59.16, -26.12) * mm, "end": v(59.2, -26.1) * mm});
            skLineSegment(sketch, "E2634", {"start": v(59.2, -26.1) * mm, "end": v(59.26, -26.05) * mm});
            skLineSegment(sketch, "E2635", {"start": v(59.26, -26.05) * mm, "end": v(59.3, -26.03) * mm});
            skLineSegment(sketch, "E2636", {"start": v(59.3, -26.03) * mm, "end": v(59.37, -26) * mm});
            skLineSegment(sketch, "E2637", {"start": v(59.37, -26) * mm, "end": v(59.41, -25.97) * mm});
            skLineSegment(sketch, "E2638", {"start": v(59.41, -25.97) * mm, "end": v(59.48, -25.94) * mm});
            skLineSegment(sketch, "E2639", {"start": v(59.48, -25.94) * mm, "end": v(59.52, -25.91) * mm});
            skLineSegment(sketch, "E2640", {"start": v(59.52, -25.91) * mm, "end": v(59.59, -25.88) * mm});
            skLineSegment(sketch, "E2641", {"start": v(59.59, -25.88) * mm, "end": v(59.63, -25.86) * mm});
            skLineSegment(sketch, "E2642", {"start": v(59.63, -25.86) * mm, "end": v(59.7, -25.83) * mm});
            skLineSegment(sketch, "E2643", {"start": v(59.7, -25.83) * mm, "end": v(59.74, -25.8) * mm});
            skLineSegment(sketch, "E2644", {"start": v(59.74, -25.8) * mm, "end": v(59.8, -25.78) * mm});
            skLineSegment(sketch, "E2645", {"start": v(59.8, -25.78) * mm, "end": v(59.85, -25.76) * mm});
            skLineSegment(sketch, "E2646", {"start": v(59.85, -25.76) * mm, "end": v(59.92, -25.73) * mm});
            skLineSegment(sketch, "E2647", {"start": v(59.92, -25.73) * mm, "end": v(59.97, -25.71) * mm});
            skLineSegment(sketch, "E2648", {"start": v(59.97, -25.71) * mm, "end": v(60.04, -25.69) * mm});
            skLineSegment(sketch, "E2649", {"start": v(60.04, -25.69) * mm, "end": v(60.08, -25.67) * mm});
            skLineSegment(sketch, "E2650", {"start": v(60.08, -25.67) * mm, "end": v(60.15, -25.64) * mm});
            skLineSegment(sketch, "E2651", {"start": v(60.15, -25.64) * mm, "end": v(60.2, -25.63) * mm});
            skLineSegment(sketch, "E2652", {"start": v(60.2, -25.63) * mm, "end": v(60.27, -25.6) * mm});
            skLineSegment(sketch, "E2653", {"start": v(60.27, -25.6) * mm, "end": v(60.32, -25.6) * mm});
            skLineSegment(sketch, "E2654", {"start": v(60.32, -25.6) * mm, "end": v(60.39, -25.57) * mm});
            skLineSegment(sketch, "E2655", {"start": v(60.39, -25.57) * mm, "end": v(60.43, -25.56) * mm});
            skLineSegment(sketch, "E2656", {"start": v(60.43, -25.56) * mm, "end": v(60.5, -25.54) * mm});
            skLineSegment(sketch, "E2657", {"start": v(60.5, -25.54) * mm, "end": v(60.55, -25.52) * mm});
            skLineSegment(sketch, "E2658", {"start": v(60.55, -25.52) * mm, "end": v(60.62, -25.5) * mm});
            skLineSegment(sketch, "E2659", {"start": v(60.62, -25.5) * mm, "end": v(60.67, -25.5) * mm});
            skLineSegment(sketch, "E2660", {"start": v(60.67, -25.5) * mm, "end": v(60.74, -25.48) * mm});
            skLineSegment(sketch, "E2661", {"start": v(60.74, -25.48) * mm, "end": v(60.8, -25.47) * mm});
            skLineSegment(sketch, "E2662", {"start": v(60.8, -25.47) * mm, "end": v(60.86, -25.46) * mm});
            skLineSegment(sketch, "E2663", {"start": v(60.86, -25.46) * mm, "end": v(60.91, -25.45) * mm});
            skLineSegment(sketch, "E2664", {"start": v(60.91, -25.45) * mm, "end": v(60.98, -25.43) * mm});
            skLineSegment(sketch, "E2665", {"start": v(60.98, -25.43) * mm, "end": v(61.04, -25.43) * mm});
            skLineSegment(sketch, "E2666", {"start": v(61.04, -25.43) * mm, "end": v(61.1, -25.42) * mm});
            skLineSegment(sketch, "E2667", {"start": v(61.1, -25.42) * mm, "end": v(61.16, -25.4) * mm});
            skLineSegment(sketch, "E2668", {"start": v(61.16, -25.4) * mm, "end": v(61.23, -25.4) * mm});
            skLineSegment(sketch, "E2669", {"start": v(61.23, -25.4) * mm, "end": v(61.28, -25.4) * mm});
            skLineSegment(sketch, "E2670", {"start": v(61.28, -25.4) * mm, "end": v(61.35, -25.39) * mm});
            skLineSegment(sketch, "E2671", {"start": v(61.35, -25.39) * mm, "end": v(61.4, -25.38) * mm});
            skLineSegment(sketch, "E2672", {"start": v(61.4, -25.38) * mm, "end": v(61.47, -25.38) * mm});
            skLineSegment(sketch, "E2673", {"start": v(61.47, -25.38) * mm, "end": v(61.53, -25.38) * mm});
            skLineSegment(sketch, "E2674", {"start": v(61.53, -25.38) * mm, "end": v(61.6, -25.37) * mm});
            skLineSegment(sketch, "E2675", {"start": v(61.6, -25.37) * mm, "end": v(61.65, -25.37) * mm});
            skLineSegment(sketch, "E2676", {"start": v(61.65, -25.37) * mm, "end": v(61.72, -25.37) * mm});
            skLineSegment(sketch, "E2677", {"start": v(61.72, -25.37) * mm, "end": v(61.77, -25.37) * mm});
            skLineSegment(sketch, "E2678", {"start": v(61.77, -25.37) * mm, "end": v(61.84, -25.37) * mm});
            skLineSegment(sketch, "E2679", {"start": v(61.84, -25.37) * mm, "end": v(61.9, -25.37) * mm});
            skLineSegment(sketch, "E2680", {"start": v(61.9, -25.37) * mm, "end": v(61.97, -25.37) * mm});
            skLineSegment(sketch, "E2681", {"start": v(61.97, -25.37) * mm, "end": v(62.08, -25.38) * mm});
            skLineSegment(sketch, "E2682", {"start": v(62.08, -25.38) * mm, "end": v(62.12, -25.38) * mm});
            skLineSegment(sketch, "E2683", {"start": v(62.12, -25.38) * mm, "end": v(62.2, -25.39) * mm});
            skLineSegment(sketch, "E2684", {"start": v(62.2, -25.39) * mm, "end": v(62.24, -25.39) * mm});
            skLineSegment(sketch, "E2685", {"start": v(62.24, -25.39) * mm, "end": v(62.33, -25.4) * mm});
            skLineSegment(sketch, "E2686", {"start": v(62.33, -25.4) * mm, "end": v(62.37, -25.4) * mm});
            skLineSegment(sketch, "E2687", {"start": v(62.37, -25.4) * mm, "end": v(62.45, -25.41) * mm});
            skLineSegment(sketch, "E2688", {"start": v(62.45, -25.41) * mm, "end": v(62.49, -25.42) * mm});
            skLineSegment(sketch, "E2689", {"start": v(62.49, -25.42) * mm, "end": v(62.57, -25.43) * mm});
            skLineSegment(sketch, "E2690", {"start": v(62.57, -25.43) * mm, "end": v(62.6, -25.44) * mm});
            skLineSegment(sketch, "E2691", {"start": v(62.6, -25.44) * mm, "end": v(62.7, -25.45) * mm});
            skLineSegment(sketch, "E2692", {"start": v(62.7, -25.45) * mm, "end": v(62.73, -25.46) * mm});
            skLineSegment(sketch, "E2693", {"start": v(62.73, -25.46) * mm, "end": v(62.81, -25.47) * mm});
            skLineSegment(sketch, "E2694", {"start": v(62.81, -25.47) * mm, "end": v(62.85, -25.48) * mm});
            skLineSegment(sketch, "E2695", {"start": v(62.85, -25.48) * mm, "end": v(62.93, -25.5) * mm});
            skLineSegment(sketch, "E2696", {"start": v(62.93, -25.5) * mm, "end": v(62.97, -25.51) * mm});
            skLineSegment(sketch, "E2697", {"start": v(62.97, -25.51) * mm, "end": v(63.05, -25.53) * mm});
            skLineSegment(sketch, "E2698", {"start": v(63.05, -25.53) * mm, "end": v(63.1, -25.54) * mm});
            skLineSegment(sketch, "E2699", {"start": v(63.1, -25.54) * mm, "end": v(63.17, -25.56) * mm});
            skLineSegment(sketch, "E2700", {"start": v(63.17, -25.56) * mm, "end": v(63.2, -25.57) * mm});
            skLineSegment(sketch, "E2701", {"start": v(63.2, -25.57) * mm, "end": v(63.29, -25.6) * mm});
            skLineSegment(sketch, "E2702", {"start": v(63.29, -25.6) * mm, "end": v(63.33, -25.61) * mm});
            skLineSegment(sketch, "E2703", {"start": v(63.33, -25.61) * mm, "end": v(63.4, -25.64) * mm});
            skLineSegment(sketch, "E2704", {"start": v(63.4, -25.64) * mm, "end": v(63.44, -25.65) * mm});
            skLineSegment(sketch, "E2705", {"start": v(63.44, -25.65) * mm, "end": v(63.52, -25.68) * mm});
            skLineSegment(sketch, "E2706", {"start": v(63.52, -25.68) * mm, "end": v(63.56, -25.7) * mm});
            skLineSegment(sketch, "E2707", {"start": v(63.56, -25.7) * mm, "end": v(63.63, -25.72) * mm});
            skLineSegment(sketch, "E2708", {"start": v(63.63, -25.72) * mm, "end": v(63.67, -25.74) * mm});
            skLineSegment(sketch, "E2709", {"start": v(63.67, -25.74) * mm, "end": v(63.75, -25.77) * mm});
            skLineSegment(sketch, "E2710", {"start": v(63.75, -25.77) * mm, "end": v(63.79, -25.79) * mm});
            skLineSegment(sketch, "E2711", {"start": v(63.79, -25.79) * mm, "end": v(63.86, -25.82) * mm});
            skLineSegment(sketch, "E2712", {"start": v(63.86, -25.82) * mm, "end": v(63.9, -25.84) * mm});
            skLineSegment(sketch, "E2713", {"start": v(63.9, -25.84) * mm, "end": v(63.97, -25.87) * mm});
            skLineSegment(sketch, "E2714", {"start": v(63.97, -25.87) * mm, "end": v(64.01, -25.9) * mm});
            skLineSegment(sketch, "E2715", {"start": v(64.01, -25.9) * mm, "end": v(64.08, -25.92) * mm});
            skLineSegment(sketch, "E2716", {"start": v(64.08, -25.92) * mm, "end": v(64.12, -25.95) * mm});
            skLineSegment(sketch, "E2717", {"start": v(64.12, -25.95) * mm, "end": v(64.19, -25.98) * mm});
            skLineSegment(sketch, "E2718", {"start": v(64.19, -25.98) * mm, "end": v(64.23, -26) * mm});
            skLineSegment(sketch, "E2719", {"start": v(64.23, -26) * mm, "end": v(64.3, -26.04) * mm});
            skLineSegment(sketch, "E2720", {"start": v(64.3, -26.04) * mm, "end": v(64.34, -26.07) * mm});
            skLineSegment(sketch, "E2721", {"start": v(64.34, -26.07) * mm, "end": v(64.4, -26.1) * mm});
            skLineSegment(sketch, "E2722", {"start": v(64.4, -26.1) * mm, "end": v(64.44, -26.13) * mm});
            skLineSegment(sketch, "E2723", {"start": v(64.44, -26.13) * mm, "end": v(64.5, -26.17) * mm});
            skLineSegment(sketch, "E2724", {"start": v(64.5, -26.17) * mm, "end": v(64.55, -26.2) * mm});
            skLineSegment(sketch, "E2725", {"start": v(64.55, -26.2) * mm, "end": v(64.6, -26.24) * mm});
            skLineSegment(sketch, "E2726", {"start": v(64.6, -26.24) * mm, "end": v(64.65, -26.27) * mm});
            skLineSegment(sketch, "E2727", {"start": v(64.65, -26.27) * mm, "end": v(64.7, -26.3) * mm});
            skLineSegment(sketch, "E2728", {"start": v(64.7, -26.3) * mm, "end": v(64.75, -26.34) * mm});
            skLineSegment(sketch, "E2729", {"start": v(64.75, -26.34) * mm, "end": v(64.8, -26.38) * mm});
            skLineSegment(sketch, "E2730", {"start": v(64.8, -26.38) * mm, "end": v(64.85, -26.41) * mm});
            skLineSegment(sketch, "E2731", {"start": v(64.85, -26.41) * mm, "end": v(64.9, -26.46) * mm});
            skLineSegment(sketch, "E2732", {"start": v(64.9, -26.46) * mm, "end": v(64.94, -26.49) * mm});
            skLineSegment(sketch, "E2733", {"start": v(64.94, -26.49) * mm, "end": v(65, -26.54) * mm});
            skLineSegment(sketch, "E2734", {"start": v(65, -26.54) * mm, "end": v(65.04, -26.57) * mm});
            skLineSegment(sketch, "E2735", {"start": v(65.04, -26.57) * mm, "end": v(65.1, -26.62) * mm});
            skLineSegment(sketch, "E2736", {"start": v(65.1, -26.62) * mm, "end": v(65.13, -26.65) * mm});
            skLineSegment(sketch, "E2737", {"start": v(65.13, -26.65) * mm, "end": v(65.18, -26.7) * mm});
            skLineSegment(sketch, "E2738", {"start": v(65.18, -26.7) * mm, "end": v(65.22, -26.73) * mm});
            skLineSegment(sketch, "E2739", {"start": v(65.22, -26.73) * mm, "end": v(65.27, -26.78) * mm});
            skLineSegment(sketch, "E2740", {"start": v(65.27, -26.78) * mm, "end": v(65.3, -26.82) * mm});
            skLineSegment(sketch, "E2741", {"start": v(65.3, -26.82) * mm, "end": v(65.36, -26.87) * mm});
            skLineSegment(sketch, "E2742", {"start": v(65.36, -26.87) * mm, "end": v(65.4, -26.9) * mm});
            skLineSegment(sketch, "E2743", {"start": v(65.4, -26.9) * mm, "end": v(65.44, -26.96) * mm});
            skLineSegment(sketch, "E2744", {"start": v(65.44, -26.96) * mm, "end": v(65.48, -27) * mm});
            skLineSegment(sketch, "E2745", {"start": v(65.48, -27) * mm, "end": v(65.53, -27.05) * mm});
            skLineSegment(sketch, "E2746", {"start": v(65.53, -27.05) * mm, "end": v(65.56, -27.09) * mm});
            skLineSegment(sketch, "E2747", {"start": v(65.56, -27.09) * mm, "end": v(65.6, -27.14) * mm});
            skLineSegment(sketch, "E2748", {"start": v(65.6, -27.14) * mm, "end": v(65.64, -27.18) * mm});
            skLineSegment(sketch, "E2749", {"start": v(65.64, -27.18) * mm, "end": v(65.68, -27.23) * mm});
            skLineSegment(sketch, "E2750", {"start": v(65.68, -27.23) * mm, "end": v(65.72, -27.28) * mm});
            skLineSegment(sketch, "E2751", {"start": v(65.72, -27.28) * mm, "end": v(65.76, -27.33) * mm});
            skLineSegment(sketch, "E2752", {"start": v(65.76, -27.33) * mm, "end": v(65.8, -27.37) * mm});
            skLineSegment(sketch, "E2753", {"start": v(65.8, -27.37) * mm, "end": v(65.83, -27.43) * mm});
            skLineSegment(sketch, "E2754", {"start": v(65.83, -27.43) * mm, "end": v(65.87, -27.47) * mm});
            skLineSegment(sketch, "E2755", {"start": v(65.87, -27.47) * mm, "end": v(65.9, -27.53) * mm});
            skLineSegment(sketch, "E2756", {"start": v(65.9, -27.53) * mm, "end": v(65.94, -27.58) * mm});
            skLineSegment(sketch, "E2757", {"start": v(65.94, -27.58) * mm, "end": v(65.97, -27.63) * mm});
            skLineSegment(sketch, "E2758", {"start": v(65.97, -27.63) * mm, "end": v(66, -27.68) * mm});
            skLineSegment(sketch, "E2759", {"start": v(66, -27.68) * mm, "end": v(66.04, -27.73) * mm});
            skLineSegment(sketch, "E2760", {"start": v(66.04, -27.73) * mm, "end": v(66.07, -27.78) * mm});
            skLineSegment(sketch, "E2761", {"start": v(66.07, -27.78) * mm, "end": v(66.1, -27.84) * mm});
            skLineSegment(sketch, "E2762", {"start": v(66.1, -27.84) * mm, "end": v(66.13, -27.89) * mm});
            skLineSegment(sketch, "E2763", {"start": v(66.13, -27.89) * mm, "end": v(66.16, -27.95) * mm});
            skLineSegment(sketch, "E2764", {"start": v(66.16, -27.95) * mm, "end": v(66.18, -27.97) * mm});
            skLineSegment(sketch, "E2765", {"start": v(66.18, -27.97) * mm, "end": v(66.2, -28) * mm});
            skLineSegment(sketch, "E2766", {"start": v(66.2, -28) * mm, "end": v(66.47, -27.72) * mm});
            skLineSegment(sketch, "E2767", {"start": v(66.47, -27.72) * mm, "end": v(67.08, -27.11) * mm});
            skLineSegment(sketch, "E2768", {"start": v(67.08, -27.11) * mm, "end": v(67.18, -27) * mm});
            skLineSegment(sketch, "E2769", {"start": v(67.18, -27) * mm, "end": v(67.53, -26.65) * mm});
            skLineSegment(sketch, "E2770", {"start": v(67.53, -26.65) * mm, "end": v(67.64, -26.53) * mm});
            skLineSegment(sketch, "E2771", {"start": v(67.64, -26.53) * mm, "end": v(67.86, -26.3) * mm});
            skLineSegment(sketch, "E2772", {"start": v(67.86, -26.3) * mm, "end": v(68.19, -25.92) * mm});
            skLineSegment(sketch, "E2773", {"start": v(68.19, -25.92) * mm, "end": v(68.65, -25.41) * mm});
            skLineSegment(sketch, "E2774", {"start": v(68.65, -25.41) * mm, "end": v(68.87, -25.15) * mm});
            skLineSegment(sketch, "E2775", {"start": v(68.87, -25.15) * mm, "end": v(69.23, -24.72) * mm});
            skLineSegment(sketch, "E2776", {"start": v(69.23, -24.72) * mm, "end": v(69.45, -24.44) * mm});
            skLineSegment(sketch, "E2777", {"start": v(69.45, -24.44) * mm, "end": v(69.8, -24) * mm});
            skLineSegment(sketch, "E2778", {"start": v(69.8, -24) * mm, "end": v(70, -23.73) * mm});
            skLineSegment(sketch, "E2779", {"start": v(70, -23.73) * mm, "end": v(70.35, -23.29) * mm});
            skLineSegment(sketch, "E2780", {"start": v(70.35, -23.29) * mm, "end": v(70.55, -23) * mm});
            skLineSegment(sketch, "E2781", {"start": v(70.55, -23) * mm, "end": v(70.88, -22.55) * mm});
            skLineSegment(sketch, "E2782", {"start": v(70.88, -22.55) * mm, "end": v(71.08, -22.26) * mm});
            skLineSegment(sketch, "E2783", {"start": v(71.08, -22.26) * mm, "end": v(71.4, -21.8) * mm});
            skLineSegment(sketch, "E2784", {"start": v(71.4, -21.8) * mm, "end": v(71.58, -21.5) * mm});
            skLineSegment(sketch, "E2785", {"start": v(71.58, -21.5) * mm, "end": v(71.89, -21.04) * mm});
            skLineSegment(sketch, "E2786", {"start": v(71.89, -21.04) * mm, "end": v(72.07, -20.74) * mm});
            skLineSegment(sketch, "E2787", {"start": v(72.07, -20.74) * mm, "end": v(72.36, -20.27) * mm});
            skLineSegment(sketch, "E2788", {"start": v(72.36, -20.27) * mm, "end": v(72.54, -19.97) * mm});
            skLineSegment(sketch, "E2789", {"start": v(72.54, -19.97) * mm, "end": v(72.82, -19.48) * mm});
            skLineSegment(sketch, "E2790", {"start": v(72.82, -19.48) * mm, "end": v(72.99, -19.18) * mm});
            skLineSegment(sketch, "E2791", {"start": v(72.99, -19.18) * mm, "end": v(73.26, -18.69) * mm});
            skLineSegment(sketch, "E2792", {"start": v(73.26, -18.69) * mm, "end": v(73.52, -18.19) * mm});
            skLineSegment(sketch, "E2793", {"start": v(73.52, -18.19) * mm, "end": v(73.68, -17.88) * mm});
            skLineSegment(sketch, "E2794", {"start": v(73.68, -17.88) * mm, "end": v(73.83, -17.57) * mm});
            skLineSegment(sketch, "E2795", {"start": v(73.83, -17.57) * mm, "end": v(74.08, -17.06) * mm});
            skLineSegment(sketch, "E2796", {"start": v(74.08, -17.06) * mm, "end": v(74.22, -16.75) * mm});
            skLineSegment(sketch, "E2797", {"start": v(74.22, -16.75) * mm, "end": v(74.45, -16.24) * mm});
            skLineSegment(sketch, "E2798", {"start": v(74.45, -16.24) * mm, "end": v(74.6, -15.92) * mm});
            skLineSegment(sketch, "E2799", {"start": v(74.6, -15.92) * mm, "end": v(74.81, -15.4) * mm});
            skLineSegment(sketch, "E2800", {"start": v(74.81, -15.4) * mm, "end": v(75.02, -14.88) * mm});
            skLineSegment(sketch, "E2801", {"start": v(75.02, -14.88) * mm, "end": v(75.15, -14.56) * mm});
            skLineSegment(sketch, "E2802", {"start": v(75.15, -14.56) * mm, "end": v(75.34, -14.04) * mm});
            skLineSegment(sketch, "E2803", {"start": v(75.34, -14.04) * mm, "end": v(75.47, -13.7) * mm});
            skLineSegment(sketch, "E2804", {"start": v(75.47, -13.7) * mm, "end": v(75.58, -13.38) * mm});
            skLineSegment(sketch, "E2805", {"start": v(75.58, -13.38) * mm, "end": v(75.76, -12.85) * mm});
            skLineSegment(sketch, "E2806", {"start": v(75.76, -12.85) * mm, "end": v(75.87, -12.52) * mm});
            skLineSegment(sketch, "E2807", {"start": v(75.87, -12.52) * mm, "end": v(76.04, -11.98) * mm});
            skLineSegment(sketch, "E2808", {"start": v(76.04, -11.98) * mm, "end": v(76.2, -11.45) * mm});
            skLineSegment(sketch, "E2809", {"start": v(76.2, -11.45) * mm, "end": v(76.29, -11.11) * mm});
            skLineSegment(sketch, "E2810", {"start": v(76.29, -11.11) * mm, "end": v(76.43, -10.57) * mm});
            skLineSegment(sketch, "E2811", {"start": v(76.43, -10.57) * mm, "end": v(76.52, -10.23) * mm});
            skLineSegment(sketch, "E2812", {"start": v(76.52, -10.23) * mm, "end": v(76.6, -9.9) * mm});
            skLineSegment(sketch, "E2813", {"start": v(76.6, -9.9) * mm, "end": v(76.73, -9.35) * mm});
            skLineSegment(sketch, "E2814", {"start": v(76.73, -9.35) * mm, "end": v(76.8, -9.01) * mm});
            skLineSegment(sketch, "E2815", {"start": v(76.8, -9.01) * mm, "end": v(76.92, -8.46) * mm});
            skLineSegment(sketch, "E2816", {"start": v(76.92, -8.46) * mm, "end": v(77.02, -7.91) * mm});
            skLineSegment(sketch, "E2817", {"start": v(77.02, -7.91) * mm, "end": v(77.08, -7.57) * mm});
            skLineSegment(sketch, "E2818", {"start": v(77.08, -7.57) * mm, "end": v(77.14, -7.23) * mm});
            skLineSegment(sketch, "E2819", {"start": v(77.14, -7.23) * mm, "end": v(77.23, -6.67) * mm});
            skLineSegment(sketch, "E2820", {"start": v(77.23, -6.67) * mm, "end": v(77.28, -6.33) * mm});
            skLineSegment(sketch, "E2821", {"start": v(77.28, -6.33) * mm, "end": v(77.35, -5.77) * mm});
            skLineSegment(sketch, "E2822", {"start": v(77.35, -5.77) * mm, "end": v(77.41, -5.22) * mm});
            skLineSegment(sketch, "E2823", {"start": v(77.41, -5.22) * mm, "end": v(77.45, -4.87) * mm});
            skLineSegment(sketch, "E2824", {"start": v(77.45, -4.87) * mm, "end": v(77.5, -4.31) * mm});
            skLineSegment(sketch, "E2825", {"start": v(77.5, -4.31) * mm, "end": v(77.53, -3.97) * mm});
            skLineSegment(sketch, "E2826", {"start": v(77.53, -3.97) * mm, "end": v(77.55, -3.62) * mm});
            skLineSegment(sketch, "E2827", {"start": v(77.55, -3.62) * mm, "end": v(77.61, -1.9) * mm});
            skLineSegment(sketch, "E2828", {"start": v(77.61, -1.9) * mm, "end": v(77.62, -1.57) * mm});
            skLineSegment(sketch, "E2829", {"start": v(77.62, -1.57) * mm, "end": v(77.63, -1.24) * mm});
            skLineSegment(sketch, "E2830", {"start": v(77.63, -1.24) * mm, "end": v(77.63, -1.14) * mm});
            skLineSegment(sketch, "E2831", {"start": v(77.63, -1.14) * mm, "end": v(77.62, -0.87) * mm});
            skLineSegment(sketch, "E2832", {"start": v(77.62, -0.87) * mm, "end": v(77.62, -0.63) * mm});
            skLineSegment(sketch, "E2833", {"start": v(77.62, -0.63) * mm, "end": v(77.62, -0.34) * mm});
            skLineSegment(sketch, "E2834", {"start": v(77.62, -0.34) * mm, "end": v(77.62, -0.26) * mm});
            skLineSegment(sketch, "E2835", {"start": v(77.62, -0.26) * mm, "end": v(77.6, 0.07) * mm});
            skLineSegment(sketch, "E2836", {"start": v(77.6, 0.07) * mm, "end": v(77.6, 0.28) * mm});
            skLineSegment(sketch, "E2837", {"start": v(77.6, 0.28) * mm, "end": v(77.58, 0.57) * mm});
            skLineSegment(sketch, "E2838", {"start": v(77.58, 0.57) * mm, "end": v(77.58, 0.7) * mm});
            skLineSegment(sketch, "E2839", {"start": v(77.58, 0.7) * mm, "end": v(77.56, 0.99) * mm});
            skLineSegment(sketch, "E2840", {"start": v(77.56, 0.99) * mm, "end": v(77.48, 1.75) * mm});
            skLineSegment(sketch, "E2841", {"start": v(77.48, 1.75) * mm, "end": v(77.47, 2.06) * mm});
            skLineSegment(sketch, "E2842", {"start": v(77.47, 2.06) * mm, "end": v(77.46, 2.2) * mm});
            skLineSegment(sketch, "E2843", {"start": v(77.46, 2.2) * mm, "end": v(77.44, 2.37) * mm});
            skLineSegment(sketch, "E2844", {"start": v(77.44, 2.37) * mm, "end": v(77.42, 2.65) * mm});
            skLineSegment(sketch, "E2845", {"start": v(77.42, 2.65) * mm, "end": v(77.4, 2.78) * mm});
            skLineSegment(sketch, "E2846", {"start": v(77.4, 2.78) * mm, "end": v(77.4, 2.9) * mm});
            skLineSegment(sketch, "E2847", {"start": v(77.4, 2.9) * mm, "end": v(77.35, 3.3) * mm});
            skLineSegment(sketch, "E2848", {"start": v(77.35, 3.3) * mm, "end": v(77.34, 3.33) * mm});
            skLineSegment(sketch, "E2849", {"start": v(77.34, 3.33) * mm, "end": v(77.29, 3.8) * mm});
            skLineSegment(sketch, "E2850", {"start": v(77.29, 3.8) * mm, "end": v(77.23, 4.18) * mm});
            skLineSegment(sketch, "E2851", {"start": v(77.23, 4.18) * mm, "end": v(77.13, 4.82) * mm});
            skLineSegment(sketch, "E2852", {"start": v(77.13, 4.82) * mm, "end": v(77.06, 5.24) * mm});
            skLineSegment(sketch, "E2853", {"start": v(77.06, 5.24) * mm, "end": v(77.04, 5.38) * mm});
            skLineSegment(sketch, "E2854", {"start": v(77.04, 5.38) * mm, "end": v(76.95, 5.33) * mm});
            skLineSegment(sketch, "E2855", {"start": v(76.95, 5.33) * mm, "end": v(76.89, 5.3) * mm});
            skLineSegment(sketch, "E2856", {"start": v(76.89, 5.3) * mm, "end": v(76.82, 5.28) * mm});
            skLineSegment(sketch, "E2857", {"start": v(76.82, 5.28) * mm, "end": v(76.76, 5.26) * mm});
            skLineSegment(sketch, "E2858", {"start": v(76.76, 5.26) * mm, "end": v(76.7, 5.24) * mm});
            skLineSegment(sketch, "E2859", {"start": v(76.7, 5.24) * mm, "end": v(76.62, 5.22) * mm});
            skLineSegment(sketch, "E2860", {"start": v(76.62, 5.22) * mm, "end": v(76.55, 5.2) * mm});
            skLineSegment(sketch, "E2861", {"start": v(76.55, 5.2) * mm, "end": v(76.48, 5.18) * mm});
            skLineSegment(sketch, "E2862", {"start": v(76.48, 5.18) * mm, "end": v(76.41, 5.16) * mm});
            skLineSegment(sketch, "E2863", {"start": v(76.41, 5.16) * mm, "end": v(76.34, 5.14) * mm});
            skLineSegment(sketch, "E2864", {"start": v(76.34, 5.14) * mm, "end": v(76.26, 5.13) * mm});
            skLineSegment(sketch, "E2865", {"start": v(76.26, 5.13) * mm, "end": v(76.19, 5.12) * mm});
            skLineSegment(sketch, "E2866", {"start": v(76.19, 5.12) * mm, "end": v(76.11, 5.1) * mm});
            skLineSegment(sketch, "E2867", {"start": v(76.11, 5.1) * mm, "end": v(76.03, 5.1) * mm});
            skLineSegment(sketch, "E2868", {"start": v(76.03, 5.1) * mm, "end": v(75.95, 5.09) * mm});
            skLineSegment(sketch, "E2869", {"start": v(75.95, 5.09) * mm, "end": v(75.87, 5.08) * mm});
            skLineSegment(sketch, "E2870", {"start": v(75.87, 5.08) * mm, "end": v(75.8, 5.08) * mm});
            skLineSegment(sketch, "E2871", {"start": v(75.8, 5.08) * mm, "end": v(75.7, 5.08) * mm});
            skLineSegment(sketch, "E2872", {"start": v(75.7, 5.08) * mm, "end": v(75.62, 5.08) * mm});
            skLineSegment(sketch, "E2873", {"start": v(75.62, 5.08) * mm, "end": v(75.54, 5.08) * mm});
            skLineSegment(sketch, "E2874", {"start": v(75.54, 5.08) * mm, "end": v(75.45, 5.08) * mm});
            skLineSegment(sketch, "E2875", {"start": v(75.45, 5.08) * mm, "end": v(75.39, 5.05) * mm});
            skLineSegment(sketch, "E2876", {"start": v(75.39, 5.05) * mm, "end": v(75.3, 5.06) * mm});
            skLineSegment(sketch, "E2877", {"start": v(75.3, 5.06) * mm, "end": v(75.26, 5.04) * mm});
            skLineSegment(sketch, "E2878", {"start": v(75.26, 5.04) * mm, "end": v(75.17, 5.04) * mm});
            skLineSegment(sketch, "E2879", {"start": v(75.17, 5.04) * mm, "end": v(75.13, 5.03) * mm});
            skLineSegment(sketch, "E2880", {"start": v(75.13, 5.03) * mm, "end": v(75.04, 5.04) * mm});
            skLineSegment(sketch, "E2881", {"start": v(75.04, 5.04) * mm, "end": v(75, 5.02) * mm});
            skLineSegment(sketch, "E2882", {"start": v(75, 5.02) * mm, "end": v(74.91, 5.03) * mm});
            skLineSegment(sketch, "E2883", {"start": v(74.91, 5.03) * mm, "end": v(74.87, 5.02) * mm});
            skLineSegment(sketch, "E2884", {"start": v(74.87, 5.02) * mm, "end": v(74.83, 5) * mm});
            skLineSegment(sketch, "E2885", {"start": v(74.83, 5) * mm, "end": v(74.74, 5.02) * mm});
            skLineSegment(sketch, "E2886", {"start": v(74.74, 5.02) * mm, "end": v(74.7, 5) * mm});
            skLineSegment(sketch, "E2887", {"start": v(74.7, 5) * mm, "end": v(74.61, 5.02) * mm});
            skLineSegment(sketch, "E2888", {"start": v(74.61, 5.02) * mm, "end": v(74.57, 5.01) * mm});
            skLineSegment(sketch, "E2889", {"start": v(74.57, 5.01) * mm, "end": v(74.53, 5) * mm});
            skLineSegment(sketch, "E2890", {"start": v(74.53, 5) * mm, "end": v(74.44, 5.02) * mm});
            skLineSegment(sketch, "E2891", {"start": v(74.44, 5.02) * mm, "end": v(74.4, 5.01) * mm});
            skLineSegment(sketch, "E2892", {"start": v(74.4, 5.01) * mm, "end": v(74.36, 5) * mm});
            skLineSegment(sketch, "E2893", {"start": v(74.36, 5) * mm, "end": v(74.27, 5.03) * mm});
            skLineSegment(sketch, "E2894", {"start": v(74.27, 5.03) * mm, "end": v(74.23, 5.02) * mm});
            skLineSegment(sketch, "E2895", {"start": v(74.23, 5.02) * mm, "end": v(74.14, 5.04) * mm});
            skLineSegment(sketch, "E2896", {"start": v(74.14, 5.04) * mm, "end": v(74.1, 5.04) * mm});
            skLineSegment(sketch, "E2897", {"start": v(74.1, 5.04) * mm, "end": v(74.01, 5.06) * mm});
            skLineSegment(sketch, "E2898", {"start": v(74.01, 5.06) * mm, "end": v(73.97, 5.06) * mm});
            skLineSegment(sketch, "E2899", {"start": v(73.97, 5.06) * mm, "end": v(73.93, 5.06) * mm});
            skLineSegment(sketch, "E2900", {"start": v(73.93, 5.06) * mm, "end": v(73.84, 5.08) * mm});
            skLineSegment(sketch, "E2901", {"start": v(73.84, 5.08) * mm, "end": v(73.8, 5.08) * mm});
            skLineSegment(sketch, "E2902", {"start": v(73.8, 5.08) * mm, "end": v(73.72, 5.11) * mm});
            skLineSegment(sketch, "E2903", {"start": v(73.72, 5.11) * mm, "end": v(73.68, 5.11) * mm});
            skLineSegment(sketch, "E2904", {"start": v(73.68, 5.11) * mm, "end": v(73.64, 5.11) * mm});
            skLineSegment(sketch, "E2905", {"start": v(73.64, 5.11) * mm, "end": v(73.55, 5.14) * mm});
            skLineSegment(sketch, "E2906", {"start": v(73.55, 5.14) * mm, "end": v(73.51, 5.14) * mm});
            skLineSegment(sketch, "E2907", {"start": v(73.51, 5.14) * mm, "end": v(73.43, 5.18) * mm});
            skLineSegment(sketch, "E2908", {"start": v(73.43, 5.18) * mm, "end": v(73.39, 5.18) * mm});
            skLineSegment(sketch, "E2909", {"start": v(73.39, 5.18) * mm, "end": v(73.35, 5.18) * mm});
            skLineSegment(sketch, "E2910", {"start": v(73.35, 5.18) * mm, "end": v(73.27, 5.22) * mm});
            skLineSegment(sketch, "E2911", {"start": v(73.27, 5.22) * mm, "end": v(73.23, 5.22) * mm});
            skLineSegment(sketch, "E2912", {"start": v(73.23, 5.22) * mm, "end": v(73.15, 5.26) * mm});
            skLineSegment(sketch, "E2913", {"start": v(73.15, 5.26) * mm, "end": v(73.1, 5.27) * mm});
            skLineSegment(sketch, "E2914", {"start": v(73.1, 5.27) * mm, "end": v(73.07, 5.27) * mm});
            skLineSegment(sketch, "E2915", {"start": v(73.07, 5.27) * mm, "end": v(72.99, 5.31) * mm});
            skLineSegment(sketch, "E2916", {"start": v(72.99, 5.31) * mm, "end": v(72.95, 5.32) * mm});
            skLineSegment(sketch, "E2917", {"start": v(72.95, 5.32) * mm, "end": v(72.87, 5.36) * mm});
            skLineSegment(sketch, "E2918", {"start": v(72.87, 5.36) * mm, "end": v(72.83, 5.37) * mm});
            skLineSegment(sketch, "E2919", {"start": v(72.83, 5.37) * mm, "end": v(72.8, 5.38) * mm});
            skLineSegment(sketch, "E2920", {"start": v(72.8, 5.38) * mm, "end": v(72.72, 5.43) * mm});
            skLineSegment(sketch, "E2921", {"start": v(72.72, 5.43) * mm, "end": v(72.68, 5.43) * mm});
            skLineSegment(sketch, "E2922", {"start": v(72.68, 5.43) * mm, "end": v(72.6, 5.48) * mm});
            skLineSegment(sketch, "E2923", {"start": v(72.6, 5.48) * mm, "end": v(72.57, 5.5) * mm});
            skLineSegment(sketch, "E2924", {"start": v(72.57, 5.5) * mm, "end": v(72.49, 5.54) * mm});
            skLineSegment(sketch, "E2925", {"start": v(72.49, 5.54) * mm, "end": v(72.46, 5.55) * mm});
            skLineSegment(sketch, "E2926", {"start": v(72.46, 5.55) * mm, "end": v(72.42, 5.56) * mm});
            skLineSegment(sketch, "E2927", {"start": v(72.42, 5.56) * mm, "end": v(72.39, 5.57) * mm});
            skLineSegment(sketch, "E2928", {"start": v(72.39, 5.57) * mm, "end": v(72.35, 5.59) * mm});
            skLineSegment(sketch, "E2929", {"start": v(72.35, 5.59) * mm, "end": v(72.32, 5.6) * mm});
            skLineSegment(sketch, "E2930", {"start": v(72.32, 5.6) * mm, "end": v(72.29, 5.61) * mm});
            skLineSegment(sketch, "E2931", {"start": v(72.29, 5.61) * mm, "end": v(72.02, 5.77) * mm});
            skLineSegment(sketch, "E2932", {"start": v(72.02, 5.77) * mm, "end": v(71.97, 5.8) * mm});
            skLineSegment(sketch, "E2933", {"start": v(71.97, 5.8) * mm, "end": v(71.91, 5.85) * mm});
            skLineSegment(sketch, "E2934", {"start": v(71.91, 5.85) * mm, "end": v(71.86, 5.89) * mm});
            skLineSegment(sketch, "E2935", {"start": v(71.86, 5.89) * mm, "end": v(71.8, 5.93) * mm});
            skLineSegment(sketch, "E2936", {"start": v(71.8, 5.93) * mm, "end": v(71.75, 5.98) * mm});
            skLineSegment(sketch, "E2937", {"start": v(71.75, 5.98) * mm, "end": v(71.7, 6.02) * mm});
            skLineSegment(sketch, "E2938", {"start": v(71.7, 6.02) * mm, "end": v(71.65, 6.07) * mm});
            skLineSegment(sketch, "E2939", {"start": v(71.65, 6.07) * mm, "end": v(71.6, 6.12) * mm});
            skLineSegment(sketch, "E2940", {"start": v(71.6, 6.12) * mm, "end": v(71.55, 6.15) * mm});
            skLineSegment(sketch, "E2941", {"start": v(71.55, 6.15) * mm, "end": v(71.51, 6.19) * mm});
            skLineSegment(sketch, "E2942", {"start": v(71.51, 6.19) * mm, "end": v(71.47, 6.22) * mm});
            skLineSegment(sketch, "E2943", {"start": v(71.47, 6.22) * mm, "end": v(71.42, 6.27) * mm});
            skLineSegment(sketch, "E2944", {"start": v(71.42, 6.27) * mm, "end": v(71.38, 6.3) * mm});
            skLineSegment(sketch, "E2945", {"start": v(71.38, 6.3) * mm, "end": v(71.33, 6.36) * mm});
            skLineSegment(sketch, "E2946", {"start": v(71.33, 6.36) * mm, "end": v(71.3, 6.4) * mm});
            skLineSegment(sketch, "E2947", {"start": v(71.3, 6.4) * mm, "end": v(71.24, 6.45) * mm});
            skLineSegment(sketch, "E2948", {"start": v(71.24, 6.45) * mm, "end": v(71.2, 6.48) * mm});
            skLineSegment(sketch, "E2949", {"start": v(71.2, 6.48) * mm, "end": v(71.16, 6.54) * mm});
            skLineSegment(sketch, "E2950", {"start": v(71.16, 6.54) * mm, "end": v(71.12, 6.58) * mm});
            skLineSegment(sketch, "E2951", {"start": v(71.12, 6.58) * mm, "end": v(71.09, 6.61) * mm});
            skLineSegment(sketch, "E2952", {"start": v(71.09, 6.61) * mm, "end": v(71.04, 6.67) * mm});
            skLineSegment(sketch, "E2953", {"start": v(71.04, 6.67) * mm, "end": v(71, 6.7) * mm});
            skLineSegment(sketch, "E2954", {"start": v(71, 6.7) * mm, "end": v(70.96, 6.77) * mm});
            skLineSegment(sketch, "E2955", {"start": v(70.96, 6.77) * mm, "end": v(70.93, 6.8) * mm});
            skLineSegment(sketch, "E2956", {"start": v(70.93, 6.8) * mm, "end": v(70.89, 6.86) * mm});
            skLineSegment(sketch, "E2957", {"start": v(70.89, 6.86) * mm, "end": v(70.86, 6.9) * mm});
            skLineSegment(sketch, "E2958", {"start": v(70.86, 6.9) * mm, "end": v(70.81, 6.96) * mm});
            skLineSegment(sketch, "E2959", {"start": v(70.81, 6.96) * mm, "end": v(70.78, 7) * mm});
            skLineSegment(sketch, "E2960", {"start": v(70.78, 7) * mm, "end": v(70.75, 7.04) * mm});
            skLineSegment(sketch, "E2961", {"start": v(70.75, 7.04) * mm, "end": v(70.71, 7.1) * mm});
            skLineSegment(sketch, "E2962", {"start": v(70.71, 7.1) * mm, "end": v(70.68, 7.14) * mm});
            skLineSegment(sketch, "E2963", {"start": v(70.68, 7.14) * mm, "end": v(70.65, 7.2) * mm});
            skLineSegment(sketch, "E2964", {"start": v(70.65, 7.2) * mm, "end": v(70.62, 7.25) * mm});
            skLineSegment(sketch, "E2965", {"start": v(70.62, 7.25) * mm, "end": v(70.58, 7.31) * mm});
            skLineSegment(sketch, "E2966", {"start": v(70.58, 7.31) * mm, "end": v(70.55, 7.35) * mm});
            skLineSegment(sketch, "E2967", {"start": v(70.55, 7.35) * mm, "end": v(70.53, 7.4) * mm});
            skLineSegment(sketch, "E2968", {"start": v(70.53, 7.4) * mm, "end": v(70.5, 7.46) * mm});
            skLineSegment(sketch, "E2969", {"start": v(70.5, 7.46) * mm, "end": v(70.47, 7.5) * mm});
            skLineSegment(sketch, "E2970", {"start": v(70.47, 7.5) * mm, "end": v(70.43, 7.57) * mm});
            skLineSegment(sketch, "E2971", {"start": v(70.43, 7.57) * mm, "end": v(70.41, 7.61) * mm});
            skLineSegment(sketch, "E2972", {"start": v(70.41, 7.61) * mm, "end": v(70.38, 7.68) * mm});
            skLineSegment(sketch, "E2973", {"start": v(70.38, 7.68) * mm, "end": v(70.36, 7.72) * mm});
            skLineSegment(sketch, "E2974", {"start": v(70.36, 7.72) * mm, "end": v(70.33, 7.79) * mm});
            skLineSegment(sketch, "E2975", {"start": v(70.33, 7.79) * mm, "end": v(70.3, 7.83) * mm});
            skLineSegment(sketch, "E2976", {"start": v(70.3, 7.83) * mm, "end": v(70.27, 7.9) * mm});
            skLineSegment(sketch, "E2977", {"start": v(70.27, 7.9) * mm, "end": v(70.26, 7.94) * mm});
            skLineSegment(sketch, "E2978", {"start": v(70.26, 7.94) * mm, "end": v(70.24, 7.99) * mm});
            skLineSegment(sketch, "E2979", {"start": v(70.24, 7.99) * mm, "end": v(70.2, 8.06) * mm});
            skLineSegment(sketch, "E2980", {"start": v(70.2, 8.06) * mm, "end": v(70.2, 8.1) * mm});
            skLineSegment(sketch, "E2981", {"start": v(70.2, 8.1) * mm, "end": v(70.17, 8.17) * mm});
            skLineSegment(sketch, "E2982", {"start": v(70.17, 8.17) * mm, "end": v(70.15, 8.22) * mm});
            skLineSegment(sketch, "E2983", {"start": v(70.15, 8.22) * mm, "end": v(70.13, 8.3) * mm});
            skLineSegment(sketch, "E2984", {"start": v(70.13, 8.3) * mm, "end": v(70.11, 8.34) * mm});
            skLineSegment(sketch, "E2985", {"start": v(70.11, 8.34) * mm, "end": v(70.1, 8.38) * mm});
            skLineSegment(sketch, "E2986", {"start": v(70.1, 8.38) * mm, "end": v(70.07, 8.45) * mm});
            skLineSegment(sketch, "E2987", {"start": v(70.07, 8.45) * mm, "end": v(70.06, 8.5) * mm});
            skLineSegment(sketch, "E2988", {"start": v(70.06, 8.5) * mm, "end": v(70.04, 8.57) * mm});
            skLineSegment(sketch, "E2989", {"start": v(70.04, 8.57) * mm, "end": v(70.03, 8.62) * mm});
            skLineSegment(sketch, "E2990", {"start": v(70.03, 8.62) * mm, "end": v(70.01, 8.69) * mm});
            skLineSegment(sketch, "E2991", {"start": v(70.01, 8.69) * mm, "end": v(70, 8.74) * mm});
            skLineSegment(sketch, "E2992", {"start": v(70, 8.74) * mm, "end": v(69.98, 8.8) * mm});
            skLineSegment(sketch, "E2993", {"start": v(69.98, 8.8) * mm, "end": v(69.97, 8.86) * mm});
            skLineSegment(sketch, "E2994", {"start": v(69.97, 8.86) * mm, "end": v(69.96, 8.93) * mm});
            skLineSegment(sketch, "E2995", {"start": v(69.96, 8.93) * mm, "end": v(69.95, 8.98) * mm});
            skLineSegment(sketch, "E2996", {"start": v(69.95, 8.98) * mm, "end": v(69.94, 9.05) * mm});
            skLineSegment(sketch, "E2997", {"start": v(69.94, 9.05) * mm, "end": v(69.93, 9.1) * mm});
            skLineSegment(sketch, "E2998", {"start": v(69.93, 9.1) * mm, "end": v(69.92, 9.17) * mm});
            skLineSegment(sketch, "E2999", {"start": v(69.92, 9.17) * mm, "end": v(69.91, 9.22) * mm});
            skLineSegment(sketch, "E3000", {"start": v(69.91, 9.22) * mm, "end": v(69.9, 9.3) * mm});
            skLineSegment(sketch, "E3001", {"start": v(69.9, 9.3) * mm, "end": v(69.9, 9.34) * mm});
            skLineSegment(sketch, "E3002", {"start": v(69.9, 9.34) * mm, "end": v(69.89, 9.41) * mm});
            skLineSegment(sketch, "E3003", {"start": v(69.89, 9.41) * mm, "end": v(69.88, 9.46) * mm});
            skLineSegment(sketch, "E3004", {"start": v(69.88, 9.46) * mm, "end": v(69.88, 9.54) * mm});
            skLineSegment(sketch, "E3005", {"start": v(69.88, 9.54) * mm, "end": v(69.88, 9.59) * mm});
            skLineSegment(sketch, "E3006", {"start": v(69.88, 9.59) * mm, "end": v(69.87, 9.66) * mm});
            skLineSegment(sketch, "E3007", {"start": v(69.87, 9.66) * mm, "end": v(69.87, 9.7) * mm});
            skLineSegment(sketch, "E3008", {"start": v(69.87, 9.7) * mm, "end": v(69.87, 9.78) * mm});
            skLineSegment(sketch, "E3009", {"start": v(69.87, 9.78) * mm, "end": v(69.87, 9.83) * mm});
            skLineSegment(sketch, "E3010", {"start": v(69.87, 9.83) * mm, "end": v(69.87, 9.9) * mm});
            skLineSegment(sketch, "E3011", {"start": v(69.87, 9.9) * mm, "end": v(69.87, 9.96) * mm});
            skLineSegment(sketch, "E3012", {"start": v(69.87, 9.96) * mm, "end": v(69.87, 10.03) * mm});
            skLineSegment(sketch, "E3013", {"start": v(69.87, 10.03) * mm, "end": v(69.87, 10.08) * mm});
            skLineSegment(sketch, "E3014", {"start": v(69.87, 10.08) * mm, "end": v(69.87, 10.15) * mm});
            skLineSegment(sketch, "E3015", {"start": v(69.87, 10.15) * mm, "end": v(69.88, 10.2) * mm});
            skLineSegment(sketch, "E3016", {"start": v(69.88, 10.2) * mm, "end": v(69.88, 10.27) * mm});
            skLineSegment(sketch, "E3017", {"start": v(69.88, 10.27) * mm, "end": v(69.89, 10.32) * mm});
            skLineSegment(sketch, "E3018", {"start": v(69.89, 10.32) * mm, "end": v(69.9, 10.4) * mm});
            skLineSegment(sketch, "E3019", {"start": v(69.9, 10.4) * mm, "end": v(69.9, 10.45) * mm});
            skLineSegment(sketch, "E3020", {"start": v(69.9, 10.45) * mm, "end": v(69.9, 10.52) * mm});
            skLineSegment(sketch, "E3021", {"start": v(69.9, 10.52) * mm, "end": v(69.91, 10.57) * mm});
            skLineSegment(sketch, "E3022", {"start": v(69.91, 10.57) * mm, "end": v(69.92, 10.64) * mm});
            skLineSegment(sketch, "E3023", {"start": v(69.92, 10.64) * mm, "end": v(69.93, 10.69) * mm});
            skLineSegment(sketch, "E3024", {"start": v(69.93, 10.69) * mm, "end": v(69.94, 10.76) * mm});
            skLineSegment(sketch, "E3025", {"start": v(69.94, 10.76) * mm, "end": v(69.95, 10.81) * mm});
            skLineSegment(sketch, "E3026", {"start": v(69.95, 10.81) * mm, "end": v(69.97, 10.88) * mm});
            skLineSegment(sketch, "E3027", {"start": v(69.97, 10.88) * mm, "end": v(69.98, 10.93) * mm});
            skLineSegment(sketch, "E3028", {"start": v(69.98, 10.93) * mm, "end": v(70, 11) * mm});
            skLineSegment(sketch, "E3029", {"start": v(70, 11) * mm, "end": v(70, 11.05) * mm});
            skLineSegment(sketch, "E3030", {"start": v(70, 11.05) * mm, "end": v(70.02, 11.12) * mm});
            skLineSegment(sketch, "E3031", {"start": v(70.02, 11.12) * mm, "end": v(70.04, 11.17) * mm});
            skLineSegment(sketch, "E3032", {"start": v(70.04, 11.17) * mm, "end": v(70.05, 11.24) * mm});
            skLineSegment(sketch, "E3033", {"start": v(70.05, 11.24) * mm, "end": v(70.07, 11.3) * mm});
            skLineSegment(sketch, "E3034", {"start": v(70.07, 11.3) * mm, "end": v(70.09, 11.35) * mm});
            skLineSegment(sketch, "E3035", {"start": v(70.09, 11.35) * mm, "end": v(70.1, 11.4) * mm});
            skLineSegment(sketch, "E3036", {"start": v(70.1, 11.4) * mm, "end": v(70.13, 11.47) * mm});
            skLineSegment(sketch, "E3037", {"start": v(70.13, 11.47) * mm, "end": v(70.15, 11.53) * mm});
            skLineSegment(sketch, "E3038", {"start": v(70.15, 11.53) * mm, "end": v(70.17, 11.6) * mm});
            skLineSegment(sketch, "E3039", {"start": v(70.17, 11.6) * mm, "end": v(70.21, 11.7) * mm});
            skLineSegment(sketch, "E3040", {"start": v(70.21, 11.7) * mm, "end": v(70.22, 11.74) * mm});
            skLineSegment(sketch, "E3041", {"start": v(70.22, 11.74) * mm, "end": v(70.26, 11.82) * mm});
            skLineSegment(sketch, "E3042", {"start": v(70.26, 11.82) * mm, "end": v(70.27, 11.85) * mm});
            skLineSegment(sketch, "E3043", {"start": v(70.27, 11.85) * mm, "end": v(70.3, 11.93) * mm});
            skLineSegment(sketch, "E3044", {"start": v(70.3, 11.93) * mm, "end": v(70.32, 11.96) * mm});
            skLineSegment(sketch, "E3045", {"start": v(70.32, 11.96) * mm, "end": v(70.36, 12.04) * mm});
            skLineSegment(sketch, "E3046", {"start": v(70.36, 12.04) * mm, "end": v(70.37, 12.07) * mm});
            skLineSegment(sketch, "E3047", {"start": v(70.37, 12.07) * mm, "end": v(70.41, 12.15) * mm});
            skLineSegment(sketch, "E3048", {"start": v(70.41, 12.15) * mm, "end": v(70.43, 12.18) * mm});
            skLineSegment(sketch, "E3049", {"start": v(70.43, 12.18) * mm, "end": v(70.47, 12.26) * mm});
            skLineSegment(sketch, "E3050", {"start": v(70.47, 12.26) * mm, "end": v(70.49, 12.3) * mm});
            skLineSegment(sketch, "E3051", {"start": v(70.49, 12.3) * mm, "end": v(70.53, 12.37) * mm});
            skLineSegment(sketch, "E3052", {"start": v(70.53, 12.37) * mm, "end": v(70.55, 12.4) * mm});
            skLineSegment(sketch, "E3053", {"start": v(70.55, 12.4) * mm, "end": v(70.6, 12.47) * mm});
            skLineSegment(sketch, "E3054", {"start": v(70.6, 12.47) * mm, "end": v(70.61, 12.5) * mm});
            skLineSegment(sketch, "E3055", {"start": v(70.61, 12.5) * mm, "end": v(70.66, 12.58) * mm});
            skLineSegment(sketch, "E3056", {"start": v(70.66, 12.58) * mm, "end": v(70.68, 12.6) * mm});
            skLineSegment(sketch, "E3057", {"start": v(70.68, 12.6) * mm, "end": v(70.72, 12.68) * mm});
            skLineSegment(sketch, "E3058", {"start": v(70.72, 12.68) * mm, "end": v(70.75, 12.71) * mm});
            skLineSegment(sketch, "E3059", {"start": v(70.75, 12.71) * mm, "end": v(70.8, 12.78) * mm});
            skLineSegment(sketch, "E3060", {"start": v(70.8, 12.78) * mm, "end": v(70.82, 12.81) * mm});
            skLineSegment(sketch, "E3061", {"start": v(70.82, 12.81) * mm, "end": v(70.87, 12.88) * mm});
            skLineSegment(sketch, "E3062", {"start": v(70.87, 12.88) * mm, "end": v(70.9, 12.91) * mm});
            skLineSegment(sketch, "E3063", {"start": v(70.9, 12.91) * mm, "end": v(70.94, 12.98) * mm});
            skLineSegment(sketch, "E3064", {"start": v(70.94, 12.98) * mm, "end": v(70.97, 13) * mm});
            skLineSegment(sketch, "E3065", {"start": v(70.97, 13) * mm, "end": v(71.02, 13.07) * mm});
            skLineSegment(sketch, "E3066", {"start": v(71.02, 13.07) * mm, "end": v(71.05, 13.1) * mm});
            skLineSegment(sketch, "E3067", {"start": v(71.05, 13.1) * mm, "end": v(71.1, 13.16) * mm});
            skLineSegment(sketch, "E3068", {"start": v(71.1, 13.16) * mm, "end": v(71.13, 13.2) * mm});
            skLineSegment(sketch, "E3069", {"start": v(71.13, 13.2) * mm, "end": v(71.18, 13.26) * mm});
            skLineSegment(sketch, "E3070", {"start": v(71.18, 13.26) * mm, "end": v(71.2, 13.29) * mm});
            skLineSegment(sketch, "E3071", {"start": v(71.2, 13.29) * mm, "end": v(71.26, 13.35) * mm});
            skLineSegment(sketch, "E3072", {"start": v(71.26, 13.35) * mm, "end": v(71.3, 13.38) * mm});
            skLineSegment(sketch, "E3073", {"start": v(71.3, 13.38) * mm, "end": v(71.35, 13.43) * mm});
            skLineSegment(sketch, "E3074", {"start": v(71.35, 13.43) * mm, "end": v(71.38, 13.46) * mm});
            skLineSegment(sketch, "E3075", {"start": v(71.38, 13.46) * mm, "end": v(71.44, 13.52) * mm});
            skLineSegment(sketch, "E3076", {"start": v(71.44, 13.52) * mm, "end": v(71.47, 13.55) * mm});
            skLineSegment(sketch, "E3077", {"start": v(71.47, 13.55) * mm, "end": v(71.53, 13.6) * mm});
            skLineSegment(sketch, "E3078", {"start": v(71.53, 13.6) * mm, "end": v(71.56, 13.63) * mm});
            skLineSegment(sketch, "E3079", {"start": v(71.56, 13.63) * mm, "end": v(71.62, 13.68) * mm});
            skLineSegment(sketch, "E3080", {"start": v(71.62, 13.68) * mm, "end": v(71.66, 13.71) * mm});
            skLineSegment(sketch, "E3081", {"start": v(71.66, 13.71) * mm, "end": v(71.71, 13.76) * mm});
            skLineSegment(sketch, "E3082", {"start": v(71.71, 13.76) * mm, "end": v(71.75, 13.79) * mm});
            skLineSegment(sketch, "E3083", {"start": v(71.75, 13.79) * mm, "end": v(71.8, 13.84) * mm});
            skLineSegment(sketch, "E3084", {"start": v(71.8, 13.84) * mm, "end": v(71.85, 13.87) * mm});
            skLineSegment(sketch, "E3085", {"start": v(71.85, 13.87) * mm, "end": v(71.9, 13.91) * mm});
            skLineSegment(sketch, "E3086", {"start": v(71.9, 13.91) * mm, "end": v(71.95, 13.94) * mm});
            skLineSegment(sketch, "E3087", {"start": v(71.95, 13.94) * mm, "end": v(72, 13.98) * mm});
            skLineSegment(sketch, "E3088", {"start": v(72, 13.98) * mm, "end": v(72.05, 14) * mm});
            skLineSegment(sketch, "E3089", {"start": v(72.05, 14) * mm, "end": v(72.1, 14.05) * mm});
            skLineSegment(sketch, "E3090", {"start": v(72.1, 14.05) * mm, "end": v(72.15, 14.08) * mm});
            skLineSegment(sketch, "E3091", {"start": v(72.15, 14.08) * mm, "end": v(72.21, 14.12) * mm});
            skLineSegment(sketch, "E3092", {"start": v(72.21, 14.12) * mm, "end": v(72.25, 14.14) * mm});
            skLineSegment(sketch, "E3093", {"start": v(72.25, 14.14) * mm, "end": v(72.32, 14.18) * mm});
            skLineSegment(sketch, "E3094", {"start": v(72.32, 14.18) * mm, "end": v(72.36, 14.2) * mm});
            skLineSegment(sketch, "E3095", {"start": v(72.36, 14.2) * mm, "end": v(72.42, 14.24) * mm});
            skLineSegment(sketch, "E3096", {"start": v(72.42, 14.24) * mm, "end": v(72.47, 14.27) * mm});
            skLineSegment(sketch, "E3097", {"start": v(72.47, 14.27) * mm, "end": v(72.53, 14.3) * mm});
            skLineSegment(sketch, "E3098", {"start": v(72.53, 14.3) * mm, "end": v(72.58, 14.32) * mm});
            skLineSegment(sketch, "E3099", {"start": v(72.58, 14.32) * mm, "end": v(72.64, 14.36) * mm});
            skLineSegment(sketch, "E3100", {"start": v(72.64, 14.36) * mm, "end": v(72.69, 14.38) * mm});
            skLineSegment(sketch, "E3101", {"start": v(72.69, 14.38) * mm, "end": v(72.75, 14.41) * mm});
            skLineSegment(sketch, "E3102", {"start": v(72.75, 14.41) * mm, "end": v(72.8, 14.43) * mm});
            skLineSegment(sketch, "E3103", {"start": v(72.8, 14.43) * mm, "end": v(72.86, 14.46) * mm});
            skLineSegment(sketch, "E3104", {"start": v(72.86, 14.46) * mm, "end": v(72.91, 14.48) * mm});
            skLineSegment(sketch, "E3105", {"start": v(72.91, 14.48) * mm, "end": v(72.98, 14.5) * mm});
            skLineSegment(sketch, "E3106", {"start": v(72.98, 14.5) * mm, "end": v(73.03, 14.53) * mm});
            skLineSegment(sketch, "E3107", {"start": v(73.03, 14.53) * mm, "end": v(73.1, 14.55) * mm});
            skLineSegment(sketch, "E3108", {"start": v(73.1, 14.55) * mm, "end": v(73.14, 14.57) * mm});
            skLineSegment(sketch, "E3109", {"start": v(73.14, 14.57) * mm, "end": v(73.2, 14.6) * mm});
            skLineSegment(sketch, "E3110", {"start": v(73.2, 14.6) * mm, "end": v(73.26, 14.61) * mm});
            skLineSegment(sketch, "E3111", {"start": v(73.26, 14.61) * mm, "end": v(73.32, 14.64) * mm});
            skLineSegment(sketch, "E3112", {"start": v(73.32, 14.64) * mm, "end": v(73.37, 14.65) * mm});
            skLineSegment(sketch, "E3113", {"start": v(73.37, 14.65) * mm, "end": v(73.44, 14.67) * mm});
            skLineSegment(sketch, "E3114", {"start": v(73.44, 14.67) * mm, "end": v(73.5, 14.69) * mm});
            skLineSegment(sketch, "E3115", {"start": v(73.5, 14.69) * mm, "end": v(73.56, 14.7) * mm});
            skLineSegment(sketch, "E3116", {"start": v(73.56, 14.7) * mm, "end": v(73.61, 14.72) * mm});
            skLineSegment(sketch, "E3117", {"start": v(73.61, 14.72) * mm, "end": v(73.68, 14.74) * mm});
            skLineSegment(sketch, "E3118", {"start": v(73.68, 14.74) * mm, "end": v(73.73, 14.75) * mm});
            skLineSegment(sketch, "E3119", {"start": v(73.73, 14.75) * mm, "end": v(73.8, 14.76) * mm});
            skLineSegment(sketch, "E3120", {"start": v(73.8, 14.76) * mm, "end": v(73.85, 14.78) * mm});
            skLineSegment(sketch, "E3121", {"start": v(73.85, 14.78) * mm, "end": v(73.92, 14.79) * mm});
            skLineSegment(sketch, "E3122", {"start": v(73.92, 14.79) * mm, "end": v(73.94, 14.8) * mm});
            skLineSegment(sketch, "E3123", {"start": v(73.94, 14.8) * mm, "end": v(73.97, 14.8) * mm});
            skLineSegment(sketch, "E3124", {"start": v(73.97, 14.8) * mm, "end": v(73.84, 15.08) * mm});
            skLineSegment(sketch, "E3125", {"start": v(73.84, 15.08) * mm, "end": v(73.64, 15.45) * mm});
            skLineSegment(sketch, "E3126", {"start": v(73.64, 15.45) * mm, "end": v(73.26, 16.2) * mm});
            skLineSegment(sketch, "E3127", {"start": v(73.26, 16.2) * mm, "end": v(73.11, 16.47) * mm});
            skLineSegment(sketch, "E3128", {"start": v(73.11, 16.47) * mm, "end": v(73.06, 16.55) * mm});
            skLineSegment(sketch, "E3129", {"start": v(73.06, 16.55) * mm, "end": v(73.03, 16.62) * mm});
            skLineSegment(sketch, "E3130", {"start": v(73.03, 16.62) * mm, "end": v(72.94, 16.77) * mm});
            skLineSegment(sketch, "E3131", {"start": v(72.94, 16.77) * mm, "end": v(72.36, 17.78) * mm});
            skLineSegment(sketch, "E3132", {"start": v(72.36, 17.78) * mm, "end": v(72.07, 18.25) * mm});
            skLineSegment(sketch, "E3133", {"start": v(72.07, 18.25) * mm, "end": v(71.89, 18.55) * mm});
            skLineSegment(sketch, "E3134", {"start": v(71.89, 18.55) * mm, "end": v(71.7, 18.84) * mm});
            skLineSegment(sketch, "E3135", {"start": v(71.7, 18.84) * mm, "end": v(71.4, 19.31) * mm});
            skLineSegment(sketch, "E3136", {"start": v(71.4, 19.31) * mm, "end": v(71.2, 19.6) * mm});
            skLineSegment(sketch, "E3137", {"start": v(71.2, 19.6) * mm, "end": v(70.88, 20.06) * mm});
            skLineSegment(sketch, "E3138", {"start": v(70.88, 20.06) * mm, "end": v(70.68, 20.34) * mm});
            skLineSegment(sketch, "E3139", {"start": v(70.68, 20.34) * mm, "end": v(70.35, 20.8) * mm});
            skLineSegment(sketch, "E3140", {"start": v(70.35, 20.8) * mm, "end": v(70.14, 21.07) * mm});
            skLineSegment(sketch, "E3141", {"start": v(70.14, 21.07) * mm, "end": v(69.8, 21.52) * mm});
            skLineSegment(sketch, "E3142", {"start": v(69.8, 21.52) * mm, "end": v(69.58, 21.8) * mm});
            skLineSegment(sketch, "E3143", {"start": v(69.58, 21.8) * mm, "end": v(69.23, 22.23) * mm});
            skLineSegment(sketch, "E3144", {"start": v(69.23, 22.23) * mm, "end": v(69, 22.5) * mm});
            skLineSegment(sketch, "E3145", {"start": v(69, 22.5) * mm, "end": v(68.65, 22.92) * mm});
            skLineSegment(sketch, "E3146", {"start": v(68.65, 22.92) * mm, "end": v(68.41, 23.18) * mm});
            skLineSegment(sketch, "E3147", {"start": v(68.41, 23.18) * mm, "end": v(68.04, 23.6) * mm});
            skLineSegment(sketch, "E3148", {"start": v(68.04, 23.6) * mm, "end": v(67.8, 23.86) * mm});
            skLineSegment(sketch, "E3149", {"start": v(67.8, 23.86) * mm, "end": v(67.43, 24.27) * mm});
            skLineSegment(sketch, "E3150", {"start": v(67.43, 24.27) * mm, "end": v(67.18, 24.52) * mm});
            skLineSegment(sketch, "E3151", {"start": v(67.18, 24.52) * mm, "end": v(66.8, 24.92) * mm});
            skLineSegment(sketch, "E3152", {"start": v(66.8, 24.92) * mm, "end": v(66.54, 25.16) * mm});
            skLineSegment(sketch, "E3153", {"start": v(66.54, 25.16) * mm, "end": v(66.14, 25.55) * mm});
            skLineSegment(sketch, "E3154", {"start": v(66.14, 25.55) * mm, "end": v(65.89, 25.79) * mm});
            skLineSegment(sketch, "E3155", {"start": v(65.89, 25.79) * mm, "end": v(65.48, 26.17) * mm});
            skLineSegment(sketch, "E3156", {"start": v(65.48, 26.17) * mm, "end": v(65.22, 26.4) * mm});
            skLineSegment(sketch, "E3157", {"start": v(65.22, 26.4) * mm, "end": v(64.8, 26.77) * mm});
            skLineSegment(sketch, "E3158", {"start": v(64.8, 26.77) * mm, "end": v(64.53, 27) * mm});
            skLineSegment(sketch, "E3159", {"start": v(64.53, 27) * mm, "end": v(64.1, 27.36) * mm});
            skLineSegment(sketch, "E3160", {"start": v(64.1, 27.36) * mm, "end": v(63.83, 27.57) * mm});
            skLineSegment(sketch, "E3161", {"start": v(63.83, 27.57) * mm, "end": v(63.4, 27.92) * mm});
            skLineSegment(sketch, "E3162", {"start": v(63.4, 27.92) * mm, "end": v(62.95, 28.26) * mm});
            skLineSegment(sketch, "E3163", {"start": v(62.95, 28.26) * mm, "end": v(62.67, 28.47) * mm});
            skLineSegment(sketch, "E3164", {"start": v(62.67, 28.47) * mm, "end": v(62.22, 28.8) * mm});
            skLineSegment(sketch, "E3165", {"start": v(62.22, 28.8) * mm, "end": v(61.93, 29) * mm});
            skLineSegment(sketch, "E3166", {"start": v(61.93, 29) * mm, "end": v(61.65, 29.2) * mm});
            skLineSegment(sketch, "E3167", {"start": v(61.65, 29.2) * mm, "end": v(61.18, 29.52) * mm});
            skLineSegment(sketch, "E3168", {"start": v(61.18, 29.52) * mm, "end": v(60.9, 29.71) * mm});
            skLineSegment(sketch, "E3169", {"start": v(60.9, 29.71) * mm, "end": v(60.42, 30.02) * mm});
            skLineSegment(sketch, "E3170", {"start": v(60.42, 30.02) * mm, "end": v(59.95, 30.3) * mm});
            skLineSegment(sketch, "E3171", {"start": v(59.95, 30.3) * mm, "end": v(59.65, 30.5) * mm});
            skLineSegment(sketch, "E3172", {"start": v(59.65, 30.5) * mm, "end": v(59.35, 30.67) * mm});
            skLineSegment(sketch, "E3173", {"start": v(59.35, 30.67) * mm, "end": v(58.87, 30.95) * mm});
            skLineSegment(sketch, "E3174", {"start": v(58.87, 30.95) * mm, "end": v(58.56, 31.12) * mm});
            skLineSegment(sketch, "E3175", {"start": v(58.56, 31.12) * mm, "end": v(58.07, 31.39) * mm});
            skLineSegment(sketch, "E3176", {"start": v(58.07, 31.39) * mm, "end": v(57.76, 31.55) * mm});
            skLineSegment(sketch, "E3177", {"start": v(57.76, 31.55) * mm, "end": v(57.26, 31.8) * mm});
            skLineSegment(sketch, "E3178", {"start": v(57.26, 31.8) * mm, "end": v(56.95, 31.96) * mm});
            skLineSegment(sketch, "E3179", {"start": v(56.95, 31.96) * mm, "end": v(56.45, 32.2) * mm});
            skLineSegment(sketch, "E3180", {"start": v(56.45, 32.2) * mm, "end": v(56.13, 32.35) * mm});
            skLineSegment(sketch, "E3181", {"start": v(56.13, 32.35) * mm, "end": v(55.62, 32.58) * mm});
            skLineSegment(sketch, "E3182", {"start": v(55.62, 32.58) * mm, "end": v(55.3, 32.72) * mm});
            skLineSegment(sketch, "E3183", {"start": v(55.3, 32.72) * mm, "end": v(54.79, 32.94) * mm});
            skLineSegment(sketch, "E3184", {"start": v(54.79, 32.94) * mm, "end": v(54.46, 33.07) * mm});
            skLineSegment(sketch, "E3185", {"start": v(54.46, 33.07) * mm, "end": v(53.94, 33.28) * mm});
            skLineSegment(sketch, "E3186", {"start": v(53.94, 33.28) * mm, "end": v(52.87, 33.66) * mm});
            skLineSegment(sketch, "E3187", {"start": v(52.87, 33.66) * mm, "end": v(52.55, 33.78) * mm});
            skLineSegment(sketch, "E3188", {"start": v(52.55, 33.78) * mm, "end": v(52.24, 33.89) * mm});
            skLineSegment(sketch, "E3189", {"start": v(52.24, 33.89) * mm, "end": v(52.22, 33.9) * mm});
            skLineSegment(sketch, "E3190", {"start": v(52.22, 33.9) * mm, "end": v(52.02, 33.96) * mm});
            skLineSegment(sketch, "E3191", {"start": v(52.02, 33.96) * mm, "end": v(51.76, 34.04) * mm});
            skLineSegment(sketch, "E3192", {"start": v(51.76, 34.04) * mm, "end": v(51.66, 34.07) * mm});
            skLineSegment(sketch, "E3193", {"start": v(51.66, 34.07) * mm, "end": v(51.37, 34.16) * mm});
            skLineSegment(sketch, "E3194", {"start": v(51.37, 34.16) * mm, "end": v(51.18, 34.22) * mm});
            skLineSegment(sketch, "E3195", {"start": v(51.18, 34.22) * mm, "end": v(50.86, 34.31) * mm});
            skLineSegment(sketch, "E3196", {"start": v(50.86, 34.31) * mm, "end": v(50.77, 34.34) * mm});
            skLineSegment(sketch, "E3197", {"start": v(50.77, 34.34) * mm, "end": v(50.5, 34.42) * mm});
            skLineSegment(sketch, "E3198", {"start": v(50.5, 34.42) * mm, "end": v(50.25, 34.48) * mm});
            skLineSegment(sketch, "E3199", {"start": v(50.25, 34.48) * mm, "end": v(49.97, 34.55) * mm});
            skLineSegment(sketch, "E3200", {"start": v(49.97, 34.55) * mm, "end": v(49.17, 34.73) * mm});
            skLineSegment(sketch, "E3201", {"start": v(49.17, 34.73) * mm, "end": v(48.87, 34.81) * mm});
            skLineSegment(sketch, "E3202", {"start": v(48.87, 34.81) * mm, "end": v(48.85, 34.82) * mm});
            skLineSegment(sketch, "E3203", {"start": v(48.85, 34.82) * mm, "end": v(48.57, 34.88) * mm});
            skLineSegment(sketch, "E3204", {"start": v(48.57, 34.88) * mm, "end": v(48.3, 34.93) * mm});
            skLineSegment(sketch, "E3205", {"start": v(48.3, 34.93) * mm, "end": v(47.5, 35.06) * mm});
            skLineSegment(sketch, "E3206", {"start": v(47.5, 35.06) * mm, "end": v(47.23, 35.12) * mm});
            skLineSegment(sketch, "E3207", {"start": v(47.23, 35.12) * mm, "end": v(47.22, 35.13) * mm});
            skLineSegment(sketch, "E3208", {"start": v(47.22, 35.13) * mm, "end": v(45.8, 35.39) * mm});
            skLineSegment(sketch, "E3209", {"start": v(45.8, 35.39) * mm, "end": v(45.58, 35.42) * mm});
            skLineSegment(sketch, "E3210", {"start": v(45.58, 35.42) * mm, "end": v(45.6, 35.33) * mm});
            skLineSegment(sketch, "E3211", {"start": v(45.6, 35.33) * mm, "end": v(45.6, 35.26) * mm});
            skLineSegment(sketch, "E3212", {"start": v(45.6, 35.26) * mm, "end": v(45.6, 35.2) * mm});
            skLineSegment(sketch, "E3213", {"start": v(45.6, 35.2) * mm, "end": v(45.6, 35.12) * mm});
            skLineSegment(sketch, "E3214", {"start": v(45.6, 35.12) * mm, "end": v(45.6, 35.05) * mm});
            skLineSegment(sketch, "E3215", {"start": v(45.6, 35.05) * mm, "end": v(45.6, 34.98) * mm});
            skLineSegment(sketch, "E3216", {"start": v(45.6, 34.98) * mm, "end": v(45.6, 34.9) * mm});
            skLineSegment(sketch, "E3217", {"start": v(45.6, 34.9) * mm, "end": v(45.6, 34.84) * mm});
            skLineSegment(sketch, "E3218", {"start": v(45.6, 34.84) * mm, "end": v(45.6, 34.76) * mm});
            skLineSegment(sketch, "E3219", {"start": v(45.6, 34.76) * mm, "end": v(45.59, 34.69) * mm});
            skLineSegment(sketch, "E3220", {"start": v(45.59, 34.69) * mm, "end": v(45.58, 34.61) * mm});
            skLineSegment(sketch, "E3221", {"start": v(45.58, 34.61) * mm, "end": v(45.57, 34.54) * mm});
            skLineSegment(sketch, "E3222", {"start": v(45.57, 34.54) * mm, "end": v(45.55, 34.46) * mm});
            skLineSegment(sketch, "E3223", {"start": v(45.55, 34.46) * mm, "end": v(45.54, 34.38) * mm});
            skLineSegment(sketch, "E3224", {"start": v(45.54, 34.38) * mm, "end": v(45.52, 34.3) * mm});
            skLineSegment(sketch, "E3225", {"start": v(45.52, 34.3) * mm, "end": v(45.5, 34.23) * mm});
            skLineSegment(sketch, "E3226", {"start": v(45.5, 34.23) * mm, "end": v(45.48, 34.15) * mm});
            skLineSegment(sketch, "E3227", {"start": v(45.48, 34.15) * mm, "end": v(45.46, 34.07) * mm});
            skLineSegment(sketch, "E3228", {"start": v(45.46, 34.07) * mm, "end": v(45.43, 33.99) * mm});
            skLineSegment(sketch, "E3229", {"start": v(45.43, 33.99) * mm, "end": v(45.4, 33.9) * mm});
            skLineSegment(sketch, "E3230", {"start": v(45.4, 33.9) * mm, "end": v(45.38, 33.83) * mm});
            skLineSegment(sketch, "E3231", {"start": v(45.38, 33.83) * mm, "end": v(45.38, 33.76) * mm});
            skLineSegment(sketch, "E3232", {"start": v(45.38, 33.76) * mm, "end": v(45.35, 33.68) * mm});
            skLineSegment(sketch, "E3233", {"start": v(45.35, 33.68) * mm, "end": v(45.36, 33.63) * mm});
            skLineSegment(sketch, "E3234", {"start": v(45.36, 33.63) * mm, "end": v(45.32, 33.55) * mm});
            skLineSegment(sketch, "E3235", {"start": v(45.32, 33.55) * mm, "end": v(45.33, 33.5) * mm});
            skLineSegment(sketch, "E3236", {"start": v(45.33, 33.5) * mm, "end": v(45.29, 33.43) * mm});
            skLineSegment(sketch, "E3237", {"start": v(45.29, 33.43) * mm, "end": v(45.3, 33.38) * mm});
            skLineSegment(sketch, "E3238", {"start": v(45.3, 33.38) * mm, "end": v(45.25, 33.3) * mm});
            skLineSegment(sketch, "E3239", {"start": v(45.25, 33.3) * mm, "end": v(45.25, 33.26) * mm});
            skLineSegment(sketch, "E3240", {"start": v(45.25, 33.26) * mm, "end": v(45.25, 33.21) * mm});
            skLineSegment(sketch, "E3241", {"start": v(45.25, 33.21) * mm, "end": v(45.21, 33.13) * mm});
            skLineSegment(sketch, "E3242", {"start": v(45.21, 33.13) * mm, "end": v(45.21, 33.09) * mm});
            skLineSegment(sketch, "E3243", {"start": v(45.21, 33.09) * mm, "end": v(45.17, 33.01) * mm});
            skLineSegment(sketch, "E3244", {"start": v(45.17, 33.01) * mm, "end": v(45.16, 32.97) * mm});
            skLineSegment(sketch, "E3245", {"start": v(45.16, 32.97) * mm, "end": v(45.16, 32.92) * mm});
            skLineSegment(sketch, "E3246", {"start": v(45.16, 32.92) * mm, "end": v(45.12, 32.85) * mm});
            skLineSegment(sketch, "E3247", {"start": v(45.12, 32.85) * mm, "end": v(45.11, 32.8) * mm});
            skLineSegment(sketch, "E3248", {"start": v(45.11, 32.8) * mm, "end": v(45.1, 32.76) * mm});
            skLineSegment(sketch, "E3249", {"start": v(45.1, 32.76) * mm, "end": v(45.06, 32.69) * mm});
            skLineSegment(sketch, "E3250", {"start": v(45.06, 32.69) * mm, "end": v(45.05, 32.64) * mm});
            skLineSegment(sketch, "E3251", {"start": v(45.05, 32.64) * mm, "end": v(45, 32.57) * mm});
            skLineSegment(sketch, "E3252", {"start": v(45, 32.57) * mm, "end": v(45, 32.53) * mm});
            skLineSegment(sketch, "E3253", {"start": v(45, 32.53) * mm, "end": v(44.94, 32.45) * mm});
            skLineSegment(sketch, "E3254", {"start": v(44.94, 32.45) * mm, "end": v(44.94, 32.41) * mm});
            skLineSegment(sketch, "E3255", {"start": v(44.94, 32.41) * mm, "end": v(44.93, 32.37) * mm});
            skLineSegment(sketch, "E3256", {"start": v(44.93, 32.37) * mm, "end": v(44.87, 32.3) * mm});
            skLineSegment(sketch, "E3257", {"start": v(44.87, 32.3) * mm, "end": v(44.86, 32.26) * mm});
            skLineSegment(sketch, "E3258", {"start": v(44.86, 32.26) * mm, "end": v(44.8, 32.19) * mm});
            skLineSegment(sketch, "E3259", {"start": v(44.8, 32.19) * mm, "end": v(44.8, 32.15) * mm});
            skLineSegment(sketch, "E3260", {"start": v(44.8, 32.15) * mm, "end": v(44.78, 32.11) * mm});
            skLineSegment(sketch, "E3261", {"start": v(44.78, 32.11) * mm, "end": v(44.73, 32.04) * mm});
            skLineSegment(sketch, "E3262", {"start": v(44.73, 32.04) * mm, "end": v(44.71, 32) * mm});
            skLineSegment(sketch, "E3263", {"start": v(44.71, 32) * mm, "end": v(44.66, 31.93) * mm});
            skLineSegment(sketch, "E3264", {"start": v(44.66, 31.93) * mm, "end": v(44.64, 31.9) * mm});
            skLineSegment(sketch, "E3265", {"start": v(44.64, 31.9) * mm, "end": v(44.63, 31.86) * mm});
            skLineSegment(sketch, "E3266", {"start": v(44.63, 31.86) * mm, "end": v(44.57, 31.8) * mm});
            skLineSegment(sketch, "E3267", {"start": v(44.57, 31.8) * mm, "end": v(44.55, 31.76) * mm});
            skLineSegment(sketch, "E3268", {"start": v(44.55, 31.76) * mm, "end": v(44.49, 31.7) * mm});
            skLineSegment(sketch, "E3269", {"start": v(44.49, 31.7) * mm, "end": v(44.47, 31.66) * mm});
            skLineSegment(sketch, "E3270", {"start": v(44.47, 31.66) * mm, "end": v(44.45, 31.62) * mm});
            skLineSegment(sketch, "E3271", {"start": v(44.45, 31.62) * mm, "end": v(44.4, 31.56) * mm});
            skLineSegment(sketch, "E3272", {"start": v(44.4, 31.56) * mm, "end": v(44.37, 31.52) * mm});
            skLineSegment(sketch, "E3273", {"start": v(44.37, 31.52) * mm, "end": v(44.3, 31.46) * mm});
            skLineSegment(sketch, "E3274", {"start": v(44.3, 31.46) * mm, "end": v(44.29, 31.43) * mm});
            skLineSegment(sketch, "E3275", {"start": v(44.29, 31.43) * mm, "end": v(44.27, 31.4) * mm});
            skLineSegment(sketch, "E3276", {"start": v(44.27, 31.4) * mm, "end": v(44.2, 31.33) * mm});
            skLineSegment(sketch, "E3277", {"start": v(44.2, 31.33) * mm, "end": v(44.18, 31.3) * mm});
            skLineSegment(sketch, "E3278", {"start": v(44.18, 31.3) * mm, "end": v(44.11, 31.24) * mm});
            skLineSegment(sketch, "E3279", {"start": v(44.11, 31.24) * mm, "end": v(44.1, 31.21) * mm});
            skLineSegment(sketch, "E3280", {"start": v(44.1, 31.21) * mm, "end": v(44.02, 31.15) * mm});
            skLineSegment(sketch, "E3281", {"start": v(44.02, 31.15) * mm, "end": v(44, 31.12) * mm});
            skLineSegment(sketch, "E3282", {"start": v(44, 31.12) * mm, "end": v(43.98, 31.1) * mm});
            skLineSegment(sketch, "E3283", {"start": v(43.98, 31.1) * mm, "end": v(43.96, 31.07) * mm});
            skLineSegment(sketch, "E3284", {"start": v(43.96, 31.07) * mm, "end": v(43.94, 31.04) * mm});
            skLineSegment(sketch, "E3285", {"start": v(43.94, 31.04) * mm, "end": v(43.91, 31.01) * mm});
            skLineSegment(sketch, "E3286", {"start": v(43.91, 31.01) * mm, "end": v(43.89, 30.98) * mm});
            skLineSegment(sketch, "E3287", {"start": v(43.89, 30.98) * mm, "end": v(43.66, 30.78) * mm});
            skLineSegment(sketch, "E3288", {"start": v(43.66, 30.78) * mm, "end": v(43.6, 30.74) * mm});
            skLineSegment(sketch, "E3289", {"start": v(43.6, 30.74) * mm, "end": v(43.55, 30.7) * mm});
            skLineSegment(sketch, "E3290", {"start": v(43.55, 30.7) * mm, "end": v(43.5, 30.66) * mm});
            skLineSegment(sketch, "E3291", {"start": v(43.5, 30.66) * mm, "end": v(43.44, 30.62) * mm});
            skLineSegment(sketch, "E3292", {"start": v(43.44, 30.62) * mm, "end": v(43.38, 30.59) * mm});
            skLineSegment(sketch, "E3293", {"start": v(43.38, 30.59) * mm, "end": v(43.32, 30.55) * mm});
            skLineSegment(sketch, "E3294", {"start": v(43.32, 30.55) * mm, "end": v(43.26, 30.52) * mm});
            skLineSegment(sketch, "E3295", {"start": v(43.26, 30.52) * mm, "end": v(43.2, 30.48) * mm});
            skLineSegment(sketch, "E3296", {"start": v(43.2, 30.48) * mm, "end": v(43.15, 30.45) * mm});
            skLineSegment(sketch, "E3297", {"start": v(43.15, 30.45) * mm, "end": v(43.1, 30.42) * mm});
            skLineSegment(sketch, "E3298", {"start": v(43.1, 30.42) * mm, "end": v(43.06, 30.4) * mm});
            skLineSegment(sketch, "E3299", {"start": v(43.06, 30.4) * mm, "end": v(43, 30.36) * mm});
            skLineSegment(sketch, "E3300", {"start": v(43, 30.36) * mm, "end": v(42.95, 30.33) * mm});
            skLineSegment(sketch, "E3301", {"start": v(42.95, 30.33) * mm, "end": v(42.89, 30.3) * mm});
            skLineSegment(sketch, "E3302", {"start": v(42.89, 30.3) * mm, "end": v(42.84, 30.28) * mm});
            skLineSegment(sketch, "E3303", {"start": v(42.84, 30.28) * mm, "end": v(42.77, 30.25) * mm});
            skLineSegment(sketch, "E3304", {"start": v(42.77, 30.25) * mm, "end": v(42.73, 30.22) * mm});
            skLineSegment(sketch, "E3305", {"start": v(42.73, 30.22) * mm, "end": v(42.66, 30.2) * mm});
            skLineSegment(sketch, "E3306", {"start": v(42.66, 30.2) * mm, "end": v(42.61, 30.17) * mm});
            skLineSegment(sketch, "E3307", {"start": v(42.61, 30.17) * mm, "end": v(42.57, 30.15) * mm});
            skLineSegment(sketch, "E3308", {"start": v(42.57, 30.15) * mm, "end": v(42.5, 30.13) * mm});
            skLineSegment(sketch, "E3309", {"start": v(42.5, 30.13) * mm, "end": v(42.45, 30.1) * mm});
            skLineSegment(sketch, "E3310", {"start": v(42.45, 30.1) * mm, "end": v(42.38, 30.08) * mm});
            skLineSegment(sketch, "E3311", {"start": v(42.38, 30.08) * mm, "end": v(42.34, 30.06) * mm});
            skLineSegment(sketch, "E3312", {"start": v(42.34, 30.06) * mm, "end": v(42.27, 30.04) * mm});
            skLineSegment(sketch, "E3313", {"start": v(42.27, 30.04) * mm, "end": v(42.22, 30.02) * mm});
            skLineSegment(sketch, "E3314", {"start": v(42.22, 30.02) * mm, "end": v(42.15, 30) * mm});
            skLineSegment(sketch, "E3315", {"start": v(42.15, 30) * mm, "end": v(42.1, 29.98) * mm});
            skLineSegment(sketch, "E3316", {"start": v(42.1, 29.98) * mm, "end": v(42.06, 29.97) * mm});
            skLineSegment(sketch, "E3317", {"start": v(42.06, 29.97) * mm, "end": v(41.99, 29.95) * mm});
            skLineSegment(sketch, "E3318", {"start": v(41.99, 29.95) * mm, "end": v(41.94, 29.93) * mm});
            skLineSegment(sketch, "E3319", {"start": v(41.94, 29.93) * mm, "end": v(41.87, 29.91) * mm});
            skLineSegment(sketch, "E3320", {"start": v(41.87, 29.91) * mm, "end": v(41.82, 29.9) * mm});
            skLineSegment(sketch, "E3321", {"start": v(41.82, 29.9) * mm, "end": v(41.75, 29.89) * mm});
            skLineSegment(sketch, "E3322", {"start": v(41.75, 29.89) * mm, "end": v(41.7, 29.87) * mm});
            skLineSegment(sketch, "E3323", {"start": v(41.7, 29.87) * mm, "end": v(41.65, 29.86) * mm});
            skLineSegment(sketch, "E3324", {"start": v(41.65, 29.86) * mm, "end": v(41.58, 29.85) * mm});
            skLineSegment(sketch, "E3325", {"start": v(41.58, 29.85) * mm, "end": v(41.53, 29.84) * mm});
            skLineSegment(sketch, "E3326", {"start": v(41.53, 29.84) * mm, "end": v(41.46, 29.83) * mm});
            skLineSegment(sketch, "E3327", {"start": v(41.46, 29.83) * mm, "end": v(41.41, 29.82) * mm});
            skLineSegment(sketch, "E3328", {"start": v(41.41, 29.82) * mm, "end": v(41.34, 29.8) * mm});
            skLineSegment(sketch, "E3329", {"start": v(41.34, 29.8) * mm, "end": v(41.29, 29.8) * mm});
            skLineSegment(sketch, "E3330", {"start": v(41.29, 29.8) * mm, "end": v(41.21, 29.8) * mm});
            skLineSegment(sketch, "E3331", {"start": v(41.21, 29.8) * mm, "end": v(41.17, 29.78) * mm});
            skLineSegment(sketch, "E3332", {"start": v(41.17, 29.78) * mm, "end": v(41.12, 29.78) * mm});
            skLineSegment(sketch, "E3333", {"start": v(41.12, 29.78) * mm, "end": v(41.04, 29.77) * mm});
            skLineSegment(sketch, "E3334", {"start": v(41.04, 29.77) * mm, "end": v(41, 29.77) * mm});
            skLineSegment(sketch, "E3335", {"start": v(41, 29.77) * mm, "end": v(40.92, 29.76) * mm});
            skLineSegment(sketch, "E3336", {"start": v(40.92, 29.76) * mm, "end": v(40.87, 29.76) * mm});
            skLineSegment(sketch, "E3337", {"start": v(40.87, 29.76) * mm, "end": v(40.8, 29.76) * mm});
            skLineSegment(sketch, "E3338", {"start": v(40.8, 29.76) * mm, "end": v(40.75, 29.75) * mm});
            skLineSegment(sketch, "E3339", {"start": v(40.75, 29.75) * mm, "end": v(40.68, 29.75) * mm});
            skLineSegment(sketch, "E3340", {"start": v(40.68, 29.75) * mm, "end": v(40.63, 29.75) * mm});
            skLineSegment(sketch, "E3341", {"start": v(40.63, 29.75) * mm, "end": v(40.58, 29.75) * mm});
            skLineSegment(sketch, "E3342", {"start": v(40.58, 29.75) * mm, "end": v(40.5, 29.76) * mm});
            skLineSegment(sketch, "E3343", {"start": v(40.5, 29.76) * mm, "end": v(40.46, 29.76) * mm});
            skLineSegment(sketch, "E3344", {"start": v(40.46, 29.76) * mm, "end": v(40.38, 29.76) * mm});
            skLineSegment(sketch, "E3345", {"start": v(40.38, 29.76) * mm, "end": v(40.34, 29.76) * mm});
            skLineSegment(sketch, "E3346", {"start": v(40.34, 29.76) * mm, "end": v(40.26, 29.77) * mm});
            skLineSegment(sketch, "E3347", {"start": v(40.26, 29.77) * mm, "end": v(40.21, 29.77) * mm});
            skLineSegment(sketch, "E3348", {"start": v(40.21, 29.77) * mm, "end": v(40.14, 29.78) * mm});
            skLineSegment(sketch, "E3349", {"start": v(40.14, 29.78) * mm, "end": v(40.1, 29.79) * mm});
            skLineSegment(sketch, "E3350", {"start": v(40.1, 29.79) * mm, "end": v(40.02, 29.8) * mm});
            skLineSegment(sketch, "E3351", {"start": v(40.02, 29.8) * mm, "end": v(39.97, 29.8) * mm});
            skLineSegment(sketch, "E3352", {"start": v(39.97, 29.8) * mm, "end": v(39.9, 29.8) * mm});
            skLineSegment(sketch, "E3353", {"start": v(39.9, 29.8) * mm, "end": v(39.85, 29.82) * mm});
            skLineSegment(sketch, "E3354", {"start": v(39.85, 29.82) * mm, "end": v(39.77, 29.83) * mm});
            skLineSegment(sketch, "E3355", {"start": v(39.77, 29.83) * mm, "end": v(39.73, 29.84) * mm});
            skLineSegment(sketch, "E3356", {"start": v(39.73, 29.84) * mm, "end": v(39.65, 29.85) * mm});
            skLineSegment(sketch, "E3357", {"start": v(39.65, 29.85) * mm, "end": v(39.6, 29.86) * mm});
            skLineSegment(sketch, "E3358", {"start": v(39.6, 29.86) * mm, "end": v(39.53, 29.88) * mm});
            skLineSegment(sketch, "E3359", {"start": v(39.53, 29.88) * mm, "end": v(39.49, 29.89) * mm});
            skLineSegment(sketch, "E3360", {"start": v(39.49, 29.89) * mm, "end": v(39.41, 29.9) * mm});
            skLineSegment(sketch, "E3361", {"start": v(39.41, 29.9) * mm, "end": v(39.37, 29.92) * mm});
            skLineSegment(sketch, "E3362", {"start": v(39.37, 29.92) * mm, "end": v(39.3, 29.94) * mm});
            skLineSegment(sketch, "E3363", {"start": v(39.3, 29.94) * mm, "end": v(39.25, 29.95) * mm});
            skLineSegment(sketch, "E3364", {"start": v(39.25, 29.95) * mm, "end": v(39.18, 29.97) * mm});
            skLineSegment(sketch, "E3365", {"start": v(39.18, 29.97) * mm, "end": v(39.13, 29.99) * mm});
            skLineSegment(sketch, "E3366", {"start": v(39.13, 29.99) * mm, "end": v(39.06, 30) * mm});
            skLineSegment(sketch, "E3367", {"start": v(39.06, 30) * mm, "end": v(39.01, 30.02) * mm});
            skLineSegment(sketch, "E3368", {"start": v(39.01, 30.02) * mm, "end": v(38.94, 30.05) * mm});
            skLineSegment(sketch, "E3369", {"start": v(38.94, 30.05) * mm, "end": v(38.9, 30.07) * mm});
            skLineSegment(sketch, "E3370", {"start": v(38.9, 30.07) * mm, "end": v(38.83, 30.1) * mm});
            skLineSegment(sketch, "E3371", {"start": v(38.83, 30.1) * mm, "end": v(38.78, 30.1) * mm});
            skLineSegment(sketch, "E3372", {"start": v(38.78, 30.1) * mm, "end": v(38.72, 30.14) * mm});
            skLineSegment(sketch, "E3373", {"start": v(38.72, 30.14) * mm, "end": v(38.67, 30.16) * mm});
            skLineSegment(sketch, "E3374", {"start": v(38.67, 30.16) * mm, "end": v(38.6, 30.18) * mm});
            skLineSegment(sketch, "E3375", {"start": v(38.6, 30.18) * mm, "end": v(38.56, 30.2) * mm});
            skLineSegment(sketch, "E3376", {"start": v(38.56, 30.2) * mm, "end": v(38.5, 30.24) * mm});
            skLineSegment(sketch, "E3377", {"start": v(38.5, 30.24) * mm, "end": v(38.44, 30.26) * mm});
            skLineSegment(sketch, "E3378", {"start": v(38.44, 30.26) * mm, "end": v(38.38, 30.29) * mm});
            skLineSegment(sketch, "E3379", {"start": v(38.38, 30.29) * mm, "end": v(38.33, 30.31) * mm});
            skLineSegment(sketch, "E3380", {"start": v(38.33, 30.31) * mm, "end": v(38.27, 30.35) * mm});
            skLineSegment(sketch, "E3381", {"start": v(38.27, 30.35) * mm, "end": v(38.23, 30.37) * mm});
            skLineSegment(sketch, "E3382", {"start": v(38.23, 30.37) * mm, "end": v(38.16, 30.4) * mm});
            skLineSegment(sketch, "E3383", {"start": v(38.16, 30.4) * mm, "end": v(38.12, 30.43) * mm});
            skLineSegment(sketch, "E3384", {"start": v(38.12, 30.43) * mm, "end": v(38.06, 30.47) * mm});
            skLineSegment(sketch, "E3385", {"start": v(38.06, 30.47) * mm, "end": v(38.01, 30.5) * mm});
            skLineSegment(sketch, "E3386", {"start": v(38.01, 30.5) * mm, "end": v(37.95, 30.53) * mm});
            skLineSegment(sketch, "E3387", {"start": v(37.95, 30.53) * mm, "end": v(37.9, 30.56) * mm});
            skLineSegment(sketch, "E3388", {"start": v(37.9, 30.56) * mm, "end": v(37.85, 30.6) * mm});
            skLineSegment(sketch, "E3389", {"start": v(37.85, 30.6) * mm, "end": v(37.8, 30.63) * mm});
            skLineSegment(sketch, "E3390", {"start": v(37.8, 30.63) * mm, "end": v(37.75, 30.67) * mm});
            skLineSegment(sketch, "E3391", {"start": v(37.75, 30.67) * mm, "end": v(37.7, 30.7) * mm});
            skLineSegment(sketch, "E3392", {"start": v(37.7, 30.7) * mm, "end": v(37.65, 30.74) * mm});
            skLineSegment(sketch, "E3393", {"start": v(37.65, 30.74) * mm, "end": v(37.6, 30.78) * mm});
            skLineSegment(sketch, "E3394", {"start": v(37.6, 30.78) * mm, "end": v(37.55, 30.82) * mm});
            skLineSegment(sketch, "E3395", {"start": v(37.55, 30.82) * mm, "end": v(37.46, 30.9) * mm});
            skLineSegment(sketch, "E3396", {"start": v(37.46, 30.9) * mm, "end": v(37.43, 30.91) * mm});
            skLineSegment(sketch, "E3397", {"start": v(37.43, 30.91) * mm, "end": v(37.36, 30.97) * mm});
            skLineSegment(sketch, "E3398", {"start": v(37.36, 30.97) * mm, "end": v(37.34, 31) * mm});
            skLineSegment(sketch, "E3399", {"start": v(37.34, 31) * mm, "end": v(37.27, 31.05) * mm});
            skLineSegment(sketch, "E3400", {"start": v(37.27, 31.05) * mm, "end": v(37.24, 31.08) * mm});
            skLineSegment(sketch, "E3401", {"start": v(37.24, 31.08) * mm, "end": v(37.18, 31.13) * mm});
            skLineSegment(sketch, "E3402", {"start": v(37.18, 31.13) * mm, "end": v(37.15, 31.16) * mm});
            skLineSegment(sketch, "E3403", {"start": v(37.15, 31.16) * mm, "end": v(37.1, 31.22) * mm});
            skLineSegment(sketch, "E3404", {"start": v(37.1, 31.22) * mm, "end": v(37.07, 31.25) * mm});
            skLineSegment(sketch, "E3405", {"start": v(37.07, 31.25) * mm, "end": v(37, 31.3) * mm});
            skLineSegment(sketch, "E3406", {"start": v(37, 31.3) * mm, "end": v(36.98, 31.34) * mm});
            skLineSegment(sketch, "E3407", {"start": v(36.98, 31.34) * mm, "end": v(36.92, 31.4) * mm});
            skLineSegment(sketch, "E3408", {"start": v(36.92, 31.4) * mm, "end": v(36.9, 31.43) * mm});
            skLineSegment(sketch, "E3409", {"start": v(36.9, 31.43) * mm, "end": v(36.84, 31.5) * mm});
            skLineSegment(sketch, "E3410", {"start": v(36.84, 31.5) * mm, "end": v(36.82, 31.52) * mm});
            skLineSegment(sketch, "E3411", {"start": v(36.82, 31.52) * mm, "end": v(36.76, 31.58) * mm});
            skLineSegment(sketch, "E3412", {"start": v(36.76, 31.58) * mm, "end": v(36.74, 31.62) * mm});
            skLineSegment(sketch, "E3413", {"start": v(36.74, 31.62) * mm, "end": v(36.69, 31.68) * mm});
            skLineSegment(sketch, "E3414", {"start": v(36.69, 31.68) * mm, "end": v(36.66, 31.71) * mm});
            skLineSegment(sketch, "E3415", {"start": v(36.66, 31.71) * mm, "end": v(36.61, 31.78) * mm});
            skLineSegment(sketch, "E3416", {"start": v(36.61, 31.78) * mm, "end": v(36.59, 31.81) * mm});
            skLineSegment(sketch, "E3417", {"start": v(36.59, 31.81) * mm, "end": v(36.54, 31.88) * mm});
            skLineSegment(sketch, "E3418", {"start": v(36.54, 31.88) * mm, "end": v(36.52, 31.91) * mm});
            skLineSegment(sketch, "E3419", {"start": v(36.52, 31.91) * mm, "end": v(36.47, 31.98) * mm});
            skLineSegment(sketch, "E3420", {"start": v(36.47, 31.98) * mm, "end": v(36.45, 32.01) * mm});
            skLineSegment(sketch, "E3421", {"start": v(36.45, 32.01) * mm, "end": v(36.4, 32.08) * mm});
            skLineSegment(sketch, "E3422", {"start": v(36.4, 32.08) * mm, "end": v(36.38, 32.12) * mm});
            skLineSegment(sketch, "E3423", {"start": v(36.38, 32.12) * mm, "end": v(36.34, 32.19) * mm});
            skLineSegment(sketch, "E3424", {"start": v(36.34, 32.19) * mm, "end": v(36.32, 32.22) * mm});
            skLineSegment(sketch, "E3425", {"start": v(36.32, 32.22) * mm, "end": v(36.28, 32.3) * mm});
            skLineSegment(sketch, "E3426", {"start": v(36.28, 32.3) * mm, "end": v(36.26, 32.33) * mm});
            skLineSegment(sketch, "E3427", {"start": v(36.26, 32.33) * mm, "end": v(36.22, 32.4) * mm});
            skLineSegment(sketch, "E3428", {"start": v(36.22, 32.4) * mm, "end": v(36.2, 32.44) * mm});
            skLineSegment(sketch, "E3429", {"start": v(36.2, 32.44) * mm, "end": v(36.16, 32.5) * mm});
            skLineSegment(sketch, "E3430", {"start": v(36.16, 32.5) * mm, "end": v(36.14, 32.55) * mm});
            skLineSegment(sketch, "E3431", {"start": v(36.14, 32.55) * mm, "end": v(36.1, 32.62) * mm});
            skLineSegment(sketch, "E3432", {"start": v(36.1, 32.62) * mm, "end": v(36.09, 32.66) * mm});
            skLineSegment(sketch, "E3433", {"start": v(36.09, 32.66) * mm, "end": v(36.06, 32.73) * mm});
            skLineSegment(sketch, "E3434", {"start": v(36.06, 32.73) * mm, "end": v(36.04, 32.77) * mm});
            skLineSegment(sketch, "E3435", {"start": v(36.04, 32.77) * mm, "end": v(36, 32.84) * mm});
            skLineSegment(sketch, "E3436", {"start": v(36, 32.84) * mm, "end": v(36, 32.89) * mm});
            skLineSegment(sketch, "E3437", {"start": v(36, 32.89) * mm, "end": v(35.96, 32.96) * mm});
            skLineSegment(sketch, "E3438", {"start": v(35.96, 32.96) * mm, "end": v(35.95, 33) * mm});
            skLineSegment(sketch, "E3439", {"start": v(35.95, 33) * mm, "end": v(35.92, 33.07) * mm});
            skLineSegment(sketch, "E3440", {"start": v(35.92, 33.07) * mm, "end": v(35.9, 33.12) * mm});
            skLineSegment(sketch, "E3441", {"start": v(35.9, 33.12) * mm, "end": v(35.88, 33.19) * mm});
            skLineSegment(sketch, "E3442", {"start": v(35.88, 33.19) * mm, "end": v(35.87, 33.23) * mm});
            skLineSegment(sketch, "E3443", {"start": v(35.87, 33.23) * mm, "end": v(35.84, 33.3) * mm});
            skLineSegment(sketch, "E3444", {"start": v(35.84, 33.3) * mm, "end": v(35.83, 33.35) * mm});
            skLineSegment(sketch, "E3445", {"start": v(35.83, 33.35) * mm, "end": v(35.8, 33.42) * mm});
            skLineSegment(sketch, "E3446", {"start": v(35.8, 33.42) * mm, "end": v(35.8, 33.47) * mm});
            skLineSegment(sketch, "E3447", {"start": v(35.8, 33.47) * mm, "end": v(35.78, 33.54) * mm});
            skLineSegment(sketch, "E3448", {"start": v(35.78, 33.54) * mm, "end": v(35.77, 33.59) * mm});
            skLineSegment(sketch, "E3449", {"start": v(35.77, 33.59) * mm, "end": v(35.75, 33.66) * mm});
            skLineSegment(sketch, "E3450", {"start": v(35.75, 33.66) * mm, "end": v(35.74, 33.7) * mm});
            skLineSegment(sketch, "E3451", {"start": v(35.74, 33.7) * mm, "end": v(35.72, 33.78) * mm});
            skLineSegment(sketch, "E3452", {"start": v(35.72, 33.78) * mm, "end": v(35.72, 33.83) * mm});
            skLineSegment(sketch, "E3453", {"start": v(35.72, 33.83) * mm, "end": v(35.7, 33.9) * mm});
            skLineSegment(sketch, "E3454", {"start": v(35.7, 33.9) * mm, "end": v(35.7, 33.95) * mm});
            skLineSegment(sketch, "E3455", {"start": v(35.7, 33.95) * mm, "end": v(35.68, 34.02) * mm});
            skLineSegment(sketch, "E3456", {"start": v(35.68, 34.02) * mm, "end": v(35.68, 34.07) * mm});
            skLineSegment(sketch, "E3457", {"start": v(35.68, 34.07) * mm, "end": v(35.67, 34.14) * mm});
            skLineSegment(sketch, "E3458", {"start": v(35.67, 34.14) * mm, "end": v(35.66, 34.2) * mm});
            skLineSegment(sketch, "E3459", {"start": v(35.66, 34.2) * mm, "end": v(35.65, 34.27) * mm});
            skLineSegment(sketch, "E3460", {"start": v(35.65, 34.27) * mm, "end": v(35.65, 34.32) * mm});
            skLineSegment(sketch, "E3461", {"start": v(35.65, 34.32) * mm, "end": v(35.64, 34.39) * mm});
            skLineSegment(sketch, "E3462", {"start": v(35.64, 34.39) * mm, "end": v(35.64, 34.44) * mm});
            skLineSegment(sketch, "E3463", {"start": v(35.64, 34.44) * mm, "end": v(35.63, 34.51) * mm});
            skLineSegment(sketch, "E3464", {"start": v(35.63, 34.51) * mm, "end": v(35.63, 34.56) * mm});
            skLineSegment(sketch, "E3465", {"start": v(35.63, 34.56) * mm, "end": v(35.63, 34.63) * mm});
            skLineSegment(sketch, "E3466", {"start": v(35.63, 34.63) * mm, "end": v(35.63, 34.69) * mm});
            skLineSegment(sketch, "E3467", {"start": v(35.63, 34.69) * mm, "end": v(35.63, 34.76) * mm});
            skLineSegment(sketch, "E3468", {"start": v(35.63, 34.76) * mm, "end": v(35.63, 34.81) * mm});
            skLineSegment(sketch, "E3469", {"start": v(35.63, 34.81) * mm, "end": v(35.63, 34.88) * mm});
            skLineSegment(sketch, "E3470", {"start": v(35.63, 34.88) * mm, "end": v(35.63, 34.93) * mm});
            skLineSegment(sketch, "E3471", {"start": v(35.63, 34.93) * mm, "end": v(35.63, 35) * mm});
            skLineSegment(sketch, "E3472", {"start": v(35.63, 35) * mm, "end": v(35.64, 35.06) * mm});
            skLineSegment(sketch, "E3473", {"start": v(35.64, 35.06) * mm, "end": v(35.64, 35.12) * mm});
            skLineSegment(sketch, "E3474", {"start": v(35.64, 35.12) * mm, "end": v(35.65, 35.18) * mm});
            skLineSegment(sketch, "E3475", {"start": v(35.65, 35.18) * mm, "end": v(35.65, 35.25) * mm});
            skLineSegment(sketch, "E3476", {"start": v(35.65, 35.25) * mm, "end": v(35.66, 35.3) * mm});
            skLineSegment(sketch, "E3477", {"start": v(35.66, 35.3) * mm, "end": v(35.67, 35.37) * mm});
            skLineSegment(sketch, "E3478", {"start": v(35.67, 35.37) * mm, "end": v(35.67, 35.4) * mm});
            skLineSegment(sketch, "E3479", {"start": v(35.67, 35.4) * mm, "end": v(35.67, 35.42) * mm});
            skLineSegment(sketch, "E3480", {"start": v(35.67, 35.42) * mm, "end": v(35.45, 35.39) * mm});
            skLineSegment(sketch, "E3481", {"start": v(35.45, 35.39) * mm, "end": v(35.03, 35.32) * mm});
            skLineSegment(sketch, "E3482", {"start": v(35.03, 35.32) * mm, "end": v(34.3, 35.21) * mm});
            skLineSegment(sketch, "E3483", {"start": v(34.3, 35.21) * mm, "end": v(34, 35.15) * mm});
            skLineSegment(sketch, "E3484", {"start": v(34, 35.15) * mm, "end": v(33.64, 35.09) * mm});
            skLineSegment(sketch, "E3485", {"start": v(33.64, 35.09) * mm, "end": v(33.51, 35.06) * mm});
            skLineSegment(sketch, "E3486", {"start": v(33.51, 35.06) * mm, "end": v(33.03, 34.96) * mm});
            skLineSegment(sketch, "E3487", {"start": v(33.03, 34.96) * mm, "end": v(32.52, 34.86) * mm});
            skLineSegment(sketch, "E3488", {"start": v(32.52, 34.86) * mm, "end": v(31.98, 34.73) * mm});
            skLineSegment(sketch, "E3489", {"start": v(31.98, 34.73) * mm, "end": v(31.64, 34.65) * mm});
            skLineSegment(sketch, "E3490", {"start": v(31.64, 34.65) * mm, "end": v(31.3, 34.56) * mm});
            skLineSegment(sketch, "E3491", {"start": v(31.3, 34.56) * mm, "end": v(30.76, 34.42) * mm});
            skLineSegment(sketch, "E3492", {"start": v(30.76, 34.42) * mm, "end": v(30.43, 34.32) * mm});
            skLineSegment(sketch, "E3493", {"start": v(30.43, 34.32) * mm, "end": v(29.89, 34.16) * mm});
            skLineSegment(sketch, "E3494", {"start": v(29.89, 34.16) * mm, "end": v(29.56, 34.06) * mm});
            skLineSegment(sketch, "E3495", {"start": v(29.56, 34.06) * mm, "end": v(29.02, 33.89) * mm});
            skLineSegment(sketch, "E3496", {"start": v(29.02, 33.89) * mm, "end": v(28.7, 33.78) * mm});
            skLineSegment(sketch, "E3497", {"start": v(28.7, 33.78) * mm, "end": v(28.16, 33.6) * mm});
            skLineSegment(sketch, "E3498", {"start": v(28.16, 33.6) * mm, "end": v(27.84, 33.47) * mm});
            skLineSegment(sketch, "E3499", {"start": v(27.84, 33.47) * mm, "end": v(27.31, 33.28) * mm});
            skLineSegment(sketch, "E3500", {"start": v(27.31, 33.28) * mm, "end": v(26.99, 33.15) * mm});
            skLineSegment(sketch, "E3501", {"start": v(26.99, 33.15) * mm, "end": v(26.47, 32.94) * mm});
            skLineSegment(sketch, "E3502", {"start": v(26.47, 32.94) * mm, "end": v(26.15, 32.8) * mm});
            skLineSegment(sketch, "E3503", {"start": v(26.15, 32.8) * mm, "end": v(25.64, 32.58) * mm});
            skLineSegment(sketch, "E3504", {"start": v(25.64, 32.58) * mm, "end": v(25.32, 32.44) * mm});
            skLineSegment(sketch, "E3505", {"start": v(25.32, 32.44) * mm, "end": v(24.8, 32.2) * mm});
            skLineSegment(sketch, "E3506", {"start": v(24.8, 32.2) * mm, "end": v(24.5, 32.05) * mm});
            skLineSegment(sketch, "E3507", {"start": v(24.5, 32.05) * mm, "end": v(24, 31.8) * mm});
            skLineSegment(sketch, "E3508", {"start": v(24, 31.8) * mm, "end": v(23.68, 31.64) * mm});
            skLineSegment(sketch, "E3509", {"start": v(23.68, 31.64) * mm, "end": v(23.19, 31.39) * mm});
            skLineSegment(sketch, "E3510", {"start": v(23.19, 31.39) * mm, "end": v(22.88, 31.22) * mm});
            skLineSegment(sketch, "E3511", {"start": v(22.88, 31.22) * mm, "end": v(22.4, 30.95) * mm});
            skLineSegment(sketch, "E3512", {"start": v(22.4, 30.95) * mm, "end": v(22.1, 30.77) * mm});
            skLineSegment(sketch, "E3513", {"start": v(22.1, 30.77) * mm, "end": v(21.6, 30.5) * mm});
            skLineSegment(sketch, "E3514", {"start": v(21.6, 30.5) * mm, "end": v(21.31, 30.3) * mm});
            skLineSegment(sketch, "E3515", {"start": v(21.31, 30.3) * mm, "end": v(20.83, 30.02) * mm});
            skLineSegment(sketch, "E3516", {"start": v(20.83, 30.02) * mm, "end": v(20.36, 29.71) * mm});
            skLineSegment(sketch, "E3517", {"start": v(20.36, 29.71) * mm, "end": v(20.07, 29.52) * mm});
            skLineSegment(sketch, "E3518", {"start": v(20.07, 29.52) * mm, "end": v(19.79, 29.32) * mm});
            skLineSegment(sketch, "E3519", {"start": v(19.79, 29.32) * mm, "end": v(19.32, 29) * mm});
            skLineSegment(sketch, "E3520", {"start": v(19.32, 29) * mm, "end": v(19.04, 28.8) * mm});
            skLineSegment(sketch, "E3521", {"start": v(19.04, 28.8) * mm, "end": v(18.59, 28.47) * mm});
            skLineSegment(sketch, "E3522", {"start": v(18.59, 28.47) * mm, "end": v(18.14, 28.14) * mm});
            skLineSegment(sketch, "E3523", {"start": v(18.14, 28.14) * mm, "end": v(17.87, 27.92) * mm});
            skLineSegment(sketch, "E3524", {"start": v(17.87, 27.92) * mm, "end": v(17.6, 27.7) * mm});
            skLineSegment(sketch, "E3525", {"start": v(17.6, 27.7) * mm, "end": v(17.16, 27.36) * mm});
            skLineSegment(sketch, "E3526", {"start": v(17.16, 27.36) * mm, "end": v(16.89, 27.13) * mm});
            skLineSegment(sketch, "E3527", {"start": v(16.89, 27.13) * mm, "end": v(16.46, 26.77) * mm});
            skLineSegment(sketch, "E3528", {"start": v(16.46, 26.77) * mm, "end": v(16.2, 26.54) * mm});
            skLineSegment(sketch, "E3529", {"start": v(16.2, 26.54) * mm, "end": v(15.78, 26.17) * mm});
            skLineSegment(sketch, "E3530", {"start": v(15.78, 26.17) * mm, "end": v(15.53, 25.93) * mm});
            skLineSegment(sketch, "E3531", {"start": v(15.53, 25.93) * mm, "end": v(15.12, 25.55) * mm});
            skLineSegment(sketch, "E3532", {"start": v(15.12, 25.55) * mm, "end": v(14.87, 25.3) * mm});
            skLineSegment(sketch, "E3533", {"start": v(14.87, 25.3) * mm, "end": v(14.47, 24.92) * mm});
            skLineSegment(sketch, "E3534", {"start": v(14.47, 24.92) * mm, "end": v(14.22, 24.67) * mm});
            skLineSegment(sketch, "E3535", {"start": v(14.22, 24.67) * mm, "end": v(13.83, 24.27) * mm});
            skLineSegment(sketch, "E3536", {"start": v(13.83, 24.27) * mm, "end": v(13.6, 24.01) * mm});
            skLineSegment(sketch, "E3537", {"start": v(13.6, 24.01) * mm, "end": v(13.21, 23.6) * mm});
            skLineSegment(sketch, "E3538", {"start": v(13.21, 23.6) * mm, "end": v(12.98, 23.34) * mm});
            skLineSegment(sketch, "E3539", {"start": v(12.98, 23.34) * mm, "end": v(12.61, 22.92) * mm});
            skLineSegment(sketch, "E3540", {"start": v(12.61, 22.92) * mm, "end": v(12.39, 22.66) * mm});
            skLineSegment(sketch, "E3541", {"start": v(12.39, 22.66) * mm, "end": v(12.03, 22.23) * mm});
            skLineSegment(sketch, "E3542", {"start": v(12.03, 22.23) * mm, "end": v(11.68, 21.8) * mm});
            skLineSegment(sketch, "E3543", {"start": v(11.68, 21.8) * mm, "end": v(11.46, 21.52) * mm});
            skLineSegment(sketch, "E3544", {"start": v(11.46, 21.52) * mm, "end": v(11.12, 21.07) * mm});
            skLineSegment(sketch, "E3545", {"start": v(11.12, 21.07) * mm, "end": v(10.91, 20.8) * mm});
            skLineSegment(sketch, "E3546", {"start": v(10.91, 20.8) * mm, "end": v(10.83, 20.7) * mm});
            skLineSegment(sketch, "E3547", {"start": v(10.83, 20.7) * mm, "end": v(10.7, 20.52) * mm});
            skLineSegment(sketch, "E3548", {"start": v(10.7, 20.52) * mm, "end": v(10.56, 20.3) * mm});
            skLineSegment(sketch, "E3549", {"start": v(10.56, 20.3) * mm, "end": v(10.38, 20.06) * mm});
            skLineSegment(sketch, "E3550", {"start": v(10.38, 20.06) * mm, "end": v(10.37, 20.05) * mm});
            skLineSegment(sketch, "E3551", {"start": v(10.37, 20.05) * mm, "end": v(10.2, 19.8) * mm});
            skLineSegment(sketch, "E3552", {"start": v(10.2, 19.8) * mm, "end": v(10.03, 19.55) * mm});
            skLineSegment(sketch, "E3553", {"start": v(10.03, 19.55) * mm, "end": v(9.86, 19.31) * mm});
            skLineSegment(sketch, "E3554", {"start": v(9.86, 19.31) * mm, "end": v(9.85, 19.28) * mm});
            skLineSegment(sketch, "E3555", {"start": v(9.85, 19.28) * mm, "end": v(9.66, 19) * mm});
            skLineSegment(sketch, "E3556", {"start": v(9.66, 19) * mm, "end": v(9.5, 18.75) * mm});
            skLineSegment(sketch, "E3557", {"start": v(9.5, 18.75) * mm, "end": v(9.05, 18) * mm});
            skLineSegment(sketch, "E3558", {"start": v(9.05, 18) * mm, "end": v(8.93, 17.81) * mm});
            skLineSegment(sketch, "E3559", {"start": v(8.93, 17.81) * mm, "end": v(8.88, 17.73) * mm});
            skLineSegment(sketch, "E3560", {"start": v(8.88, 17.73) * mm, "end": v(8.72, 17.47) * mm});
            skLineSegment(sketch, "E3561", {"start": v(8.72, 17.47) * mm, "end": v(8.63, 17.32) * mm});
            skLineSegment(sketch, "E3562", {"start": v(8.63, 17.32) * mm, "end": v(8.57, 17.23) * mm});
            skLineSegment(sketch, "E3563", {"start": v(8.57, 17.23) * mm, "end": v(8.45, 17.02) * mm});
            skLineSegment(sketch, "E3564", {"start": v(8.45, 17.02) * mm, "end": v(8.35, 16.85) * mm});
            skLineSegment(sketch, "E3565", {"start": v(8.35, 16.85) * mm, "end": v(8.34, 16.83) * mm});
            skLineSegment(sketch, "E3566", {"start": v(8.34, 16.83) * mm, "end": v(8.23, 16.63) * mm});
            skLineSegment(sketch, "E3567", {"start": v(8.23, 16.63) * mm, "end": v(8.1, 16.4) * mm});
            skLineSegment(sketch, "E3568", {"start": v(8.1, 16.4) * mm, "end": v(8, 16.2) * mm});
            skLineSegment(sketch, "E3569", {"start": v(8, 16.2) * mm, "end": v(7.61, 15.45) * mm});
            skLineSegment(sketch, "E3570", {"start": v(7.61, 15.45) * mm, "end": v(7.42, 15.08) * mm});
            skLineSegment(sketch, "E3571", {"start": v(7.42, 15.08) * mm, "end": v(7.28, 14.8) * mm});
            skLineSegment(sketch, "E3572", {"start": v(7.28, 14.8) * mm, "end": v(7.38, 14.78) * mm});
            skLineSegment(sketch, "E3573", {"start": v(7.38, 14.78) * mm, "end": v(7.44, 14.77) * mm});
            skLineSegment(sketch, "E3574", {"start": v(7.44, 14.77) * mm, "end": v(7.51, 14.75) * mm});
            skLineSegment(sketch, "E3575", {"start": v(7.51, 14.75) * mm, "end": v(7.58, 14.73) * mm});
            skLineSegment(sketch, "E3576", {"start": v(7.58, 14.73) * mm, "end": v(7.64, 14.7) * mm});
            skLineSegment(sketch, "E3577", {"start": v(7.64, 14.7) * mm, "end": v(7.71, 14.69) * mm});
            skLineSegment(sketch, "E3578", {"start": v(7.71, 14.69) * mm, "end": v(7.78, 14.66) * mm});
            skLineSegment(sketch, "E3579", {"start": v(7.78, 14.66) * mm, "end": v(7.85, 14.64) * mm});
            skLineSegment(sketch, "E3580", {"start": v(7.85, 14.64) * mm, "end": v(7.91, 14.6) * mm});
            skLineSegment(sketch, "E3581", {"start": v(7.91, 14.6) * mm, "end": v(7.98, 14.58) * mm});
            skLineSegment(sketch, "E3582", {"start": v(7.98, 14.58) * mm, "end": v(8.05, 14.55) * mm});
            skLineSegment(sketch, "E3583", {"start": v(8.05, 14.55) * mm, "end": v(8.12, 14.51) * mm});
            skLineSegment(sketch, "E3584", {"start": v(8.12, 14.51) * mm, "end": v(8.19, 14.47) * mm});
            skLineSegment(sketch, "E3585", {"start": v(8.19, 14.47) * mm, "end": v(8.26, 14.44) * mm});
            skLineSegment(sketch, "E3586", {"start": v(8.26, 14.44) * mm, "end": v(8.33, 14.4) * mm});
            skLineSegment(sketch, "E3587", {"start": v(8.33, 14.4) * mm, "end": v(8.4, 14.35) * mm});
            skLineSegment(sketch, "E3588", {"start": v(8.4, 14.35) * mm, "end": v(8.46, 14.3) * mm});
            skLineSegment(sketch, "E3589", {"start": v(8.46, 14.3) * mm, "end": v(8.53, 14.26) * mm});
            skLineSegment(sketch, "E3590", {"start": v(8.53, 14.26) * mm, "end": v(8.6, 14.21) * mm});
            skLineSegment(sketch, "E3591", {"start": v(8.6, 14.21) * mm, "end": v(8.67, 14.16) * mm});
            skLineSegment(sketch, "E3592", {"start": v(8.67, 14.16) * mm, "end": v(8.74, 14.1) * mm});
            skLineSegment(sketch, "E3593", {"start": v(8.74, 14.1) * mm, "end": v(8.8, 14.1) * mm});
            skLineSegment(sketch, "E3594", {"start": v(8.8, 14.1) * mm, "end": v(8.87, 14.04) * mm});
            skLineSegment(sketch, "E3595", {"start": v(8.87, 14.04) * mm, "end": v(8.92, 14.03) * mm});
            skLineSegment(sketch, "E3596", {"start": v(8.92, 14.03) * mm, "end": v(8.99, 13.97) * mm});
            skLineSegment(sketch, "E3597", {"start": v(8.99, 13.97) * mm, "end": v(9.03, 13.96) * mm});
            skLineSegment(sketch, "E3598", {"start": v(9.03, 13.96) * mm, "end": v(9.1, 13.9) * mm});
            skLineSegment(sketch, "E3599", {"start": v(9.1, 13.9) * mm, "end": v(9.14, 13.9) * mm});
            skLineSegment(sketch, "E3600", {"start": v(9.14, 13.9) * mm, "end": v(9.2, 13.83) * mm});
            skLineSegment(sketch, "E3601", {"start": v(9.2, 13.83) * mm, "end": v(9.24, 13.82) * mm});
            skLineSegment(sketch, "E3602", {"start": v(9.24, 13.82) * mm, "end": v(9.29, 13.8) * mm});
            skLineSegment(sketch, "E3603", {"start": v(9.29, 13.8) * mm, "end": v(9.35, 13.74) * mm});
            skLineSegment(sketch, "E3604", {"start": v(9.35, 13.74) * mm, "end": v(9.4, 13.72) * mm});
            skLineSegment(sketch, "E3605", {"start": v(9.4, 13.72) * mm, "end": v(9.45, 13.66) * mm});
            skLineSegment(sketch, "E3606", {"start": v(9.45, 13.66) * mm, "end": v(9.5, 13.64) * mm});
            skLineSegment(sketch, "E3607", {"start": v(9.5, 13.64) * mm, "end": v(9.53, 13.63) * mm});
            skLineSegment(sketch, "E3608", {"start": v(9.53, 13.63) * mm, "end": v(9.6, 13.56) * mm});
            skLineSegment(sketch, "E3609", {"start": v(9.6, 13.56) * mm, "end": v(9.63, 13.54) * mm});
            skLineSegment(sketch, "E3610", {"start": v(9.63, 13.54) * mm, "end": v(9.67, 13.52) * mm});
            skLineSegment(sketch, "E3611", {"start": v(9.67, 13.52) * mm, "end": v(9.73, 13.46) * mm});
            skLineSegment(sketch, "E3612", {"start": v(9.73, 13.46) * mm, "end": v(9.77, 13.44) * mm});
            skLineSegment(sketch, "E3613", {"start": v(9.77, 13.44) * mm, "end": v(9.82, 13.37) * mm});
            skLineSegment(sketch, "E3614", {"start": v(9.82, 13.37) * mm, "end": v(9.86, 13.35) * mm});
            skLineSegment(sketch, "E3615", {"start": v(9.86, 13.35) * mm, "end": v(9.91, 13.27) * mm});
            skLineSegment(sketch, "E3616", {"start": v(9.91, 13.27) * mm, "end": v(9.95, 13.25) * mm});
            skLineSegment(sketch, "E3617", {"start": v(9.95, 13.25) * mm, "end": v(9.98, 13.23) * mm});
            skLineSegment(sketch, "E3618", {"start": v(9.98, 13.23) * mm, "end": v(10.04, 13.16) * mm});
            skLineSegment(sketch, "E3619", {"start": v(10.04, 13.16) * mm, "end": v(10.07, 13.14) * mm});
            skLineSegment(sketch, "E3620", {"start": v(10.07, 13.14) * mm, "end": v(10.12, 13.06) * mm});
            skLineSegment(sketch, "E3621", {"start": v(10.12, 13.06) * mm, "end": v(10.16, 13.04) * mm});
            skLineSegment(sketch, "E3622", {"start": v(10.16, 13.04) * mm, "end": v(10.19, 13.02) * mm});
            skLineSegment(sketch, "E3623", {"start": v(10.19, 13.02) * mm, "end": v(10.24, 12.94) * mm});
            skLineSegment(sketch, "E3624", {"start": v(10.24, 12.94) * mm, "end": v(10.27, 12.92) * mm});
            skLineSegment(sketch, "E3625", {"start": v(10.27, 12.92) * mm, "end": v(10.32, 12.84) * mm});
            skLineSegment(sketch, "E3626", {"start": v(10.32, 12.84) * mm, "end": v(10.35, 12.81) * mm});
            skLineSegment(sketch, "E3627", {"start": v(10.35, 12.81) * mm, "end": v(10.38, 12.79) * mm});
            skLineSegment(sketch, "E3628", {"start": v(10.38, 12.79) * mm, "end": v(10.42, 12.71) * mm});
            skLineSegment(sketch, "E3629", {"start": v(10.42, 12.71) * mm, "end": v(10.45, 12.68) * mm});
            skLineSegment(sketch, "E3630", {"start": v(10.45, 12.68) * mm, "end": v(10.5, 12.6) * mm});
            skLineSegment(sketch, "E3631", {"start": v(10.5, 12.6) * mm, "end": v(10.53, 12.58) * mm});
            skLineSegment(sketch, "E3632", {"start": v(10.53, 12.58) * mm, "end": v(10.55, 12.55) * mm});
            skLineSegment(sketch, "E3633", {"start": v(10.55, 12.55) * mm, "end": v(10.6, 12.47) * mm});
            skLineSegment(sketch, "E3634", {"start": v(10.6, 12.47) * mm, "end": v(10.62, 12.44) * mm});
            skLineSegment(sketch, "E3635", {"start": v(10.62, 12.44) * mm, "end": v(10.66, 12.36) * mm});
            skLineSegment(sketch, "E3636", {"start": v(10.66, 12.36) * mm, "end": v(10.69, 12.33) * mm});
            skLineSegment(sketch, "E3637", {"start": v(10.69, 12.33) * mm, "end": v(10.72, 12.25) * mm});
            skLineSegment(sketch, "E3638", {"start": v(10.72, 12.25) * mm, "end": v(10.75, 12.22) * mm});
            skLineSegment(sketch, "E3639", {"start": v(10.75, 12.22) * mm, "end": v(10.77, 12.2) * mm});
            skLineSegment(sketch, "E3640", {"start": v(10.77, 12.2) * mm, "end": v(10.8, 12.17) * mm});
            skLineSegment(sketch, "E3641", {"start": v(10.8, 12.17) * mm, "end": v(10.82, 12.14) * mm});
            skLineSegment(sketch, "E3642", {"start": v(10.82, 12.14) * mm, "end": v(10.84, 12.1) * mm});
            skLineSegment(sketch, "E3643", {"start": v(10.84, 12.1) * mm, "end": v(10.86, 12.08) * mm});
            skLineSegment(sketch, "E3644", {"start": v(10.86, 12.08) * mm, "end": v(10.88, 12.05) * mm});
            skLineSegment(sketch, "E3645", {"start": v(10.88, 12.05) * mm, "end": v(10.9, 12.01) * mm});
            skLineSegment(sketch, "E3646", {"start": v(10.9, 12.01) * mm, "end": v(10.92, 11.98) * mm});
            skLineSegment(sketch, "E3647", {"start": v(10.92, 11.98) * mm, "end": v(10.94, 11.95) * mm});
            skLineSegment(sketch, "E3648", {"start": v(10.94, 11.95) * mm, "end": v(10.95, 11.92) * mm});
            skLineSegment(sketch, "E3649", {"start": v(10.95, 11.92) * mm, "end": v(11.06, 11.65) * mm});
            skLineSegment(sketch, "E3650", {"start": v(11.06, 11.65) * mm, "end": v(11.09, 11.6) * mm});
            skLineSegment(sketch, "E3651", {"start": v(11.09, 11.6) * mm, "end": v(11.1, 11.53) * mm});
            skLineSegment(sketch, "E3652", {"start": v(11.1, 11.53) * mm, "end": v(11.13, 11.47) * mm});
            skLineSegment(sketch, "E3653", {"start": v(11.13, 11.47) * mm, "end": v(11.15, 11.4) * mm});
            skLineSegment(sketch, "E3654", {"start": v(11.15, 11.4) * mm, "end": v(11.17, 11.34) * mm});
            skLineSegment(sketch, "E3655", {"start": v(11.17, 11.34) * mm, "end": v(11.19, 11.28) * mm});
            skLineSegment(sketch, "E3656", {"start": v(11.19, 11.28) * mm, "end": v(11.2, 11.2) * mm});
            skLineSegment(sketch, "E3657", {"start": v(11.2, 11.2) * mm, "end": v(11.22, 11.14) * mm});
            skLineSegment(sketch, "E3658", {"start": v(11.22, 11.14) * mm, "end": v(11.23, 11.07) * mm});
            skLineSegment(sketch, "E3659", {"start": v(11.23, 11.07) * mm, "end": v(11.25, 11) * mm});
            skLineSegment(sketch, "E3660", {"start": v(11.25, 11) * mm, "end": v(11.26, 10.95) * mm});
            skLineSegment(sketch, "E3661", {"start": v(11.26, 10.95) * mm, "end": v(11.28, 10.9) * mm});
            skLineSegment(sketch, "E3662", {"start": v(11.28, 10.9) * mm, "end": v(11.3, 10.85) * mm});
            skLineSegment(sketch, "E3663", {"start": v(11.3, 10.85) * mm, "end": v(11.3, 10.77) * mm});
            skLineSegment(sketch, "E3664", {"start": v(11.3, 10.77) * mm, "end": v(11.31, 10.72) * mm});
            skLineSegment(sketch, "E3665", {"start": v(11.31, 10.72) * mm, "end": v(11.32, 10.65) * mm});
            skLineSegment(sketch, "E3666", {"start": v(11.32, 10.65) * mm, "end": v(11.33, 10.6) * mm});
            skLineSegment(sketch, "E3667", {"start": v(11.33, 10.6) * mm, "end": v(11.34, 10.53) * mm});
            skLineSegment(sketch, "E3668", {"start": v(11.34, 10.53) * mm, "end": v(11.35, 10.48) * mm});
            skLineSegment(sketch, "E3669", {"start": v(11.35, 10.48) * mm, "end": v(11.35, 10.4) * mm});
            skLineSegment(sketch, "E3670", {"start": v(11.35, 10.4) * mm, "end": v(11.36, 10.35) * mm});
            skLineSegment(sketch, "E3671", {"start": v(11.36, 10.35) * mm, "end": v(11.37, 10.3) * mm});
            skLineSegment(sketch, "E3672", {"start": v(11.37, 10.3) * mm, "end": v(11.37, 10.23) * mm});
            skLineSegment(sketch, "E3673", {"start": v(11.37, 10.23) * mm, "end": v(11.38, 10.18) * mm});
            skLineSegment(sketch, "E3674", {"start": v(11.38, 10.18) * mm, "end": v(11.38, 10.1) * mm});
            skLineSegment(sketch, "E3675", {"start": v(11.38, 10.1) * mm, "end": v(11.38, 10.06) * mm});
            skLineSegment(sketch, "E3676", {"start": v(11.38, 10.06) * mm, "end": v(11.38, 9.98) * mm});
            skLineSegment(sketch, "E3677", {"start": v(11.38, 9.98) * mm, "end": v(11.39, 9.93) * mm});
            skLineSegment(sketch, "E3678", {"start": v(11.39, 9.93) * mm, "end": v(11.38, 9.86) * mm});
            skLineSegment(sketch, "E3679", {"start": v(11.38, 9.86) * mm, "end": v(11.39, 9.8) * mm});
            skLineSegment(sketch, "E3680", {"start": v(11.39, 9.8) * mm, "end": v(11.39, 9.76) * mm});
            skLineSegment(sketch, "E3681", {"start": v(11.39, 9.76) * mm, "end": v(11.38, 9.69) * mm});
            skLineSegment(sketch, "E3682", {"start": v(11.38, 9.69) * mm, "end": v(11.38, 9.64) * mm});
            skLineSegment(sketch, "E3683", {"start": v(11.38, 9.64) * mm, "end": v(11.38, 9.56) * mm});
            skLineSegment(sketch, "E3684", {"start": v(11.38, 9.56) * mm, "end": v(11.38, 9.51) * mm});
            skLineSegment(sketch, "E3685", {"start": v(11.38, 9.51) * mm, "end": v(11.37, 9.44) * mm});
            skLineSegment(sketch, "E3686", {"start": v(11.37, 9.44) * mm, "end": v(11.37, 9.4) * mm});
            skLineSegment(sketch, "E3687", {"start": v(11.37, 9.4) * mm, "end": v(11.36, 9.34) * mm});
            skLineSegment(sketch, "E3688", {"start": v(11.36, 9.34) * mm, "end": v(11.35, 9.27) * mm});
            skLineSegment(sketch, "E3689", {"start": v(11.35, 9.27) * mm, "end": v(11.35, 9.22) * mm});
            skLineSegment(sketch, "E3690", {"start": v(11.35, 9.22) * mm, "end": v(11.34, 9.15) * mm});
            skLineSegment(sketch, "E3691", {"start": v(11.34, 9.15) * mm, "end": v(11.33, 9.1) * mm});
            skLineSegment(sketch, "E3692", {"start": v(11.33, 9.1) * mm, "end": v(11.32, 9.03) * mm});
            skLineSegment(sketch, "E3693", {"start": v(11.32, 9.03) * mm, "end": v(11.3, 8.98) * mm});
            skLineSegment(sketch, "E3694", {"start": v(11.3, 8.98) * mm, "end": v(11.3, 8.9) * mm});
            skLineSegment(sketch, "E3695", {"start": v(11.3, 8.9) * mm, "end": v(11.28, 8.86) * mm});
            skLineSegment(sketch, "E3696", {"start": v(11.28, 8.86) * mm, "end": v(11.27, 8.8) * mm});
            skLineSegment(sketch, "E3697", {"start": v(11.27, 8.8) * mm, "end": v(11.26, 8.74) * mm});
            skLineSegment(sketch, "E3698", {"start": v(11.26, 8.74) * mm, "end": v(11.25, 8.69) * mm});
            skLineSegment(sketch, "E3699", {"start": v(11.25, 8.69) * mm, "end": v(11.23, 8.62) * mm});
            skLineSegment(sketch, "E3700", {"start": v(11.23, 8.62) * mm, "end": v(11.22, 8.57) * mm});
            skLineSegment(sketch, "E3701", {"start": v(11.22, 8.57) * mm, "end": v(11.2, 8.5) * mm});
            skLineSegment(sketch, "E3702", {"start": v(11.2, 8.5) * mm, "end": v(11.18, 8.45) * mm});
            skLineSegment(sketch, "E3703", {"start": v(11.18, 8.45) * mm, "end": v(11.16, 8.38) * mm});
            skLineSegment(sketch, "E3704", {"start": v(11.16, 8.38) * mm, "end": v(11.15, 8.34) * mm});
            skLineSegment(sketch, "E3705", {"start": v(11.15, 8.34) * mm, "end": v(11.13, 8.29) * mm});
            skLineSegment(sketch, "E3706", {"start": v(11.13, 8.29) * mm, "end": v(11.1, 8.22) * mm});
            skLineSegment(sketch, "E3707", {"start": v(11.1, 8.22) * mm, "end": v(11.1, 8.17) * mm});
            skLineSegment(sketch, "E3708", {"start": v(11.1, 8.17) * mm, "end": v(11.07, 8.1) * mm});
            skLineSegment(sketch, "E3709", {"start": v(11.07, 8.1) * mm, "end": v(11.05, 8.06) * mm});
            skLineSegment(sketch, "E3710", {"start": v(11.05, 8.06) * mm, "end": v(11.02, 7.99) * mm});
            skLineSegment(sketch, "E3711", {"start": v(11.02, 7.99) * mm, "end": v(11, 7.95) * mm});
            skLineSegment(sketch, "E3712", {"start": v(11, 7.95) * mm, "end": v(10.97, 7.88) * mm});
            skLineSegment(sketch, "E3713", {"start": v(10.97, 7.88) * mm, "end": v(10.95, 7.83) * mm});
            skLineSegment(sketch, "E3714", {"start": v(10.95, 7.83) * mm, "end": v(10.92, 7.77) * mm});
            skLineSegment(sketch, "E3715", {"start": v(10.92, 7.77) * mm, "end": v(10.9, 7.72) * mm});
            skLineSegment(sketch, "E3716", {"start": v(10.9, 7.72) * mm, "end": v(10.87, 7.65) * mm});
            skLineSegment(sketch, "E3717", {"start": v(10.87, 7.65) * mm, "end": v(10.85, 7.61) * mm});
            skLineSegment(sketch, "E3718", {"start": v(10.85, 7.61) * mm, "end": v(10.81, 7.55) * mm});
            skLineSegment(sketch, "E3719", {"start": v(10.81, 7.55) * mm, "end": v(10.79, 7.5) * mm});
            skLineSegment(sketch, "E3720", {"start": v(10.79, 7.5) * mm, "end": v(10.75, 7.44) * mm});
            skLineSegment(sketch, "E3721", {"start": v(10.75, 7.44) * mm, "end": v(10.73, 7.4) * mm});
            skLineSegment(sketch, "E3722", {"start": v(10.73, 7.4) * mm, "end": v(10.7, 7.33) * mm});
            skLineSegment(sketch, "E3723", {"start": v(10.7, 7.33) * mm, "end": v(10.67, 7.29) * mm});
            skLineSegment(sketch, "E3724", {"start": v(10.67, 7.29) * mm, "end": v(10.63, 7.23) * mm});
            skLineSegment(sketch, "E3725", {"start": v(10.63, 7.23) * mm, "end": v(10.6, 7.19) * mm});
            skLineSegment(sketch, "E3726", {"start": v(10.6, 7.19) * mm, "end": v(10.56, 7.12) * mm});
            skLineSegment(sketch, "E3727", {"start": v(10.56, 7.12) * mm, "end": v(10.53, 7.08) * mm});
            skLineSegment(sketch, "E3728", {"start": v(10.53, 7.08) * mm, "end": v(10.5, 7.02) * mm});
            skLineSegment(sketch, "E3729", {"start": v(10.5, 7.02) * mm, "end": v(10.46, 6.98) * mm});
            skLineSegment(sketch, "E3730", {"start": v(10.46, 6.98) * mm, "end": v(10.42, 6.92) * mm});
            skLineSegment(sketch, "E3731", {"start": v(10.42, 6.92) * mm, "end": v(10.4, 6.88) * mm});
            skLineSegment(sketch, "E3732", {"start": v(10.4, 6.88) * mm, "end": v(10.35, 6.82) * mm});
            skLineSegment(sketch, "E3733", {"start": v(10.35, 6.82) * mm, "end": v(10.32, 6.78) * mm});
            skLineSegment(sketch, "E3734", {"start": v(10.32, 6.78) * mm, "end": v(10.27, 6.73) * mm});
            skLineSegment(sketch, "E3735", {"start": v(10.27, 6.73) * mm, "end": v(10.24, 6.69) * mm});
            skLineSegment(sketch, "E3736", {"start": v(10.24, 6.69) * mm, "end": v(10.2, 6.63) * mm});
            skLineSegment(sketch, "E3737", {"start": v(10.2, 6.63) * mm, "end": v(10.16, 6.6) * mm});
            skLineSegment(sketch, "E3738", {"start": v(10.16, 6.6) * mm, "end": v(10.11, 6.54) * mm});
            skLineSegment(sketch, "E3739", {"start": v(10.11, 6.54) * mm, "end": v(10.08, 6.5) * mm});
            skLineSegment(sketch, "E3740", {"start": v(10.08, 6.5) * mm, "end": v(10.03, 6.45) * mm});
            skLineSegment(sketch, "E3741", {"start": v(10.03, 6.45) * mm, "end": v(10, 6.41) * mm});
            skLineSegment(sketch, "E3742", {"start": v(10, 6.41) * mm, "end": v(9.94, 6.36) * mm});
            skLineSegment(sketch, "E3743", {"start": v(9.94, 6.36) * mm, "end": v(9.9, 6.33) * mm});
            skLineSegment(sketch, "E3744", {"start": v(9.9, 6.33) * mm, "end": v(9.86, 6.28) * mm});
            skLineSegment(sketch, "E3745", {"start": v(9.86, 6.28) * mm, "end": v(9.82, 6.24) * mm});
            skLineSegment(sketch, "E3746", {"start": v(9.82, 6.24) * mm, "end": v(9.77, 6.2) * mm});
            skLineSegment(sketch, "E3747", {"start": v(9.77, 6.2) * mm, "end": v(9.73, 6.16) * mm});
            skLineSegment(sketch, "E3748", {"start": v(9.73, 6.16) * mm, "end": v(9.68, 6.11) * mm});
            skLineSegment(sketch, "E3749", {"start": v(9.68, 6.11) * mm, "end": v(9.63, 6.08) * mm});
            skLineSegment(sketch, "E3750", {"start": v(9.63, 6.08) * mm, "end": v(9.58, 6.03) * mm});
            skLineSegment(sketch, "E3751", {"start": v(9.58, 6.03) * mm, "end": v(9.54, 6) * mm});
            skLineSegment(sketch, "E3752", {"start": v(9.54, 6) * mm, "end": v(9.49, 5.95) * mm});
            skLineSegment(sketch, "E3753", {"start": v(9.49, 5.95) * mm, "end": v(9.44, 5.92) * mm});
            skLineSegment(sketch, "E3754", {"start": v(9.44, 5.92) * mm, "end": v(9.39, 5.88) * mm});
            skLineSegment(sketch, "E3755", {"start": v(9.39, 5.88) * mm, "end": v(9.34, 5.85) * mm});
            skLineSegment(sketch, "E3756", {"start": v(9.34, 5.85) * mm, "end": v(9.29, 5.8) * mm});
            skLineSegment(sketch, "E3757", {"start": v(9.29, 5.8) * mm, "end": v(9.23, 5.77) * mm});
            skLineSegment(sketch, "E3758", {"start": v(9.23, 5.77) * mm, "end": v(9.18, 5.73) * mm});
            skLineSegment(sketch, "E3759", {"start": v(9.18, 5.73) * mm, "end": v(9.09, 5.67) * mm});
            skLineSegment(sketch, "E3760", {"start": v(9.09, 5.67) * mm, "end": v(9.06, 5.65) * mm});
            skLineSegment(sketch, "E3761", {"start": v(9.06, 5.65) * mm, "end": v(8.98, 5.6) * mm});
            skLineSegment(sketch, "E3762", {"start": v(8.98, 5.6) * mm, "end": v(8.95, 5.59) * mm});
            skLineSegment(sketch, "E3763", {"start": v(8.95, 5.59) * mm, "end": v(8.88, 5.54) * mm});
            skLineSegment(sketch, "E3764", {"start": v(8.88, 5.54) * mm, "end": v(8.84, 5.52) * mm});
            skLineSegment(sketch, "E3765", {"start": v(8.84, 5.52) * mm, "end": v(8.77, 5.48) * mm});
            skLineSegment(sketch, "E3766", {"start": v(8.77, 5.48) * mm, "end": v(8.74, 5.47) * mm});
            skLineSegment(sketch, "E3767", {"start": v(8.74, 5.47) * mm, "end": v(8.66, 5.43) * mm});
            skLineSegment(sketch, "E3768", {"start": v(8.66, 5.43) * mm, "end": v(8.63, 5.4) * mm});
            skLineSegment(sketch, "E3769", {"start": v(8.63, 5.4) * mm, "end": v(8.55, 5.37) * mm});
            skLineSegment(sketch, "E3770", {"start": v(8.55, 5.37) * mm, "end": v(8.52, 5.36) * mm});
            skLineSegment(sketch, "E3771", {"start": v(8.52, 5.36) * mm, "end": v(8.44, 5.32) * mm});
            skLineSegment(sketch, "E3772", {"start": v(8.44, 5.32) * mm, "end": v(8.4, 5.3) * mm});
            skLineSegment(sketch, "E3773", {"start": v(8.4, 5.3) * mm, "end": v(8.33, 5.27) * mm});
            skLineSegment(sketch, "E3774", {"start": v(8.33, 5.27) * mm, "end": v(8.3, 5.26) * mm});
            skLineSegment(sketch, "E3775", {"start": v(8.3, 5.26) * mm, "end": v(8.21, 5.22) * mm});
            skLineSegment(sketch, "E3776", {"start": v(8.21, 5.22) * mm, "end": v(8.18, 5.21) * mm});
            skLineSegment(sketch, "E3777", {"start": v(8.18, 5.21) * mm, "end": v(8.1, 5.18) * mm});
            skLineSegment(sketch, "E3778", {"start": v(8.1, 5.18) * mm, "end": v(8.06, 5.17) * mm});
            skLineSegment(sketch, "E3779", {"start": v(8.06, 5.17) * mm, "end": v(7.98, 5.14) * mm});
            skLineSegment(sketch, "E3780", {"start": v(7.98, 5.14) * mm, "end": v(7.94, 5.13) * mm});
            skLineSegment(sketch, "E3781", {"start": v(7.94, 5.13) * mm, "end": v(7.87, 5.1) * mm});
            skLineSegment(sketch, "E3782", {"start": v(7.87, 5.1) * mm, "end": v(7.83, 5.1) * mm});
            skLineSegment(sketch, "E3783", {"start": v(7.83, 5.1) * mm, "end": v(7.75, 5.07) * mm});
            skLineSegment(sketch, "E3784", {"start": v(7.75, 5.07) * mm, "end": v(7.7, 5.06) * mm});
            skLineSegment(sketch, "E3785", {"start": v(7.7, 5.06) * mm, "end": v(7.63, 5.04) * mm});
            skLineSegment(sketch, "E3786", {"start": v(7.63, 5.04) * mm, "end": v(7.59, 5.03) * mm});
            skLineSegment(sketch, "E3787", {"start": v(7.59, 5.03) * mm, "end": v(7.51, 5) * mm});
            skLineSegment(sketch, "E3788", {"start": v(7.51, 5) * mm, "end": v(7.47, 5) * mm});
            skLineSegment(sketch, "E3789", {"start": v(7.47, 5) * mm, "end": v(7.4, 4.98) * mm});
            skLineSegment(sketch, "E3790", {"start": v(7.4, 4.98) * mm, "end": v(7.35, 4.97) * mm});
            skLineSegment(sketch, "E3791", {"start": v(7.35, 4.97) * mm, "end": v(7.27, 4.96) * mm});
            skLineSegment(sketch, "E3792", {"start": v(7.27, 4.96) * mm, "end": v(7.23, 4.95) * mm});
            skLineSegment(sketch, "E3793", {"start": v(7.23, 4.95) * mm, "end": v(7.15, 4.94) * mm});
            skLineSegment(sketch, "E3794", {"start": v(7.15, 4.94) * mm, "end": v(7.1, 4.93) * mm});
            skLineSegment(sketch, "E3795", {"start": v(7.1, 4.93) * mm, "end": v(7.03, 4.92) * mm});
            skLineSegment(sketch, "E3796", {"start": v(7.03, 4.92) * mm, "end": v(6.98, 4.92) * mm});
            skLineSegment(sketch, "E3797", {"start": v(6.98, 4.92) * mm, "end": v(6.9, 4.9) * mm});
            skLineSegment(sketch, "E3798", {"start": v(6.9, 4.9) * mm, "end": v(6.86, 4.9) * mm});
            skLineSegment(sketch, "E3799", {"start": v(6.86, 4.9) * mm, "end": v(6.78, 4.9) * mm});
            skLineSegment(sketch, "E3800", {"start": v(6.78, 4.9) * mm, "end": v(6.74, 4.9) * mm});
            skLineSegment(sketch, "E3801", {"start": v(6.74, 4.9) * mm, "end": v(6.66, 4.89) * mm});
            skLineSegment(sketch, "E3802", {"start": v(6.66, 4.89) * mm, "end": v(6.61, 4.89) * mm});
            skLineSegment(sketch, "E3803", {"start": v(6.61, 4.89) * mm, "end": v(6.54, 4.88) * mm});
            skLineSegment(sketch, "E3804", {"start": v(6.54, 4.88) * mm, "end": v(6.5, 4.88) * mm});
            skLineSegment(sketch, "E3805", {"start": v(6.5, 4.88) * mm, "end": v(6.42, 4.88) * mm});
            skLineSegment(sketch, "E3806", {"start": v(6.42, 4.88) * mm, "end": v(6.37, 4.88) * mm});
            skLineSegment(sketch, "E3807", {"start": v(6.37, 4.88) * mm, "end": v(6.3, 4.88) * mm});
            skLineSegment(sketch, "E3808", {"start": v(6.3, 4.88) * mm, "end": v(6.24, 4.88) * mm});
            skLineSegment(sketch, "E3809", {"start": v(6.24, 4.88) * mm, "end": v(6.17, 4.89) * mm});
            skLineSegment(sketch, "E3810", {"start": v(6.17, 4.89) * mm, "end": v(6.12, 4.89) * mm});
            skLineSegment(sketch, "E3811", {"start": v(6.12, 4.89) * mm, "end": v(6.05, 4.9) * mm});
            skLineSegment(sketch, "E3812", {"start": v(6.05, 4.9) * mm, "end": v(6, 4.9) * mm});
            skLineSegment(sketch, "E3813", {"start": v(6, 4.9) * mm, "end": v(5.92, 4.9) * mm});
            skLineSegment(sketch, "E3814", {"start": v(5.92, 4.9) * mm, "end": v(5.87, 4.9) * mm});
            skLineSegment(sketch, "E3815", {"start": v(5.87, 4.9) * mm, "end": v(5.8, 4.92) * mm});
            skLineSegment(sketch, "E3816", {"start": v(5.8, 4.92) * mm, "end": v(5.75, 4.92) * mm});
            skLineSegment(sketch, "E3817", {"start": v(5.75, 4.92) * mm, "end": v(5.68, 4.93) * mm});
            skLineSegment(sketch, "E3818", {"start": v(5.68, 4.93) * mm, "end": v(5.63, 4.94) * mm});
            skLineSegment(sketch, "E3819", {"start": v(5.63, 4.94) * mm, "end": v(5.56, 4.95) * mm});
            skLineSegment(sketch, "E3820", {"start": v(5.56, 4.95) * mm, "end": v(5.5, 4.96) * mm});
            skLineSegment(sketch, "E3821", {"start": v(5.5, 4.96) * mm, "end": v(5.44, 4.97) * mm});
            skLineSegment(sketch, "E3822", {"start": v(5.44, 4.97) * mm, "end": v(5.39, 4.98) * mm});
            skLineSegment(sketch, "E3823", {"start": v(5.39, 4.98) * mm, "end": v(5.32, 5) * mm});
            skLineSegment(sketch, "E3824", {"start": v(5.32, 5) * mm, "end": v(5.27, 5) * mm});
            skLineSegment(sketch, "E3825", {"start": v(5.27, 5) * mm, "end": v(5.2, 5.02) * mm});
            skLineSegment(sketch, "E3826", {"start": v(5.2, 5.02) * mm, "end": v(5.15, 5.04) * mm});
            skLineSegment(sketch, "E3827", {"start": v(5.15, 5.04) * mm, "end": v(5.08, 5.05) * mm});
            skLineSegment(sketch, "E3828", {"start": v(5.08, 5.05) * mm, "end": v(5.03, 5.07) * mm});
            skLineSegment(sketch, "E3829", {"start": v(5.03, 5.07) * mm, "end": v(4.96, 5.09) * mm});
            skLineSegment(sketch, "E3830", {"start": v(4.96, 5.09) * mm, "end": v(4.91, 5.1) * mm});
            skLineSegment(sketch, "E3831", {"start": v(4.91, 5.1) * mm, "end": v(4.85, 5.12) * mm});
            skLineSegment(sketch, "E3832", {"start": v(4.85, 5.12) * mm, "end": v(4.8, 5.14) * mm});
            skLineSegment(sketch, "E3833", {"start": v(4.8, 5.14) * mm, "end": v(4.73, 5.16) * mm});
            skLineSegment(sketch, "E3834", {"start": v(4.73, 5.16) * mm, "end": v(4.68, 5.18) * mm});
            skLineSegment(sketch, "E3835", {"start": v(4.68, 5.18) * mm, "end": v(4.61, 5.2) * mm});
            skLineSegment(sketch, "E3836", {"start": v(4.61, 5.2) * mm, "end": v(4.56, 5.23) * mm});
            skLineSegment(sketch, "E3837", {"start": v(4.56, 5.23) * mm, "end": v(4.5, 5.25) * mm});
            skLineSegment(sketch, "E3838", {"start": v(4.5, 5.25) * mm, "end": v(4.45, 5.27) * mm});
            skLineSegment(sketch, "E3839", {"start": v(4.45, 5.27) * mm, "end": v(4.39, 5.3) * mm});
            skLineSegment(sketch, "E3840", {"start": v(4.39, 5.3) * mm, "end": v(4.34, 5.32) * mm});
            skLineSegment(sketch, "E3841", {"start": v(4.34, 5.32) * mm, "end": v(4.28, 5.35) * mm});
            skLineSegment(sketch, "E3842", {"start": v(4.28, 5.35) * mm, "end": v(4.25, 5.36) * mm});
            skLineSegment(sketch, "E3843", {"start": v(4.25, 5.36) * mm, "end": v(4.22, 5.38) * mm});
            skLineSegment(sketch, "E3844", {"start": v(4.22, 5.38) * mm, "end": v(4.2, 5.24) * mm});
            skLineSegment(sketch, "E3845", {"start": v(4.2, 5.24) * mm, "end": v(4.13, 4.82) * mm});
            skLineSegment(sketch, "E3846", {"start": v(4.13, 4.82) * mm, "end": v(4.02, 4.18) * mm});
            skLineSegment(sketch, "E3847", {"start": v(4.02, 4.18) * mm, "end": v(3.97, 3.8) * mm});
            skLineSegment(sketch, "E3848", {"start": v(3.97, 3.8) * mm, "end": v(3.9, 3.34) * mm});
            skLineSegment(sketch, "E3849", {"start": v(3.9, 3.34) * mm, "end": v(3.9, 3.3) * mm});
            skLineSegment(sketch, "E3850", {"start": v(3.9, 3.3) * mm, "end": v(3.9, 3.29) * mm});
            skLineSegment(sketch, "E3851", {"start": v(3.9, 3.29) * mm, "end": v(3.85, 2.73) * mm});
            skLineSegment(sketch, "E3852", {"start": v(3.85, 2.73) * mm, "end": v(3.8, 2.38) * mm});
            skLineSegment(sketch, "E3853", {"start": v(3.8, 2.38) * mm, "end": v(3.76, 1.82) * mm});
            skLineSegment(sketch, "E3854", {"start": v(3.76, 1.82) * mm, "end": v(3.73, 1.48) * mm});
            skLineSegment(sketch, "E3855", {"start": v(3.73, 1.48) * mm, "end": v(3.7, 1.13) * mm});
            skLineSegment(sketch, "E3856", {"start": v(3.7, 1.13) * mm, "end": v(3.67, 0.57) * mm});
            skLineSegment(sketch, "E3857", {"start": v(3.67, 0.57) * mm, "end": v(3.66, 0.22) * mm});
            skLineSegment(sketch, "E3858", {"start": v(3.66, 0.22) * mm, "end": v(3.64, -0.34) * mm});
            skLineSegment(sketch, "E3859", {"start": v(3.64, -0.34) * mm, "end": v(3.63, -0.9) * mm});
            skLineSegment(sketch, "E3860", {"start": v(3.63, -0.9) * mm, "end": v(3.63, -1.24) * mm});
            skLineSegment(sketch, "E3861", {"start": v(3.63, -1.24) * mm, "end": v(3.64, -1.8) * mm});
            skLineSegment(sketch, "E3862", {"start": v(3.64, -1.8) * mm, "end": v(3.64, -2.15) * mm});
            skLineSegment(sketch, "E3863", {"start": v(3.64, -2.15) * mm, "end": v(3.66, -2.71) * mm});
            skLineSegment(sketch, "E3864", {"start": v(3.66, -2.71) * mm, "end": v(3.67, -3.06) * mm});
            skLineSegment(sketch, "E3865", {"start": v(3.67, -3.06) * mm, "end": v(3.7, -3.62) * mm});
            skLineSegment(sketch, "E3866", {"start": v(3.7, -3.62) * mm, "end": v(3.73, -3.97) * mm});
            skLineSegment(sketch, "E3867", {"start": v(3.73, -3.97) * mm, "end": v(3.78, -4.52) * mm});
            skLineSegment(sketch, "E3868", {"start": v(3.78, -4.52) * mm, "end": v(3.8, -4.87) * mm});
            skLineSegment(sketch, "E3869", {"start": v(3.8, -4.87) * mm, "end": v(3.85, -5.22) * mm});
            skLineSegment(sketch, "E3870", {"start": v(3.85, -5.22) * mm, "end": v(3.9, -5.77) * mm});
            skLineSegment(sketch, "E3871", {"start": v(3.9, -5.77) * mm, "end": v(3.95, -6.12) * mm});
            skLineSegment(sketch, "E3872", {"start": v(3.95, -6.12) * mm, "end": v(4.03, -6.67) * mm});
            skLineSegment(sketch, "E3873", {"start": v(4.03, -6.67) * mm, "end": v(4.08, -7.02) * mm});
            skLineSegment(sketch, "E3874", {"start": v(4.08, -7.02) * mm, "end": v(4.17, -7.57) * mm});
            skLineSegment(sketch, "E3875", {"start": v(4.17, -7.57) * mm, "end": v(4.24, -7.91) * mm});
            skLineSegment(sketch, "E3876", {"start": v(4.24, -7.91) * mm, "end": v(4.34, -8.46) * mm});
            skLineSegment(sketch, "E3877", {"start": v(4.34, -8.46) * mm, "end": v(4.41, -8.8) * mm});
            skLineSegment(sketch, "E3878", {"start": v(4.41, -8.8) * mm, "end": v(4.53, -9.35) * mm});
            skLineSegment(sketch, "E3879", {"start": v(4.53, -9.35) * mm, "end": v(4.6, -9.69) * mm});
            skLineSegment(sketch, "E3880", {"start": v(4.6, -9.69) * mm, "end": v(4.74, -10.23) * mm});
            skLineSegment(sketch, "E3881", {"start": v(4.74, -10.23) * mm, "end": v(4.88, -10.78) * mm});
            skLineSegment(sketch, "E3882", {"start": v(4.88, -10.78) * mm, "end": v(4.97, -11.11) * mm});
            skLineSegment(sketch, "E3883", {"start": v(4.97, -11.11) * mm, "end": v(5.13, -11.65) * mm});
            skLineSegment(sketch, "E3884", {"start": v(5.13, -11.65) * mm, "end": v(5.22, -11.98) * mm});
            skLineSegment(sketch, "E3885", {"start": v(5.22, -11.98) * mm, "end": v(5.33, -12.32) * mm});
            skLineSegment(sketch, "E3886", {"start": v(5.33, -12.32) * mm, "end": v(5.5, -12.85) * mm});
            skLineSegment(sketch, "E3887", {"start": v(5.5, -12.85) * mm, "end": v(5.68, -13.38) * mm});
            skLineSegment(sketch, "E3888", {"start": v(5.68, -13.38) * mm, "end": v(5.8, -13.7) * mm});
            skLineSegment(sketch, "E3889", {"start": v(5.8, -13.7) * mm, "end": v(5.99, -14.23) * mm});
            skLineSegment(sketch, "E3890", {"start": v(5.99, -14.23) * mm, "end": v(6.1, -14.56) * mm});
            skLineSegment(sketch, "E3891", {"start": v(6.1, -14.56) * mm, "end": v(6.32, -15.08) * mm});
            skLineSegment(sketch, "E3892", {"start": v(6.32, -15.08) * mm, "end": v(6.45, -15.4) * mm});
            skLineSegment(sketch, "E3893", {"start": v(6.45, -15.4) * mm, "end": v(6.58, -15.72) * mm});
            skLineSegment(sketch, "E3894", {"start": v(6.58, -15.72) * mm, "end": v(6.8, -16.24) * mm});
            skLineSegment(sketch, "E3895", {"start": v(6.8, -16.24) * mm, "end": v(6.95, -16.55) * mm});
            skLineSegment(sketch, "E3896", {"start": v(6.95, -16.55) * mm, "end": v(7.18, -17.06) * mm});
            skLineSegment(sketch, "E3897", {"start": v(7.18, -17.06) * mm, "end": v(7.43, -17.57) * mm});
            skLineSegment(sketch, "E3898", {"start": v(7.43, -17.57) * mm, "end": v(7.58, -17.88) * mm});
            skLineSegment(sketch, "E3899", {"start": v(7.58, -17.88) * mm, "end": v(7.84, -18.38) * mm});
            skLineSegment(sketch, "E3900", {"start": v(7.84, -18.38) * mm, "end": v(8, -18.69) * mm});
            skLineSegment(sketch, "E3901", {"start": v(8, -18.69) * mm, "end": v(8.17, -19) * mm});
            skLineSegment(sketch, "E3902", {"start": v(8.17, -19) * mm, "end": v(8.44, -19.48) * mm});
            skLineSegment(sketch, "E3903", {"start": v(8.44, -19.48) * mm, "end": v(8.72, -19.97) * mm});
            skLineSegment(sketch, "E3904", {"start": v(8.72, -19.97) * mm, "end": v(8.9, -20.27) * mm});
            skLineSegment(sketch, "E3905", {"start": v(8.9, -20.27) * mm, "end": v(9.08, -20.56) * mm});
            skLineSegment(sketch, "E3906", {"start": v(9.08, -20.56) * mm, "end": v(9.37, -21.04) * mm});
            skLineSegment(sketch, "E3907", {"start": v(9.37, -21.04) * mm, "end": v(9.56, -21.33) * mm});
            skLineSegment(sketch, "E3908", {"start": v(9.56, -21.33) * mm, "end": v(9.86, -21.8) * mm});
            skLineSegment(sketch, "E3909", {"start": v(9.86, -21.8) * mm, "end": v(10.18, -22.26) * mm});
            skLineSegment(sketch, "E3910", {"start": v(10.18, -22.26) * mm, "end": v(10.38, -22.55) * mm});
            skLineSegment(sketch, "E3911", {"start": v(10.38, -22.55) * mm, "end": v(10.52, -22.75) * mm});
            skLineSegment(sketch, "E3912", {"start": v(10.52, -22.75) * mm, "end": v(10.65, -22.92) * mm});
            skLineSegment(sketch, "E3913", {"start": v(10.65, -22.92) * mm, "end": v(10.73, -23.03) * mm});
            skLineSegment(sketch, "E3914", {"start": v(10.73, -23.03) * mm, "end": v(10.91, -23.29) * mm});
            skLineSegment(sketch, "E3915", {"start": v(10.91, -23.29) * mm, "end": v(11, -23.4) * mm});
            skLineSegment(sketch, "E3916", {"start": v(11, -23.4) * mm, "end": v(11.18, -23.64) * mm});
            skLineSegment(sketch, "E3917", {"start": v(11.18, -23.64) * mm, "end": v(11.28, -23.78) * mm});
            skLineSegment(sketch, "E3918", {"start": v(11.28, -23.78) * mm, "end": v(11.46, -24) * mm});
            skLineSegment(sketch, "E3919", {"start": v(11.46, -24) * mm, "end": v(11.56, -24.13) * mm});
            skLineSegment(sketch, "E3920", {"start": v(11.56, -24.13) * mm, "end": v(11.78, -24.4) * mm});
            skLineSegment(sketch, "E3921", {"start": v(11.78, -24.4) * mm, "end": v(11.95, -24.63) * mm});
            skLineSegment(sketch, "E3922", {"start": v(11.95, -24.63) * mm, "end": v(12.14, -24.84) * mm});
            skLineSegment(sketch, "E3923", {"start": v(12.14, -24.84) * mm, "end": v(12.57, -25.33) * mm});
            skLineSegment(sketch, "E3924", {"start": v(12.57, -25.33) * mm, "end": v(12.64, -25.41) * mm});
            skLineSegment(sketch, "E3925", {"start": v(12.64, -25.41) * mm, "end": v(12.77, -25.57) * mm});
            skLineSegment(sketch, "E3926", {"start": v(12.77, -25.57) * mm, "end": v(12.97, -25.8) * mm});
            skLineSegment(sketch, "E3927", {"start": v(12.97, -25.8) * mm, "end": v(13.05, -25.9) * mm});
            skLineSegment(sketch, "E3928", {"start": v(13.05, -25.9) * mm, "end": v(13.73, -26.59) * mm});
            skLineSegment(sketch, "E3929", {"start": v(13.73, -26.59) * mm, "end": v(13.77, -26.63) * mm});
            skLineSegment(sketch, "E3930", {"start": v(54.4, -33.42) * mm, "end": v(54.35, -33.44) * mm});
            skSolve(sketch);
        }
        {
            var Q0;
            Q0=makeQuery(id+"F0.imprint","IMPRINT",FACE,{"disambiguationData":[TD([[makeQuery(id+"F0.imprint","IMPRINT",EDGE,{"derivedFrom":sQuery(id+"F0.wireOp",EDGE,"E0")}),1.0]])]});
            extrude(context, id + "F1", {"entities" : qUnion([Q0]), "depth" : 25 * mm});
        }
        {
            var Q0;
            Q0=makeQuery(id+"F0.imprint","IMPRINT",FACE,{"disambiguationData":[TD([[makeQuery(id+"F0.imprint","IMPRINT",EDGE,{"derivedFrom":sQuery(id+"F0.wireOp",EDGE,"E665")}),1.0]])]});
            extrude(context, id + "F2", {"entities" : qUnion([Q0]), "depth" : 25 * mm});
        }
        {
            var Q0;
            Q0=makeQuery(id+"F1.opExtrude","CAP_FACE",FACE,{"disambiguationData":[OSD([sQuery(id+"F0.wireOp",EDGE,"E0"),sQuery(id+"F0.wireOp",EDGE,"E1"),sQuery(id+"F0.wireOp",EDGE,"E2"),sQuery(id+"F0.wireOp",EDGE,"E3"),sQuery(id+"F0.wireOp",EDGE,"E4"),sQuery(id+"F0.wireOp",EDGE,"E5"),sQuery(id+"F0.wireOp",EDGE,"E6"),sQuery(id+"F0.wireOp",EDGE,"E7"),sQuery(id+"F0.wireOp",EDGE,"E8"),sQuery(id+"F0.wireOp",EDGE,"E9"),sQuery(id+"F0.wireOp",EDGE,"E10"),sQuery(id+"F0.wireOp",EDGE,"E11"),sQuery(id+"F0.wireOp",EDGE,"E12"),sQuery(id+"F0.wireOp",EDGE,"E13"),sQuery(id+"F0.wireOp",EDGE,"E14"),sQuery(id+"F0.wireOp",EDGE,"E15"),sQuery(id+"F0.wireOp",EDGE,"E16"),sQuery(id+"F0.wireOp",EDGE,"E17"),sQuery(id+"F0.wireOp",EDGE,"E18"),sQuery(id+"F0.wireOp",EDGE,"E19"),sQuery(id+"F0.wireOp",EDGE,"E20"),sQuery(id+"F0.wireOp",EDGE,"E21"),sQuery(id+"F0.wireOp",EDGE,"E22"),sQuery(id+"F0.wireOp",EDGE,"E23"),sQuery(id+"F0.wireOp",EDGE,"E24"),sQuery(id+"F0.wireOp",EDGE,"E25"),sQuery(id+"F0.wireOp",EDGE,"E26"),sQuery(id+"F0.wireOp",EDGE,"E27"),sQuery(id+"F0.wireOp",EDGE,"E28"),sQuery(id+"F0.wireOp",EDGE,"E29"),sQuery(id+"F0.wireOp",EDGE,"E30"),sQuery(id+"F0.wireOp",EDGE,"E31"),sQuery(id+"F0.wireOp",EDGE,"E32"),sQuery(id+"F0.wireOp",EDGE,"E33"),sQuery(id+"F0.wireOp",EDGE,"E34"),sQuery(id+"F0.wireOp",EDGE,"E35"),sQuery(id+"F0.wireOp",EDGE,"E36"),sQuery(id+"F0.wireOp",EDGE,"E37"),sQuery(id+"F0.wireOp",EDGE,"E38"),sQuery(id+"F0.wireOp",EDGE,"E39"),sQuery(id+"F0.wireOp",EDGE,"E40"),sQuery(id+"F0.wireOp",EDGE,"E41"),sQuery(id+"F0.wireOp",EDGE,"E42"),sQuery(id+"F0.wireOp",EDGE,"E43"),sQuery(id+"F0.wireOp",EDGE,"E44"),sQuery(id+"F0.wireOp",EDGE,"E45"),sQuery(id+"F0.wireOp",EDGE,"E46"),sQuery(id+"F0.wireOp",EDGE,"E47"),sQuery(id+"F0.wireOp",EDGE,"E48"),sQuery(id+"F0.wireOp",EDGE,"E49"),sQuery(id+"F0.wireOp",EDGE,"E50"),sQuery(id+"F0.wireOp",EDGE,"E51"),sQuery(id+"F0.wireOp",EDGE,"E52"),sQuery(id+"F0.wireOp",EDGE,"E53"),sQuery(id+"F0.wireOp",EDGE,"E54"),sQuery(id+"F0.wireOp",EDGE,"E55"),sQuery(id+"F0.wireOp",EDGE,"E56"),sQuery(id+"F0.wireOp",EDGE,"E57"),sQuery(id+"F0.wireOp",EDGE,"E58"),sQuery(id+"F0.wireOp",EDGE,"E59"),sQuery(id+"F0.wireOp",EDGE,"E60"),sQuery(id+"F0.wireOp",EDGE,"E61"),sQuery(id+"F0.wireOp",EDGE,"E62"),sQuery(id+"F0.wireOp",EDGE,"E63"),sQuery(id+"F0.wireOp",EDGE,"E64"),sQuery(id+"F0.wireOp",EDGE,"E65"),sQuery(id+"F0.wireOp",EDGE,"E66"),sQuery(id+"F0.wireOp",EDGE,"E67"),sQuery(id+"F0.wireOp",EDGE,"E68"),sQuery(id+"F0.wireOp",EDGE,"E69"),sQuery(id+"F0.wireOp",EDGE,"E70"),sQuery(id+"F0.wireOp",EDGE,"E71"),sQuery(id+"F0.wireOp",EDGE,"E72"),sQuery(id+"F0.wireOp",EDGE,"E73"),sQuery(id+"F0.wireOp",EDGE,"E74"),sQuery(id+"F0.wireOp",EDGE,"E75"),sQuery(id+"F0.wireOp",EDGE,"E76"),sQuery(id+"F0.wireOp",EDGE,"E77"),sQuery(id+"F0.wireOp",EDGE,"E78"),sQuery(id+"F0.wireOp",EDGE,"E79"),sQuery(id+"F0.wireOp",EDGE,"E80"),sQuery(id+"F0.wireOp",EDGE,"E81"),sQuery(id+"F0.wireOp",EDGE,"E82"),sQuery(id+"F0.wireOp",EDGE,"E83"),sQuery(id+"F0.wireOp",EDGE,"E84"),sQuery(id+"F0.wireOp",EDGE,"E85"),sQuery(id+"F0.wireOp",EDGE,"E86"),sQuery(id+"F0.wireOp",EDGE,"E87"),sQuery(id+"F0.wireOp",EDGE,"E88"),sQuery(id+"F0.wireOp",EDGE,"E89"),sQuery(id+"F0.wireOp",EDGE,"E90"),sQuery(id+"F0.wireOp",EDGE,"E91"),sQuery(id+"F0.wireOp",EDGE,"E92"),sQuery(id+"F0.wireOp",EDGE,"E93"),sQuery(id+"F0.wireOp",EDGE,"E94"),sQuery(id+"F0.wireOp",EDGE,"E95"),sQuery(id+"F0.wireOp",EDGE,"E96"),sQuery(id+"F0.wireOp",EDGE,"E97"),sQuery(id+"F0.wireOp",EDGE,"E98"),sQuery(id+"F0.wireOp",EDGE,"E99"),sQuery(id+"F0.wireOp",EDGE,"E100"),sQuery(id+"F0.wireOp",EDGE,"E101"),sQuery(id+"F0.wireOp",EDGE,"E102"),sQuery(id+"F0.wireOp",EDGE,"E103"),sQuery(id+"F0.wireOp",EDGE,"E104"),sQuery(id+"F0.wireOp",EDGE,"E105"),sQuery(id+"F0.wireOp",EDGE,"E106"),sQuery(id+"F0.wireOp",EDGE,"E107"),sQuery(id+"F0.wireOp",EDGE,"E108"),sQuery(id+"F0.wireOp",EDGE,"E109"),sQuery(id+"F0.wireOp",EDGE,"E110"),sQuery(id+"F0.wireOp",EDGE,"E111"),sQuery(id+"F0.wireOp",EDGE,"E112"),sQuery(id+"F0.wireOp",EDGE,"E113"),sQuery(id+"F0.wireOp",EDGE,"E114"),sQuery(id+"F0.wireOp",EDGE,"E115"),sQuery(id+"F0.wireOp",EDGE,"E116"),sQuery(id+"F0.wireOp",EDGE,"E117"),sQuery(id+"F0.wireOp",EDGE,"E118"),sQuery(id+"F0.wireOp",EDGE,"E119"),sQuery(id+"F0.wireOp",EDGE,"E120"),sQuery(id+"F0.wireOp",EDGE,"E121"),sQuery(id+"F0.wireOp",EDGE,"E122"),sQuery(id+"F0.wireOp",EDGE,"E123"),sQuery(id+"F0.wireOp",EDGE,"E124"),sQuery(id+"F0.wireOp",EDGE,"E125"),sQuery(id+"F0.wireOp",EDGE,"E126"),sQuery(id+"F0.wireOp",EDGE,"E127"),sQuery(id+"F0.wireOp",EDGE,"E128"),sQuery(id+"F0.wireOp",EDGE,"E129"),sQuery(id+"F0.wireOp",EDGE,"E130"),sQuery(id+"F0.wireOp",EDGE,"E131"),sQuery(id+"F0.wireOp",EDGE,"E132"),sQuery(id+"F0.wireOp",EDGE,"E133"),sQuery(id+"F0.wireOp",EDGE,"E134"),sQuery(id+"F0.wireOp",EDGE,"E135"),sQuery(id+"F0.wireOp",EDGE,"E136"),sQuery(id+"F0.wireOp",EDGE,"E137"),sQuery(id+"F0.wireOp",EDGE,"E138"),sQuery(id+"F0.wireOp",EDGE,"E139"),sQuery(id+"F0.wireOp",EDGE,"E140"),sQuery(id+"F0.wireOp",EDGE,"E141"),sQuery(id+"F0.wireOp",EDGE,"E142"),sQuery(id+"F0.wireOp",EDGE,"E143"),sQuery(id+"F0.wireOp",EDGE,"E144"),sQuery(id+"F0.wireOp",EDGE,"E145"),sQuery(id+"F0.wireOp",EDGE,"E146"),sQuery(id+"F0.wireOp",EDGE,"E147"),sQuery(id+"F0.wireOp",EDGE,"E148"),sQuery(id+"F0.wireOp",EDGE,"E149"),sQuery(id+"F0.wireOp",EDGE,"E150"),sQuery(id+"F0.wireOp",EDGE,"E151"),sQuery(id+"F0.wireOp",EDGE,"E152"),sQuery(id+"F0.wireOp",EDGE,"E153"),sQuery(id+"F0.wireOp",EDGE,"E154"),sQuery(id+"F0.wireOp",EDGE,"E155"),sQuery(id+"F0.wireOp",EDGE,"E156"),sQuery(id+"F0.wireOp",EDGE,"E157"),sQuery(id+"F0.wireOp",EDGE,"E158"),sQuery(id+"F0.wireOp",EDGE,"E159"),sQuery(id+"F0.wireOp",EDGE,"E160"),sQuery(id+"F0.wireOp",EDGE,"E161"),sQuery(id+"F0.wireOp",EDGE,"E162"),sQuery(id+"F0.wireOp",EDGE,"E163"),sQuery(id+"F0.wireOp",EDGE,"E164"),sQuery(id+"F0.wireOp",EDGE,"E165"),sQuery(id+"F0.wireOp",EDGE,"E166"),sQuery(id+"F0.wireOp",EDGE,"E167"),sQuery(id+"F0.wireOp",EDGE,"E168"),sQuery(id+"F0.wireOp",EDGE,"E169"),sQuery(id+"F0.wireOp",EDGE,"E170"),sQuery(id+"F0.wireOp",EDGE,"E171"),sQuery(id+"F0.wireOp",EDGE,"E172"),sQuery(id+"F0.wireOp",EDGE,"E173"),sQuery(id+"F0.wireOp",EDGE,"E174"),sQuery(id+"F0.wireOp",EDGE,"E175"),sQuery(id+"F0.wireOp",EDGE,"E176"),sQuery(id+"F0.wireOp",EDGE,"E177"),sQuery(id+"F0.wireOp",EDGE,"E178"),sQuery(id+"F0.wireOp",EDGE,"E179"),sQuery(id+"F0.wireOp",EDGE,"E180"),sQuery(id+"F0.wireOp",EDGE,"E181"),sQuery(id+"F0.wireOp",EDGE,"E182"),sQuery(id+"F0.wireOp",EDGE,"E183"),sQuery(id+"F0.wireOp",EDGE,"E184"),sQuery(id+"F0.wireOp",EDGE,"E185"),sQuery(id+"F0.wireOp",EDGE,"E186"),sQuery(id+"F0.wireOp",EDGE,"E187"),sQuery(id+"F0.wireOp",EDGE,"E188"),sQuery(id+"F0.wireOp",EDGE,"E189"),sQuery(id+"F0.wireOp",EDGE,"E190"),sQuery(id+"F0.wireOp",EDGE,"E191"),sQuery(id+"F0.wireOp",EDGE,"E192"),sQuery(id+"F0.wireOp",EDGE,"E193"),sQuery(id+"F0.wireOp",EDGE,"E194"),sQuery(id+"F0.wireOp",EDGE,"E195"),sQuery(id+"F0.wireOp",EDGE,"E196"),sQuery(id+"F0.wireOp",EDGE,"E197"),sQuery(id+"F0.wireOp",EDGE,"E198"),sQuery(id+"F0.wireOp",EDGE,"E199"),sQuery(id+"F0.wireOp",EDGE,"E200"),sQuery(id+"F0.wireOp",EDGE,"E201"),sQuery(id+"F0.wireOp",EDGE,"E202"),sQuery(id+"F0.wireOp",EDGE,"E203"),sQuery(id+"F0.wireOp",EDGE,"E204"),sQuery(id+"F0.wireOp",EDGE,"E205"),sQuery(id+"F0.wireOp",EDGE,"E206"),sQuery(id+"F0.wireOp",EDGE,"E207"),sQuery(id+"F0.wireOp",EDGE,"E208"),sQuery(id+"F0.wireOp",EDGE,"E209"),sQuery(id+"F0.wireOp",EDGE,"E210"),sQuery(id+"F0.wireOp",EDGE,"E211"),sQuery(id+"F0.wireOp",EDGE,"E212"),sQuery(id+"F0.wireOp",EDGE,"E213"),sQuery(id+"F0.wireOp",EDGE,"E214"),sQuery(id+"F0.wireOp",EDGE,"E215"),sQuery(id+"F0.wireOp",EDGE,"E216"),sQuery(id+"F0.wireOp",EDGE,"E217"),sQuery(id+"F0.wireOp",EDGE,"E218"),sQuery(id+"F0.wireOp",EDGE,"E219"),sQuery(id+"F0.wireOp",EDGE,"E220"),sQuery(id+"F0.wireOp",EDGE,"E221"),sQuery(id+"F0.wireOp",EDGE,"E222"),sQuery(id+"F0.wireOp",EDGE,"E223"),sQuery(id+"F0.wireOp",EDGE,"E224"),sQuery(id+"F0.wireOp",EDGE,"E225"),sQuery(id+"F0.wireOp",EDGE,"E226"),sQuery(id+"F0.wireOp",EDGE,"E227"),sQuery(id+"F0.wireOp",EDGE,"E228"),sQuery(id+"F0.wireOp",EDGE,"E229"),sQuery(id+"F0.wireOp",EDGE,"E230"),sQuery(id+"F0.wireOp",EDGE,"E231"),sQuery(id+"F0.wireOp",EDGE,"E232"),sQuery(id+"F0.wireOp",EDGE,"E233"),sQuery(id+"F0.wireOp",EDGE,"E234"),sQuery(id+"F0.wireOp",EDGE,"E235"),sQuery(id+"F0.wireOp",EDGE,"E236"),sQuery(id+"F0.wireOp",EDGE,"E237"),sQuery(id+"F0.wireOp",EDGE,"E238"),sQuery(id+"F0.wireOp",EDGE,"E239"),sQuery(id+"F0.wireOp",EDGE,"E240"),sQuery(id+"F0.wireOp",EDGE,"E241"),sQuery(id+"F0.wireOp",EDGE,"E242"),sQuery(id+"F0.wireOp",EDGE,"E243"),sQuery(id+"F0.wireOp",EDGE,"E244"),sQuery(id+"F0.wireOp",EDGE,"E245"),sQuery(id+"F0.wireOp",EDGE,"E246"),sQuery(id+"F0.wireOp",EDGE,"E247"),sQuery(id+"F0.wireOp",EDGE,"E248"),sQuery(id+"F0.wireOp",EDGE,"E249"),sQuery(id+"F0.wireOp",EDGE,"E250"),sQuery(id+"F0.wireOp",EDGE,"E251"),sQuery(id+"F0.wireOp",EDGE,"E252"),sQuery(id+"F0.wireOp",EDGE,"E253"),sQuery(id+"F0.wireOp",EDGE,"E254"),sQuery(id+"F0.wireOp",EDGE,"E255"),sQuery(id+"F0.wireOp",EDGE,"E256"),sQuery(id+"F0.wireOp",EDGE,"E257"),sQuery(id+"F0.wireOp",EDGE,"E258"),sQuery(id+"F0.wireOp",EDGE,"E259"),sQuery(id+"F0.wireOp",EDGE,"E260"),sQuery(id+"F0.wireOp",EDGE,"E261"),sQuery(id+"F0.wireOp",EDGE,"E262"),sQuery(id+"F0.wireOp",EDGE,"E263"),sQuery(id+"F0.wireOp",EDGE,"E264"),sQuery(id+"F0.wireOp",EDGE,"E265"),sQuery(id+"F0.wireOp",EDGE,"E266"),sQuery(id+"F0.wireOp",EDGE,"E267"),sQuery(id+"F0.wireOp",EDGE,"E268"),sQuery(id+"F0.wireOp",EDGE,"E269"),sQuery(id+"F0.wireOp",EDGE,"E270"),sQuery(id+"F0.wireOp",EDGE,"E271"),sQuery(id+"F0.wireOp",EDGE,"E272"),sQuery(id+"F0.wireOp",EDGE,"E273"),sQuery(id+"F0.wireOp",EDGE,"E274"),sQuery(id+"F0.wireOp",EDGE,"E275"),sQuery(id+"F0.wireOp",EDGE,"E276"),sQuery(id+"F0.wireOp",EDGE,"E277"),sQuery(id+"F0.wireOp",EDGE,"E278"),sQuery(id+"F0.wireOp",EDGE,"E279"),sQuery(id+"F0.wireOp",EDGE,"E280"),sQuery(id+"F0.wireOp",EDGE,"E281"),sQuery(id+"F0.wireOp",EDGE,"E282"),sQuery(id+"F0.wireOp",EDGE,"E283"),sQuery(id+"F0.wireOp",EDGE,"E284"),sQuery(id+"F0.wireOp",EDGE,"E285"),sQuery(id+"F0.wireOp",EDGE,"E286"),sQuery(id+"F0.wireOp",EDGE,"E287"),sQuery(id+"F0.wireOp",EDGE,"E288"),sQuery(id+"F0.wireOp",EDGE,"E289"),sQuery(id+"F0.wireOp",EDGE,"E290"),sQuery(id+"F0.wireOp",EDGE,"E291"),sQuery(id+"F0.wireOp",EDGE,"E292"),sQuery(id+"F0.wireOp",EDGE,"E293"),sQuery(id+"F0.wireOp",EDGE,"E294"),sQuery(id+"F0.wireOp",EDGE,"E295"),sQuery(id+"F0.wireOp",EDGE,"E296"),sQuery(id+"F0.wireOp",EDGE,"E297"),sQuery(id+"F0.wireOp",EDGE,"E298"),sQuery(id+"F0.wireOp",EDGE,"E299"),sQuery(id+"F0.wireOp",EDGE,"E300"),sQuery(id+"F0.wireOp",EDGE,"E301"),sQuery(id+"F0.wireOp",EDGE,"E302"),sQuery(id+"F0.wireOp",EDGE,"E303"),sQuery(id+"F0.wireOp",EDGE,"E304"),sQuery(id+"F0.wireOp",EDGE,"E305"),sQuery(id+"F0.wireOp",EDGE,"E306"),sQuery(id+"F0.wireOp",EDGE,"E307"),sQuery(id+"F0.wireOp",EDGE,"E308"),sQuery(id+"F0.wireOp",EDGE,"E309"),sQuery(id+"F0.wireOp",EDGE,"E310"),sQuery(id+"F0.wireOp",EDGE,"E311"),sQuery(id+"F0.wireOp",EDGE,"E312"),sQuery(id+"F0.wireOp",EDGE,"E313"),sQuery(id+"F0.wireOp",EDGE,"E314"),sQuery(id+"F0.wireOp",EDGE,"E315"),sQuery(id+"F0.wireOp",EDGE,"E316"),sQuery(id+"F0.wireOp",EDGE,"E317"),sQuery(id+"F0.wireOp",EDGE,"E318"),sQuery(id+"F0.wireOp",EDGE,"E319"),sQuery(id+"F0.wireOp",EDGE,"E320"),sQuery(id+"F0.wireOp",EDGE,"E321"),sQuery(id+"F0.wireOp",EDGE,"E322"),sQuery(id+"F0.wireOp",EDGE,"E323"),sQuery(id+"F0.wireOp",EDGE,"E324"),sQuery(id+"F0.wireOp",EDGE,"E325"),sQuery(id+"F0.wireOp",EDGE,"E326"),sQuery(id+"F0.wireOp",EDGE,"E327"),sQuery(id+"F0.wireOp",EDGE,"E328"),sQuery(id+"F0.wireOp",EDGE,"E329"),sQuery(id+"F0.wireOp",EDGE,"E330"),sQuery(id+"F0.wireOp",EDGE,"E331"),sQuery(id+"F0.wireOp",EDGE,"E332"),sQuery(id+"F0.wireOp",EDGE,"E333"),sQuery(id+"F0.wireOp",EDGE,"E334"),sQuery(id+"F0.wireOp",EDGE,"E335"),sQuery(id+"F0.wireOp",EDGE,"E336"),sQuery(id+"F0.wireOp",EDGE,"E337"),sQuery(id+"F0.wireOp",EDGE,"E338"),sQuery(id+"F0.wireOp",EDGE,"E339"),sQuery(id+"F0.wireOp",EDGE,"E340"),sQuery(id+"F0.wireOp",EDGE,"E341"),sQuery(id+"F0.wireOp",EDGE,"E342"),sQuery(id+"F0.wireOp",EDGE,"E343"),sQuery(id+"F0.wireOp",EDGE,"E344"),sQuery(id+"F0.wireOp",EDGE,"E345"),sQuery(id+"F0.wireOp",EDGE,"E346"),sQuery(id+"F0.wireOp",EDGE,"E347"),sQuery(id+"F0.wireOp",EDGE,"E348"),sQuery(id+"F0.wireOp",EDGE,"E349"),sQuery(id+"F0.wireOp",EDGE,"E350"),sQuery(id+"F0.wireOp",EDGE,"E351"),sQuery(id+"F0.wireOp",EDGE,"E352"),sQuery(id+"F0.wireOp",EDGE,"E353"),sQuery(id+"F0.wireOp",EDGE,"E354"),sQuery(id+"F0.wireOp",EDGE,"E355"),sQuery(id+"F0.wireOp",EDGE,"E356"),sQuery(id+"F0.wireOp",EDGE,"E357"),sQuery(id+"F0.wireOp",EDGE,"E358"),sQuery(id+"F0.wireOp",EDGE,"E359"),sQuery(id+"F0.wireOp",EDGE,"E360"),sQuery(id+"F0.wireOp",EDGE,"E361"),sQuery(id+"F0.wireOp",EDGE,"E362"),sQuery(id+"F0.wireOp",EDGE,"E363"),sQuery(id+"F0.wireOp",EDGE,"E364"),sQuery(id+"F0.wireOp",EDGE,"E365"),sQuery(id+"F0.wireOp",EDGE,"E366"),sQuery(id+"F0.wireOp",EDGE,"E367"),sQuery(id+"F0.wireOp",EDGE,"E368"),sQuery(id+"F0.wireOp",EDGE,"E369"),sQuery(id+"F0.wireOp",EDGE,"E370"),sQuery(id+"F0.wireOp",EDGE,"E371"),sQuery(id+"F0.wireOp",EDGE,"E372"),sQuery(id+"F0.wireOp",EDGE,"E373"),sQuery(id+"F0.wireOp",EDGE,"E374"),sQuery(id+"F0.wireOp",EDGE,"E375"),sQuery(id+"F0.wireOp",EDGE,"E376"),sQuery(id+"F0.wireOp",EDGE,"E377"),sQuery(id+"F0.wireOp",EDGE,"E378"),sQuery(id+"F0.wireOp",EDGE,"E379"),sQuery(id+"F0.wireOp",EDGE,"E380"),sQuery(id+"F0.wireOp",EDGE,"E381"),sQuery(id+"F0.wireOp",EDGE,"E382"),sQuery(id+"F0.wireOp",EDGE,"E383"),sQuery(id+"F0.wireOp",EDGE,"E384"),sQuery(id+"F0.wireOp",EDGE,"E385"),sQuery(id+"F0.wireOp",EDGE,"E386"),sQuery(id+"F0.wireOp",EDGE,"E387"),sQuery(id+"F0.wireOp",EDGE,"E388"),sQuery(id+"F0.wireOp",EDGE,"E389"),sQuery(id+"F0.wireOp",EDGE,"E390"),sQuery(id+"F0.wireOp",EDGE,"E391"),sQuery(id+"F0.wireOp",EDGE,"E392"),sQuery(id+"F0.wireOp",EDGE,"E393"),sQuery(id+"F0.wireOp",EDGE,"E394"),sQuery(id+"F0.wireOp",EDGE,"E395"),sQuery(id+"F0.wireOp",EDGE,"E396"),sQuery(id+"F0.wireOp",EDGE,"E397"),sQuery(id+"F0.wireOp",EDGE,"E398"),sQuery(id+"F0.wireOp",EDGE,"E399"),sQuery(id+"F0.wireOp",EDGE,"E400"),sQuery(id+"F0.wireOp",EDGE,"E401"),sQuery(id+"F0.wireOp",EDGE,"E402"),sQuery(id+"F0.wireOp",EDGE,"E403"),sQuery(id+"F0.wireOp",EDGE,"E404"),sQuery(id+"F0.wireOp",EDGE,"E405"),sQuery(id+"F0.wireOp",EDGE,"E406"),sQuery(id+"F0.wireOp",EDGE,"E407"),sQuery(id+"F0.wireOp",EDGE,"E408"),sQuery(id+"F0.wireOp",EDGE,"E409"),sQuery(id+"F0.wireOp",EDGE,"E410"),sQuery(id+"F0.wireOp",EDGE,"E411"),sQuery(id+"F0.wireOp",EDGE,"E412"),sQuery(id+"F0.wireOp",EDGE,"E413"),sQuery(id+"F0.wireOp",EDGE,"E414"),sQuery(id+"F0.wireOp",EDGE,"E415"),sQuery(id+"F0.wireOp",EDGE,"E416"),sQuery(id+"F0.wireOp",EDGE,"E417"),sQuery(id+"F0.wireOp",EDGE,"E418"),sQuery(id+"F0.wireOp",EDGE,"E419"),sQuery(id+"F0.wireOp",EDGE,"E420"),sQuery(id+"F0.wireOp",EDGE,"E421"),sQuery(id+"F0.wireOp",EDGE,"E422"),sQuery(id+"F0.wireOp",EDGE,"E423"),sQuery(id+"F0.wireOp",EDGE,"E424"),sQuery(id+"F0.wireOp",EDGE,"E425"),sQuery(id+"F0.wireOp",EDGE,"E426"),sQuery(id+"F0.wireOp",EDGE,"E427"),sQuery(id+"F0.wireOp",EDGE,"E428"),sQuery(id+"F0.wireOp",EDGE,"E429"),sQuery(id+"F0.wireOp",EDGE,"E430"),sQuery(id+"F0.wireOp",EDGE,"E431"),sQuery(id+"F0.wireOp",EDGE,"E432"),sQuery(id+"F0.wireOp",EDGE,"E433"),sQuery(id+"F0.wireOp",EDGE,"E434"),sQuery(id+"F0.wireOp",EDGE,"E435"),sQuery(id+"F0.wireOp",EDGE,"E436"),sQuery(id+"F0.wireOp",EDGE,"E437"),sQuery(id+"F0.wireOp",EDGE,"E438"),sQuery(id+"F0.wireOp",EDGE,"E439"),sQuery(id+"F0.wireOp",EDGE,"E440"),sQuery(id+"F0.wireOp",EDGE,"E441"),sQuery(id+"F0.wireOp",EDGE,"E442"),sQuery(id+"F0.wireOp",EDGE,"E443"),sQuery(id+"F0.wireOp",EDGE,"E444"),sQuery(id+"F0.wireOp",EDGE,"E445"),sQuery(id+"F0.wireOp",EDGE,"E446"),sQuery(id+"F0.wireOp",EDGE,"E447"),sQuery(id+"F0.wireOp",EDGE,"E448"),sQuery(id+"F0.wireOp",EDGE,"E449"),sQuery(id+"F0.wireOp",EDGE,"E450"),sQuery(id+"F0.wireOp",EDGE,"E451"),sQuery(id+"F0.wireOp",EDGE,"E452"),sQuery(id+"F0.wireOp",EDGE,"E453"),sQuery(id+"F0.wireOp",EDGE,"E454"),sQuery(id+"F0.wireOp",EDGE,"E455"),sQuery(id+"F0.wireOp",EDGE,"E456"),sQuery(id+"F0.wireOp",EDGE,"E457"),sQuery(id+"F0.wireOp",EDGE,"E458"),sQuery(id+"F0.wireOp",EDGE,"E459"),sQuery(id+"F0.wireOp",EDGE,"E460"),sQuery(id+"F0.wireOp",EDGE,"E461"),sQuery(id+"F0.wireOp",EDGE,"E462"),sQuery(id+"F0.wireOp",EDGE,"E463"),sQuery(id+"F0.wireOp",EDGE,"E464"),sQuery(id+"F0.wireOp",EDGE,"E465"),sQuery(id+"F0.wireOp",EDGE,"E466"),sQuery(id+"F0.wireOp",EDGE,"E467"),sQuery(id+"F0.wireOp",EDGE,"E468"),sQuery(id+"F0.wireOp",EDGE,"E469"),sQuery(id+"F0.wireOp",EDGE,"E470"),sQuery(id+"F0.wireOp",EDGE,"E471"),sQuery(id+"F0.wireOp",EDGE,"E472"),sQuery(id+"F0.wireOp",EDGE,"E473"),sQuery(id+"F0.wireOp",EDGE,"E474"),sQuery(id+"F0.wireOp",EDGE,"E475"),sQuery(id+"F0.wireOp",EDGE,"E476"),sQuery(id+"F0.wireOp",EDGE,"E477"),sQuery(id+"F0.wireOp",EDGE,"E478"),sQuery(id+"F0.wireOp",EDGE,"E479"),sQuery(id+"F0.wireOp",EDGE,"E480"),sQuery(id+"F0.wireOp",EDGE,"E481"),sQuery(id+"F0.wireOp",EDGE,"E482"),sQuery(id+"F0.wireOp",EDGE,"E483"),sQuery(id+"F0.wireOp",EDGE,"E484"),sQuery(id+"F0.wireOp",EDGE,"E485"),sQuery(id+"F0.wireOp",EDGE,"E486"),sQuery(id+"F0.wireOp",EDGE,"E487"),sQuery(id+"F0.wireOp",EDGE,"E488"),sQuery(id+"F0.wireOp",EDGE,"E489"),sQuery(id+"F0.wireOp",EDGE,"E490"),sQuery(id+"F0.wireOp",EDGE,"E491"),sQuery(id+"F0.wireOp",EDGE,"E492"),sQuery(id+"F0.wireOp",EDGE,"E493"),sQuery(id+"F0.wireOp",EDGE,"E494"),sQuery(id+"F0.wireOp",EDGE,"E495"),sQuery(id+"F0.wireOp",EDGE,"E496"),sQuery(id+"F0.wireOp",EDGE,"E497"),sQuery(id+"F0.wireOp",EDGE,"E498"),sQuery(id+"F0.wireOp",EDGE,"E499"),sQuery(id+"F0.wireOp",EDGE,"E500"),sQuery(id+"F0.wireOp",EDGE,"E501"),sQuery(id+"F0.wireOp",EDGE,"E502"),sQuery(id+"F0.wireOp",EDGE,"E503"),sQuery(id+"F0.wireOp",EDGE,"E504"),sQuery(id+"F0.wireOp",EDGE,"E505"),sQuery(id+"F0.wireOp",EDGE,"E506"),sQuery(id+"F0.wireOp",EDGE,"E507"),sQuery(id+"F0.wireOp",EDGE,"E508"),sQuery(id+"F0.wireOp",EDGE,"E509"),sQuery(id+"F0.wireOp",EDGE,"E510"),sQuery(id+"F0.wireOp",EDGE,"E511"),sQuery(id+"F0.wireOp",EDGE,"E512"),sQuery(id+"F0.wireOp",EDGE,"E513"),sQuery(id+"F0.wireOp",EDGE,"E514"),sQuery(id+"F0.wireOp",EDGE,"E515"),sQuery(id+"F0.wireOp",EDGE,"E516"),sQuery(id+"F0.wireOp",EDGE,"E517"),sQuery(id+"F0.wireOp",EDGE,"E518"),sQuery(id+"F0.wireOp",EDGE,"E519"),sQuery(id+"F0.wireOp",EDGE,"E520"),sQuery(id+"F0.wireOp",EDGE,"E521"),sQuery(id+"F0.wireOp",EDGE,"E522"),sQuery(id+"F0.wireOp",EDGE,"E523"),sQuery(id+"F0.wireOp",EDGE,"E524"),sQuery(id+"F0.wireOp",EDGE,"E525"),sQuery(id+"F0.wireOp",EDGE,"E526"),sQuery(id+"F0.wireOp",EDGE,"E527"),sQuery(id+"F0.wireOp",EDGE,"E528"),sQuery(id+"F0.wireOp",EDGE,"E529"),sQuery(id+"F0.wireOp",EDGE,"E530"),sQuery(id+"F0.wireOp",EDGE,"E531"),sQuery(id+"F0.wireOp",EDGE,"E532"),sQuery(id+"F0.wireOp",EDGE,"E533"),sQuery(id+"F0.wireOp",EDGE,"E534"),sQuery(id+"F0.wireOp",EDGE,"E535"),sQuery(id+"F0.wireOp",EDGE,"E536"),sQuery(id+"F0.wireOp",EDGE,"E537"),sQuery(id+"F0.wireOp",EDGE,"E538"),sQuery(id+"F0.wireOp",EDGE,"E539"),sQuery(id+"F0.wireOp",EDGE,"E540"),sQuery(id+"F0.wireOp",EDGE,"E541"),sQuery(id+"F0.wireOp",EDGE,"E542"),sQuery(id+"F0.wireOp",EDGE,"E543"),sQuery(id+"F0.wireOp",EDGE,"E544"),sQuery(id+"F0.wireOp",EDGE,"E545"),sQuery(id+"F0.wireOp",EDGE,"E546"),sQuery(id+"F0.wireOp",EDGE,"E547"),sQuery(id+"F0.wireOp",EDGE,"E548"),sQuery(id+"F0.wireOp",EDGE,"E549"),sQuery(id+"F0.wireOp",EDGE,"E550"),sQuery(id+"F0.wireOp",EDGE,"E551"),sQuery(id+"F0.wireOp",EDGE,"E552"),sQuery(id+"F0.wireOp",EDGE,"E553"),sQuery(id+"F0.wireOp",EDGE,"E554"),sQuery(id+"F0.wireOp",EDGE,"E554"),sQuery(id+"F0.wireOp",EDGE,"E555"),sQuery(id+"F0.wireOp",EDGE,"E556"),sQuery(id+"F0.wireOp",EDGE,"E557"),sQuery(id+"F0.wireOp",EDGE,"E558"),sQuery(id+"F0.wireOp",EDGE,"E559"),sQuery(id+"F0.wireOp",EDGE,"E560"),sQuery(id+"F0.wireOp",EDGE,"E561"),sQuery(id+"F0.wireOp",EDGE,"E562"),sQuery(id+"F0.wireOp",EDGE,"E563"),sQuery(id+"F0.wireOp",EDGE,"E564"),sQuery(id+"F0.wireOp",EDGE,"E565"),sQuery(id+"F0.wireOp",EDGE,"E566"),sQuery(id+"F0.wireOp",EDGE,"E567"),sQuery(id+"F0.wireOp",EDGE,"E568"),sQuery(id+"F0.wireOp",EDGE,"E569"),sQuery(id+"F0.wireOp",EDGE,"E570"),sQuery(id+"F0.wireOp",EDGE,"E571"),sQuery(id+"F0.wireOp",EDGE,"E572"),sQuery(id+"F0.wireOp",EDGE,"E573"),sQuery(id+"F0.wireOp",EDGE,"E574"),sQuery(id+"F0.wireOp",EDGE,"E575"),sQuery(id+"F0.wireOp",EDGE,"E576"),sQuery(id+"F0.wireOp",EDGE,"E577"),sQuery(id+"F0.wireOp",EDGE,"E578"),sQuery(id+"F0.wireOp",EDGE,"E579"),sQuery(id+"F0.wireOp",EDGE,"E580"),sQuery(id+"F0.wireOp",EDGE,"E581"),sQuery(id+"F0.wireOp",EDGE,"E582"),sQuery(id+"F0.wireOp",EDGE,"E583"),sQuery(id+"F0.wireOp",EDGE,"E584"),sQuery(id+"F0.wireOp",EDGE,"E585"),sQuery(id+"F0.wireOp",EDGE,"E586"),sQuery(id+"F0.wireOp",EDGE,"E587"),sQuery(id+"F0.wireOp",EDGE,"E588"),sQuery(id+"F0.wireOp",EDGE,"E589"),sQuery(id+"F0.wireOp",EDGE,"E590"),sQuery(id+"F0.wireOp",EDGE,"E591"),sQuery(id+"F0.wireOp",EDGE,"E592"),sQuery(id+"F0.wireOp",EDGE,"E593"),sQuery(id+"F0.wireOp",EDGE,"E594"),sQuery(id+"F0.wireOp",EDGE,"E595"),sQuery(id+"F0.wireOp",EDGE,"E596"),sQuery(id+"F0.wireOp",EDGE,"E597"),sQuery(id+"F0.wireOp",EDGE,"E598"),sQuery(id+"F0.wireOp",EDGE,"E599"),sQuery(id+"F0.wireOp",EDGE,"E600"),sQuery(id+"F0.wireOp",EDGE,"E601"),sQuery(id+"F0.wireOp",EDGE,"E602"),sQuery(id+"F0.wireOp",EDGE,"E603"),sQuery(id+"F0.wireOp",EDGE,"E604"),sQuery(id+"F0.wireOp",EDGE,"E605"),sQuery(id+"F0.wireOp",EDGE,"E606"),sQuery(id+"F0.wireOp",EDGE,"E607"),sQuery(id+"F0.wireOp",EDGE,"E608"),sQuery(id+"F0.wireOp",EDGE,"E609"),sQuery(id+"F0.wireOp",EDGE,"E610"),sQuery(id+"F0.wireOp",EDGE,"E611"),sQuery(id+"F0.wireOp",EDGE,"E612"),sQuery(id+"F0.wireOp",EDGE,"E613"),sQuery(id+"F0.wireOp",EDGE,"E614"),sQuery(id+"F0.wireOp",EDGE,"E615"),sQuery(id+"F0.wireOp",EDGE,"E616"),sQuery(id+"F0.wireOp",EDGE,"E617"),sQuery(id+"F0.wireOp",EDGE,"E618"),sQuery(id+"F0.wireOp",EDGE,"E619"),sQuery(id+"F0.wireOp",EDGE,"E620"),sQuery(id+"F0.wireOp",EDGE,"E621"),sQuery(id+"F0.wireOp",EDGE,"E622"),sQuery(id+"F0.wireOp",EDGE,"E623"),sQuery(id+"F0.wireOp",EDGE,"E624"),sQuery(id+"F0.wireOp",EDGE,"E625"),sQuery(id+"F0.wireOp",EDGE,"E626"),sQuery(id+"F0.wireOp",EDGE,"E627"),sQuery(id+"F0.wireOp",EDGE,"E628"),sQuery(id+"F0.wireOp",EDGE,"E629"),sQuery(id+"F0.wireOp",EDGE,"E630"),sQuery(id+"F0.wireOp",EDGE,"E631"),sQuery(id+"F0.wireOp",EDGE,"E632"),sQuery(id+"F0.wireOp",EDGE,"E633"),sQuery(id+"F0.wireOp",EDGE,"E634"),sQuery(id+"F0.wireOp",EDGE,"E635"),sQuery(id+"F0.wireOp",EDGE,"E636"),sQuery(id+"F0.wireOp",EDGE,"E637"),sQuery(id+"F0.wireOp",EDGE,"E638"),sQuery(id+"F0.wireOp",EDGE,"E639"),sQuery(id+"F0.wireOp",EDGE,"E640"),sQuery(id+"F0.wireOp",EDGE,"E641"),sQuery(id+"F0.wireOp",EDGE,"E642"),sQuery(id+"F0.wireOp",EDGE,"E643"),sQuery(id+"F0.wireOp",EDGE,"E644"),sQuery(id+"F0.wireOp",EDGE,"E645"),sQuery(id+"F0.wireOp",EDGE,"E646"),sQuery(id+"F0.wireOp",EDGE,"E647"),sQuery(id+"F0.wireOp",EDGE,"E648"),sQuery(id+"F0.wireOp",EDGE,"E649"),sQuery(id+"F0.wireOp",EDGE,"E650"),sQuery(id+"F0.wireOp",EDGE,"E651"),sQuery(id+"F0.wireOp",EDGE,"E652"),sQuery(id+"F0.wireOp",EDGE,"E653"),sQuery(id+"F0.wireOp",EDGE,"E654"),sQuery(id+"F0.wireOp",EDGE,"E655"),sQuery(id+"F0.wireOp",EDGE,"E656"),sQuery(id+"F0.wireOp",EDGE,"E657"),sQuery(id+"F0.wireOp",EDGE,"E658"),sQuery(id+"F0.wireOp",EDGE,"E659"),sQuery(id+"F0.wireOp",EDGE,"E660"),sQuery(id+"F0.wireOp",EDGE,"E661"),sQuery(id+"F0.wireOp",EDGE,"E662"),sQuery(id+"F0.wireOp",EDGE,"E663"),sQuery(id+"F0.wireOp",EDGE,"E664")])],"isStart":false});
            var sketch = newSketch(context, id + "F3", { "sketchPlane" : qUnion([Q0])});
            skCircle(sketch, "E3931", {"center": v(-40.63, 1.24) * mm, "radius": 37 * mm});
            skPoint(sketch, "E3931.first.point", {"position": v(-60.41, 32.51) * mm});
            skPoint(sketch, "E3931.second.point", {"position": v(-3.9, 5.78) * mm});
            skPoint(sketch, "E3931.third.point", {"position": v(-56.44, -32.2) * mm});
            skLineSegment(sketch, "E3932.bottom", {"start": v(-52.5, 7.8) * mm, "end": v(-28.76, 7.8) * mm});
            skLineSegment(sketch, "E3932.top", {"start": v(-52.5, -5.07) * mm, "end": v(-28.76, -5.07) * mm});
            skLineSegment(sketch, "E3932.left", {"start": v(-52.5, 7.8) * mm, "end": v(-52.5, -5.07) * mm});
            skLineSegment(sketch, "E3932.right", {"start": v(-28.76, 7.8) * mm, "end": v(-28.76, -5.07) * mm});
            skCircle(sketch, "E3933", {"center": v(-50.63, -15.76) * mm, "radius": 2 * mm});
            skPoint(sketch, "E3933.first.point", {"position": v(-51.65, -14.05) * mm});
            skPoint(sketch, "E3933.second.point", {"position": v(-48.75, -15.08) * mm});
            skPoint(sketch, "E3933.third.point", {"position": v(-51.3, -17.63) * mm});
            skCircle(sketch, "E3934", {"center": v(-30.63, -15.76) * mm, "radius": 2 * mm});
            skPoint(sketch, "E3934.first.point", {"position": v(-32.23, -14.57) * mm});
            skPoint(sketch, "E3934.second.point", {"position": v(-28.75, -15.08) * mm});
            skPoint(sketch, "E3934.third.point", {"position": v(-30.63, -17.76) * mm});
            skSolve(sketch);
        }
        {
            var Q0;
            Q0=makeQuery(id+"F3.imprint","IMPRINT",FACE,{"disambiguationData":[TD([[makeQuery(id+"F3.imprint","IMPRINT",EDGE,{"derivedFrom":sQuery(id+"F3.wireOp",EDGE,"E3932.bottom")}),1.0]])]});
            var Q1;
            Q1=makeQuery(id+"F3.imprint","IMPRINT",FACE,{"disambiguationData":[TD([[makeQuery(id+"F3.imprint","IMPRINT",EDGE,{"derivedFrom":sQuery(id+"F3.wireOp",EDGE,"E3932.bottom")}),1.0]])]});
            extrude(context, id + "F4", {"entities" : qUnion([Q0, Q1]), "depth" : 25 * mm});
        }
    });
